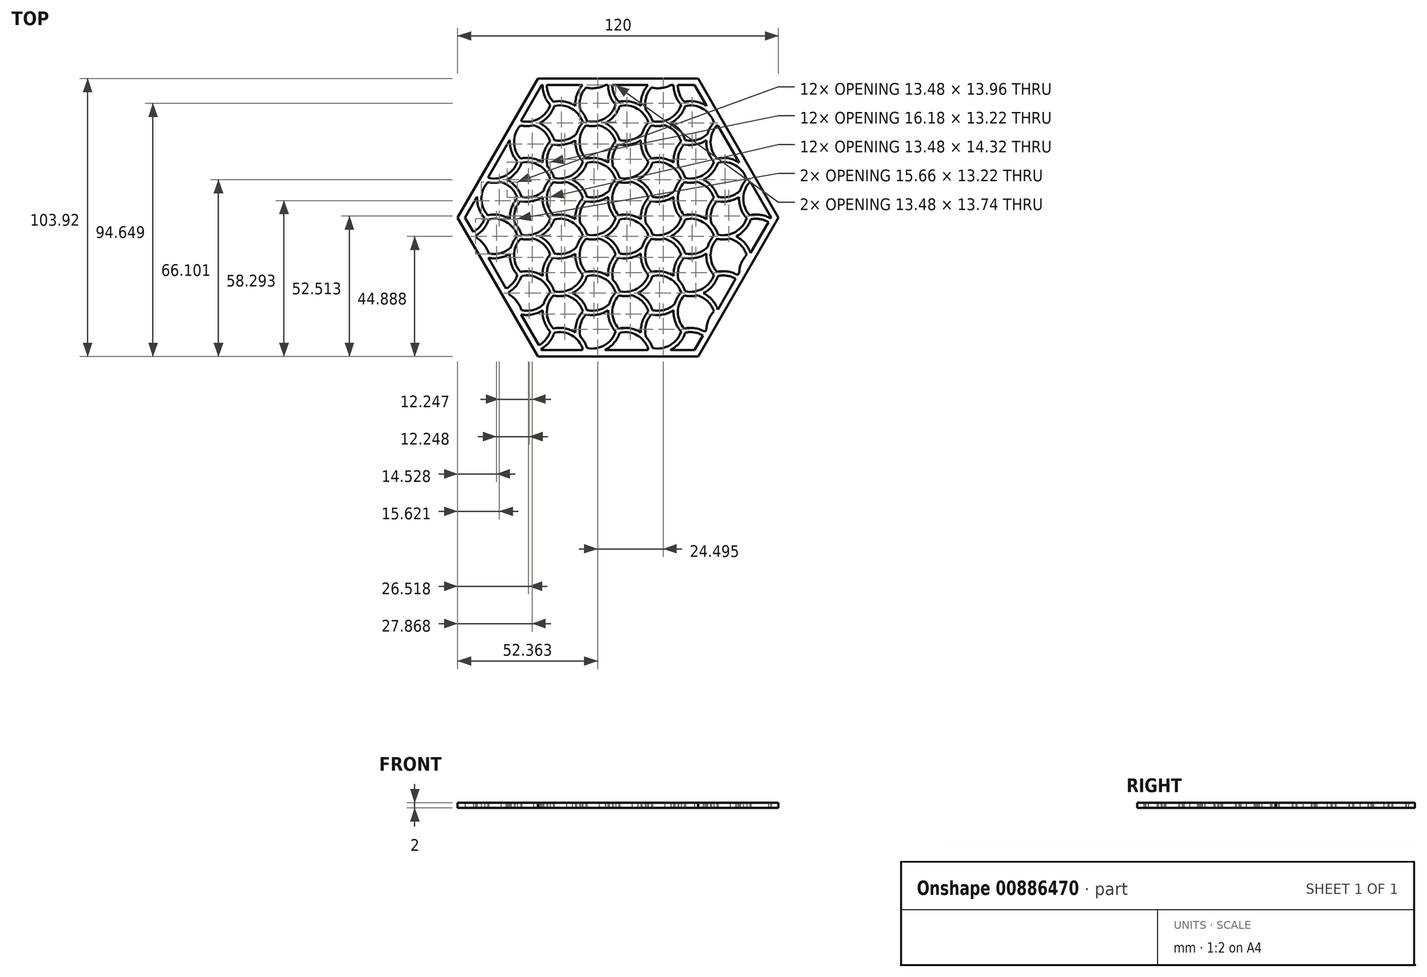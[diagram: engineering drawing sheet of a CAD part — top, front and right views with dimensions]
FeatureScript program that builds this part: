
annotation { "Feature Type Name" : "Feature", "Feature Type Description" : "" }
export const myFeature = defineFeature(function(context is Context, id is Id, definition is map)
    precondition{}
    {
        {
            var Q0;
            Q0=qCreatedBy(makeId("Top.planeOp"),FACE);
            var sketch = newSketch(context, id + "F0", { "sketchPlane" : qUnion([Q0])});
            skArc(sketch, "E0", {"start": v(0, 0) * mm, "mid": v(4.53, -0.15) * mm, "end": v(8.65, 1.7) * mm});
            skPoint(sketch, "E1.center", {"position": v(0, 0) * mm});
            skArc(sketch, "E2.1.0", {"start": v(0, 0) * mm, "mid": v(-2.13, 4) * mm, "end": v(-5.8, 6.64) * mm});
            skArc(sketch, "E2.2.0", {"start": v(0, 0) * mm, "mid": v(-2.4, -3.84) * mm, "end": v(-2.85, -8.35) * mm});
            skArc(sketch, "E3.1.0.0", {"start": v(12.25, 7.07) * mm, "mid": v(7.59, 13.14) * mm, "end": v(0, 14.14) * mm});
            skArc(sketch, "E3.1.0.2", {"start": v(12.25, 7.07) * mm, "mid": v(9.32, 0) * mm, "end": v(12.25, -7.07) * mm});
            skArc(sketch, "E4.1.0", {"start": v(-12.25, 7.07) * mm, "mid": v(-15.18, 0) * mm, "end": v(-12.25, -7.07) * mm});
            skArc(sketch, "E4.1.2", {"start": v(-12.25, 7.07) * mm, "mid": v(-4.66, 8.07) * mm, "end": v(0, 14.14) * mm});
            skArc(sketch, "E4.2.0", {"start": v(0, -14.14) * mm, "mid": v(7.59, -13.14) * mm, "end": v(12.25, -7.07) * mm});
            skArc(sketch, "E4.2.2", {"start": v(0, -14.14) * mm, "mid": v(-4.66, -8.07) * mm, "end": v(-12.25, -7.07) * mm});
            skPoint(sketch, "E4.center", {"position": v(-0.04, -0.07) * mm});
            skPoint(sketch, "E5.orphan", {"position": v(-12.25, 7.07) * mm});
            skPoint(sketch, "E6.orphan", {"position": v(0, -14.14) * mm});
            skLineSegment(sketch, "E7", {"start": v(0, 0) * mm, "end": v(9.66, 2.59) * mm, "construction": true});
            skLineSegment(sketch, "E8", {"start": v(0, 0) * mm, "end": v(-14.4, -3.86) * mm, "construction": true});
            skArc(sketch, "E9.0", {"start": v(-11.99, 6.18) * mm, "mid": v(-14.38, 0) * mm, "end": v(-11.99, -6.18) * mm});
            skArc(sketch, "E9.1", {"start": v(11.35, 7.29) * mm, "mid": v(7.19, 12.45) * mm, "end": v(0.64, 13.47) * mm});
            skArc(sketch, "E9.2", {"start": v(11.35, 7.29) * mm, "mid": v(8.52, 0) * mm, "end": v(11.35, -7.29) * mm});
            skArc(sketch, "E9.3", {"start": v(-11.99, 6.18) * mm, "mid": v(-4.26, 7.38) * mm, "end": v(0.64, 13.47) * mm});
            skArc(sketch, "E9.4", {"start": v(0.64, -13.47) * mm, "mid": v(7.19, -12.45) * mm, "end": v(11.35, -7.29) * mm});
            skArc(sketch, "E9.5", {"start": v(0.64, -13.47) * mm, "mid": v(-4.26, -7.38) * mm, "end": v(-11.99, -6.18) * mm});
            skArc(sketch, "E10.0", {"start": v(0.64, 0.67) * mm, "mid": v(-1.45, 4.42) * mm, "end": v(-4.83, 7.07) * mm});
            skArc(sketch, "E10.1", {"start": v(0.64, 0.67) * mm, "mid": v(5.08, 0.8) * mm, "end": v(8.95, 3.01) * mm});
            skArc(sketch, "E11.0", {"start": v(-0.9, 0.22) * mm, "mid": v(-3.24, 4) * mm, "end": v(-7.08, 6.24) * mm});
            skArc(sketch, "E11.1", {"start": v(-0.9, 0.22) * mm, "mid": v(-3.1, -3.46) * mm, "end": v(-3.7, -7.72) * mm});
            skArc(sketch, "E12.0", {"start": v(0.26, -0.89) * mm, "mid": v(4.55, -0.96) * mm, "end": v(8.54, 0.65) * mm});
            skArc(sketch, "E12.1", {"start": v(0.26, -0.89) * mm, "mid": v(-1.85, -4.8) * mm, "end": v(-1.87, -9.25) * mm});
            skArc(sketch, "E13.1.0.0", {"start": v(25.13, -13.47) * mm, "mid": v(20.24, -7.38) * mm, "end": v(12.5, -6.18) * mm});
            skArc(sketch, "E13.1.0.1", {"start": v(36.74, 7.07) * mm, "mid": v(32.08, 13.14) * mm, "end": v(24.5, 14.14) * mm});
            skArc(sketch, "E13.1.0.2", {"start": v(24.5, -14.14) * mm, "mid": v(19.84, -8.07) * mm, "end": v(12.25, -7.07) * mm});
            skArc(sketch, "E13.1.0.3", {"start": v(12.5, 6.18) * mm, "mid": v(10.12, 0) * mm, "end": v(12.5, -6.18) * mm});
            skArc(sketch, "E13.1.0.4", {"start": v(12.25, 7.07) * mm, "mid": v(19.84, 8.07) * mm, "end": v(24.5, 14.14) * mm});
            skArc(sketch, "E13.1.0.5", {"start": v(35.84, 7.29) * mm, "mid": v(31.68, 12.45) * mm, "end": v(25.13, 13.47) * mm});
            skArc(sketch, "E13.1.0.6", {"start": v(23.6, 0.22) * mm, "mid": v(21.26, 4) * mm, "end": v(17.41, 6.24) * mm});
            skArc(sketch, "E13.1.0.7", {"start": v(24.5, 0) * mm, "mid": v(22.1, -3.84) * mm, "end": v(21.65, -8.35) * mm});
            skPoint(sketch, "E13.1.0.8", {"position": v(12.25, 7.07) * mm});
            skArc(sketch, "E13.1.0.9", {"start": v(24.5, -14.14) * mm, "mid": v(32.08, -13.14) * mm, "end": v(36.74, -7.07) * mm});
            skLineSegment(sketch, "E13.1.0.10", {"start": v(24.5, 0) * mm, "end": v(34.15, 2.59) * mm, "construction": true});
            skArc(sketch, "E13.1.0.11", {"start": v(24.5, 0) * mm, "mid": v(22.36, 4) * mm, "end": v(18.69, 6.64) * mm});
            skArc(sketch, "E13.1.0.12", {"start": v(12.5, 6.18) * mm, "mid": v(20.24, 7.38) * mm, "end": v(25.13, 13.47) * mm});
            skArc(sketch, "E13.1.0.13", {"start": v(25.13, 0.67) * mm, "mid": v(29.58, 0.8) * mm, "end": v(33.44, 3.01) * mm});
            skArc(sketch, "E13.1.0.14", {"start": v(35.84, 7.29) * mm, "mid": v(33.01, 0) * mm, "end": v(35.84, -7.29) * mm});
            skArc(sketch, "E13.1.0.15", {"start": v(24.5, 0) * mm, "mid": v(29.02, -0.15) * mm, "end": v(33.15, 1.7) * mm});
            skArc(sketch, "E13.1.0.16", {"start": v(36.74, 7.07) * mm, "mid": v(33.81, 0) * mm, "end": v(36.74, -7.07) * mm});
            skArc(sketch, "E13.1.0.17", {"start": v(25.13, -13.47) * mm, "mid": v(31.68, -12.45) * mm, "end": v(35.84, -7.29) * mm});
            skArc(sketch, "E13.1.0.18", {"start": v(25.13, 0.67) * mm, "mid": v(23.05, 4.42) * mm, "end": v(19.67, 7.07) * mm});
            skArc(sketch, "E13.1.0.19", {"start": v(24.75, -0.89) * mm, "mid": v(29.05, -0.96) * mm, "end": v(33.03, 0.65) * mm});
            skArc(sketch, "E13.1.0.21", {"start": v(24.75, -0.89) * mm, "mid": v(22.65, -4.8) * mm, "end": v(22.63, -9.25) * mm});
            skArc(sketch, "E13.1.0.22", {"start": v(23.6, 0.22) * mm, "mid": v(21.39, -3.46) * mm, "end": v(20.79, -7.72) * mm});
            skLineSegment(sketch, "E13.1.0.23", {"start": v(24.5, 0) * mm, "end": v(10.1, -3.86) * mm, "construction": true});
            skPoint(sketch, "E13.1.0.24", {"position": v(24.5, 0) * mm});
            skPoint(sketch, "E13.1.0.25", {"position": v(24.5, -14.14) * mm});
            skPoint(sketch, "E13.1.0.26", {"position": v(24.46, -0.07) * mm});
            skPoint(sketch, "E13.1.0.27", {"position": v(24.5, 0) * mm});
            skPoint(sketch, "E13.1.0.28", {"position": v(24.5, 0) * mm});
            skPoint(sketch, "E13.1.0.29", {"position": v(24.5, 0) * mm});
            skArc(sketch, "E13.2.0.0", {"start": v(49.63, -13.47) * mm, "mid": v(44.73, -7.38) * mm, "end": v(37, -6.18) * mm});
            skArc(sketch, "E13.2.0.1", {"start": v(61.24, 7.07) * mm, "mid": v(56.58, 13.14) * mm, "end": v(48.99, 14.14) * mm});
            skArc(sketch, "E13.2.0.2", {"start": v(48.99, -14.14) * mm, "mid": v(44.33, -8.07) * mm, "end": v(36.74, -7.07) * mm});
            skArc(sketch, "E13.2.0.3", {"start": v(37, 6.18) * mm, "mid": v(34.61, 0) * mm, "end": v(37, -6.18) * mm});
            skArc(sketch, "E13.2.0.4", {"start": v(36.74, 7.07) * mm, "mid": v(44.33, 8.07) * mm, "end": v(48.99, 14.14) * mm});
            skArc(sketch, "E13.2.0.5", {"start": v(60.34, 7.29) * mm, "mid": v(56.18, 12.45) * mm, "end": v(49.63, 13.47) * mm});
            skArc(sketch, "E13.2.0.6", {"start": v(48.1, 0.22) * mm, "mid": v(45.75, 4) * mm, "end": v(41.9, 6.24) * mm});
            skArc(sketch, "E13.2.0.7", {"start": v(48.99, 0) * mm, "mid": v(46.6, -3.84) * mm, "end": v(46.14, -8.35) * mm});
            skPoint(sketch, "E13.2.0.8", {"position": v(36.74, 7.07) * mm});
            skArc(sketch, "E13.2.0.9", {"start": v(48.99, -14.14) * mm, "mid": v(56.58, -13.14) * mm, "end": v(61.24, -7.07) * mm});
            skLineSegment(sketch, "E13.2.0.10", {"start": v(48.99, 0) * mm, "end": v(58.65, 2.59) * mm, "construction": true});
            skArc(sketch, "E13.2.0.11", {"start": v(48.99, 0) * mm, "mid": v(46.86, 4) * mm, "end": v(43.18, 6.64) * mm});
            skArc(sketch, "E13.2.0.12", {"start": v(37, 6.18) * mm, "mid": v(44.73, 7.38) * mm, "end": v(49.63, 13.47) * mm});
            skArc(sketch, "E13.2.0.13", {"start": v(49.63, 0.67) * mm, "mid": v(54.07, 0.8) * mm, "end": v(57.94, 3.01) * mm});
            skArc(sketch, "E13.2.0.14", {"start": v(60.34, 7.29) * mm, "mid": v(57.5, 0) * mm, "end": v(60.34, -7.29) * mm});
            skArc(sketch, "E13.2.0.15", {"start": v(48.99, 0) * mm, "mid": v(53.52, -0.15) * mm, "end": v(57.64, 1.7) * mm});
            skArc(sketch, "E13.2.0.16", {"start": v(61.24, 7.07) * mm, "mid": v(58.3, 0) * mm, "end": v(61.24, -7.07) * mm});
            skArc(sketch, "E13.2.0.17", {"start": v(49.63, -13.47) * mm, "mid": v(56.18, -12.45) * mm, "end": v(60.34, -7.29) * mm});
            skArc(sketch, "E13.2.0.18", {"start": v(49.63, 0.67) * mm, "mid": v(47.54, 4.42) * mm, "end": v(44.16, 7.07) * mm});
            skArc(sketch, "E13.2.0.19", {"start": v(49.25, -0.89) * mm, "mid": v(53.54, -0.96) * mm, "end": v(57.53, 0.65) * mm});
            skArc(sketch, "E13.2.0.20", {"start": v(36.74, 7.07) * mm, "mid": v(33.81, 0) * mm, "end": v(36.74, -7.07) * mm});
            skArc(sketch, "E13.2.0.21", {"start": v(49.25, -0.89) * mm, "mid": v(47.14, -4.8) * mm, "end": v(47.12, -9.25) * mm});
            skArc(sketch, "E13.2.0.22", {"start": v(48.1, 0.22) * mm, "mid": v(45.88, -3.46) * mm, "end": v(45.28, -7.72) * mm});
            skLineSegment(sketch, "E13.2.0.23", {"start": v(48.99, 0) * mm, "end": v(34.59, -3.86) * mm, "construction": true});
            skPoint(sketch, "E13.2.0.24", {"position": v(48.99, 0) * mm});
            skPoint(sketch, "E13.2.0.25", {"position": v(48.99, -14.14) * mm});
            skPoint(sketch, "E13.2.0.26", {"position": v(48.95, -0.07) * mm});
            skPoint(sketch, "E13.2.0.27", {"position": v(48.99, 0) * mm});
            skPoint(sketch, "E13.2.0.28", {"position": v(48.99, 0) * mm});
            skPoint(sketch, "E13.2.0.29", {"position": v(48.99, 0) * mm});
            skLineSegment(sketch, "E13.direction1", {"start": v(-9.66, -16.73) * mm, "end": v(14.84, -16.73) * mm, "construction": true});
            skArc(sketch, "E14.0.3.0", {"start": v(74.12, -13.47) * mm, "mid": v(69.23, -7.38) * mm, "end": v(61.5, -6.18) * mm});
            skArc(sketch, "E14.4.3.0", {"start": v(85.73, 7.07) * mm, "mid": v(81.07, 13.14) * mm, "end": v(73.48, 14.14) * mm});
            skArc(sketch, "E14.8.3.0", {"start": v(73.48, -14.14) * mm, "mid": v(68.83, -8.07) * mm, "end": v(61.24, -7.07) * mm});
            skArc(sketch, "E14.12.3.0", {"start": v(61.5, 6.18) * mm, "mid": v(59.1, 0) * mm, "end": v(61.5, -6.18) * mm});
            skArc(sketch, "E14.16.3.0", {"start": v(61.24, 7.07) * mm, "mid": v(68.83, 8.07) * mm, "end": v(73.48, 14.14) * mm});
            skArc(sketch, "E14.20.3.0", {"start": v(84.83, 7.29) * mm, "mid": v(80.67, 12.45) * mm, "end": v(74.12, 13.47) * mm});
            skArc(sketch, "E14.24.3.0", {"start": v(72.59, 0.22) * mm, "mid": v(70.25, 4) * mm, "end": v(66.4, 6.24) * mm});
            skArc(sketch, "E14.28.3.0", {"start": v(73.48, 0) * mm, "mid": v(71.1, -3.84) * mm, "end": v(70.64, -8.35) * mm});
            skPoint(sketch, "E14.32.3.0", {"position": v(61.24, 7.07) * mm});
            skArc(sketch, "E14.33.3.0", {"start": v(73.48, -14.14) * mm, "mid": v(81.07, -13.14) * mm, "end": v(85.73, -7.07) * mm});
            skLineSegment(sketch, "E14.37.3.0", {"start": v(73.48, 0) * mm, "end": v(83.14, 2.59) * mm, "construction": true});
            skArc(sketch, "E14.40.3.0", {"start": v(73.48, 0) * mm, "mid": v(71.35, 4) * mm, "end": v(67.68, 6.64) * mm});
            skArc(sketch, "E14.44.3.0", {"start": v(61.5, 6.18) * mm, "mid": v(69.23, 7.38) * mm, "end": v(74.12, 13.47) * mm});
            skArc(sketch, "E14.48.3.0", {"start": v(74.12, 0.67) * mm, "mid": v(78.57, 0.8) * mm, "end": v(82.43, 3.01) * mm});
            skArc(sketch, "E14.52.3.0", {"start": v(84.83, 7.29) * mm, "mid": v(82, 0) * mm, "end": v(84.83, -7.29) * mm});
            skArc(sketch, "E14.56.3.0", {"start": v(73.48, 0) * mm, "mid": v(78.01, -0.15) * mm, "end": v(82.14, 1.7) * mm});
            skArc(sketch, "E14.60.3.0", {"start": v(85.73, 7.07) * mm, "mid": v(82.8, 0) * mm, "end": v(85.73, -7.07) * mm});
            skArc(sketch, "E14.64.3.0", {"start": v(74.12, -13.47) * mm, "mid": v(80.67, -12.45) * mm, "end": v(84.83, -7.29) * mm});
            skArc(sketch, "E14.68.3.0", {"start": v(74.12, 0.67) * mm, "mid": v(72.04, 4.42) * mm, "end": v(68.66, 7.07) * mm});
            skArc(sketch, "E14.72.3.0", {"start": v(73.74, -0.89) * mm, "mid": v(78.04, -0.96) * mm, "end": v(82.02, 0.65) * mm});
            skArc(sketch, "E14.80.3.0", {"start": v(73.74, -0.89) * mm, "mid": v(71.64, -4.8) * mm, "end": v(71.62, -9.25) * mm});
            skArc(sketch, "E14.84.3.0", {"start": v(72.59, 0.22) * mm, "mid": v(70.38, -3.46) * mm, "end": v(69.78, -7.72) * mm});
            skLineSegment(sketch, "E14.88.3.0", {"start": v(73.48, 0) * mm, "end": v(59.08, -3.86) * mm, "construction": true});
            skPoint(sketch, "E14.91.3.0", {"position": v(73.48, 0) * mm});
            skPoint(sketch, "E14.92.3.0", {"position": v(73.48, -14.14) * mm});
            skPoint(sketch, "E14.93.3.0", {"position": v(73.45, -0.07) * mm});
            skPoint(sketch, "E14.94.3.0", {"position": v(73.48, 0) * mm});
            skPoint(sketch, "E14.95.3.0", {"position": v(73.48, 0) * mm});
            skPoint(sketch, "E14.96.3.0", {"position": v(73.48, 0) * mm});
            skArc(sketch, "E14.0.4.0", {"start": v(98.62, -13.47) * mm, "mid": v(93.72, -7.38) * mm, "end": v(86, -6.18) * mm});
            skArc(sketch, "E14.4.4.0", {"start": v(110.23, 7.07) * mm, "mid": v(105.57, 13.14) * mm, "end": v(97.98, 14.14) * mm});
            skArc(sketch, "E14.8.4.0", {"start": v(97.98, -14.14) * mm, "mid": v(93.32, -8.07) * mm, "end": v(85.73, -7.07) * mm});
            skArc(sketch, "E14.12.4.0", {"start": v(86, 6.18) * mm, "mid": v(83.6, 0) * mm, "end": v(86, -6.18) * mm});
            skArc(sketch, "E14.16.4.0", {"start": v(85.73, 7.07) * mm, "mid": v(93.32, 8.07) * mm, "end": v(97.98, 14.14) * mm});
            skArc(sketch, "E14.20.4.0", {"start": v(109.33, 7.29) * mm, "mid": v(105.17, 12.45) * mm, "end": v(98.62, 13.47) * mm});
            skArc(sketch, "E14.24.4.0", {"start": v(97.08, 0.22) * mm, "mid": v(94.74, 4) * mm, "end": v(90.9, 6.24) * mm});
            skArc(sketch, "E14.28.4.0", {"start": v(97.98, 0) * mm, "mid": v(95.59, -3.84) * mm, "end": v(95.13, -8.35) * mm});
            skPoint(sketch, "E14.32.4.0", {"position": v(85.73, 7.07) * mm});
            skArc(sketch, "E14.33.4.0", {"start": v(97.98, -14.14) * mm, "mid": v(105.57, -13.14) * mm, "end": v(110.23, -7.07) * mm});
            skLineSegment(sketch, "E14.37.4.0", {"start": v(97.98, 0) * mm, "end": v(107.64, 2.59) * mm, "construction": true});
            skArc(sketch, "E14.40.4.0", {"start": v(97.98, 0) * mm, "mid": v(95.85, 4) * mm, "end": v(92.17, 6.64) * mm});
            skArc(sketch, "E14.44.4.0", {"start": v(86, 6.18) * mm, "mid": v(93.72, 7.38) * mm, "end": v(98.62, 13.47) * mm});
            skArc(sketch, "E14.48.4.0", {"start": v(98.62, 0.67) * mm, "mid": v(103.06, 0.8) * mm, "end": v(106.93, 3.01) * mm});
            skArc(sketch, "E14.52.4.0", {"start": v(109.33, 7.29) * mm, "mid": v(106.5, 0) * mm, "end": v(109.33, -7.29) * mm});
            skArc(sketch, "E14.56.4.0", {"start": v(97.98, 0) * mm, "mid": v(102.5, -0.15) * mm, "end": v(106.63, 1.7) * mm});
            skArc(sketch, "E14.60.4.0", {"start": v(110.23, 7.07) * mm, "mid": v(107.3, 0) * mm, "end": v(110.23, -7.07) * mm});
            skArc(sketch, "E14.64.4.0", {"start": v(98.62, -13.47) * mm, "mid": v(105.17, -12.45) * mm, "end": v(109.33, -7.29) * mm});
            skArc(sketch, "E14.68.4.0", {"start": v(98.62, 0.67) * mm, "mid": v(96.53, 4.42) * mm, "end": v(93.15, 7.07) * mm});
            skArc(sketch, "E14.72.4.0", {"start": v(98.24, -0.89) * mm, "mid": v(102.53, -0.96) * mm, "end": v(106.52, 0.65) * mm});
            skArc(sketch, "E14.76.4.0", {"start": v(85.73, 7.07) * mm, "mid": v(82.8, 0) * mm, "end": v(85.73, -7.07) * mm});
            skArc(sketch, "E14.80.4.0", {"start": v(98.24, -0.89) * mm, "mid": v(96.13, -4.8) * mm, "end": v(96.11, -9.25) * mm});
            skArc(sketch, "E14.84.4.0", {"start": v(97.08, 0.22) * mm, "mid": v(94.87, -3.46) * mm, "end": v(94.27, -7.72) * mm});
            skLineSegment(sketch, "E14.88.4.0", {"start": v(97.98, 0) * mm, "end": v(83.58, -3.86) * mm, "construction": true});
            skPoint(sketch, "E14.91.4.0", {"position": v(97.98, 0) * mm});
            skPoint(sketch, "E14.92.4.0", {"position": v(97.98, -14.14) * mm});
            skPoint(sketch, "E14.93.4.0", {"position": v(97.94, -0.07) * mm});
            skPoint(sketch, "E14.94.4.0", {"position": v(97.98, 0) * mm});
            skPoint(sketch, "E14.95.4.0", {"position": v(97.98, 0) * mm});
            skPoint(sketch, "E14.96.4.0", {"position": v(97.98, 0) * mm});
            skArc(sketch, "E14.0.5.0", {"start": v(123.11, -13.47) * mm, "mid": v(118.22, -7.38) * mm, "end": v(110.49, -6.18) * mm});
            skArc(sketch, "E14.4.5.0", {"start": v(134.72, 7.07) * mm, "mid": v(130.06, 13.14) * mm, "end": v(122.47, 14.14) * mm});
            skArc(sketch, "E14.8.5.0", {"start": v(122.47, -14.14) * mm, "mid": v(117.82, -8.07) * mm, "end": v(110.23, -7.07) * mm});
            skArc(sketch, "E14.12.5.0", {"start": v(110.49, 6.18) * mm, "mid": v(108.1, 0) * mm, "end": v(110.49, -6.18) * mm});
            skArc(sketch, "E14.16.5.0", {"start": v(110.23, 7.07) * mm, "mid": v(117.82, 8.07) * mm, "end": v(122.47, 14.14) * mm});
            skArc(sketch, "E14.20.5.0", {"start": v(133.82, 7.29) * mm, "mid": v(129.66, 12.45) * mm, "end": v(123.11, 13.47) * mm});
            skArc(sketch, "E14.24.5.0", {"start": v(121.58, 0.22) * mm, "mid": v(119.24, 4) * mm, "end": v(115.4, 6.24) * mm});
            skArc(sketch, "E14.28.5.0", {"start": v(122.47, 0) * mm, "mid": v(120.08, -3.84) * mm, "end": v(119.63, -8.35) * mm});
            skPoint(sketch, "E14.32.5.0", {"position": v(110.23, 7.07) * mm});
            skArc(sketch, "E14.33.5.0", {"start": v(122.47, -14.14) * mm, "mid": v(130.06, -13.14) * mm, "end": v(134.72, -7.07) * mm});
            skLineSegment(sketch, "E14.37.5.0", {"start": v(122.47, 0) * mm, "end": v(132.13, 2.59) * mm, "construction": true});
            skArc(sketch, "E14.40.5.0", {"start": v(122.47, 0) * mm, "mid": v(120.34, 4) * mm, "end": v(116.67, 6.64) * mm});
            skArc(sketch, "E14.44.5.0", {"start": v(110.49, 6.18) * mm, "mid": v(118.22, 7.38) * mm, "end": v(123.11, 13.47) * mm});
            skArc(sketch, "E14.48.5.0", {"start": v(123.11, 0.67) * mm, "mid": v(127.56, 0.8) * mm, "end": v(131.42, 3.01) * mm});
            skArc(sketch, "E14.52.5.0", {"start": v(133.82, 7.29) * mm, "mid": v(131, 0) * mm, "end": v(133.82, -7.29) * mm});
            skArc(sketch, "E14.56.5.0", {"start": v(122.47, 0) * mm, "mid": v(127, -0.15) * mm, "end": v(131.13, 1.7) * mm});
            skArc(sketch, "E14.60.5.0", {"start": v(134.72, 7.07) * mm, "mid": v(131.8, 0) * mm, "end": v(134.72, -7.07) * mm});
            skArc(sketch, "E14.64.5.0", {"start": v(123.11, -13.47) * mm, "mid": v(129.66, -12.45) * mm, "end": v(133.82, -7.29) * mm});
            skArc(sketch, "E14.68.5.0", {"start": v(123.11, 0.67) * mm, "mid": v(121.03, 4.42) * mm, "end": v(117.65, 7.07) * mm});
            skArc(sketch, "E14.72.5.0", {"start": v(122.73, -0.89) * mm, "mid": v(127.03, -0.96) * mm, "end": v(131.01, 0.65) * mm});
            skArc(sketch, "E14.76.5.0", {"start": v(110.23, 7.07) * mm, "mid": v(107.3, 0) * mm, "end": v(110.23, -7.07) * mm});
            skArc(sketch, "E14.80.5.0", {"start": v(122.73, -0.89) * mm, "mid": v(120.63, -4.8) * mm, "end": v(120.6, -9.25) * mm});
            skArc(sketch, "E14.84.5.0", {"start": v(121.58, 0.22) * mm, "mid": v(119.37, -3.46) * mm, "end": v(118.76, -7.72) * mm});
            skLineSegment(sketch, "E14.88.5.0", {"start": v(122.47, 0) * mm, "end": v(108.07, -3.86) * mm, "construction": true});
            skPoint(sketch, "E14.91.5.0", {"position": v(122.47, 0) * mm});
            skPoint(sketch, "E14.92.5.0", {"position": v(122.47, -14.14) * mm});
            skPoint(sketch, "E14.93.5.0", {"position": v(122.44, -0.07) * mm});
            skPoint(sketch, "E14.94.5.0", {"position": v(122.47, 0) * mm});
            skPoint(sketch, "E14.95.5.0", {"position": v(122.47, 0) * mm});
            skPoint(sketch, "E14.96.5.0", {"position": v(122.47, 0) * mm});
            skLineSegment(sketch, "E15.0.1.0", {"start": v(110.23, 21.21) * mm, "end": v(119.89, 23.8) * mm, "construction": true});
            skArc(sketch, "E15.0.1.1", {"start": v(-24.24, 27.4) * mm, "mid": v(-26.62, 21.21) * mm, "end": v(-24.24, 15.03) * mm});
            skArc(sketch, "E15.0.1.2", {"start": v(110.49, 20.33) * mm, "mid": v(108.38, 16.4) * mm, "end": v(108.36, 11.96) * mm});
            skArc(sketch, "E15.0.1.3", {"start": v(-12.25, 21.21) * mm, "mid": v(-14.64, 17.37) * mm, "end": v(-15.1, 12.86) * mm});
            skLineSegment(sketch, "E15.0.1.4", {"start": v(61.24, 21.21) * mm, "end": v(46.84, 17.35) * mm, "construction": true});
            skPoint(sketch, "E15.0.1.5", {"position": v(36.74, 21.21) * mm});
            skLineSegment(sketch, "E15.0.1.6", {"start": v(85.73, 21.21) * mm, "end": v(95.4, 23.8) * mm, "construction": true});
            skArc(sketch, "E15.0.1.7", {"start": v(12.89, 21.88) * mm, "mid": v(17.33, 22.02) * mm, "end": v(21.2, 24.22) * mm});
            skArc(sketch, "E15.0.1.8", {"start": v(12.89, 21.88) * mm, "mid": v(10.8, 25.64) * mm, "end": v(7.42, 28.28) * mm});
            skArc(sketch, "E15.0.1.9", {"start": v(23.6, 28.5) * mm, "mid": v(20.77, 21.21) * mm, "end": v(23.6, 13.92) * mm});
            skArc(sketch, "E15.0.1.10", {"start": v(-0.9, 28.5) * mm, "mid": v(-3.73, 21.21) * mm, "end": v(-0.9, 13.92) * mm});
            skArc(sketch, "E15.0.1.11", {"start": v(61.88, 21.88) * mm, "mid": v(66.32, 22.02) * mm, "end": v(70.18, 24.22) * mm});
            skArc(sketch, "E15.0.1.12", {"start": v(110.87, 7.74) * mm, "mid": v(105.97, 13.84) * mm, "end": v(98.24, 15.03) * mm});
            skArc(sketch, "E15.0.1.13", {"start": v(86, 20.33) * mm, "mid": v(83.89, 16.4) * mm, "end": v(83.87, 11.96) * mm});
            skArc(sketch, "E15.0.1.14", {"start": v(37, 20.33) * mm, "mid": v(34.9, 16.4) * mm, "end": v(34.88, 11.96) * mm});
            skArc(sketch, "E15.0.1.15", {"start": v(72.59, 28.5) * mm, "mid": v(69.76, 21.21) * mm, "end": v(72.59, 13.92) * mm});
            skArc(sketch, "E15.0.1.16", {"start": v(97.08, 28.5) * mm, "mid": v(92.92, 33.66) * mm, "end": v(86.37, 34.69) * mm});
            skArc(sketch, "E15.0.1.17", {"start": v(12.25, 21.21) * mm, "mid": v(9.85, 17.37) * mm, "end": v(9.4, 12.86) * mm});
            skArc(sketch, "E15.0.1.19", {"start": v(85.73, 21.21) * mm, "mid": v(83.6, 25.2) * mm, "end": v(79.92, 27.85) * mm});
            skArc(sketch, "E15.0.1.20", {"start": v(35.84, 21.43) * mm, "mid": v(33.63, 17.75) * mm, "end": v(33.03, 13.5) * mm});
            skArc(sketch, "E15.0.1.21", {"start": v(61.5, 20.33) * mm, "mid": v(59.4, 16.4) * mm, "end": v(59.37, 11.96) * mm});
            skArc(sketch, "E15.0.1.22", {"start": v(-11.6, 7.74) * mm, "mid": v(-5.06, 8.76) * mm, "end": v(-0.9, 13.92) * mm});
            skArc(sketch, "E15.0.1.23", {"start": v(110.23, 21.21) * mm, "mid": v(114.75, 21.06) * mm, "end": v(118.88, 22.92) * mm});
            skArc(sketch, "E15.0.1.24", {"start": v(36.74, 21.21) * mm, "mid": v(34.61, 25.2) * mm, "end": v(30.93, 27.85) * mm});
            skArc(sketch, "E15.0.1.25", {"start": v(24.5, 28.28) * mm, "mid": v(19.84, 34.36) * mm, "end": v(12.25, 35.36) * mm});
            skArc(sketch, "E15.0.1.26", {"start": v(86.37, 21.88) * mm, "mid": v(90.82, 22.02) * mm, "end": v(94.68, 24.22) * mm});
            skArc(sketch, "E15.0.1.27", {"start": v(12.89, 7.74) * mm, "mid": v(7.99, 13.84) * mm, "end": v(0.26, 15.03) * mm});
            skArc(sketch, "E15.0.1.28", {"start": v(60.34, 21.43) * mm, "mid": v(58.13, 17.75) * mm, "end": v(57.53, 13.5) * mm});
            skLineSegment(sketch, "E15.0.1.30", {"start": v(36.74, 21.21) * mm, "end": v(22.34, 17.35) * mm, "construction": true});
            skArc(sketch, "E15.0.1.31", {"start": v(72.59, 28.5) * mm, "mid": v(68.43, 33.66) * mm, "end": v(61.88, 34.69) * mm});
            skArc(sketch, "E15.0.1.32", {"start": v(11.35, 21.43) * mm, "mid": v(9.14, 17.75) * mm, "end": v(8.54, 13.5) * mm});
            skArc(sketch, "E15.0.1.33", {"start": v(12.5, 20.33) * mm, "mid": v(10.4, 16.4) * mm, "end": v(10.38, 11.96) * mm});
            skArc(sketch, "E15.0.1.34", {"start": v(97.08, 28.5) * mm, "mid": v(94.25, 21.21) * mm, "end": v(97.08, 13.92) * mm});
            skArc(sketch, "E15.0.1.35", {"start": v(97.98, 28.28) * mm, "mid": v(93.32, 34.36) * mm, "end": v(85.73, 35.36) * mm});
            skArc(sketch, "E15.0.1.36", {"start": v(-12.25, 7.07) * mm, "mid": v(-16.9, 13.14) * mm, "end": v(-24.5, 14.14) * mm});
            skArc(sketch, "E15.0.1.37", {"start": v(24.5, 28.28) * mm, "mid": v(32.08, 29.28) * mm, "end": v(36.74, 35.36) * mm});
            skArc(sketch, "E15.0.1.39", {"start": v(-24.5, 28.28) * mm, "mid": v(-16.9, 29.28) * mm, "end": v(-12.25, 35.36) * mm});
            skArc(sketch, "E15.0.1.40", {"start": v(23.6, 28.5) * mm, "mid": v(19.44, 33.66) * mm, "end": v(12.89, 34.69) * mm});
            skArc(sketch, "E15.0.1.41", {"start": v(110.23, 21.21) * mm, "mid": v(108.1, 25.2) * mm, "end": v(104.42, 27.85) * mm});
            skPoint(sketch, "E15.0.1.44", {"position": v(97.98, 28.28) * mm});
            skArc(sketch, "E15.0.1.46", {"start": v(12.89, 7.74) * mm, "mid": v(19.44, 8.76) * mm, "end": v(23.6, 13.92) * mm});
            skArc(sketch, "E15.0.1.47", {"start": v(-11.6, 7.74) * mm, "mid": v(-16.5, 13.84) * mm, "end": v(-24.24, 15.03) * mm});
            skArc(sketch, "E15.0.1.48", {"start": v(121.58, 28.5) * mm, "mid": v(118.75, 21.21) * mm, "end": v(121.58, 13.92) * mm});
            skArc(sketch, "E15.0.1.49", {"start": v(37.38, 7.74) * mm, "mid": v(32.48, 13.84) * mm, "end": v(24.75, 15.03) * mm});
            skArc(sketch, "E15.0.1.50", {"start": v(-0.9, 28.5) * mm, "mid": v(-5.06, 33.66) * mm, "end": v(-11.6, 34.69) * mm});
            skArc(sketch, "E15.0.1.51", {"start": v(86.37, 7.74) * mm, "mid": v(92.92, 8.76) * mm, "end": v(97.08, 13.92) * mm});
            skArc(sketch, "E15.0.1.52", {"start": v(84.83, 21.43) * mm, "mid": v(82.5, 25.21) * mm, "end": v(78.65, 27.46) * mm});
            skArc(sketch, "E15.0.1.55", {"start": v(-12.25, 21.21) * mm, "mid": v(-7.72, 21.06) * mm, "end": v(-3.6, 22.92) * mm});
            skArc(sketch, "E15.0.1.56", {"start": v(12.25, 21.21) * mm, "mid": v(10.12, 25.2) * mm, "end": v(6.44, 27.85) * mm});
            skArc(sketch, "E15.0.1.57", {"start": v(85.73, 21.21) * mm, "mid": v(83.34, 17.37) * mm, "end": v(82.89, 12.86) * mm});
            skArc(sketch, "E15.0.1.58", {"start": v(-24.5, 28.28) * mm, "mid": v(-27.42, 21.21) * mm, "end": v(-24.5, 14.14) * mm});
            skArc(sketch, "E15.0.1.59", {"start": v(-11.6, 21.88) * mm, "mid": v(-13.7, 25.64) * mm, "end": v(-17.08, 28.28) * mm});
            skPoint(sketch, "E15.0.1.61", {"position": v(-12.25, 21.21) * mm});
            skLineSegment(sketch, "E15.0.1.62", {"start": v(61.24, 21.21) * mm, "end": v(70.9, 23.8) * mm, "construction": true});
            skArc(sketch, "E15.0.1.63", {"start": v(48.1, 28.5) * mm, "mid": v(45.26, 21.21) * mm, "end": v(48.1, 13.92) * mm});
            skArc(sketch, "E15.0.1.64", {"start": v(-11.99, 20.33) * mm, "mid": v(-14.1, 16.4) * mm, "end": v(-14.11, 11.96) * mm});
            skArc(sketch, "E15.0.1.65", {"start": v(98.24, 27.4) * mm, "mid": v(95.85, 21.21) * mm, "end": v(98.24, 15.03) * mm});
            skArc(sketch, "E15.0.1.66", {"start": v(86, 20.33) * mm, "mid": v(90.29, 20.25) * mm, "end": v(94.27, 21.86) * mm});
            skArc(sketch, "E15.0.1.67", {"start": v(-11.6, 21.88) * mm, "mid": v(-7.16, 22.02) * mm, "end": v(-3.3, 24.22) * mm});
            skArc(sketch, "E15.0.1.68", {"start": v(110.87, 21.88) * mm, "mid": v(115.31, 22.02) * mm, "end": v(119.17, 24.22) * mm});
            skArc(sketch, "E15.0.1.70", {"start": v(37.38, 7.74) * mm, "mid": v(43.93, 8.76) * mm, "end": v(48.1, 13.92) * mm});
            skArc(sketch, "E15.0.1.71", {"start": v(73.74, 27.4) * mm, "mid": v(81.47, 28.6) * mm, "end": v(86.37, 34.69) * mm});
            skArc(sketch, "E15.0.1.72", {"start": v(122.47, 28.28) * mm, "mid": v(119.55, 21.21) * mm, "end": v(122.47, 14.14) * mm});
            skPoint(sketch, "E15.0.1.73", {"position": v(85.73, 21.21) * mm});
            skArc(sketch, "E15.0.1.74", {"start": v(73.74, 27.4) * mm, "mid": v(71.36, 21.21) * mm, "end": v(73.74, 15.03) * mm});
            skArc(sketch, "E15.0.1.75", {"start": v(61.88, 21.88) * mm, "mid": v(59.8, 25.64) * mm, "end": v(56.4, 28.28) * mm});
            skPoint(sketch, "E15.0.1.76", {"position": v(24.5, 28.28) * mm});
            skArc(sketch, "E15.0.1.77", {"start": v(48.1, 28.5) * mm, "mid": v(43.93, 33.66) * mm, "end": v(37.38, 34.69) * mm});
            skLineSegment(sketch, "E15.0.1.78", {"start": v(110.23, 21.21) * mm, "end": v(95.83, 17.35) * mm, "construction": true});
            skArc(sketch, "E15.0.1.79", {"start": v(86.37, 21.88) * mm, "mid": v(84.29, 25.64) * mm, "end": v(80.9, 28.28) * mm});
            skArc(sketch, "E15.0.1.80", {"start": v(110.87, 21.88) * mm, "mid": v(108.78, 25.64) * mm, "end": v(105.4, 28.28) * mm});
            skPoint(sketch, "E15.0.1.81", {"position": v(48.99, 28.28) * mm});
            skLineSegment(sketch, "E15.0.1.82", {"start": v(-12.25, 21.21) * mm, "end": v(-26.65, 17.35) * mm, "construction": true});
            skArc(sketch, "E15.0.1.83", {"start": v(110.49, 20.33) * mm, "mid": v(114.78, 20.25) * mm, "end": v(118.76, 21.86) * mm});
            skArc(sketch, "E15.0.1.84", {"start": v(84.83, 21.43) * mm, "mid": v(82.62, 17.75) * mm, "end": v(82.02, 13.5) * mm});
            skArc(sketch, "E15.0.1.85", {"start": v(24.75, 27.4) * mm, "mid": v(32.48, 28.6) * mm, "end": v(37.38, 34.69) * mm});
            skArc(sketch, "E15.0.1.86", {"start": v(37, 20.33) * mm, "mid": v(41.3, 20.25) * mm, "end": v(45.28, 21.86) * mm});
            skArc(sketch, "E15.0.1.87", {"start": v(86.37, 7.74) * mm, "mid": v(81.47, 13.84) * mm, "end": v(73.74, 15.03) * mm});
            skArc(sketch, "E15.0.1.88", {"start": v(12.5, 20.33) * mm, "mid": v(16.8, 20.25) * mm, "end": v(20.79, 21.86) * mm});
            skArc(sketch, "E15.0.1.89", {"start": v(73.48, 28.28) * mm, "mid": v(68.83, 34.36) * mm, "end": v(61.24, 35.36) * mm});
            skArc(sketch, "E15.0.1.91", {"start": v(60.34, 21.43) * mm, "mid": v(58, 25.21) * mm, "end": v(54.16, 27.46) * mm});
            skArc(sketch, "E15.0.1.92", {"start": v(-12.25, 21.21) * mm, "mid": v(-14.38, 25.2) * mm, "end": v(-18.06, 27.85) * mm});
            skArc(sketch, "E15.0.1.93", {"start": v(61.24, 21.21) * mm, "mid": v(58.84, 17.37) * mm, "end": v(58.4, 12.86) * mm});
            skArc(sketch, "E15.0.1.94", {"start": v(109.33, 21.43) * mm, "mid": v(107.12, 17.75) * mm, "end": v(106.52, 13.5) * mm});
            skArc(sketch, "E15.0.1.95", {"start": v(37.38, 21.88) * mm, "mid": v(41.83, 22.02) * mm, "end": v(45.69, 24.22) * mm});
            skArc(sketch, "E15.0.1.96", {"start": v(121.58, 28.5) * mm, "mid": v(117.42, 33.66) * mm, "end": v(110.87, 34.69) * mm});
            skArc(sketch, "E15.0.1.97", {"start": v(-13.15, 21.43) * mm, "mid": v(-15.36, 17.75) * mm, "end": v(-15.96, 13.5) * mm});
            skArc(sketch, "E15.0.1.98", {"start": v(110.87, 7.74) * mm, "mid": v(117.42, 8.76) * mm, "end": v(121.58, 13.92) * mm});
            skArc(sketch, "E15.0.1.99", {"start": v(37.38, 21.88) * mm, "mid": v(35.3, 25.64) * mm, "end": v(31.91, 28.28) * mm});
            skArc(sketch, "E15.0.1.100", {"start": v(0.26, 27.4) * mm, "mid": v(7.99, 28.6) * mm, "end": v(12.89, 34.69) * mm});
            skArc(sketch, "E15.0.1.101", {"start": v(122.47, 28.28) * mm, "mid": v(117.82, 34.36) * mm, "end": v(110.23, 35.36) * mm});
            skArc(sketch, "E15.0.1.102", {"start": v(0, 28.28) * mm, "mid": v(-4.66, 34.36) * mm, "end": v(-12.25, 35.36) * mm});
            skArc(sketch, "E15.0.1.103", {"start": v(36.74, 21.21) * mm, "mid": v(41.27, 21.06) * mm, "end": v(45.4, 22.92) * mm});
            skArc(sketch, "E15.0.1.105", {"start": v(-24.24, 27.4) * mm, "mid": v(-16.5, 28.6) * mm, "end": v(-11.6, 34.69) * mm});
            skArc(sketch, "E15.0.1.106", {"start": v(0, 28.28) * mm, "mid": v(7.59, 29.28) * mm, "end": v(12.25, 35.36) * mm});
            skArc(sketch, "E15.0.1.107", {"start": v(49.25, 27.4) * mm, "mid": v(46.86, 21.21) * mm, "end": v(49.25, 15.03) * mm});
            skArc(sketch, "E15.0.1.108", {"start": v(73.48, 28.28) * mm, "mid": v(81.07, 29.28) * mm, "end": v(85.73, 35.36) * mm});
            skArc(sketch, "E15.0.1.109", {"start": v(48.99, 28.28) * mm, "mid": v(56.58, 29.28) * mm, "end": v(61.24, 35.36) * mm});
            skPoint(sketch, "E15.0.1.110", {"position": v(0, 28.28) * mm});
            skArc(sketch, "E15.0.1.112", {"start": v(48.99, 28.28) * mm, "mid": v(44.33, 34.36) * mm, "end": v(36.74, 35.36) * mm});
            skLineSegment(sketch, "E15.0.1.113", {"start": v(85.73, 21.21) * mm, "end": v(71.33, 17.35) * mm, "construction": true});
            skArc(sketch, "E15.0.1.115", {"start": v(-11.99, 20.33) * mm, "mid": v(-7.7, 20.25) * mm, "end": v(-3.7, 21.86) * mm});
            skArc(sketch, "E15.0.1.118", {"start": v(49.25, 27.4) * mm, "mid": v(56.98, 28.6) * mm, "end": v(61.88, 34.69) * mm});
            skLineSegment(sketch, "E15.0.1.120", {"start": v(12.25, 21.21) * mm, "end": v(-2.15, 17.35) * mm, "construction": true});
            skArc(sketch, "E15.0.1.121", {"start": v(61.5, 20.33) * mm, "mid": v(65.8, 20.25) * mm, "end": v(69.78, 21.86) * mm});
            skArc(sketch, "E15.0.1.122", {"start": v(36.74, 21.21) * mm, "mid": v(34.35, 17.37) * mm, "end": v(33.9, 12.86) * mm});
            skArc(sketch, "E15.0.1.123", {"start": v(97.98, 28.28) * mm, "mid": v(105.57, 29.28) * mm, "end": v(110.23, 35.36) * mm});
            skPoint(sketch, "E15.0.1.124", {"position": v(73.48, 28.28) * mm});
            skArc(sketch, "E15.0.1.125", {"start": v(-13.15, 21.43) * mm, "mid": v(-15.49, 25.21) * mm, "end": v(-19.33, 27.46) * mm});
            skPoint(sketch, "E15.0.1.126", {"position": v(-24.5, 28.28) * mm});
            skLineSegment(sketch, "E15.0.1.127", {"start": v(-12.25, 21.21) * mm, "end": v(-2.59, 23.8) * mm, "construction": true});
            skArc(sketch, "E15.0.1.128", {"start": v(0, 28.28) * mm, "mid": v(-2.93, 21.21) * mm, "end": v(0, 14.14) * mm});
            skPoint(sketch, "E15.0.1.129", {"position": v(-12.28, 21.14) * mm});
            skArc(sketch, "E15.0.1.130", {"start": v(85.73, 21.21) * mm, "mid": v(90.26, 21.06) * mm, "end": v(94.39, 22.92) * mm});
            skArc(sketch, "E15.0.1.131", {"start": v(35.84, 21.43) * mm, "mid": v(33.5, 25.21) * mm, "end": v(29.66, 27.46) * mm});
            skArc(sketch, "E15.0.1.132", {"start": v(61.88, 7.74) * mm, "mid": v(68.43, 8.76) * mm, "end": v(72.59, 13.92) * mm});
            skLineSegment(sketch, "E15.0.1.133", {"start": v(-21.9, 4.48) * mm, "end": v(2.59, 4.48) * mm, "construction": true});
            skArc(sketch, "E15.0.1.134", {"start": v(73.48, 28.28) * mm, "mid": v(70.56, 21.21) * mm, "end": v(73.48, 14.14) * mm});
            skArc(sketch, "E15.0.1.135", {"start": v(109.33, 21.43) * mm, "mid": v(106.99, 25.21) * mm, "end": v(103.15, 27.46) * mm});
            skArc(sketch, "E15.0.1.136", {"start": v(61.24, 21.21) * mm, "mid": v(59.1, 25.2) * mm, "end": v(55.43, 27.85) * mm});
            skArc(sketch, "E15.0.1.137", {"start": v(24.5, 28.28) * mm, "mid": v(21.57, 21.21) * mm, "end": v(24.5, 14.14) * mm});
            skLineSegment(sketch, "E15.0.1.138", {"start": v(12.25, 21.21) * mm, "end": v(21.9, 23.8) * mm, "construction": true});
            skPoint(sketch, "E15.0.1.139", {"position": v(61.24, 21.21) * mm});
            skLineSegment(sketch, "E15.0.1.140", {"start": v(36.74, 21.21) * mm, "end": v(46.4, 23.8) * mm, "construction": true});
            skArc(sketch, "E15.0.1.141", {"start": v(48.99, 28.28) * mm, "mid": v(46.06, 21.21) * mm, "end": v(48.99, 14.14) * mm});
            skArc(sketch, "E15.0.1.142", {"start": v(110.23, 21.21) * mm, "mid": v(107.83, 17.37) * mm, "end": v(107.38, 12.86) * mm});
            skArc(sketch, "E15.0.1.143", {"start": v(0.26, 27.4) * mm, "mid": v(-2.13, 21.21) * mm, "end": v(0.26, 15.03) * mm});
            skArc(sketch, "E15.0.1.144", {"start": v(61.88, 7.74) * mm, "mid": v(56.98, 13.84) * mm, "end": v(49.25, 15.03) * mm});
            skArc(sketch, "E15.0.1.145", {"start": v(61.24, 21.21) * mm, "mid": v(65.76, 21.06) * mm, "end": v(69.9, 22.92) * mm});
            skArc(sketch, "E15.0.1.146", {"start": v(97.98, 28.28) * mm, "mid": v(95.05, 21.21) * mm, "end": v(97.98, 14.14) * mm});
            skArc(sketch, "E15.0.1.147", {"start": v(24.75, 27.4) * mm, "mid": v(22.37, 21.21) * mm, "end": v(24.75, 15.03) * mm});
            skPoint(sketch, "E15.0.1.148", {"position": v(110.23, 21.21) * mm});
            skPoint(sketch, "E15.0.1.149", {"position": v(12.25, 21.21) * mm});
            skArc(sketch, "E15.0.1.150", {"start": v(12.25, 21.21) * mm, "mid": v(16.77, 21.06) * mm, "end": v(20.9, 22.92) * mm});
            skArc(sketch, "E15.0.1.151", {"start": v(98.24, 27.4) * mm, "mid": v(105.97, 28.6) * mm, "end": v(110.87, 34.69) * mm});
            skArc(sketch, "E15.0.1.152", {"start": v(11.35, 21.43) * mm, "mid": v(9, 25.21) * mm, "end": v(5.17, 27.46) * mm});
            skArc(sketch, "E15.0.1.153", {"start": v(24.5, 28.28) * mm, "mid": v(21.57, 21.21) * mm, "end": v(24.5, 14.14) * mm});
            skPoint(sketch, "E15.0.1.154", {"position": v(61.24, 21.21) * mm});
            skArc(sketch, "E15.0.1.155", {"start": v(97.98, 28.28) * mm, "mid": v(95.05, 21.21) * mm, "end": v(97.98, 14.14) * mm});
            skPoint(sketch, "E15.0.1.156", {"position": v(110.23, 21.21) * mm});
            skArc(sketch, "E15.0.1.157", {"start": v(0, 28.28) * mm, "mid": v(-2.93, 21.21) * mm, "end": v(0, 14.14) * mm});
            skPoint(sketch, "E15.0.1.158", {"position": v(36.74, 21.21) * mm});
            skArc(sketch, "E15.0.1.159", {"start": v(48.99, 28.28) * mm, "mid": v(46.06, 21.21) * mm, "end": v(48.99, 14.14) * mm});
            skArc(sketch, "E15.0.1.160", {"start": v(73.48, 28.28) * mm, "mid": v(70.56, 21.21) * mm, "end": v(73.48, 14.14) * mm});
            skPoint(sketch, "E15.0.1.161", {"position": v(-12.25, 21.21) * mm});
            skPoint(sketch, "E15.0.1.162", {"position": v(12.25, 21.21) * mm});
            skPoint(sketch, "E15.0.1.163", {"position": v(85.73, 21.21) * mm});
            skPoint(sketch, "E15.0.1.164", {"position": v(110.23, 21.21) * mm});
            skPoint(sketch, "E15.0.1.165", {"position": v(85.73, 21.21) * mm});
            skPoint(sketch, "E15.0.1.166", {"position": v(12.25, 21.21) * mm});
            skPoint(sketch, "E15.0.1.167", {"position": v(61.24, 21.21) * mm});
            skPoint(sketch, "E15.0.1.168", {"position": v(-12.25, 21.21) * mm});
            skPoint(sketch, "E15.0.1.169", {"position": v(36.74, 21.21) * mm});
            skPoint(sketch, "E15.0.1.170", {"position": v(110.23, 21.21) * mm});
            skPoint(sketch, "E15.0.1.171", {"position": v(12.25, 21.21) * mm});
            skPoint(sketch, "E15.0.1.172", {"position": v(-12.25, 21.21) * mm});
            skPoint(sketch, "E15.0.1.173", {"position": v(85.73, 21.21) * mm});
            skPoint(sketch, "E15.0.1.174", {"position": v(36.74, 21.21) * mm});
            skPoint(sketch, "E15.0.1.175", {"position": v(61.2, 21.14) * mm});
            skPoint(sketch, "E15.0.1.176", {"position": v(36.7, 21.14) * mm});
            skPoint(sketch, "E15.0.1.177", {"position": v(110.2, 21.14) * mm});
            skPoint(sketch, "E15.0.1.178", {"position": v(61.24, 21.21) * mm});
            skPoint(sketch, "E15.0.1.179", {"position": v(85.7, 21.14) * mm});
            skPoint(sketch, "E15.0.1.180", {"position": v(12.21, 21.14) * mm});
            skLineSegment(sketch, "E15.0.2.0", {"start": v(97.98, 42.43) * mm, "end": v(107.64, 45.01) * mm, "construction": true});
            skArc(sketch, "E15.0.2.1", {"start": v(-36.48, 48.61) * mm, "mid": v(-38.87, 42.43) * mm, "end": v(-36.48, 36.24) * mm});
            skArc(sketch, "E15.0.2.2", {"start": v(98.24, 41.54) * mm, "mid": v(96.13, 37.62) * mm, "end": v(96.11, 33.17) * mm});
            skArc(sketch, "E15.0.2.3", {"start": v(-24.5, 42.43) * mm, "mid": v(-26.89, 38.58) * mm, "end": v(-27.34, 34.08) * mm});
            skLineSegment(sketch, "E15.0.2.4", {"start": v(48.99, 42.43) * mm, "end": v(34.59, 38.57) * mm, "construction": true});
            skPoint(sketch, "E15.0.2.5", {"position": v(24.5, 42.43) * mm});
            skLineSegment(sketch, "E15.0.2.6", {"start": v(73.48, 42.43) * mm, "end": v(83.14, 45.01) * mm, "construction": true});
            skArc(sketch, "E15.0.2.7", {"start": v(0.64, 43.1) * mm, "mid": v(5.08, 43.23) * mm, "end": v(8.95, 45.44) * mm});
            skArc(sketch, "E15.0.2.8", {"start": v(0.64, 43.1) * mm, "mid": v(-1.45, 46.85) * mm, "end": v(-4.83, 49.5) * mm});
            skArc(sketch, "E15.0.2.9", {"start": v(11.35, 49.72) * mm, "mid": v(8.52, 42.43) * mm, "end": v(11.35, 35.14) * mm});
            skArc(sketch, "E15.0.2.10", {"start": v(-13.15, 49.72) * mm, "mid": v(-15.98, 42.43) * mm, "end": v(-13.15, 35.14) * mm});
            skArc(sketch, "E15.0.2.11", {"start": v(49.63, 43.1) * mm, "mid": v(54.07, 43.23) * mm, "end": v(57.94, 45.44) * mm});
            skArc(sketch, "E15.0.2.12", {"start": v(98.62, 28.95) * mm, "mid": v(93.72, 35.05) * mm, "end": v(86, 36.24) * mm});
            skArc(sketch, "E15.0.2.13", {"start": v(73.74, 41.54) * mm, "mid": v(71.64, 37.62) * mm, "end": v(71.62, 33.17) * mm});
            skArc(sketch, "E15.0.2.14", {"start": v(24.75, 41.54) * mm, "mid": v(22.65, 37.62) * mm, "end": v(22.63, 33.17) * mm});
            skArc(sketch, "E15.0.2.15", {"start": v(60.34, 49.72) * mm, "mid": v(57.5, 42.43) * mm, "end": v(60.34, 35.14) * mm});
            skArc(sketch, "E15.0.2.16", {"start": v(84.83, 49.72) * mm, "mid": v(80.67, 54.88) * mm, "end": v(74.12, 55.9) * mm});
            skArc(sketch, "E15.0.2.17", {"start": v(0, 42.43) * mm, "mid": v(-2.4, 38.58) * mm, "end": v(-2.85, 34.08) * mm});
            skPoint(sketch, "E15.0.2.18", {"position": v(73.48, 28.28) * mm});
            skArc(sketch, "E15.0.2.19", {"start": v(73.48, 42.43) * mm, "mid": v(71.35, 46.42) * mm, "end": v(67.68, 49.07) * mm});
            skArc(sketch, "E15.0.2.20", {"start": v(23.6, 42.64) * mm, "mid": v(21.39, 38.96) * mm, "end": v(20.79, 34.7) * mm});
            skArc(sketch, "E15.0.2.21", {"start": v(49.25, 41.54) * mm, "mid": v(47.14, 37.62) * mm, "end": v(47.12, 33.17) * mm});
            skArc(sketch, "E15.0.2.22", {"start": v(-23.86, 28.95) * mm, "mid": v(-17.3, 29.98) * mm, "end": v(-13.15, 35.14) * mm});
            skArc(sketch, "E15.0.2.23", {"start": v(97.98, 42.43) * mm, "mid": v(102.5, 42.28) * mm, "end": v(106.63, 44.14) * mm});
            skArc(sketch, "E15.0.2.24", {"start": v(24.5, 42.43) * mm, "mid": v(22.36, 46.42) * mm, "end": v(18.69, 49.07) * mm});
            skArc(sketch, "E15.0.2.25", {"start": v(12.25, 49.5) * mm, "mid": v(7.59, 55.57) * mm, "end": v(0, 56.57) * mm});
            skArc(sketch, "E15.0.2.26", {"start": v(74.12, 43.1) * mm, "mid": v(78.57, 43.23) * mm, "end": v(82.43, 45.44) * mm});
            skArc(sketch, "E15.0.2.27", {"start": v(0.64, 28.95) * mm, "mid": v(-4.26, 35.05) * mm, "end": v(-11.99, 36.24) * mm});
            skArc(sketch, "E15.0.2.28", {"start": v(48.1, 42.64) * mm, "mid": v(45.88, 38.96) * mm, "end": v(45.28, 34.7) * mm});
            skPoint(sketch, "E15.0.2.29", {"position": v(24.5, 28.28) * mm});
            skLineSegment(sketch, "E15.0.2.30", {"start": v(24.5, 42.43) * mm, "end": v(10.1, 38.57) * mm, "construction": true});
            skArc(sketch, "E15.0.2.31", {"start": v(60.34, 49.72) * mm, "mid": v(56.18, 54.88) * mm, "end": v(49.63, 55.9) * mm});
            skArc(sketch, "E15.0.2.32", {"start": v(-0.9, 42.64) * mm, "mid": v(-3.1, 38.96) * mm, "end": v(-3.7, 34.7) * mm});
            skArc(sketch, "E15.0.2.33", {"start": v(0.26, 41.54) * mm, "mid": v(-1.85, 37.62) * mm, "end": v(-1.87, 33.17) * mm});
            skArc(sketch, "E15.0.2.34", {"start": v(84.83, 49.72) * mm, "mid": v(82, 42.43) * mm, "end": v(84.83, 35.14) * mm});
            skArc(sketch, "E15.0.2.35", {"start": v(85.73, 49.5) * mm, "mid": v(81.07, 55.57) * mm, "end": v(73.48, 56.57) * mm});
            skArc(sketch, "E15.0.2.36", {"start": v(-24.5, 28.28) * mm, "mid": v(-29.15, 34.36) * mm, "end": v(-36.74, 35.36) * mm});
            skArc(sketch, "E15.0.2.37", {"start": v(12.25, 49.5) * mm, "mid": v(19.84, 50.5) * mm, "end": v(24.5, 56.57) * mm});
            skArc(sketch, "E15.0.2.38", {"start": v(97.98, 28.28) * mm, "mid": v(105.57, 29.28) * mm, "end": v(110.23, 35.36) * mm});
            skArc(sketch, "E15.0.2.39", {"start": v(-36.74, 49.5) * mm, "mid": v(-29.15, 50.5) * mm, "end": v(-24.5, 56.57) * mm});
            skArc(sketch, "E15.0.2.40", {"start": v(11.35, 49.72) * mm, "mid": v(7.19, 54.88) * mm, "end": v(0.64, 55.9) * mm});
            skArc(sketch, "E15.0.2.41", {"start": v(97.98, 42.43) * mm, "mid": v(95.85, 46.42) * mm, "end": v(92.17, 49.07) * mm});
            skArc(sketch, "E15.0.2.42", {"start": v(73.48, 28.28) * mm, "mid": v(68.83, 34.36) * mm, "end": v(61.24, 35.36) * mm});
            skPoint(sketch, "E15.0.2.43", {"position": v(0, 28.28) * mm});
            skPoint(sketch, "E15.0.2.44", {"position": v(85.73, 49.5) * mm});
            skArc(sketch, "E15.0.2.45", {"start": v(48.99, 28.28) * mm, "mid": v(44.33, 34.36) * mm, "end": v(36.74, 35.36) * mm});
            skArc(sketch, "E15.0.2.46", {"start": v(0.64, 28.95) * mm, "mid": v(7.19, 29.98) * mm, "end": v(11.35, 35.14) * mm});
            skArc(sketch, "E15.0.2.47", {"start": v(-23.86, 28.95) * mm, "mid": v(-28.75, 35.05) * mm, "end": v(-36.48, 36.24) * mm});
            skArc(sketch, "E15.0.2.48", {"start": v(109.33, 49.72) * mm, "mid": v(106.5, 42.43) * mm, "end": v(109.33, 35.14) * mm});
            skArc(sketch, "E15.0.2.49", {"start": v(25.13, 28.95) * mm, "mid": v(20.24, 35.05) * mm, "end": v(12.5, 36.24) * mm});
            skArc(sketch, "E15.0.2.50", {"start": v(-13.15, 49.72) * mm, "mid": v(-17.3, 54.88) * mm, "end": v(-23.86, 55.9) * mm});
            skArc(sketch, "E15.0.2.51", {"start": v(74.12, 28.95) * mm, "mid": v(80.67, 29.98) * mm, "end": v(84.83, 35.14) * mm});
            skArc(sketch, "E15.0.2.52", {"start": v(72.59, 42.64) * mm, "mid": v(70.25, 46.43) * mm, "end": v(66.4, 48.67) * mm});
            skPoint(sketch, "E15.0.2.53", {"position": v(-24.5, 28.28) * mm});
            skArc(sketch, "E15.0.2.54", {"start": v(73.48, 28.28) * mm, "mid": v(81.07, 29.28) * mm, "end": v(85.73, 35.36) * mm});
            skArc(sketch, "E15.0.2.55", {"start": v(-24.5, 42.43) * mm, "mid": v(-19.97, 42.28) * mm, "end": v(-15.84, 44.14) * mm});
            skArc(sketch, "E15.0.2.56", {"start": v(0, 42.43) * mm, "mid": v(-2.13, 46.42) * mm, "end": v(-5.8, 49.07) * mm});
            skArc(sketch, "E15.0.2.57", {"start": v(73.48, 42.43) * mm, "mid": v(71.1, 38.58) * mm, "end": v(70.64, 34.08) * mm});
            skArc(sketch, "E15.0.2.58", {"start": v(-36.74, 49.5) * mm, "mid": v(-39.67, 42.43) * mm, "end": v(-36.74, 35.36) * mm});
            skArc(sketch, "E15.0.2.59", {"start": v(-23.86, 43.1) * mm, "mid": v(-25.94, 46.85) * mm, "end": v(-29.32, 49.5) * mm});
            skArc(sketch, "E15.0.2.60", {"start": v(24.5, 28.28) * mm, "mid": v(32.08, 29.28) * mm, "end": v(36.74, 35.36) * mm});
            skPoint(sketch, "E15.0.2.61", {"position": v(-24.5, 42.43) * mm});
            skLineSegment(sketch, "E15.0.2.62", {"start": v(48.99, 42.43) * mm, "end": v(58.65, 45.01) * mm, "construction": true});
            skArc(sketch, "E15.0.2.63", {"start": v(35.84, 49.72) * mm, "mid": v(33.01, 42.43) * mm, "end": v(35.84, 35.14) * mm});
            skArc(sketch, "E15.0.2.64", {"start": v(-24.24, 41.54) * mm, "mid": v(-26.34, 37.62) * mm, "end": v(-26.36, 33.17) * mm});
            skArc(sketch, "E15.0.2.65", {"start": v(86, 48.61) * mm, "mid": v(83.6, 42.43) * mm, "end": v(86, 36.24) * mm});
            skArc(sketch, "E15.0.2.66", {"start": v(73.74, 41.54) * mm, "mid": v(78.04, 41.47) * mm, "end": v(82.02, 43.07) * mm});
            skArc(sketch, "E15.0.2.67", {"start": v(-23.86, 43.1) * mm, "mid": v(-19.41, 43.23) * mm, "end": v(-15.55, 45.44) * mm});
            skArc(sketch, "E15.0.2.68", {"start": v(98.62, 43.1) * mm, "mid": v(103.06, 43.23) * mm, "end": v(106.93, 45.44) * mm});
            skPoint(sketch, "E15.0.2.69", {"position": v(48.99, 28.28) * mm});
            skArc(sketch, "E15.0.2.70", {"start": v(25.13, 28.95) * mm, "mid": v(31.68, 29.98) * mm, "end": v(35.84, 35.14) * mm});
            skArc(sketch, "E15.0.2.71", {"start": v(61.5, 48.61) * mm, "mid": v(69.23, 49.8) * mm, "end": v(74.12, 55.9) * mm});
            skArc(sketch, "E15.0.2.72", {"start": v(110.23, 49.5) * mm, "mid": v(107.3, 42.43) * mm, "end": v(110.23, 35.36) * mm});
            skPoint(sketch, "E15.0.2.73", {"position": v(73.48, 42.43) * mm});
            skArc(sketch, "E15.0.2.74", {"start": v(61.5, 48.61) * mm, "mid": v(59.1, 42.43) * mm, "end": v(61.5, 36.24) * mm});
            skArc(sketch, "E15.0.2.75", {"start": v(49.63, 43.1) * mm, "mid": v(47.54, 46.85) * mm, "end": v(44.16, 49.5) * mm});
            skPoint(sketch, "E15.0.2.76", {"position": v(12.25, 49.5) * mm});
            skArc(sketch, "E15.0.2.77", {"start": v(35.84, 49.72) * mm, "mid": v(31.68, 54.88) * mm, "end": v(25.13, 55.9) * mm});
            skLineSegment(sketch, "E15.0.2.78", {"start": v(97.98, 42.43) * mm, "end": v(83.58, 38.57) * mm, "construction": true});
            skArc(sketch, "E15.0.2.79", {"start": v(74.12, 43.1) * mm, "mid": v(72.04, 46.85) * mm, "end": v(68.66, 49.5) * mm});
            skArc(sketch, "E15.0.2.80", {"start": v(98.62, 43.1) * mm, "mid": v(96.53, 46.85) * mm, "end": v(93.15, 49.5) * mm});
            skPoint(sketch, "E15.0.2.81", {"position": v(36.74, 49.5) * mm});
            skLineSegment(sketch, "E15.0.2.82", {"start": v(-24.5, 42.43) * mm, "end": v(-38.9, 38.57) * mm, "construction": true});
            skArc(sketch, "E15.0.2.83", {"start": v(98.24, 41.54) * mm, "mid": v(102.53, 41.47) * mm, "end": v(106.52, 43.07) * mm});
            skArc(sketch, "E15.0.2.84", {"start": v(72.59, 42.64) * mm, "mid": v(70.38, 38.96) * mm, "end": v(69.78, 34.7) * mm});
            skArc(sketch, "E15.0.2.85", {"start": v(12.5, 48.61) * mm, "mid": v(20.24, 49.8) * mm, "end": v(25.13, 55.9) * mm});
            skArc(sketch, "E15.0.2.86", {"start": v(24.75, 41.54) * mm, "mid": v(29.05, 41.47) * mm, "end": v(33.03, 43.07) * mm});
            skArc(sketch, "E15.0.2.87", {"start": v(74.12, 28.95) * mm, "mid": v(69.23, 35.05) * mm, "end": v(61.5, 36.24) * mm});
            skArc(sketch, "E15.0.2.88", {"start": v(0.26, 41.54) * mm, "mid": v(4.55, 41.47) * mm, "end": v(8.54, 43.07) * mm});
            skArc(sketch, "E15.0.2.89", {"start": v(61.24, 49.5) * mm, "mid": v(56.58, 55.57) * mm, "end": v(48.99, 56.57) * mm});
            skArc(sketch, "E15.0.2.90", {"start": v(48.99, 28.28) * mm, "mid": v(56.58, 29.28) * mm, "end": v(61.24, 35.36) * mm});
            skArc(sketch, "E15.0.2.91", {"start": v(48.1, 42.64) * mm, "mid": v(45.75, 46.43) * mm, "end": v(41.9, 48.67) * mm});
            skArc(sketch, "E15.0.2.92", {"start": v(-24.5, 42.43) * mm, "mid": v(-26.63, 46.42) * mm, "end": v(-30.3, 49.07) * mm});
            skArc(sketch, "E15.0.2.93", {"start": v(48.99, 42.43) * mm, "mid": v(46.6, 38.58) * mm, "end": v(46.14, 34.08) * mm});
            skArc(sketch, "E15.0.2.94", {"start": v(97.08, 42.64) * mm, "mid": v(94.87, 38.96) * mm, "end": v(94.27, 34.7) * mm});
            skArc(sketch, "E15.0.2.95", {"start": v(25.13, 43.1) * mm, "mid": v(29.58, 43.23) * mm, "end": v(33.44, 45.44) * mm});
            skArc(sketch, "E15.0.2.96", {"start": v(109.33, 49.72) * mm, "mid": v(105.17, 54.88) * mm, "end": v(98.62, 55.9) * mm});
            skArc(sketch, "E15.0.2.97", {"start": v(-25.4, 42.64) * mm, "mid": v(-27.6, 38.96) * mm, "end": v(-28.2, 34.7) * mm});
            skArc(sketch, "E15.0.2.98", {"start": v(98.62, 28.95) * mm, "mid": v(105.17, 29.98) * mm, "end": v(109.33, 35.14) * mm});
            skArc(sketch, "E15.0.2.99", {"start": v(25.13, 43.1) * mm, "mid": v(23.05, 46.85) * mm, "end": v(19.67, 49.5) * mm});
            skArc(sketch, "E15.0.2.100", {"start": v(-11.99, 48.61) * mm, "mid": v(-4.26, 49.8) * mm, "end": v(0.64, 55.9) * mm});
            skArc(sketch, "E15.0.2.101", {"start": v(110.23, 49.5) * mm, "mid": v(105.57, 55.57) * mm, "end": v(97.98, 56.57) * mm});
            skArc(sketch, "E15.0.2.102", {"start": v(-12.25, 49.5) * mm, "mid": v(-16.9, 55.57) * mm, "end": v(-24.5, 56.57) * mm});
            skArc(sketch, "E15.0.2.103", {"start": v(24.5, 42.43) * mm, "mid": v(29.02, 42.28) * mm, "end": v(33.15, 44.14) * mm});
            skArc(sketch, "E15.0.2.104", {"start": v(0, 28.28) * mm, "mid": v(-4.66, 34.36) * mm, "end": v(-12.25, 35.36) * mm});
            skArc(sketch, "E15.0.2.105", {"start": v(-36.48, 48.61) * mm, "mid": v(-28.75, 49.8) * mm, "end": v(-23.86, 55.9) * mm});
            skArc(sketch, "E15.0.2.106", {"start": v(-12.25, 49.5) * mm, "mid": v(-4.66, 50.5) * mm, "end": v(0, 56.57) * mm});
            skArc(sketch, "E15.0.2.107", {"start": v(37, 48.61) * mm, "mid": v(34.61, 42.43) * mm, "end": v(37, 36.24) * mm});
            skArc(sketch, "E15.0.2.108", {"start": v(61.24, 49.5) * mm, "mid": v(68.83, 50.5) * mm, "end": v(73.48, 56.57) * mm});
            skArc(sketch, "E15.0.2.109", {"start": v(36.74, 49.5) * mm, "mid": v(44.33, 50.5) * mm, "end": v(48.99, 56.57) * mm});
            skPoint(sketch, "E15.0.2.110", {"position": v(-12.25, 49.5) * mm});
            skPoint(sketch, "E15.0.2.111", {"position": v(97.98, 28.28) * mm});
            skArc(sketch, "E15.0.2.112", {"start": v(36.74, 49.5) * mm, "mid": v(32.08, 55.57) * mm, "end": v(24.5, 56.57) * mm});
            skLineSegment(sketch, "E15.0.2.113", {"start": v(73.48, 42.43) * mm, "end": v(59.08, 38.57) * mm, "construction": true});
            skArc(sketch, "E15.0.2.114", {"start": v(0, 28.28) * mm, "mid": v(7.59, 29.28) * mm, "end": v(12.25, 35.36) * mm});
            skArc(sketch, "E15.0.2.115", {"start": v(-24.24, 41.54) * mm, "mid": v(-19.94, 41.47) * mm, "end": v(-15.96, 43.07) * mm});
            skArc(sketch, "E15.0.2.116", {"start": v(-24.5, 28.28) * mm, "mid": v(-16.9, 29.28) * mm, "end": v(-12.25, 35.36) * mm});
            skArc(sketch, "E15.0.2.117", {"start": v(24.5, 28.28) * mm, "mid": v(19.84, 34.36) * mm, "end": v(12.25, 35.36) * mm});
            skArc(sketch, "E15.0.2.118", {"start": v(37, 48.61) * mm, "mid": v(44.73, 49.8) * mm, "end": v(49.63, 55.9) * mm});
            skArc(sketch, "E15.0.2.119", {"start": v(97.98, 28.28) * mm, "mid": v(93.32, 34.36) * mm, "end": v(85.73, 35.36) * mm});
            skLineSegment(sketch, "E15.0.2.120", {"start": v(0, 42.43) * mm, "end": v(-14.4, 38.57) * mm, "construction": true});
            skArc(sketch, "E15.0.2.121", {"start": v(49.25, 41.54) * mm, "mid": v(53.54, 41.47) * mm, "end": v(57.53, 43.07) * mm});
            skArc(sketch, "E15.0.2.122", {"start": v(24.5, 42.43) * mm, "mid": v(22.1, 38.58) * mm, "end": v(21.65, 34.08) * mm});
            skArc(sketch, "E15.0.2.123", {"start": v(85.73, 49.5) * mm, "mid": v(93.32, 50.5) * mm, "end": v(97.98, 56.57) * mm});
            skPoint(sketch, "E15.0.2.124", {"position": v(61.24, 49.5) * mm});
            skArc(sketch, "E15.0.2.125", {"start": v(-25.4, 42.64) * mm, "mid": v(-27.73, 46.43) * mm, "end": v(-31.57, 48.67) * mm});
            skPoint(sketch, "E15.0.2.126", {"position": v(-36.74, 49.5) * mm});
            skLineSegment(sketch, "E15.0.2.127", {"start": v(-24.5, 42.43) * mm, "end": v(-14.84, 45.01) * mm, "construction": true});
            skArc(sketch, "E15.0.2.128", {"start": v(-12.25, 49.5) * mm, "mid": v(-15.18, 42.43) * mm, "end": v(-12.25, 35.36) * mm});
            skPoint(sketch, "E15.0.2.129", {"position": v(-24.53, 42.36) * mm});
            skArc(sketch, "E15.0.2.130", {"start": v(73.48, 42.43) * mm, "mid": v(78.01, 42.28) * mm, "end": v(82.14, 44.14) * mm});
            skArc(sketch, "E15.0.2.131", {"start": v(23.6, 42.64) * mm, "mid": v(21.26, 46.43) * mm, "end": v(17.41, 48.67) * mm});
            skArc(sketch, "E15.0.2.132", {"start": v(49.63, 28.95) * mm, "mid": v(56.18, 29.98) * mm, "end": v(60.34, 35.14) * mm});
            skLineSegment(sketch, "E15.0.2.133", {"start": v(-34.15, 25.7) * mm, "end": v(-9.66, 25.7) * mm, "construction": true});
            skArc(sketch, "E15.0.2.134", {"start": v(61.24, 49.5) * mm, "mid": v(58.3, 42.43) * mm, "end": v(61.24, 35.36) * mm});
            skArc(sketch, "E15.0.2.135", {"start": v(97.08, 42.64) * mm, "mid": v(94.74, 46.43) * mm, "end": v(90.9, 48.67) * mm});
            skArc(sketch, "E15.0.2.136", {"start": v(48.99, 42.43) * mm, "mid": v(46.86, 46.42) * mm, "end": v(43.18, 49.07) * mm});
            skArc(sketch, "E15.0.2.137", {"start": v(12.25, 49.5) * mm, "mid": v(9.32, 42.43) * mm, "end": v(12.25, 35.36) * mm});
            skLineSegment(sketch, "E15.0.2.138", {"start": v(0, 42.43) * mm, "end": v(9.66, 45.01) * mm, "construction": true});
            skPoint(sketch, "E15.0.2.139", {"position": v(48.99, 42.43) * mm});
            skLineSegment(sketch, "E15.0.2.140", {"start": v(24.5, 42.43) * mm, "end": v(34.15, 45.01) * mm, "construction": true});
            skArc(sketch, "E15.0.2.141", {"start": v(36.74, 49.5) * mm, "mid": v(33.81, 42.43) * mm, "end": v(36.74, 35.36) * mm});
            skArc(sketch, "E15.0.2.142", {"start": v(97.98, 42.43) * mm, "mid": v(95.59, 38.58) * mm, "end": v(95.13, 34.08) * mm});
            skArc(sketch, "E15.0.2.143", {"start": v(-11.99, 48.61) * mm, "mid": v(-14.38, 42.43) * mm, "end": v(-11.99, 36.24) * mm});
            skArc(sketch, "E15.0.2.144", {"start": v(49.63, 28.95) * mm, "mid": v(44.73, 35.05) * mm, "end": v(37, 36.24) * mm});
            skArc(sketch, "E15.0.2.145", {"start": v(48.99, 42.43) * mm, "mid": v(53.52, 42.28) * mm, "end": v(57.64, 44.14) * mm});
            skArc(sketch, "E15.0.2.146", {"start": v(85.73, 49.5) * mm, "mid": v(82.8, 42.43) * mm, "end": v(85.73, 35.36) * mm});
            skArc(sketch, "E15.0.2.147", {"start": v(12.5, 48.61) * mm, "mid": v(10.12, 42.43) * mm, "end": v(12.5, 36.24) * mm});
            skPoint(sketch, "E15.0.2.148", {"position": v(97.98, 42.43) * mm});
            skPoint(sketch, "E15.0.2.149", {"position": v(0, 42.43) * mm});
            skArc(sketch, "E15.0.2.150", {"start": v(0, 42.43) * mm, "mid": v(4.53, 42.28) * mm, "end": v(8.65, 44.14) * mm});
            skArc(sketch, "E15.0.2.151", {"start": v(86, 48.61) * mm, "mid": v(93.72, 49.8) * mm, "end": v(98.62, 55.9) * mm});
            skArc(sketch, "E15.0.2.152", {"start": v(-0.9, 42.64) * mm, "mid": v(-3.24, 46.43) * mm, "end": v(-7.08, 48.67) * mm});
            skArc(sketch, "E15.0.2.153", {"start": v(12.25, 49.5) * mm, "mid": v(9.32, 42.43) * mm, "end": v(12.25, 35.36) * mm});
            skPoint(sketch, "E15.0.2.154", {"position": v(48.99, 42.43) * mm});
            skArc(sketch, "E15.0.2.155", {"start": v(85.73, 49.5) * mm, "mid": v(82.8, 42.43) * mm, "end": v(85.73, 35.36) * mm});
            skPoint(sketch, "E15.0.2.156", {"position": v(97.98, 42.43) * mm});
            skArc(sketch, "E15.0.2.157", {"start": v(-12.25, 49.5) * mm, "mid": v(-15.18, 42.43) * mm, "end": v(-12.25, 35.36) * mm});
            skPoint(sketch, "E15.0.2.158", {"position": v(24.5, 42.43) * mm});
            skArc(sketch, "E15.0.2.159", {"start": v(36.74, 49.5) * mm, "mid": v(33.81, 42.43) * mm, "end": v(36.74, 35.36) * mm});
            skArc(sketch, "E15.0.2.160", {"start": v(61.24, 49.5) * mm, "mid": v(58.3, 42.43) * mm, "end": v(61.24, 35.36) * mm});
            skPoint(sketch, "E15.0.2.161", {"position": v(-24.5, 42.43) * mm});
            skPoint(sketch, "E15.0.2.162", {"position": v(0, 42.43) * mm});
            skPoint(sketch, "E15.0.2.163", {"position": v(73.48, 42.43) * mm});
            skPoint(sketch, "E15.0.2.164", {"position": v(97.98, 42.43) * mm});
            skPoint(sketch, "E15.0.2.165", {"position": v(73.48, 42.43) * mm});
            skPoint(sketch, "E15.0.2.166", {"position": v(0, 42.43) * mm});
            skPoint(sketch, "E15.0.2.167", {"position": v(48.99, 42.43) * mm});
            skPoint(sketch, "E15.0.2.168", {"position": v(-24.5, 42.43) * mm});
            skPoint(sketch, "E15.0.2.169", {"position": v(24.5, 42.43) * mm});
            skPoint(sketch, "E15.0.2.170", {"position": v(97.98, 42.43) * mm});
            skPoint(sketch, "E15.0.2.171", {"position": v(0, 42.43) * mm});
            skPoint(sketch, "E15.0.2.172", {"position": v(-24.5, 42.43) * mm});
            skPoint(sketch, "E15.0.2.173", {"position": v(73.48, 42.43) * mm});
            skPoint(sketch, "E15.0.2.174", {"position": v(24.5, 42.43) * mm});
            skPoint(sketch, "E15.0.2.175", {"position": v(48.95, 42.36) * mm});
            skPoint(sketch, "E15.0.2.176", {"position": v(24.46, 42.36) * mm});
            skPoint(sketch, "E15.0.2.177", {"position": v(97.94, 42.36) * mm});
            skPoint(sketch, "E15.0.2.178", {"position": v(48.99, 42.43) * mm});
            skPoint(sketch, "E15.0.2.179", {"position": v(73.45, 42.36) * mm});
            skPoint(sketch, "E15.0.2.180", {"position": v(-0.04, 42.36) * mm});
            skLineSegment(sketch, "E15.0.3.0", {"start": v(85.73, 63.64) * mm, "end": v(95.4, 66.23) * mm, "construction": true});
            skArc(sketch, "E15.0.3.1", {"start": v(-48.73, 69.82) * mm, "mid": v(-51.12, 63.64) * mm, "end": v(-48.73, 57.46) * mm});
            skArc(sketch, "E15.0.3.2", {"start": v(86, 62.75) * mm, "mid": v(83.89, 58.83) * mm, "end": v(83.87, 54.39) * mm});
            skArc(sketch, "E15.0.3.3", {"start": v(-36.74, 63.64) * mm, "mid": v(-39.14, 59.8) * mm, "end": v(-39.59, 55.29) * mm});
            skLineSegment(sketch, "E15.0.3.4", {"start": v(36.74, 63.64) * mm, "end": v(22.34, 59.78) * mm, "construction": true});
            skPoint(sketch, "E15.0.3.5", {"position": v(12.25, 63.64) * mm});
            skLineSegment(sketch, "E15.0.3.6", {"start": v(61.24, 63.64) * mm, "end": v(70.9, 66.23) * mm, "construction": true});
            skArc(sketch, "E15.0.3.7", {"start": v(-11.6, 64.3) * mm, "mid": v(-7.16, 64.44) * mm, "end": v(-3.3, 66.65) * mm});
            skArc(sketch, "E15.0.3.8", {"start": v(-11.6, 64.3) * mm, "mid": v(-13.7, 68.06) * mm, "end": v(-17.08, 70.71) * mm});
            skArc(sketch, "E15.0.3.9", {"start": v(-0.9, 70.93) * mm, "mid": v(-3.73, 63.64) * mm, "end": v(-0.9, 56.35) * mm});
            skArc(sketch, "E15.0.3.10", {"start": v(-25.4, 70.93) * mm, "mid": v(-28.22, 63.64) * mm, "end": v(-25.4, 56.35) * mm});
            skArc(sketch, "E15.0.3.11", {"start": v(37.38, 64.3) * mm, "mid": v(41.83, 64.44) * mm, "end": v(45.69, 66.65) * mm});
            skArc(sketch, "E15.0.3.12", {"start": v(86.37, 50.17) * mm, "mid": v(81.47, 56.26) * mm, "end": v(73.74, 57.46) * mm});
            skArc(sketch, "E15.0.3.13", {"start": v(61.5, 62.75) * mm, "mid": v(59.4, 58.83) * mm, "end": v(59.37, 54.39) * mm});
            skArc(sketch, "E15.0.3.14", {"start": v(12.5, 62.75) * mm, "mid": v(10.4, 58.83) * mm, "end": v(10.38, 54.39) * mm});
            skArc(sketch, "E15.0.3.15", {"start": v(48.1, 70.93) * mm, "mid": v(45.26, 63.64) * mm, "end": v(48.1, 56.35) * mm});
            skArc(sketch, "E15.0.3.16", {"start": v(72.59, 70.93) * mm, "mid": v(68.43, 76.09) * mm, "end": v(61.88, 77.11) * mm});
            skArc(sketch, "E15.0.3.17", {"start": v(-12.25, 63.64) * mm, "mid": v(-14.64, 59.8) * mm, "end": v(-15.1, 55.29) * mm});
            skPoint(sketch, "E15.0.3.18", {"position": v(61.24, 49.5) * mm});
            skArc(sketch, "E15.0.3.19", {"start": v(61.24, 63.64) * mm, "mid": v(59.1, 67.63) * mm, "end": v(55.43, 70.28) * mm});
            skArc(sketch, "E15.0.3.20", {"start": v(11.35, 63.86) * mm, "mid": v(9.14, 60.18) * mm, "end": v(8.54, 55.92) * mm});
            skArc(sketch, "E15.0.3.21", {"start": v(37, 62.75) * mm, "mid": v(34.9, 58.83) * mm, "end": v(34.88, 54.39) * mm});
            skArc(sketch, "E15.0.3.22", {"start": v(-36.1, 50.17) * mm, "mid": v(-29.55, 51.19) * mm, "end": v(-25.4, 56.35) * mm});
            skArc(sketch, "E15.0.3.23", {"start": v(85.73, 63.64) * mm, "mid": v(90.26, 63.49) * mm, "end": v(94.39, 65.35) * mm});
            skArc(sketch, "E15.0.3.24", {"start": v(12.25, 63.64) * mm, "mid": v(10.12, 67.63) * mm, "end": v(6.44, 70.28) * mm});
            skArc(sketch, "E15.0.3.25", {"start": v(0, 70.71) * mm, "mid": v(-4.66, 76.78) * mm, "end": v(-12.25, 77.78) * mm});
            skArc(sketch, "E15.0.3.26", {"start": v(61.88, 64.3) * mm, "mid": v(66.32, 64.44) * mm, "end": v(70.18, 66.65) * mm});
            skArc(sketch, "E15.0.3.27", {"start": v(-11.6, 50.17) * mm, "mid": v(-16.5, 56.26) * mm, "end": v(-24.24, 57.46) * mm});
            skArc(sketch, "E15.0.3.28", {"start": v(35.84, 63.86) * mm, "mid": v(33.63, 60.18) * mm, "end": v(33.03, 55.92) * mm});
            skPoint(sketch, "E15.0.3.29", {"position": v(12.25, 49.5) * mm});
            skLineSegment(sketch, "E15.0.3.30", {"start": v(12.25, 63.64) * mm, "end": v(-2.15, 59.78) * mm, "construction": true});
            skArc(sketch, "E15.0.3.31", {"start": v(48.1, 70.93) * mm, "mid": v(43.93, 76.09) * mm, "end": v(37.38, 77.11) * mm});
            skArc(sketch, "E15.0.3.32", {"start": v(-13.15, 63.86) * mm, "mid": v(-15.36, 60.18) * mm, "end": v(-15.96, 55.92) * mm});
            skArc(sketch, "E15.0.3.33", {"start": v(-11.99, 62.75) * mm, "mid": v(-14.1, 58.83) * mm, "end": v(-14.11, 54.39) * mm});
            skArc(sketch, "E15.0.3.34", {"start": v(72.59, 70.93) * mm, "mid": v(69.76, 63.64) * mm, "end": v(72.59, 56.35) * mm});
            skArc(sketch, "E15.0.3.35", {"start": v(73.48, 70.71) * mm, "mid": v(68.83, 76.78) * mm, "end": v(61.24, 77.78) * mm});
            skArc(sketch, "E15.0.3.36", {"start": v(-36.74, 49.5) * mm, "mid": v(-41.4, 55.57) * mm, "end": v(-48.99, 56.57) * mm});
            skArc(sketch, "E15.0.3.37", {"start": v(0, 70.71) * mm, "mid": v(7.59, 71.7) * mm, "end": v(12.25, 77.78) * mm});
            skArc(sketch, "E15.0.3.38", {"start": v(85.73, 49.5) * mm, "mid": v(93.32, 50.5) * mm, "end": v(97.98, 56.57) * mm});
            skArc(sketch, "E15.0.3.39", {"start": v(-48.99, 70.71) * mm, "mid": v(-41.4, 71.7) * mm, "end": v(-36.74, 77.78) * mm});
            skArc(sketch, "E15.0.3.40", {"start": v(-0.9, 70.93) * mm, "mid": v(-5.06, 76.09) * mm, "end": v(-11.6, 77.11) * mm});
            skArc(sketch, "E15.0.3.41", {"start": v(85.73, 63.64) * mm, "mid": v(83.6, 67.63) * mm, "end": v(79.92, 70.28) * mm});
            skArc(sketch, "E15.0.3.42", {"start": v(61.24, 49.5) * mm, "mid": v(56.58, 55.57) * mm, "end": v(48.99, 56.57) * mm});
            skPoint(sketch, "E15.0.3.43", {"position": v(-12.25, 49.5) * mm});
            skPoint(sketch, "E15.0.3.44", {"position": v(73.48, 70.71) * mm});
            skArc(sketch, "E15.0.3.45", {"start": v(36.74, 49.5) * mm, "mid": v(32.08, 55.57) * mm, "end": v(24.5, 56.57) * mm});
            skArc(sketch, "E15.0.3.46", {"start": v(-11.6, 50.17) * mm, "mid": v(-5.06, 51.19) * mm, "end": v(-0.9, 56.35) * mm});
            skArc(sketch, "E15.0.3.47", {"start": v(-36.1, 50.17) * mm, "mid": v(-41, 56.26) * mm, "end": v(-48.73, 57.46) * mm});
            skArc(sketch, "E15.0.3.48", {"start": v(97.08, 70.93) * mm, "mid": v(94.25, 63.64) * mm, "end": v(97.08, 56.35) * mm});
            skArc(sketch, "E15.0.3.49", {"start": v(12.89, 50.17) * mm, "mid": v(7.99, 56.26) * mm, "end": v(0.26, 57.46) * mm});
            skArc(sketch, "E15.0.3.50", {"start": v(-25.4, 70.93) * mm, "mid": v(-29.55, 76.09) * mm, "end": v(-36.1, 77.11) * mm});
            skArc(sketch, "E15.0.3.51", {"start": v(61.88, 50.17) * mm, "mid": v(68.43, 51.19) * mm, "end": v(72.59, 56.35) * mm});
            skArc(sketch, "E15.0.3.52", {"start": v(60.34, 63.86) * mm, "mid": v(58, 67.64) * mm, "end": v(54.16, 69.88) * mm});
            skPoint(sketch, "E15.0.3.53", {"position": v(-36.74, 49.5) * mm});
            skArc(sketch, "E15.0.3.54", {"start": v(61.24, 49.5) * mm, "mid": v(68.83, 50.5) * mm, "end": v(73.48, 56.57) * mm});
            skArc(sketch, "E15.0.3.55", {"start": v(-36.74, 63.64) * mm, "mid": v(-32.22, 63.49) * mm, "end": v(-28.09, 65.35) * mm});
            skArc(sketch, "E15.0.3.56", {"start": v(-12.25, 63.64) * mm, "mid": v(-14.38, 67.63) * mm, "end": v(-18.06, 70.28) * mm});
            skArc(sketch, "E15.0.3.57", {"start": v(61.24, 63.64) * mm, "mid": v(58.84, 59.8) * mm, "end": v(58.4, 55.29) * mm});
            skArc(sketch, "E15.0.3.58", {"start": v(-48.99, 70.71) * mm, "mid": v(-51.92, 63.64) * mm, "end": v(-48.99, 56.57) * mm});
            skArc(sketch, "E15.0.3.59", {"start": v(-36.1, 64.3) * mm, "mid": v(-38.19, 68.06) * mm, "end": v(-41.57, 70.71) * mm});
            skArc(sketch, "E15.0.3.60", {"start": v(12.25, 49.5) * mm, "mid": v(19.84, 50.5) * mm, "end": v(24.5, 56.57) * mm});
            skPoint(sketch, "E15.0.3.61", {"position": v(-36.74, 63.64) * mm});
            skLineSegment(sketch, "E15.0.3.62", {"start": v(36.74, 63.64) * mm, "end": v(46.4, 66.23) * mm, "construction": true});
            skArc(sketch, "E15.0.3.63", {"start": v(23.6, 70.93) * mm, "mid": v(20.77, 63.64) * mm, "end": v(23.6, 56.35) * mm});
            skArc(sketch, "E15.0.3.64", {"start": v(-36.48, 62.75) * mm, "mid": v(-38.59, 58.83) * mm, "end": v(-38.6, 54.39) * mm});
            skArc(sketch, "E15.0.3.65", {"start": v(73.74, 69.82) * mm, "mid": v(71.36, 63.64) * mm, "end": v(73.74, 57.46) * mm});
            skArc(sketch, "E15.0.3.66", {"start": v(61.5, 62.75) * mm, "mid": v(65.8, 62.68) * mm, "end": v(69.78, 64.29) * mm});
            skArc(sketch, "E15.0.3.67", {"start": v(-36.1, 64.3) * mm, "mid": v(-31.66, 64.44) * mm, "end": v(-27.8, 66.65) * mm});
            skArc(sketch, "E15.0.3.68", {"start": v(86.37, 64.3) * mm, "mid": v(90.82, 64.44) * mm, "end": v(94.68, 66.65) * mm});
            skPoint(sketch, "E15.0.3.69", {"position": v(36.74, 49.5) * mm});
            skArc(sketch, "E15.0.3.70", {"start": v(12.89, 50.17) * mm, "mid": v(19.44, 51.19) * mm, "end": v(23.6, 56.35) * mm});
            skArc(sketch, "E15.0.3.71", {"start": v(49.25, 69.82) * mm, "mid": v(56.98, 71.02) * mm, "end": v(61.88, 77.11) * mm});
            skArc(sketch, "E15.0.3.72", {"start": v(97.98, 70.71) * mm, "mid": v(95.05, 63.64) * mm, "end": v(97.98, 56.57) * mm});
            skPoint(sketch, "E15.0.3.73", {"position": v(61.24, 63.64) * mm});
            skArc(sketch, "E15.0.3.74", {"start": v(49.25, 69.82) * mm, "mid": v(46.86, 63.64) * mm, "end": v(49.25, 57.46) * mm});
            skArc(sketch, "E15.0.3.75", {"start": v(37.38, 64.3) * mm, "mid": v(35.3, 68.06) * mm, "end": v(31.91, 70.71) * mm});
            skPoint(sketch, "E15.0.3.76", {"position": v(0, 70.71) * mm});
            skArc(sketch, "E15.0.3.77", {"start": v(23.6, 70.93) * mm, "mid": v(19.44, 76.09) * mm, "end": v(12.89, 77.11) * mm});
            skLineSegment(sketch, "E15.0.3.78", {"start": v(85.73, 63.64) * mm, "end": v(71.33, 59.78) * mm, "construction": true});
            skArc(sketch, "E15.0.3.79", {"start": v(61.88, 64.3) * mm, "mid": v(59.8, 68.06) * mm, "end": v(56.4, 70.71) * mm});
            skArc(sketch, "E15.0.3.80", {"start": v(86.37, 64.3) * mm, "mid": v(84.29, 68.06) * mm, "end": v(80.9, 70.71) * mm});
            skPoint(sketch, "E15.0.3.81", {"position": v(24.5, 70.71) * mm});
            skLineSegment(sketch, "E15.0.3.82", {"start": v(-36.74, 63.64) * mm, "end": v(-51.14, 59.78) * mm, "construction": true});
            skArc(sketch, "E15.0.3.83", {"start": v(86, 62.75) * mm, "mid": v(90.29, 62.68) * mm, "end": v(94.27, 64.29) * mm});
            skArc(sketch, "E15.0.3.84", {"start": v(60.34, 63.86) * mm, "mid": v(58.13, 60.18) * mm, "end": v(57.53, 55.92) * mm});
            skArc(sketch, "E15.0.3.85", {"start": v(0.26, 69.82) * mm, "mid": v(7.99, 71.02) * mm, "end": v(12.89, 77.11) * mm});
            skArc(sketch, "E15.0.3.86", {"start": v(12.5, 62.75) * mm, "mid": v(16.8, 62.68) * mm, "end": v(20.79, 64.29) * mm});
            skArc(sketch, "E15.0.3.87", {"start": v(61.88, 50.17) * mm, "mid": v(56.98, 56.26) * mm, "end": v(49.25, 57.46) * mm});
            skArc(sketch, "E15.0.3.88", {"start": v(-11.99, 62.75) * mm, "mid": v(-7.7, 62.68) * mm, "end": v(-3.7, 64.29) * mm});
            skArc(sketch, "E15.0.3.89", {"start": v(48.99, 70.71) * mm, "mid": v(44.33, 76.78) * mm, "end": v(36.74, 77.78) * mm});
            skArc(sketch, "E15.0.3.90", {"start": v(36.74, 49.5) * mm, "mid": v(44.33, 50.5) * mm, "end": v(48.99, 56.57) * mm});
            skArc(sketch, "E15.0.3.91", {"start": v(35.84, 63.86) * mm, "mid": v(33.5, 67.64) * mm, "end": v(29.66, 69.88) * mm});
            skArc(sketch, "E15.0.3.92", {"start": v(-36.74, 63.64) * mm, "mid": v(-38.87, 67.63) * mm, "end": v(-42.55, 70.28) * mm});
            skArc(sketch, "E15.0.3.93", {"start": v(36.74, 63.64) * mm, "mid": v(34.35, 59.8) * mm, "end": v(33.9, 55.29) * mm});
            skArc(sketch, "E15.0.3.94", {"start": v(84.83, 63.86) * mm, "mid": v(82.62, 60.18) * mm, "end": v(82.02, 55.92) * mm});
            skArc(sketch, "E15.0.3.95", {"start": v(12.89, 64.3) * mm, "mid": v(17.33, 64.44) * mm, "end": v(21.2, 66.65) * mm});
            skArc(sketch, "E15.0.3.96", {"start": v(97.08, 70.93) * mm, "mid": v(92.92, 76.09) * mm, "end": v(86.37, 77.11) * mm});
            skArc(sketch, "E15.0.3.97", {"start": v(-37.64, 63.86) * mm, "mid": v(-39.85, 60.18) * mm, "end": v(-40.45, 55.92) * mm});
            skArc(sketch, "E15.0.3.98", {"start": v(86.37, 50.17) * mm, "mid": v(92.92, 51.19) * mm, "end": v(97.08, 56.35) * mm});
            skArc(sketch, "E15.0.3.99", {"start": v(12.89, 64.3) * mm, "mid": v(10.8, 68.06) * mm, "end": v(7.42, 70.71) * mm});
            skArc(sketch, "E15.0.3.100", {"start": v(-24.24, 69.82) * mm, "mid": v(-16.5, 71.02) * mm, "end": v(-11.6, 77.11) * mm});
            skArc(sketch, "E15.0.3.101", {"start": v(97.98, 70.71) * mm, "mid": v(93.32, 76.78) * mm, "end": v(85.73, 77.78) * mm});
            skArc(sketch, "E15.0.3.102", {"start": v(-24.5, 70.71) * mm, "mid": v(-29.15, 76.78) * mm, "end": v(-36.74, 77.78) * mm});
            skArc(sketch, "E15.0.3.103", {"start": v(12.25, 63.64) * mm, "mid": v(16.77, 63.49) * mm, "end": v(20.9, 65.35) * mm});
            skArc(sketch, "E15.0.3.104", {"start": v(-12.25, 49.5) * mm, "mid": v(-16.9, 55.57) * mm, "end": v(-24.5, 56.57) * mm});
            skArc(sketch, "E15.0.3.105", {"start": v(-48.73, 69.82) * mm, "mid": v(-41, 71.02) * mm, "end": v(-36.1, 77.11) * mm});
            skArc(sketch, "E15.0.3.106", {"start": v(-24.5, 70.71) * mm, "mid": v(-16.9, 71.7) * mm, "end": v(-12.25, 77.78) * mm});
            skArc(sketch, "E15.0.3.107", {"start": v(24.75, 69.82) * mm, "mid": v(22.37, 63.64) * mm, "end": v(24.75, 57.46) * mm});
            skArc(sketch, "E15.0.3.108", {"start": v(48.99, 70.71) * mm, "mid": v(56.58, 71.7) * mm, "end": v(61.24, 77.78) * mm});
            skArc(sketch, "E15.0.3.109", {"start": v(24.5, 70.71) * mm, "mid": v(32.08, 71.7) * mm, "end": v(36.74, 77.78) * mm});
            skPoint(sketch, "E15.0.3.110", {"position": v(-24.5, 70.71) * mm});
            skPoint(sketch, "E15.0.3.111", {"position": v(85.73, 49.5) * mm});
            skArc(sketch, "E15.0.3.112", {"start": v(24.5, 70.71) * mm, "mid": v(19.84, 76.78) * mm, "end": v(12.25, 77.78) * mm});
            skLineSegment(sketch, "E15.0.3.113", {"start": v(61.24, 63.64) * mm, "end": v(46.84, 59.78) * mm, "construction": true});
            skArc(sketch, "E15.0.3.114", {"start": v(-12.25, 49.5) * mm, "mid": v(-4.66, 50.5) * mm, "end": v(0, 56.57) * mm});
            skArc(sketch, "E15.0.3.115", {"start": v(-36.48, 62.75) * mm, "mid": v(-32.19, 62.68) * mm, "end": v(-28.2, 64.29) * mm});
            skArc(sketch, "E15.0.3.116", {"start": v(-36.74, 49.5) * mm, "mid": v(-29.15, 50.5) * mm, "end": v(-24.5, 56.57) * mm});
            skArc(sketch, "E15.0.3.117", {"start": v(12.25, 49.5) * mm, "mid": v(7.59, 55.57) * mm, "end": v(0, 56.57) * mm});
            skArc(sketch, "E15.0.3.118", {"start": v(24.75, 69.82) * mm, "mid": v(32.48, 71.02) * mm, "end": v(37.38, 77.11) * mm});
            skArc(sketch, "E15.0.3.119", {"start": v(85.73, 49.5) * mm, "mid": v(81.07, 55.57) * mm, "end": v(73.48, 56.57) * mm});
            skLineSegment(sketch, "E15.0.3.120", {"start": v(-12.25, 63.64) * mm, "end": v(-26.65, 59.78) * mm, "construction": true});
            skArc(sketch, "E15.0.3.121", {"start": v(37, 62.75) * mm, "mid": v(41.3, 62.68) * mm, "end": v(45.28, 64.29) * mm});
            skArc(sketch, "E15.0.3.122", {"start": v(12.25, 63.64) * mm, "mid": v(9.85, 59.8) * mm, "end": v(9.4, 55.29) * mm});
            skArc(sketch, "E15.0.3.123", {"start": v(73.48, 70.71) * mm, "mid": v(81.07, 71.7) * mm, "end": v(85.73, 77.78) * mm});
            skPoint(sketch, "E15.0.3.124", {"position": v(48.99, 70.71) * mm});
            skArc(sketch, "E15.0.3.125", {"start": v(-37.64, 63.86) * mm, "mid": v(-39.98, 67.64) * mm, "end": v(-43.82, 69.88) * mm});
            skPoint(sketch, "E15.0.3.126", {"position": v(-48.99, 70.71) * mm});
            skLineSegment(sketch, "E15.0.3.127", {"start": v(-36.74, 63.64) * mm, "end": v(-27.08, 66.23) * mm, "construction": true});
            skArc(sketch, "E15.0.3.128", {"start": v(-24.5, 70.71) * mm, "mid": v(-27.42, 63.64) * mm, "end": v(-24.5, 56.57) * mm});
            skPoint(sketch, "E15.0.3.129", {"position": v(-36.78, 63.57) * mm});
            skArc(sketch, "E15.0.3.130", {"start": v(61.24, 63.64) * mm, "mid": v(65.76, 63.49) * mm, "end": v(69.9, 65.35) * mm});
            skArc(sketch, "E15.0.3.131", {"start": v(11.35, 63.86) * mm, "mid": v(9, 67.64) * mm, "end": v(5.17, 69.88) * mm});
            skArc(sketch, "E15.0.3.132", {"start": v(37.38, 50.17) * mm, "mid": v(43.93, 51.19) * mm, "end": v(48.1, 56.35) * mm});
            skLineSegment(sketch, "E15.0.3.133", {"start": v(-46.4, 46.9) * mm, "end": v(-21.9, 46.9) * mm, "construction": true});
            skArc(sketch, "E15.0.3.134", {"start": v(48.99, 70.71) * mm, "mid": v(46.06, 63.64) * mm, "end": v(48.99, 56.57) * mm});
            skArc(sketch, "E15.0.3.135", {"start": v(84.83, 63.86) * mm, "mid": v(82.5, 67.64) * mm, "end": v(78.65, 69.88) * mm});
            skArc(sketch, "E15.0.3.136", {"start": v(36.74, 63.64) * mm, "mid": v(34.61, 67.63) * mm, "end": v(30.93, 70.28) * mm});
            skArc(sketch, "E15.0.3.137", {"start": v(0, 70.71) * mm, "mid": v(-2.93, 63.64) * mm, "end": v(0, 56.57) * mm});
            skLineSegment(sketch, "E15.0.3.138", {"start": v(-12.25, 63.64) * mm, "end": v(-2.59, 66.23) * mm, "construction": true});
            skPoint(sketch, "E15.0.3.139", {"position": v(36.74, 63.64) * mm});
            skLineSegment(sketch, "E15.0.3.140", {"start": v(12.25, 63.64) * mm, "end": v(21.9, 66.23) * mm, "construction": true});
            skArc(sketch, "E15.0.3.141", {"start": v(24.5, 70.71) * mm, "mid": v(21.57, 63.64) * mm, "end": v(24.5, 56.57) * mm});
            skArc(sketch, "E15.0.3.142", {"start": v(85.73, 63.64) * mm, "mid": v(83.34, 59.8) * mm, "end": v(82.89, 55.29) * mm});
            skArc(sketch, "E15.0.3.143", {"start": v(-24.24, 69.82) * mm, "mid": v(-26.62, 63.64) * mm, "end": v(-24.24, 57.46) * mm});
            skArc(sketch, "E15.0.3.144", {"start": v(37.38, 50.17) * mm, "mid": v(32.48, 56.26) * mm, "end": v(24.75, 57.46) * mm});
            skArc(sketch, "E15.0.3.145", {"start": v(36.74, 63.64) * mm, "mid": v(41.27, 63.49) * mm, "end": v(45.4, 65.35) * mm});
            skArc(sketch, "E15.0.3.146", {"start": v(73.48, 70.71) * mm, "mid": v(70.56, 63.64) * mm, "end": v(73.48, 56.57) * mm});
            skArc(sketch, "E15.0.3.147", {"start": v(0.26, 69.82) * mm, "mid": v(-2.13, 63.64) * mm, "end": v(0.26, 57.46) * mm});
            skPoint(sketch, "E15.0.3.148", {"position": v(85.73, 63.64) * mm});
            skPoint(sketch, "E15.0.3.149", {"position": v(-12.25, 63.64) * mm});
            skArc(sketch, "E15.0.3.150", {"start": v(-12.25, 63.64) * mm, "mid": v(-7.72, 63.49) * mm, "end": v(-3.6, 65.35) * mm});
            skArc(sketch, "E15.0.3.151", {"start": v(73.74, 69.82) * mm, "mid": v(81.47, 71.02) * mm, "end": v(86.37, 77.11) * mm});
            skArc(sketch, "E15.0.3.152", {"start": v(-13.15, 63.86) * mm, "mid": v(-15.49, 67.64) * mm, "end": v(-19.33, 69.88) * mm});
            skArc(sketch, "E15.0.3.153", {"start": v(0, 70.71) * mm, "mid": v(-2.93, 63.64) * mm, "end": v(0, 56.57) * mm});
            skPoint(sketch, "E15.0.3.154", {"position": v(36.74, 63.64) * mm});
            skArc(sketch, "E15.0.3.155", {"start": v(73.48, 70.71) * mm, "mid": v(70.56, 63.64) * mm, "end": v(73.48, 56.57) * mm});
            skPoint(sketch, "E15.0.3.156", {"position": v(85.73, 63.64) * mm});
            skArc(sketch, "E15.0.3.157", {"start": v(-24.5, 70.71) * mm, "mid": v(-27.42, 63.64) * mm, "end": v(-24.5, 56.57) * mm});
            skPoint(sketch, "E15.0.3.158", {"position": v(12.25, 63.64) * mm});
            skArc(sketch, "E15.0.3.159", {"start": v(24.5, 70.71) * mm, "mid": v(21.57, 63.64) * mm, "end": v(24.5, 56.57) * mm});
            skArc(sketch, "E15.0.3.160", {"start": v(48.99, 70.71) * mm, "mid": v(46.06, 63.64) * mm, "end": v(48.99, 56.57) * mm});
            skPoint(sketch, "E15.0.3.161", {"position": v(-36.74, 63.64) * mm});
            skPoint(sketch, "E15.0.3.162", {"position": v(-12.25, 63.64) * mm});
            skPoint(sketch, "E15.0.3.163", {"position": v(61.24, 63.64) * mm});
            skPoint(sketch, "E15.0.3.164", {"position": v(85.73, 63.64) * mm});
            skPoint(sketch, "E15.0.3.165", {"position": v(61.24, 63.64) * mm});
            skPoint(sketch, "E15.0.3.166", {"position": v(-12.25, 63.64) * mm});
            skPoint(sketch, "E15.0.3.167", {"position": v(36.74, 63.64) * mm});
            skPoint(sketch, "E15.0.3.168", {"position": v(-36.74, 63.64) * mm});
            skPoint(sketch, "E15.0.3.169", {"position": v(12.25, 63.64) * mm});
            skPoint(sketch, "E15.0.3.170", {"position": v(85.73, 63.64) * mm});
            skPoint(sketch, "E15.0.3.171", {"position": v(-12.25, 63.64) * mm});
            skPoint(sketch, "E15.0.3.172", {"position": v(-36.74, 63.64) * mm});
            skPoint(sketch, "E15.0.3.173", {"position": v(61.24, 63.64) * mm});
            skPoint(sketch, "E15.0.3.174", {"position": v(12.25, 63.64) * mm});
            skPoint(sketch, "E15.0.3.175", {"position": v(36.7, 63.57) * mm});
            skPoint(sketch, "E15.0.3.176", {"position": v(12.21, 63.57) * mm});
            skPoint(sketch, "E15.0.3.177", {"position": v(85.7, 63.57) * mm});
            skPoint(sketch, "E15.0.3.178", {"position": v(36.74, 63.64) * mm});
            skPoint(sketch, "E15.0.3.179", {"position": v(61.2, 63.57) * mm});
            skPoint(sketch, "E15.0.3.180", {"position": v(-12.28, 63.57) * mm});
            skLineSegment(sketch, "E15.0.4.0", {"start": v(73.48, 84.85) * mm, "end": v(83.14, 87.44) * mm, "construction": true});
            skArc(sketch, "E15.0.4.1", {"start": v(-60.98, 91.04) * mm, "mid": v(-63.37, 84.85) * mm, "end": v(-60.98, 78.67) * mm});
            skArc(sketch, "E15.0.4.2", {"start": v(73.74, 83.97) * mm, "mid": v(71.64, 80.05) * mm, "end": v(71.62, 75.6) * mm});
            skArc(sketch, "E15.0.4.3", {"start": v(-48.99, 84.85) * mm, "mid": v(-51.38, 81) * mm, "end": v(-51.84, 76.5) * mm});
            skLineSegment(sketch, "E15.0.4.4", {"start": v(24.5, 84.85) * mm, "end": v(10.1, 81) * mm, "construction": true});
            skPoint(sketch, "E15.0.4.5", {"position": v(0, 84.85) * mm});
            skLineSegment(sketch, "E15.0.4.6", {"start": v(48.99, 84.85) * mm, "end": v(58.65, 87.44) * mm, "construction": true});
            skArc(sketch, "E15.0.4.7", {"start": v(-23.86, 85.52) * mm, "mid": v(-19.41, 85.66) * mm, "end": v(-15.55, 87.86) * mm});
            skArc(sketch, "E15.0.4.8", {"start": v(-23.86, 85.52) * mm, "mid": v(-25.94, 89.28) * mm, "end": v(-29.32, 91.92) * mm});
            skArc(sketch, "E15.0.4.9", {"start": v(-13.15, 92.14) * mm, "mid": v(-15.98, 84.85) * mm, "end": v(-13.15, 77.56) * mm});
            skArc(sketch, "E15.0.4.10", {"start": v(-37.64, 92.14) * mm, "mid": v(-40.47, 84.85) * mm, "end": v(-37.64, 77.56) * mm});
            skArc(sketch, "E15.0.4.11", {"start": v(25.13, 85.52) * mm, "mid": v(29.58, 85.66) * mm, "end": v(33.44, 87.86) * mm});
            skArc(sketch, "E15.0.4.12", {"start": v(74.12, 71.38) * mm, "mid": v(69.23, 77.48) * mm, "end": v(61.5, 78.67) * mm});
            skArc(sketch, "E15.0.4.13", {"start": v(49.25, 83.97) * mm, "mid": v(47.14, 80.05) * mm, "end": v(47.12, 75.6) * mm});
            skArc(sketch, "E15.0.4.14", {"start": v(0.26, 83.97) * mm, "mid": v(-1.85, 80.05) * mm, "end": v(-1.87, 75.6) * mm});
            skArc(sketch, "E15.0.4.15", {"start": v(35.84, 92.14) * mm, "mid": v(33.01, 84.85) * mm, "end": v(35.84, 77.56) * mm});
            skArc(sketch, "E15.0.4.16", {"start": v(60.34, 92.14) * mm, "mid": v(56.18, 97.3) * mm, "end": v(49.63, 98.33) * mm});
            skArc(sketch, "E15.0.4.17", {"start": v(-24.5, 84.85) * mm, "mid": v(-26.89, 81) * mm, "end": v(-27.34, 76.5) * mm});
            skPoint(sketch, "E15.0.4.18", {"position": v(48.99, 70.71) * mm});
            skArc(sketch, "E15.0.4.19", {"start": v(48.99, 84.85) * mm, "mid": v(46.86, 88.85) * mm, "end": v(43.18, 91.5) * mm});
            skArc(sketch, "E15.0.4.20", {"start": v(-0.9, 85.07) * mm, "mid": v(-3.1, 81.39) * mm, "end": v(-3.7, 77.14) * mm});
            skArc(sketch, "E15.0.4.21", {"start": v(24.75, 83.97) * mm, "mid": v(22.65, 80.05) * mm, "end": v(22.63, 75.6) * mm});
            skArc(sketch, "E15.0.4.22", {"start": v(-48.35, 71.38) * mm, "mid": v(-41.8, 72.4) * mm, "end": v(-37.64, 77.56) * mm});
            skArc(sketch, "E15.0.4.23", {"start": v(73.48, 84.85) * mm, "mid": v(78.01, 84.7) * mm, "end": v(82.14, 86.56) * mm});
            skArc(sketch, "E15.0.4.24", {"start": v(0, 84.85) * mm, "mid": v(-2.13, 88.85) * mm, "end": v(-5.8, 91.5) * mm});
            skArc(sketch, "E15.0.4.25", {"start": v(-12.25, 91.92) * mm, "mid": v(-16.9, 98) * mm, "end": v(-24.5, 99) * mm});
            skArc(sketch, "E15.0.4.26", {"start": v(49.63, 85.52) * mm, "mid": v(54.07, 85.66) * mm, "end": v(57.94, 87.86) * mm});
            skArc(sketch, "E15.0.4.27", {"start": v(-23.86, 71.38) * mm, "mid": v(-28.75, 77.48) * mm, "end": v(-36.48, 78.67) * mm});
            skArc(sketch, "E15.0.4.28", {"start": v(23.6, 85.07) * mm, "mid": v(21.39, 81.39) * mm, "end": v(20.79, 77.14) * mm});
            skPoint(sketch, "E15.0.4.29", {"position": v(0, 70.71) * mm});
            skLineSegment(sketch, "E15.0.4.30", {"start": v(0, 84.85) * mm, "end": v(-14.4, 81) * mm, "construction": true});
            skArc(sketch, "E15.0.4.31", {"start": v(35.84, 92.14) * mm, "mid": v(31.68, 97.3) * mm, "end": v(25.13, 98.33) * mm});
            skArc(sketch, "E15.0.4.32", {"start": v(-25.4, 85.07) * mm, "mid": v(-27.6, 81.39) * mm, "end": v(-28.2, 77.14) * mm});
            skArc(sketch, "E15.0.4.33", {"start": v(-24.24, 83.97) * mm, "mid": v(-26.34, 80.05) * mm, "end": v(-26.36, 75.6) * mm});
            skArc(sketch, "E15.0.4.34", {"start": v(60.34, 92.14) * mm, "mid": v(57.5, 84.85) * mm, "end": v(60.34, 77.56) * mm});
            skArc(sketch, "E15.0.4.35", {"start": v(61.24, 91.92) * mm, "mid": v(56.58, 98) * mm, "end": v(48.99, 99) * mm});
            skArc(sketch, "E15.0.4.36", {"start": v(-48.99, 70.71) * mm, "mid": v(-53.65, 76.78) * mm, "end": v(-61.24, 77.78) * mm});
            skArc(sketch, "E15.0.4.37", {"start": v(-12.25, 91.92) * mm, "mid": v(-4.66, 92.92) * mm, "end": v(0, 99) * mm});
            skArc(sketch, "E15.0.4.38", {"start": v(73.48, 70.71) * mm, "mid": v(81.07, 71.7) * mm, "end": v(85.73, 77.78) * mm});
            skArc(sketch, "E15.0.4.39", {"start": v(-61.24, 91.92) * mm, "mid": v(-53.65, 92.92) * mm, "end": v(-48.99, 99) * mm});
            skArc(sketch, "E15.0.4.40", {"start": v(-13.15, 92.14) * mm, "mid": v(-17.3, 97.3) * mm, "end": v(-23.86, 98.33) * mm});
            skArc(sketch, "E15.0.4.41", {"start": v(73.48, 84.85) * mm, "mid": v(71.35, 88.85) * mm, "end": v(67.68, 91.5) * mm});
            skArc(sketch, "E15.0.4.42", {"start": v(48.99, 70.71) * mm, "mid": v(44.33, 76.78) * mm, "end": v(36.74, 77.78) * mm});
            skPoint(sketch, "E15.0.4.43", {"position": v(-24.5, 70.71) * mm});
            skPoint(sketch, "E15.0.4.44", {"position": v(61.24, 91.92) * mm});
            skArc(sketch, "E15.0.4.45", {"start": v(24.5, 70.71) * mm, "mid": v(19.84, 76.78) * mm, "end": v(12.25, 77.78) * mm});
            skArc(sketch, "E15.0.4.46", {"start": v(-23.86, 71.38) * mm, "mid": v(-17.3, 72.4) * mm, "end": v(-13.15, 77.56) * mm});
            skArc(sketch, "E15.0.4.47", {"start": v(-48.35, 71.38) * mm, "mid": v(-53.25, 77.48) * mm, "end": v(-60.98, 78.67) * mm});
            skArc(sketch, "E15.0.4.48", {"start": v(84.83, 92.14) * mm, "mid": v(82, 84.85) * mm, "end": v(84.83, 77.56) * mm});
            skArc(sketch, "E15.0.4.49", {"start": v(0.64, 71.38) * mm, "mid": v(-4.26, 77.48) * mm, "end": v(-11.99, 78.67) * mm});
            skArc(sketch, "E15.0.4.50", {"start": v(-37.64, 92.14) * mm, "mid": v(-41.8, 97.3) * mm, "end": v(-48.35, 98.33) * mm});
            skArc(sketch, "E15.0.4.51", {"start": v(49.63, 71.38) * mm, "mid": v(56.18, 72.4) * mm, "end": v(60.34, 77.56) * mm});
            skArc(sketch, "E15.0.4.52", {"start": v(48.1, 85.07) * mm, "mid": v(45.75, 88.85) * mm, "end": v(41.9, 91.1) * mm});
            skPoint(sketch, "E15.0.4.53", {"position": v(-48.99, 70.71) * mm});
            skArc(sketch, "E15.0.4.54", {"start": v(48.99, 70.71) * mm, "mid": v(56.58, 71.7) * mm, "end": v(61.24, 77.78) * mm});
            skArc(sketch, "E15.0.4.55", {"start": v(-48.99, 84.85) * mm, "mid": v(-44.46, 84.7) * mm, "end": v(-40.34, 86.56) * mm});
            skArc(sketch, "E15.0.4.56", {"start": v(-24.5, 84.85) * mm, "mid": v(-26.63, 88.85) * mm, "end": v(-30.3, 91.5) * mm});
            skArc(sketch, "E15.0.4.57", {"start": v(48.99, 84.85) * mm, "mid": v(46.6, 81) * mm, "end": v(46.14, 76.5) * mm});
            skArc(sketch, "E15.0.4.58", {"start": v(-61.24, 91.92) * mm, "mid": v(-64.17, 84.85) * mm, "end": v(-61.24, 77.78) * mm});
            skArc(sketch, "E15.0.4.59", {"start": v(-48.35, 85.52) * mm, "mid": v(-50.44, 89.28) * mm, "end": v(-53.82, 91.92) * mm});
            skArc(sketch, "E15.0.4.60", {"start": v(0, 70.71) * mm, "mid": v(7.59, 71.7) * mm, "end": v(12.25, 77.78) * mm});
            skPoint(sketch, "E15.0.4.61", {"position": v(-48.99, 84.85) * mm});
            skLineSegment(sketch, "E15.0.4.62", {"start": v(24.5, 84.85) * mm, "end": v(34.15, 87.44) * mm, "construction": true});
            skArc(sketch, "E15.0.4.63", {"start": v(11.35, 92.14) * mm, "mid": v(8.52, 84.85) * mm, "end": v(11.35, 77.56) * mm});
            skArc(sketch, "E15.0.4.64", {"start": v(-48.73, 83.97) * mm, "mid": v(-50.84, 80.05) * mm, "end": v(-50.86, 75.6) * mm});
            skArc(sketch, "E15.0.4.65", {"start": v(61.5, 91.04) * mm, "mid": v(59.1, 84.85) * mm, "end": v(61.5, 78.67) * mm});
            skArc(sketch, "E15.0.4.66", {"start": v(49.25, 83.97) * mm, "mid": v(53.54, 83.9) * mm, "end": v(57.53, 85.5) * mm});
            skArc(sketch, "E15.0.4.67", {"start": v(-48.35, 85.52) * mm, "mid": v(-43.9, 85.66) * mm, "end": v(-40.04, 87.86) * mm});
            skArc(sketch, "E15.0.4.68", {"start": v(74.12, 85.52) * mm, "mid": v(78.57, 85.66) * mm, "end": v(82.43, 87.86) * mm});
            skPoint(sketch, "E15.0.4.69", {"position": v(24.5, 70.71) * mm});
            skArc(sketch, "E15.0.4.70", {"start": v(0.64, 71.38) * mm, "mid": v(7.19, 72.4) * mm, "end": v(11.35, 77.56) * mm});
            skArc(sketch, "E15.0.4.71", {"start": v(37, 91.04) * mm, "mid": v(44.73, 92.23) * mm, "end": v(49.63, 98.33) * mm});
            skArc(sketch, "E15.0.4.72", {"start": v(85.73, 91.92) * mm, "mid": v(82.8, 84.85) * mm, "end": v(85.73, 77.78) * mm});
            skPoint(sketch, "E15.0.4.73", {"position": v(48.99, 84.85) * mm});
            skArc(sketch, "E15.0.4.74", {"start": v(37, 91.04) * mm, "mid": v(34.61, 84.85) * mm, "end": v(37, 78.67) * mm});
            skArc(sketch, "E15.0.4.75", {"start": v(25.13, 85.52) * mm, "mid": v(23.05, 89.28) * mm, "end": v(19.67, 91.92) * mm});
            skPoint(sketch, "E15.0.4.76", {"position": v(-12.25, 91.92) * mm});
            skArc(sketch, "E15.0.4.77", {"start": v(11.35, 92.14) * mm, "mid": v(7.19, 97.3) * mm, "end": v(0.64, 98.33) * mm});
            skLineSegment(sketch, "E15.0.4.78", {"start": v(73.48, 84.85) * mm, "end": v(59.08, 81) * mm, "construction": true});
            skArc(sketch, "E15.0.4.79", {"start": v(49.63, 85.52) * mm, "mid": v(47.54, 89.28) * mm, "end": v(44.16, 91.92) * mm});
            skArc(sketch, "E15.0.4.80", {"start": v(74.12, 85.52) * mm, "mid": v(72.04, 89.28) * mm, "end": v(68.66, 91.92) * mm});
            skPoint(sketch, "E15.0.4.81", {"position": v(12.25, 91.92) * mm});
            skLineSegment(sketch, "E15.0.4.82", {"start": v(-48.99, 84.85) * mm, "end": v(-63.4, 81) * mm, "construction": true});
            skArc(sketch, "E15.0.4.83", {"start": v(73.74, 83.97) * mm, "mid": v(78.04, 83.9) * mm, "end": v(82.02, 85.5) * mm});
            skArc(sketch, "E15.0.4.84", {"start": v(48.1, 85.07) * mm, "mid": v(45.88, 81.39) * mm, "end": v(45.28, 77.14) * mm});
            skArc(sketch, "E15.0.4.85", {"start": v(-11.99, 91.04) * mm, "mid": v(-4.26, 92.23) * mm, "end": v(0.64, 98.33) * mm});
            skArc(sketch, "E15.0.4.86", {"start": v(0.26, 83.97) * mm, "mid": v(4.55, 83.9) * mm, "end": v(8.54, 85.5) * mm});
            skArc(sketch, "E15.0.4.87", {"start": v(49.63, 71.38) * mm, "mid": v(44.73, 77.48) * mm, "end": v(37, 78.67) * mm});
            skArc(sketch, "E15.0.4.88", {"start": v(-24.24, 83.97) * mm, "mid": v(-19.94, 83.9) * mm, "end": v(-15.96, 85.5) * mm});
            skArc(sketch, "E15.0.4.89", {"start": v(36.74, 91.92) * mm, "mid": v(32.08, 98) * mm, "end": v(24.5, 99) * mm});
            skArc(sketch, "E15.0.4.90", {"start": v(24.5, 70.71) * mm, "mid": v(32.08, 71.7) * mm, "end": v(36.74, 77.78) * mm});
            skArc(sketch, "E15.0.4.91", {"start": v(23.6, 85.07) * mm, "mid": v(21.26, 88.85) * mm, "end": v(17.41, 91.1) * mm});
            skArc(sketch, "E15.0.4.92", {"start": v(-48.99, 84.85) * mm, "mid": v(-51.12, 88.85) * mm, "end": v(-54.8, 91.5) * mm});
            skArc(sketch, "E15.0.4.93", {"start": v(24.5, 84.85) * mm, "mid": v(22.1, 81) * mm, "end": v(21.65, 76.5) * mm});
            skArc(sketch, "E15.0.4.94", {"start": v(72.59, 85.07) * mm, "mid": v(70.38, 81.39) * mm, "end": v(69.78, 77.14) * mm});
            skArc(sketch, "E15.0.4.95", {"start": v(0.64, 85.52) * mm, "mid": v(5.08, 85.66) * mm, "end": v(8.95, 87.86) * mm});
            skArc(sketch, "E15.0.4.96", {"start": v(84.83, 92.14) * mm, "mid": v(80.67, 97.3) * mm, "end": v(74.12, 98.33) * mm});
            skArc(sketch, "E15.0.4.97", {"start": v(-49.89, 85.07) * mm, "mid": v(-52.1, 81.39) * mm, "end": v(-52.7, 77.14) * mm});
            skArc(sketch, "E15.0.4.98", {"start": v(74.12, 71.38) * mm, "mid": v(80.67, 72.4) * mm, "end": v(84.83, 77.56) * mm});
            skArc(sketch, "E15.0.4.99", {"start": v(0.64, 85.52) * mm, "mid": v(-1.45, 89.28) * mm, "end": v(-4.83, 91.92) * mm});
            skArc(sketch, "E15.0.4.100", {"start": v(-36.48, 91.04) * mm, "mid": v(-28.75, 92.23) * mm, "end": v(-23.86, 98.33) * mm});
            skArc(sketch, "E15.0.4.101", {"start": v(85.73, 91.92) * mm, "mid": v(81.07, 98) * mm, "end": v(73.48, 99) * mm});
            skArc(sketch, "E15.0.4.102", {"start": v(-36.74, 91.92) * mm, "mid": v(-41.4, 98) * mm, "end": v(-48.99, 99) * mm});
            skArc(sketch, "E15.0.4.103", {"start": v(0, 84.85) * mm, "mid": v(4.53, 84.7) * mm, "end": v(8.65, 86.56) * mm});
            skArc(sketch, "E15.0.4.104", {"start": v(-24.5, 70.71) * mm, "mid": v(-29.15, 76.78) * mm, "end": v(-36.74, 77.78) * mm});
            skArc(sketch, "E15.0.4.105", {"start": v(-60.98, 91.04) * mm, "mid": v(-53.25, 92.23) * mm, "end": v(-48.35, 98.33) * mm});
            skArc(sketch, "E15.0.4.106", {"start": v(-36.74, 91.92) * mm, "mid": v(-29.15, 92.92) * mm, "end": v(-24.5, 99) * mm});
            skArc(sketch, "E15.0.4.107", {"start": v(12.5, 91.04) * mm, "mid": v(10.12, 84.85) * mm, "end": v(12.5, 78.67) * mm});
            skArc(sketch, "E15.0.4.108", {"start": v(36.74, 91.92) * mm, "mid": v(44.33, 92.92) * mm, "end": v(48.99, 99) * mm});
            skArc(sketch, "E15.0.4.109", {"start": v(12.25, 91.92) * mm, "mid": v(19.84, 92.92) * mm, "end": v(24.5, 99) * mm});
            skPoint(sketch, "E15.0.4.110", {"position": v(-36.74, 91.92) * mm});
            skPoint(sketch, "E15.0.4.111", {"position": v(73.48, 70.71) * mm});
            skArc(sketch, "E15.0.4.112", {"start": v(12.25, 91.92) * mm, "mid": v(7.59, 98) * mm, "end": v(0, 99) * mm});
            skLineSegment(sketch, "E15.0.4.113", {"start": v(48.99, 84.85) * mm, "end": v(34.59, 81) * mm, "construction": true});
            skArc(sketch, "E15.0.4.114", {"start": v(-24.5, 70.71) * mm, "mid": v(-16.9, 71.7) * mm, "end": v(-12.25, 77.78) * mm});
            skArc(sketch, "E15.0.4.115", {"start": v(-48.73, 83.97) * mm, "mid": v(-44.44, 83.9) * mm, "end": v(-40.45, 85.5) * mm});
            skArc(sketch, "E15.0.4.116", {"start": v(-48.99, 70.71) * mm, "mid": v(-41.4, 71.7) * mm, "end": v(-36.74, 77.78) * mm});
            skArc(sketch, "E15.0.4.117", {"start": v(0, 70.71) * mm, "mid": v(-4.66, 76.78) * mm, "end": v(-12.25, 77.78) * mm});
            skArc(sketch, "E15.0.4.118", {"start": v(12.5, 91.04) * mm, "mid": v(20.24, 92.23) * mm, "end": v(25.13, 98.33) * mm});
            skArc(sketch, "E15.0.4.119", {"start": v(73.48, 70.71) * mm, "mid": v(68.83, 76.78) * mm, "end": v(61.24, 77.78) * mm});
            skLineSegment(sketch, "E15.0.4.120", {"start": v(-24.5, 84.85) * mm, "end": v(-38.9, 81) * mm, "construction": true});
            skArc(sketch, "E15.0.4.121", {"start": v(24.75, 83.97) * mm, "mid": v(29.05, 83.9) * mm, "end": v(33.03, 85.5) * mm});
            skArc(sketch, "E15.0.4.122", {"start": v(0, 84.85) * mm, "mid": v(-2.4, 81) * mm, "end": v(-2.85, 76.5) * mm});
            skArc(sketch, "E15.0.4.123", {"start": v(61.24, 91.92) * mm, "mid": v(68.83, 92.92) * mm, "end": v(73.48, 99) * mm});
            skPoint(sketch, "E15.0.4.124", {"position": v(36.74, 91.92) * mm});
            skArc(sketch, "E15.0.4.125", {"start": v(-49.89, 85.07) * mm, "mid": v(-52.23, 88.85) * mm, "end": v(-56.07, 91.1) * mm});
            skPoint(sketch, "E15.0.4.126", {"position": v(-61.24, 91.92) * mm});
            skLineSegment(sketch, "E15.0.4.127", {"start": v(-48.99, 84.85) * mm, "end": v(-39.33, 87.44) * mm, "construction": true});
            skArc(sketch, "E15.0.4.128", {"start": v(-36.74, 91.92) * mm, "mid": v(-39.67, 84.85) * mm, "end": v(-36.74, 77.78) * mm});
            skPoint(sketch, "E15.0.4.129", {"position": v(-49.03, 84.78) * mm});
            skArc(sketch, "E15.0.4.130", {"start": v(48.99, 84.85) * mm, "mid": v(53.52, 84.7) * mm, "end": v(57.64, 86.56) * mm});
            skArc(sketch, "E15.0.4.131", {"start": v(-0.9, 85.07) * mm, "mid": v(-3.24, 88.85) * mm, "end": v(-7.08, 91.1) * mm});
            skArc(sketch, "E15.0.4.132", {"start": v(25.13, 71.38) * mm, "mid": v(31.68, 72.4) * mm, "end": v(35.84, 77.56) * mm});
            skLineSegment(sketch, "E15.0.4.133", {"start": v(-58.65, 68.12) * mm, "end": v(-34.15, 68.12) * mm, "construction": true});
            skArc(sketch, "E15.0.4.134", {"start": v(36.74, 91.92) * mm, "mid": v(33.81, 84.85) * mm, "end": v(36.74, 77.78) * mm});
            skArc(sketch, "E15.0.4.135", {"start": v(72.59, 85.07) * mm, "mid": v(70.25, 88.85) * mm, "end": v(66.4, 91.1) * mm});
            skArc(sketch, "E15.0.4.136", {"start": v(24.5, 84.85) * mm, "mid": v(22.36, 88.85) * mm, "end": v(18.69, 91.5) * mm});
            skArc(sketch, "E15.0.4.137", {"start": v(-12.25, 91.92) * mm, "mid": v(-15.18, 84.85) * mm, "end": v(-12.25, 77.78) * mm});
            skLineSegment(sketch, "E15.0.4.138", {"start": v(-24.5, 84.85) * mm, "end": v(-14.84, 87.44) * mm, "construction": true});
            skPoint(sketch, "E15.0.4.139", {"position": v(24.5, 84.85) * mm});
            skLineSegment(sketch, "E15.0.4.140", {"start": v(0, 84.85) * mm, "end": v(9.66, 87.44) * mm, "construction": true});
            skArc(sketch, "E15.0.4.141", {"start": v(12.25, 91.92) * mm, "mid": v(9.32, 84.85) * mm, "end": v(12.25, 77.78) * mm});
            skArc(sketch, "E15.0.4.142", {"start": v(73.48, 84.85) * mm, "mid": v(71.1, 81) * mm, "end": v(70.64, 76.5) * mm});
            skArc(sketch, "E15.0.4.143", {"start": v(-36.48, 91.04) * mm, "mid": v(-38.87, 84.85) * mm, "end": v(-36.48, 78.67) * mm});
            skArc(sketch, "E15.0.4.144", {"start": v(25.13, 71.38) * mm, "mid": v(20.24, 77.48) * mm, "end": v(12.5, 78.67) * mm});
            skArc(sketch, "E15.0.4.145", {"start": v(24.5, 84.85) * mm, "mid": v(29.02, 84.7) * mm, "end": v(33.15, 86.56) * mm});
            skArc(sketch, "E15.0.4.146", {"start": v(61.24, 91.92) * mm, "mid": v(58.3, 84.85) * mm, "end": v(61.24, 77.78) * mm});
            skArc(sketch, "E15.0.4.147", {"start": v(-11.99, 91.04) * mm, "mid": v(-14.38, 84.85) * mm, "end": v(-11.99, 78.67) * mm});
            skPoint(sketch, "E15.0.4.148", {"position": v(73.48, 84.85) * mm});
            skPoint(sketch, "E15.0.4.149", {"position": v(-24.5, 84.85) * mm});
            skArc(sketch, "E15.0.4.150", {"start": v(-24.5, 84.85) * mm, "mid": v(-19.97, 84.7) * mm, "end": v(-15.84, 86.56) * mm});
            skArc(sketch, "E15.0.4.151", {"start": v(61.5, 91.04) * mm, "mid": v(69.23, 92.23) * mm, "end": v(74.12, 98.33) * mm});
            skArc(sketch, "E15.0.4.152", {"start": v(-25.4, 85.07) * mm, "mid": v(-27.73, 88.85) * mm, "end": v(-31.57, 91.1) * mm});
            skArc(sketch, "E15.0.4.153", {"start": v(-12.25, 91.92) * mm, "mid": v(-15.18, 84.85) * mm, "end": v(-12.25, 77.78) * mm});
            skPoint(sketch, "E15.0.4.154", {"position": v(24.5, 84.85) * mm});
            skArc(sketch, "E15.0.4.155", {"start": v(61.24, 91.92) * mm, "mid": v(58.3, 84.85) * mm, "end": v(61.24, 77.78) * mm});
            skPoint(sketch, "E15.0.4.156", {"position": v(73.48, 84.85) * mm});
            skArc(sketch, "E15.0.4.157", {"start": v(-36.74, 91.92) * mm, "mid": v(-39.67, 84.85) * mm, "end": v(-36.74, 77.78) * mm});
            skPoint(sketch, "E15.0.4.158", {"position": v(0, 84.85) * mm});
            skArc(sketch, "E15.0.4.159", {"start": v(12.25, 91.92) * mm, "mid": v(9.32, 84.85) * mm, "end": v(12.25, 77.78) * mm});
            skArc(sketch, "E15.0.4.160", {"start": v(36.74, 91.92) * mm, "mid": v(33.81, 84.85) * mm, "end": v(36.74, 77.78) * mm});
            skPoint(sketch, "E15.0.4.161", {"position": v(-48.99, 84.85) * mm});
            skPoint(sketch, "E15.0.4.162", {"position": v(-24.5, 84.85) * mm});
            skPoint(sketch, "E15.0.4.163", {"position": v(48.99, 84.85) * mm});
            skPoint(sketch, "E15.0.4.164", {"position": v(73.48, 84.85) * mm});
            skPoint(sketch, "E15.0.4.165", {"position": v(48.99, 84.85) * mm});
            skPoint(sketch, "E15.0.4.166", {"position": v(-24.5, 84.85) * mm});
            skPoint(sketch, "E15.0.4.167", {"position": v(24.5, 84.85) * mm});
            skPoint(sketch, "E15.0.4.168", {"position": v(-48.99, 84.85) * mm});
            skPoint(sketch, "E15.0.4.169", {"position": v(0, 84.85) * mm});
            skPoint(sketch, "E15.0.4.170", {"position": v(73.48, 84.85) * mm});
            skPoint(sketch, "E15.0.4.171", {"position": v(-24.5, 84.85) * mm});
            skPoint(sketch, "E15.0.4.172", {"position": v(-48.99, 84.85) * mm});
            skPoint(sketch, "E15.0.4.173", {"position": v(48.99, 84.85) * mm});
            skPoint(sketch, "E15.0.4.174", {"position": v(0, 84.85) * mm});
            skPoint(sketch, "E15.0.4.175", {"position": v(24.46, 84.78) * mm});
            skPoint(sketch, "E15.0.4.176", {"position": v(-0.04, 84.78) * mm});
            skPoint(sketch, "E15.0.4.177", {"position": v(73.45, 84.78) * mm});
            skPoint(sketch, "E15.0.4.178", {"position": v(24.5, 84.85) * mm});
            skPoint(sketch, "E15.0.4.179", {"position": v(48.95, 84.78) * mm});
            skPoint(sketch, "E15.0.4.180", {"position": v(-24.53, 84.78) * mm});
            skLineSegment(sketch, "E15.0.5.0", {"start": v(61.24, 106.07) * mm, "end": v(70.9, 108.65) * mm, "construction": true});
            skArc(sketch, "E15.0.5.1", {"start": v(-73.22, 112.25) * mm, "mid": v(-75.61, 106.07) * mm, "end": v(-73.22, 99.88) * mm});
            skArc(sketch, "E15.0.5.2", {"start": v(61.5, 105.18) * mm, "mid": v(59.4, 101.26) * mm, "end": v(59.37, 96.81) * mm});
            skArc(sketch, "E15.0.5.3", {"start": v(-61.24, 106.07) * mm, "mid": v(-63.63, 102.22) * mm, "end": v(-64.08, 97.72) * mm});
            skLineSegment(sketch, "E15.0.5.4", {"start": v(12.25, 106.07) * mm, "end": v(-2.15, 102.2) * mm, "construction": true});
            skPoint(sketch, "E15.0.5.5", {"position": v(-12.25, 106.07) * mm});
            skLineSegment(sketch, "E15.0.5.6", {"start": v(36.74, 106.07) * mm, "end": v(46.4, 108.65) * mm, "construction": true});
            skArc(sketch, "E15.0.5.7", {"start": v(-36.1, 106.73) * mm, "mid": v(-31.66, 106.87) * mm, "end": v(-27.8, 109.08) * mm});
            skArc(sketch, "E15.0.5.8", {"start": v(-36.1, 106.73) * mm, "mid": v(-38.19, 110.5) * mm, "end": v(-41.57, 113.14) * mm});
            skArc(sketch, "E15.0.5.9", {"start": v(-25.4, 113.36) * mm, "mid": v(-28.22, 106.07) * mm, "end": v(-25.4, 98.78) * mm});
            skArc(sketch, "E15.0.5.10", {"start": v(-49.89, 113.36) * mm, "mid": v(-52.72, 106.07) * mm, "end": v(-49.89, 98.78) * mm});
            skArc(sketch, "E15.0.5.11", {"start": v(12.89, 106.73) * mm, "mid": v(17.33, 106.87) * mm, "end": v(21.2, 109.08) * mm});
            skArc(sketch, "E15.0.5.12", {"start": v(61.88, 92.6) * mm, "mid": v(56.98, 98.69) * mm, "end": v(49.25, 99.88) * mm});
            skArc(sketch, "E15.0.5.13", {"start": v(37, 105.18) * mm, "mid": v(34.9, 101.26) * mm, "end": v(34.88, 96.81) * mm});
            skArc(sketch, "E15.0.5.14", {"start": v(-11.99, 105.18) * mm, "mid": v(-14.1, 101.26) * mm, "end": v(-14.11, 96.81) * mm});
            skArc(sketch, "E15.0.5.15", {"start": v(23.6, 113.36) * mm, "mid": v(20.77, 106.07) * mm, "end": v(23.6, 98.78) * mm});
            skArc(sketch, "E15.0.5.16", {"start": v(48.1, 113.36) * mm, "mid": v(43.93, 118.52) * mm, "end": v(37.38, 119.54) * mm});
            skArc(sketch, "E15.0.5.17", {"start": v(-36.74, 106.07) * mm, "mid": v(-39.14, 102.22) * mm, "end": v(-39.59, 97.72) * mm});
            skPoint(sketch, "E15.0.5.18", {"position": v(36.74, 91.92) * mm});
            skArc(sketch, "E15.0.5.19", {"start": v(36.74, 106.07) * mm, "mid": v(34.61, 110.06) * mm, "end": v(30.93, 112.7) * mm});
            skArc(sketch, "E15.0.5.20", {"start": v(-13.15, 106.28) * mm, "mid": v(-15.36, 102.6) * mm, "end": v(-15.96, 98.35) * mm});
            skArc(sketch, "E15.0.5.21", {"start": v(12.5, 105.18) * mm, "mid": v(10.4, 101.26) * mm, "end": v(10.38, 96.81) * mm});
            skArc(sketch, "E15.0.5.22", {"start": v(-60.6, 92.6) * mm, "mid": v(-54.05, 93.62) * mm, "end": v(-49.89, 98.78) * mm});
            skArc(sketch, "E15.0.5.23", {"start": v(61.24, 106.07) * mm, "mid": v(65.76, 105.91) * mm, "end": v(69.9, 107.78) * mm});
            skArc(sketch, "E15.0.5.24", {"start": v(-12.25, 106.07) * mm, "mid": v(-14.38, 110.06) * mm, "end": v(-18.06, 112.7) * mm});
            skArc(sketch, "E15.0.5.25", {"start": v(-24.5, 113.14) * mm, "mid": v(-29.15, 119.2) * mm, "end": v(-36.74, 120.2) * mm});
            skArc(sketch, "E15.0.5.26", {"start": v(37.38, 106.73) * mm, "mid": v(41.83, 106.87) * mm, "end": v(45.69, 109.08) * mm});
            skArc(sketch, "E15.0.5.27", {"start": v(-36.1, 92.6) * mm, "mid": v(-41, 98.69) * mm, "end": v(-48.73, 99.88) * mm});
            skArc(sketch, "E15.0.5.28", {"start": v(11.35, 106.28) * mm, "mid": v(9.14, 102.6) * mm, "end": v(8.54, 98.35) * mm});
            skPoint(sketch, "E15.0.5.29", {"position": v(-12.25, 91.92) * mm});
            skLineSegment(sketch, "E15.0.5.30", {"start": v(-12.25, 106.07) * mm, "end": v(-26.65, 102.2) * mm, "construction": true});
            skArc(sketch, "E15.0.5.31", {"start": v(23.6, 113.36) * mm, "mid": v(19.44, 118.52) * mm, "end": v(12.89, 119.54) * mm});
            skArc(sketch, "E15.0.5.32", {"start": v(-37.64, 106.28) * mm, "mid": v(-39.85, 102.6) * mm, "end": v(-40.45, 98.35) * mm});
            skArc(sketch, "E15.0.5.33", {"start": v(-36.48, 105.18) * mm, "mid": v(-38.59, 101.26) * mm, "end": v(-38.6, 96.81) * mm});
            skArc(sketch, "E15.0.5.34", {"start": v(48.1, 113.36) * mm, "mid": v(45.26, 106.07) * mm, "end": v(48.1, 98.78) * mm});
            skArc(sketch, "E15.0.5.35", {"start": v(48.99, 113.14) * mm, "mid": v(44.33, 119.2) * mm, "end": v(36.74, 120.2) * mm});
            skArc(sketch, "E15.0.5.36", {"start": v(-61.24, 91.92) * mm, "mid": v(-65.9, 98) * mm, "end": v(-73.48, 99) * mm});
            skArc(sketch, "E15.0.5.37", {"start": v(-24.5, 113.14) * mm, "mid": v(-16.9, 114.14) * mm, "end": v(-12.25, 120.2) * mm});
            skArc(sketch, "E15.0.5.38", {"start": v(61.24, 91.92) * mm, "mid": v(68.83, 92.92) * mm, "end": v(73.48, 99) * mm});
            skArc(sketch, "E15.0.5.39", {"start": v(-73.48, 113.14) * mm, "mid": v(-65.9, 114.14) * mm, "end": v(-61.24, 120.2) * mm});
            skArc(sketch, "E15.0.5.40", {"start": v(-25.4, 113.36) * mm, "mid": v(-29.55, 118.52) * mm, "end": v(-36.1, 119.54) * mm});
            skArc(sketch, "E15.0.5.41", {"start": v(61.24, 106.07) * mm, "mid": v(59.1, 110.06) * mm, "end": v(55.43, 112.7) * mm});
            skArc(sketch, "E15.0.5.42", {"start": v(36.74, 91.92) * mm, "mid": v(32.08, 98) * mm, "end": v(24.5, 99) * mm});
            skPoint(sketch, "E15.0.5.43", {"position": v(-36.74, 91.92) * mm});
            skPoint(sketch, "E15.0.5.44", {"position": v(48.99, 113.14) * mm});
            skArc(sketch, "E15.0.5.45", {"start": v(12.25, 91.92) * mm, "mid": v(7.59, 98) * mm, "end": v(0, 99) * mm});
            skArc(sketch, "E15.0.5.46", {"start": v(-36.1, 92.6) * mm, "mid": v(-29.55, 93.62) * mm, "end": v(-25.4, 98.78) * mm});
            skArc(sketch, "E15.0.5.47", {"start": v(-60.6, 92.6) * mm, "mid": v(-65.5, 98.69) * mm, "end": v(-73.22, 99.88) * mm});
            skArc(sketch, "E15.0.5.48", {"start": v(72.59, 113.36) * mm, "mid": v(69.76, 106.07) * mm, "end": v(72.59, 98.78) * mm});
            skArc(sketch, "E15.0.5.49", {"start": v(-11.6, 92.6) * mm, "mid": v(-16.5, 98.69) * mm, "end": v(-24.24, 99.88) * mm});
            skArc(sketch, "E15.0.5.50", {"start": v(-49.89, 113.36) * mm, "mid": v(-54.05, 118.52) * mm, "end": v(-60.6, 119.54) * mm});
            skArc(sketch, "E15.0.5.51", {"start": v(37.38, 92.6) * mm, "mid": v(43.93, 93.62) * mm, "end": v(48.1, 98.78) * mm});
            skArc(sketch, "E15.0.5.52", {"start": v(35.84, 106.28) * mm, "mid": v(33.5, 110.07) * mm, "end": v(29.66, 112.3) * mm});
            skPoint(sketch, "E15.0.5.53", {"position": v(-61.24, 91.92) * mm});
            skArc(sketch, "E15.0.5.54", {"start": v(36.74, 91.92) * mm, "mid": v(44.33, 92.92) * mm, "end": v(48.99, 99) * mm});
            skArc(sketch, "E15.0.5.55", {"start": v(-61.24, 106.07) * mm, "mid": v(-56.71, 105.91) * mm, "end": v(-52.58, 107.78) * mm});
            skArc(sketch, "E15.0.5.56", {"start": v(-36.74, 106.07) * mm, "mid": v(-38.87, 110.06) * mm, "end": v(-42.55, 112.7) * mm});
            skArc(sketch, "E15.0.5.57", {"start": v(36.74, 106.07) * mm, "mid": v(34.35, 102.22) * mm, "end": v(33.9, 97.72) * mm});
            skArc(sketch, "E15.0.5.58", {"start": v(-73.48, 113.14) * mm, "mid": v(-76.41, 106.07) * mm, "end": v(-73.48, 99) * mm});
            skArc(sketch, "E15.0.5.59", {"start": v(-60.6, 106.73) * mm, "mid": v(-62.68, 110.5) * mm, "end": v(-66.07, 113.14) * mm});
            skArc(sketch, "E15.0.5.60", {"start": v(-12.25, 91.92) * mm, "mid": v(-4.66, 92.92) * mm, "end": v(0, 99) * mm});
            skPoint(sketch, "E15.0.5.61", {"position": v(-61.24, 106.07) * mm});
            skLineSegment(sketch, "E15.0.5.62", {"start": v(12.25, 106.07) * mm, "end": v(21.9, 108.65) * mm, "construction": true});
            skArc(sketch, "E15.0.5.63", {"start": v(-0.9, 113.36) * mm, "mid": v(-3.73, 106.07) * mm, "end": v(-0.9, 98.78) * mm});
            skArc(sketch, "E15.0.5.64", {"start": v(-60.98, 105.18) * mm, "mid": v(-63.08, 101.26) * mm, "end": v(-63.1, 96.81) * mm});
            skArc(sketch, "E15.0.5.65", {"start": v(49.25, 112.25) * mm, "mid": v(46.86, 106.07) * mm, "end": v(49.25, 99.88) * mm});
            skArc(sketch, "E15.0.5.66", {"start": v(37, 105.18) * mm, "mid": v(41.3, 105.1) * mm, "end": v(45.28, 106.71) * mm});
            skArc(sketch, "E15.0.5.67", {"start": v(-60.6, 106.73) * mm, "mid": v(-56.15, 106.87) * mm, "end": v(-52.3, 109.08) * mm});
            skArc(sketch, "E15.0.5.68", {"start": v(61.88, 106.73) * mm, "mid": v(66.32, 106.87) * mm, "end": v(70.18, 109.08) * mm});
            skPoint(sketch, "E15.0.5.69", {"position": v(12.25, 91.92) * mm});
            skArc(sketch, "E15.0.5.70", {"start": v(-11.6, 92.6) * mm, "mid": v(-5.06, 93.62) * mm, "end": v(-0.9, 98.78) * mm});
            skArc(sketch, "E15.0.5.71", {"start": v(24.75, 112.25) * mm, "mid": v(32.48, 113.44) * mm, "end": v(37.38, 119.54) * mm});
            skArc(sketch, "E15.0.5.72", {"start": v(73.48, 113.14) * mm, "mid": v(70.56, 106.07) * mm, "end": v(73.48, 99) * mm});
            skPoint(sketch, "E15.0.5.73", {"position": v(36.74, 106.07) * mm});
            skArc(sketch, "E15.0.5.74", {"start": v(24.75, 112.25) * mm, "mid": v(22.37, 106.07) * mm, "end": v(24.75, 99.88) * mm});
            skArc(sketch, "E15.0.5.75", {"start": v(12.89, 106.73) * mm, "mid": v(10.8, 110.5) * mm, "end": v(7.42, 113.14) * mm});
            skPoint(sketch, "E15.0.5.76", {"position": v(-24.5, 113.14) * mm});
            skArc(sketch, "E15.0.5.77", {"start": v(-0.9, 113.36) * mm, "mid": v(-5.06, 118.52) * mm, "end": v(-11.6, 119.54) * mm});
            skLineSegment(sketch, "E15.0.5.78", {"start": v(61.24, 106.07) * mm, "end": v(46.84, 102.2) * mm, "construction": true});
            skArc(sketch, "E15.0.5.79", {"start": v(37.38, 106.73) * mm, "mid": v(35.3, 110.5) * mm, "end": v(31.91, 113.14) * mm});
            skArc(sketch, "E15.0.5.80", {"start": v(61.88, 106.73) * mm, "mid": v(59.8, 110.5) * mm, "end": v(56.4, 113.14) * mm});
            skPoint(sketch, "E15.0.5.81", {"position": v(0, 113.14) * mm});
            skLineSegment(sketch, "E15.0.5.82", {"start": v(-61.24, 106.07) * mm, "end": v(-75.64, 102.2) * mm, "construction": true});
            skArc(sketch, "E15.0.5.83", {"start": v(61.5, 105.18) * mm, "mid": v(65.8, 105.1) * mm, "end": v(69.78, 106.71) * mm});
            skArc(sketch, "E15.0.5.84", {"start": v(35.84, 106.28) * mm, "mid": v(33.63, 102.6) * mm, "end": v(33.03, 98.35) * mm});
            skArc(sketch, "E15.0.5.85", {"start": v(-24.24, 112.25) * mm, "mid": v(-16.5, 113.44) * mm, "end": v(-11.6, 119.54) * mm});
            skArc(sketch, "E15.0.5.86", {"start": v(-11.99, 105.18) * mm, "mid": v(-7.7, 105.1) * mm, "end": v(-3.7, 106.71) * mm});
            skArc(sketch, "E15.0.5.87", {"start": v(37.38, 92.6) * mm, "mid": v(32.48, 98.69) * mm, "end": v(24.75, 99.88) * mm});
            skArc(sketch, "E15.0.5.88", {"start": v(-36.48, 105.18) * mm, "mid": v(-32.19, 105.1) * mm, "end": v(-28.2, 106.71) * mm});
            skArc(sketch, "E15.0.5.89", {"start": v(24.5, 113.14) * mm, "mid": v(19.84, 119.2) * mm, "end": v(12.25, 120.2) * mm});
            skArc(sketch, "E15.0.5.90", {"start": v(12.25, 91.92) * mm, "mid": v(19.84, 92.92) * mm, "end": v(24.5, 99) * mm});
            skArc(sketch, "E15.0.5.91", {"start": v(11.35, 106.28) * mm, "mid": v(9, 110.07) * mm, "end": v(5.17, 112.3) * mm});
            skArc(sketch, "E15.0.5.92", {"start": v(-61.24, 106.07) * mm, "mid": v(-63.37, 110.06) * mm, "end": v(-67.05, 112.7) * mm});
            skArc(sketch, "E15.0.5.93", {"start": v(12.25, 106.07) * mm, "mid": v(9.85, 102.22) * mm, "end": v(9.4, 97.72) * mm});
            skArc(sketch, "E15.0.5.94", {"start": v(60.34, 106.28) * mm, "mid": v(58.13, 102.6) * mm, "end": v(57.53, 98.35) * mm});
            skArc(sketch, "E15.0.5.95", {"start": v(-11.6, 106.73) * mm, "mid": v(-7.16, 106.87) * mm, "end": v(-3.3, 109.08) * mm});
            skArc(sketch, "E15.0.5.96", {"start": v(72.59, 113.36) * mm, "mid": v(68.43, 118.52) * mm, "end": v(61.88, 119.54) * mm});
            skArc(sketch, "E15.0.5.97", {"start": v(-62.14, 106.28) * mm, "mid": v(-64.35, 102.6) * mm, "end": v(-64.95, 98.35) * mm});
            skArc(sketch, "E15.0.5.98", {"start": v(61.88, 92.6) * mm, "mid": v(68.43, 93.62) * mm, "end": v(72.59, 98.78) * mm});
            skArc(sketch, "E15.0.5.99", {"start": v(-11.6, 106.73) * mm, "mid": v(-13.7, 110.5) * mm, "end": v(-17.08, 113.14) * mm});
            skArc(sketch, "E15.0.5.100", {"start": v(-48.73, 112.25) * mm, "mid": v(-41, 113.44) * mm, "end": v(-36.1, 119.54) * mm});
            skArc(sketch, "E15.0.5.101", {"start": v(73.48, 113.14) * mm, "mid": v(68.83, 119.2) * mm, "end": v(61.24, 120.2) * mm});
            skArc(sketch, "E15.0.5.102", {"start": v(-48.99, 113.14) * mm, "mid": v(-53.65, 119.2) * mm, "end": v(-61.24, 120.2) * mm});
            skArc(sketch, "E15.0.5.103", {"start": v(-12.25, 106.07) * mm, "mid": v(-7.72, 105.91) * mm, "end": v(-3.6, 107.78) * mm});
            skArc(sketch, "E15.0.5.104", {"start": v(-36.74, 91.92) * mm, "mid": v(-41.4, 98) * mm, "end": v(-48.99, 99) * mm});
            skArc(sketch, "E15.0.5.105", {"start": v(-73.22, 112.25) * mm, "mid": v(-65.5, 113.44) * mm, "end": v(-60.6, 119.54) * mm});
            skArc(sketch, "E15.0.5.106", {"start": v(-48.99, 113.14) * mm, "mid": v(-41.4, 114.14) * mm, "end": v(-36.74, 120.2) * mm});
            skArc(sketch, "E15.0.5.107", {"start": v(0.26, 112.25) * mm, "mid": v(-2.13, 106.07) * mm, "end": v(0.26, 99.88) * mm});
            skArc(sketch, "E15.0.5.108", {"start": v(24.5, 113.14) * mm, "mid": v(32.08, 114.14) * mm, "end": v(36.74, 120.2) * mm});
            skArc(sketch, "E15.0.5.109", {"start": v(0, 113.14) * mm, "mid": v(7.59, 114.14) * mm, "end": v(12.25, 120.2) * mm});
            skPoint(sketch, "E15.0.5.110", {"position": v(-48.99, 113.14) * mm});
            skPoint(sketch, "E15.0.5.111", {"position": v(61.24, 91.92) * mm});
            skArc(sketch, "E15.0.5.112", {"start": v(0, 113.14) * mm, "mid": v(-4.66, 119.2) * mm, "end": v(-12.25, 120.2) * mm});
            skLineSegment(sketch, "E15.0.5.113", {"start": v(36.74, 106.07) * mm, "end": v(22.34, 102.2) * mm, "construction": true});
            skArc(sketch, "E15.0.5.114", {"start": v(-36.74, 91.92) * mm, "mid": v(-29.15, 92.92) * mm, "end": v(-24.5, 99) * mm});
            skArc(sketch, "E15.0.5.115", {"start": v(-60.98, 105.18) * mm, "mid": v(-56.68, 105.1) * mm, "end": v(-52.7, 106.71) * mm});
            skArc(sketch, "E15.0.5.116", {"start": v(-61.24, 91.92) * mm, "mid": v(-53.65, 92.92) * mm, "end": v(-48.99, 99) * mm});
            skArc(sketch, "E15.0.5.117", {"start": v(-12.25, 91.92) * mm, "mid": v(-16.9, 98) * mm, "end": v(-24.5, 99) * mm});
            skArc(sketch, "E15.0.5.118", {"start": v(0.26, 112.25) * mm, "mid": v(7.99, 113.44) * mm, "end": v(12.89, 119.54) * mm});
            skArc(sketch, "E15.0.5.119", {"start": v(61.24, 91.92) * mm, "mid": v(56.58, 98) * mm, "end": v(48.99, 99) * mm});
            skLineSegment(sketch, "E15.0.5.120", {"start": v(-36.74, 106.07) * mm, "end": v(-51.14, 102.2) * mm, "construction": true});
            skArc(sketch, "E15.0.5.121", {"start": v(12.5, 105.18) * mm, "mid": v(16.8, 105.1) * mm, "end": v(20.79, 106.71) * mm});
            skArc(sketch, "E15.0.5.122", {"start": v(-12.25, 106.07) * mm, "mid": v(-14.64, 102.22) * mm, "end": v(-15.1, 97.72) * mm});
            skArc(sketch, "E15.0.5.123", {"start": v(48.99, 113.14) * mm, "mid": v(56.58, 114.14) * mm, "end": v(61.24, 120.2) * mm});
            skPoint(sketch, "E15.0.5.124", {"position": v(24.5, 113.14) * mm});
            skArc(sketch, "E15.0.5.125", {"start": v(-62.14, 106.28) * mm, "mid": v(-64.48, 110.07) * mm, "end": v(-68.32, 112.3) * mm});
            skPoint(sketch, "E15.0.5.126", {"position": v(-73.48, 113.14) * mm});
            skLineSegment(sketch, "E15.0.5.127", {"start": v(-61.24, 106.07) * mm, "end": v(-51.58, 108.65) * mm, "construction": true});
            skArc(sketch, "E15.0.5.128", {"start": v(-48.99, 113.14) * mm, "mid": v(-51.92, 106.07) * mm, "end": v(-48.99, 99) * mm});
            skPoint(sketch, "E15.0.5.129", {"position": v(-61.27, 106) * mm});
            skArc(sketch, "E15.0.5.130", {"start": v(36.74, 106.07) * mm, "mid": v(41.27, 105.91) * mm, "end": v(45.4, 107.78) * mm});
            skArc(sketch, "E15.0.5.131", {"start": v(-13.15, 106.28) * mm, "mid": v(-15.49, 110.07) * mm, "end": v(-19.33, 112.3) * mm});
            skArc(sketch, "E15.0.5.132", {"start": v(12.89, 92.6) * mm, "mid": v(19.44, 93.62) * mm, "end": v(23.6, 98.78) * mm});
            skLineSegment(sketch, "E15.0.5.133", {"start": v(-70.9, 89.34) * mm, "end": v(-46.4, 89.34) * mm, "construction": true});
            skArc(sketch, "E15.0.5.134", {"start": v(24.5, 113.14) * mm, "mid": v(21.57, 106.07) * mm, "end": v(24.5, 99) * mm});
            skArc(sketch, "E15.0.5.135", {"start": v(60.34, 106.28) * mm, "mid": v(58, 110.07) * mm, "end": v(54.16, 112.3) * mm});
            skArc(sketch, "E15.0.5.136", {"start": v(12.25, 106.07) * mm, "mid": v(10.12, 110.06) * mm, "end": v(6.44, 112.7) * mm});
            skArc(sketch, "E15.0.5.137", {"start": v(-24.5, 113.14) * mm, "mid": v(-27.42, 106.07) * mm, "end": v(-24.5, 99) * mm});
            skLineSegment(sketch, "E15.0.5.138", {"start": v(-36.74, 106.07) * mm, "end": v(-27.08, 108.65) * mm, "construction": true});
            skPoint(sketch, "E15.0.5.139", {"position": v(12.25, 106.07) * mm});
            skLineSegment(sketch, "E15.0.5.140", {"start": v(-12.25, 106.07) * mm, "end": v(-2.59, 108.65) * mm, "construction": true});
            skArc(sketch, "E15.0.5.141", {"start": v(0, 113.14) * mm, "mid": v(-2.93, 106.07) * mm, "end": v(0, 99) * mm});
            skArc(sketch, "E15.0.5.142", {"start": v(61.24, 106.07) * mm, "mid": v(58.84, 102.22) * mm, "end": v(58.4, 97.72) * mm});
            skArc(sketch, "E15.0.5.143", {"start": v(-48.73, 112.25) * mm, "mid": v(-51.12, 106.07) * mm, "end": v(-48.73, 99.88) * mm});
            skArc(sketch, "E15.0.5.144", {"start": v(12.89, 92.6) * mm, "mid": v(7.99, 98.69) * mm, "end": v(0.26, 99.88) * mm});
            skArc(sketch, "E15.0.5.145", {"start": v(12.25, 106.07) * mm, "mid": v(16.77, 105.91) * mm, "end": v(20.9, 107.78) * mm});
            skArc(sketch, "E15.0.5.146", {"start": v(48.99, 113.14) * mm, "mid": v(46.06, 106.07) * mm, "end": v(48.99, 99) * mm});
            skArc(sketch, "E15.0.5.147", {"start": v(-24.24, 112.25) * mm, "mid": v(-26.62, 106.07) * mm, "end": v(-24.24, 99.88) * mm});
            skPoint(sketch, "E15.0.5.148", {"position": v(61.24, 106.07) * mm});
            skPoint(sketch, "E15.0.5.149", {"position": v(-36.74, 106.07) * mm});
            skArc(sketch, "E15.0.5.150", {"start": v(-36.74, 106.07) * mm, "mid": v(-32.22, 105.91) * mm, "end": v(-28.09, 107.78) * mm});
            skArc(sketch, "E15.0.5.151", {"start": v(49.25, 112.25) * mm, "mid": v(56.98, 113.44) * mm, "end": v(61.88, 119.54) * mm});
            skArc(sketch, "E15.0.5.152", {"start": v(-37.64, 106.28) * mm, "mid": v(-39.98, 110.07) * mm, "end": v(-43.82, 112.3) * mm});
            skArc(sketch, "E15.0.5.153", {"start": v(-24.5, 113.14) * mm, "mid": v(-27.42, 106.07) * mm, "end": v(-24.5, 99) * mm});
            skPoint(sketch, "E15.0.5.154", {"position": v(12.25, 106.07) * mm});
            skArc(sketch, "E15.0.5.155", {"start": v(48.99, 113.14) * mm, "mid": v(46.06, 106.07) * mm, "end": v(48.99, 99) * mm});
            skPoint(sketch, "E15.0.5.156", {"position": v(61.24, 106.07) * mm});
            skArc(sketch, "E15.0.5.157", {"start": v(-48.99, 113.14) * mm, "mid": v(-51.92, 106.07) * mm, "end": v(-48.99, 99) * mm});
            skPoint(sketch, "E15.0.5.158", {"position": v(-12.25, 106.07) * mm});
            skArc(sketch, "E15.0.5.159", {"start": v(0, 113.14) * mm, "mid": v(-2.93, 106.07) * mm, "end": v(0, 99) * mm});
            skArc(sketch, "E15.0.5.160", {"start": v(24.5, 113.14) * mm, "mid": v(21.57, 106.07) * mm, "end": v(24.5, 99) * mm});
            skPoint(sketch, "E15.0.5.161", {"position": v(-61.24, 106.07) * mm});
            skPoint(sketch, "E15.0.5.162", {"position": v(-36.74, 106.07) * mm});
            skPoint(sketch, "E15.0.5.163", {"position": v(36.74, 106.07) * mm});
            skPoint(sketch, "E15.0.5.164", {"position": v(61.24, 106.07) * mm});
            skPoint(sketch, "E15.0.5.165", {"position": v(36.74, 106.07) * mm});
            skPoint(sketch, "E15.0.5.166", {"position": v(-36.74, 106.07) * mm});
            skPoint(sketch, "E15.0.5.167", {"position": v(12.25, 106.07) * mm});
            skPoint(sketch, "E15.0.5.168", {"position": v(-61.24, 106.07) * mm});
            skPoint(sketch, "E15.0.5.169", {"position": v(-12.25, 106.07) * mm});
            skPoint(sketch, "E15.0.5.170", {"position": v(61.24, 106.07) * mm});
            skPoint(sketch, "E15.0.5.171", {"position": v(-36.74, 106.07) * mm});
            skPoint(sketch, "E15.0.5.172", {"position": v(-61.24, 106.07) * mm});
            skPoint(sketch, "E15.0.5.173", {"position": v(36.74, 106.07) * mm});
            skPoint(sketch, "E15.0.5.174", {"position": v(-12.25, 106.07) * mm});
            skPoint(sketch, "E15.0.5.175", {"position": v(12.21, 106) * mm});
            skPoint(sketch, "E15.0.5.176", {"position": v(-12.28, 106) * mm});
            skPoint(sketch, "E15.0.5.177", {"position": v(61.2, 106) * mm});
            skPoint(sketch, "E15.0.5.178", {"position": v(12.25, 106.07) * mm});
            skPoint(sketch, "E15.0.5.179", {"position": v(36.7, 106) * mm});
            skPoint(sketch, "E15.0.5.180", {"position": v(-36.78, 106) * mm});
            skLineSegment(sketch, "E15.direction1", {"start": v(-9.66, -16.73) * mm, "end": v(15.34, -16.73) * mm, "construction": true});
            skLineSegment(sketch, "E15.direction2", {"start": v(-9.66, -16.73) * mm, "end": v(-21.9, 4.48) * mm, "construction": true});
            skPoint(sketch, "E16.1.0.0", {"position": v(-61.24, 49.5) * mm});
            skArc(sketch, "E16.1.0.1", {"start": v(-85.1, 64.3) * mm, "mid": v(-80.65, 64.44) * mm, "end": v(-76.79, 66.65) * mm});
            skArc(sketch, "E16.1.0.2", {"start": v(-97.98, 84.85) * mm, "mid": v(-93.45, 84.7) * mm, "end": v(-89.32, 86.56) * mm});
            skArc(sketch, "E16.1.0.3", {"start": v(-97.72, 41.54) * mm, "mid": v(-93.43, 41.47) * mm, "end": v(-89.44, 43.07) * mm});
            skArc(sketch, "E16.1.0.4", {"start": v(-49.89, 70.93) * mm, "mid": v(-54.05, 76.09) * mm, "end": v(-60.6, 77.11) * mm});
            skArc(sketch, "E16.1.0.5", {"start": v(-109.59, 50.17) * mm, "mid": v(-103.04, 51.19) * mm, "end": v(-98.88, 56.35) * mm});
            skArc(sketch, "E16.1.0.6", {"start": v(-60.6, 64.3) * mm, "mid": v(-62.68, 68.06) * mm, "end": v(-66.07, 70.71) * mm});
            skArc(sketch, "E16.1.0.7", {"start": v(-85.1, 50.17) * mm, "mid": v(-90, 56.26) * mm, "end": v(-97.72, 57.46) * mm});
            skArc(sketch, "E16.1.0.8", {"start": v(-24.5, -14.14) * mm, "mid": v(-16.9, -13.14) * mm, "end": v(-12.25, -7.07) * mm});
            skArc(sketch, "E16.1.0.9", {"start": v(-195.32, 71.38) * mm, "mid": v(-188.77, 72.4) * mm, "end": v(-184.6, 77.56) * mm});
            skArc(sketch, "E16.1.0.10", {"start": v(-121.84, 71.38) * mm, "mid": v(-126.73, 77.48) * mm, "end": v(-134.46, 78.67) * mm});
            skArc(sketch, "E16.1.0.11", {"start": v(-85.1, 106.73) * mm, "mid": v(-87.18, 110.5) * mm, "end": v(-90.56, 113.14) * mm});
            skArc(sketch, "E16.1.0.12", {"start": v(-122.47, -14.14) * mm, "mid": v(-127.13, -8.07) * mm, "end": v(-134.72, -7.07) * mm});
            skArc(sketch, "E16.1.0.13", {"start": v(-98.88, 42.64) * mm, "mid": v(-101.22, 46.43) * mm, "end": v(-105.06, 48.67) * mm});
            skArc(sketch, "E16.1.0.14", {"start": v(-97.72, 41.54) * mm, "mid": v(-99.83, 37.62) * mm, "end": v(-99.85, 33.17) * mm});
            skArc(sketch, "E16.1.0.15", {"start": v(-146.7, 27.4) * mm, "mid": v(-138.98, 28.6) * mm, "end": v(-134.08, 34.69) * mm});
            skArc(sketch, "E16.1.0.16", {"start": v(-146.97, 28.28) * mm, "mid": v(-151.63, 34.36) * mm, "end": v(-159.22, 35.36) * mm});
            skArc(sketch, "E16.1.0.17", {"start": v(-134.46, 91.04) * mm, "mid": v(-126.73, 92.23) * mm, "end": v(-121.84, 98.33) * mm});
            skPoint(sketch, "E16.1.0.18", {"position": v(-85.73, 106.07) * mm});
            skPoint(sketch, "E16.1.0.19", {"position": v(-85.73, 7.07) * mm});
            skArc(sketch, "E16.1.0.20", {"start": v(-183.07, 50.17) * mm, "mid": v(-176.52, 51.19) * mm, "end": v(-172.36, 56.35) * mm});
            skArc(sketch, "E16.1.0.21", {"start": v(-60.98, 20.33) * mm, "mid": v(-63.08, 16.4) * mm, "end": v(-63.1, 11.96) * mm});
            skPoint(sketch, "E16.1.0.22", {"position": v(-122.47, 113.14) * mm});
            skArc(sketch, "E16.1.0.23", {"start": v(-183.07, 64.3) * mm, "mid": v(-178.63, 64.44) * mm, "end": v(-174.77, 66.65) * mm});
            skArc(sketch, "E16.1.0.24", {"start": v(-158.96, 48.61) * mm, "mid": v(-151.23, 49.8) * mm, "end": v(-146.33, 55.9) * mm});
            skArc(sketch, "E16.1.0.25", {"start": v(-97.34, -13.47) * mm, "mid": v(-90.8, -12.45) * mm, "end": v(-86.63, -7.29) * mm});
            skArc(sketch, "E16.1.0.26", {"start": v(-208.2, 106.07) * mm, "mid": v(-210.6, 102.22) * mm, "end": v(-211.05, 97.72) * mm});
            skArc(sketch, "E16.1.0.27", {"start": v(-109.59, 7.74) * mm, "mid": v(-103.04, 8.76) * mm, "end": v(-98.88, 13.92) * mm});
            skArc(sketch, "E16.1.0.28", {"start": v(-172.36, 70.93) * mm, "mid": v(-176.52, 76.09) * mm, "end": v(-183.07, 77.11) * mm});
            skArc(sketch, "E16.1.0.29", {"start": v(-208.2, 91.92) * mm, "mid": v(-211.14, 84.85) * mm, "end": v(-208.2, 77.78) * mm});
            skArc(sketch, "E16.1.0.30", {"start": v(-85.1, 21.88) * mm, "mid": v(-80.65, 22.02) * mm, "end": v(-76.79, 24.22) * mm});
            skArc(sketch, "E16.1.0.31", {"start": v(-171.46, 113.14) * mm, "mid": v(-176.12, 119.2) * mm, "end": v(-183.71, 120.2) * mm});
            skArc(sketch, "E16.1.0.32", {"start": v(-61.24, 49.5) * mm, "mid": v(-53.65, 50.5) * mm, "end": v(-48.99, 56.57) * mm});
            skArc(sketch, "E16.1.0.33", {"start": v(-36.1, 7.74) * mm, "mid": v(-41, 13.84) * mm, "end": v(-48.73, 15.03) * mm});
            skArc(sketch, "E16.1.0.34", {"start": v(-49.89, 28.5) * mm, "mid": v(-54.05, 33.66) * mm, "end": v(-60.6, 34.69) * mm});
            skArc(sketch, "E16.1.0.35", {"start": v(-146.7, 112.25) * mm, "mid": v(-138.98, 113.44) * mm, "end": v(-134.08, 119.54) * mm});
            skArc(sketch, "E16.1.0.36", {"start": v(-207.95, 91.04) * mm, "mid": v(-210.34, 84.85) * mm, "end": v(-207.95, 78.67) * mm});
            skArc(sketch, "E16.1.0.38", {"start": v(-134.08, 21.88) * mm, "mid": v(-129.64, 22.02) * mm, "end": v(-125.78, 24.22) * mm});
            skArc(sketch, "E16.1.0.39", {"start": v(-73.48, 0) * mm, "mid": v(-75.62, 4) * mm, "end": v(-79.3, 6.64) * mm});
            skPoint(sketch, "E16.1.0.40", {"position": v(-85.73, 91.92) * mm});
            skArc(sketch, "E16.1.0.41", {"start": v(-122.21, 112.25) * mm, "mid": v(-114.49, 113.44) * mm, "end": v(-109.59, 119.54) * mm});
            skArc(sketch, "E16.1.0.42", {"start": v(-36.1, 21.88) * mm, "mid": v(-38.19, 25.64) * mm, "end": v(-41.57, 28.28) * mm});
            skArc(sketch, "E16.1.0.43", {"start": v(-170.83, 71.38) * mm, "mid": v(-175.72, 77.48) * mm, "end": v(-183.45, 78.67) * mm});
            skArc(sketch, "E16.1.0.44", {"start": v(-110.23, 63.64) * mm, "mid": v(-112.36, 67.63) * mm, "end": v(-116.03, 70.28) * mm});
            skArc(sketch, "E16.1.0.45", {"start": v(-160.11, 49.72) * mm, "mid": v(-164.28, 54.88) * mm, "end": v(-170.83, 55.9) * mm});
            skPoint(sketch, "E16.1.0.46", {"position": v(-85.73, 49.5) * mm});
            skPoint(sketch, "E16.1.0.47", {"position": v(-97.98, 42.43) * mm});
            skArc(sketch, "E16.1.0.48", {"start": v(-122.21, -0.89) * mm, "mid": v(-117.92, -0.96) * mm, "end": v(-113.94, 0.65) * mm});
            skArc(sketch, "E16.1.0.49", {"start": v(-24.24, -0.89) * mm, "mid": v(-19.94, -0.96) * mm, "end": v(-15.96, 0.65) * mm});
            skArc(sketch, "E16.1.0.50", {"start": v(-36.48, 20.33) * mm, "mid": v(-32.19, 20.25) * mm, "end": v(-28.2, 21.86) * mm});
            skPoint(sketch, "E16.1.0.51", {"position": v(-85.73, 21.21) * mm});
            skPoint(sketch, "E16.1.0.52", {"position": v(-208.2, 91.92) * mm});
            skArc(sketch, "E16.1.0.53", {"start": v(-98.88, 0.22) * mm, "mid": v(-101.09, -3.46) * mm, "end": v(-101.69, -7.72) * mm});
            skPoint(sketch, "E16.1.0.54", {"position": v(-171.46, 84.85) * mm});
            skArc(sketch, "E16.1.0.55", {"start": v(-159.22, 63.64) * mm, "mid": v(-154.7, 63.49) * mm, "end": v(-150.56, 65.35) * mm});
            skPoint(sketch, "E16.1.0.56", {"position": v(-159.22, 21.21) * mm});
            skArc(sketch, "E16.1.0.57", {"start": v(-72.85, -13.47) * mm, "mid": v(-66.3, -12.45) * mm, "end": v(-62.14, -7.29) * mm});
            skLineSegment(sketch, "E16.1.0.58", {"start": v(-156.63, -16.73) * mm, "end": v(-168.88, 4.48) * mm, "construction": true});
            skLineSegment(sketch, "E16.1.0.59", {"start": v(-73.48, 84.85) * mm, "end": v(-63.83, 87.44) * mm, "construction": true});
            skArc(sketch, "E16.1.0.60", {"start": v(-134.46, 20.33) * mm, "mid": v(-130.17, 20.25) * mm, "end": v(-126.18, 21.86) * mm});
            skLineSegment(sketch, "E16.1.0.61", {"start": v(-61.24, 21.21) * mm, "end": v(-51.58, 23.8) * mm, "construction": true});
            skArc(sketch, "E16.1.0.62", {"start": v(-73.48, 70.71) * mm, "mid": v(-65.9, 71.7) * mm, "end": v(-61.24, 77.78) * mm});
            skLineSegment(sketch, "E16.1.0.63", {"start": v(-134.72, 21.21) * mm, "end": v(-125.06, 23.8) * mm, "construction": true});
            skArc(sketch, "E16.1.0.64", {"start": v(-172.36, 42.64) * mm, "mid": v(-174.57, 38.96) * mm, "end": v(-175.17, 34.7) * mm});
            skPoint(sketch, "E16.1.0.65", {"position": v(-183.71, 106.07) * mm});
            skPoint(sketch, "E16.1.0.66", {"position": v(-195.96, 113.14) * mm});
            skLineSegment(sketch, "E16.1.0.67", {"start": v(-85.73, 21.21) * mm, "end": v(-76.07, 23.8) * mm, "construction": true});
            skArc(sketch, "E16.1.0.68", {"start": v(-183.45, 62.75) * mm, "mid": v(-179.16, 62.68) * mm, "end": v(-175.17, 64.29) * mm});
            skArc(sketch, "E16.1.0.69", {"start": v(-85.47, 62.75) * mm, "mid": v(-81.18, 62.68) * mm, "end": v(-77.2, 64.29) * mm});
            skArc(sketch, "E16.1.0.71", {"start": v(-135.62, 21.43) * mm, "mid": v(-137.83, 17.75) * mm, "end": v(-138.43, 13.5) * mm});
            skArc(sketch, "E16.1.0.72", {"start": v(-158.58, 106.73) * mm, "mid": v(-154.13, 106.87) * mm, "end": v(-150.27, 109.08) * mm});
            skArc(sketch, "E16.1.0.73", {"start": v(-97.34, 28.95) * mm, "mid": v(-90.8, 29.98) * mm, "end": v(-86.63, 35.14) * mm});
            skArc(sketch, "E16.1.0.74", {"start": v(-123.37, 42.64) * mm, "mid": v(-125.71, 46.43) * mm, "end": v(-129.55, 48.67) * mm});
            skArc(sketch, "E16.1.0.75", {"start": v(-86.63, 92.14) * mm, "mid": v(-90.8, 97.3) * mm, "end": v(-97.34, 98.33) * mm});
            skArc(sketch, "E16.1.0.76", {"start": v(-48.73, -0.89) * mm, "mid": v(-50.84, -4.8) * mm, "end": v(-50.86, -9.25) * mm});
            skArc(sketch, "E16.1.0.77", {"start": v(-97.98, 113.14) * mm, "mid": v(-102.64, 119.2) * mm, "end": v(-110.23, 120.2) * mm});
            skArc(sketch, "E16.1.0.78", {"start": v(-72.85, 28.95) * mm, "mid": v(-77.74, 35.05) * mm, "end": v(-85.47, 36.24) * mm});
            skArc(sketch, "E16.1.0.79", {"start": v(-48.99, 28.28) * mm, "mid": v(-53.65, 34.36) * mm, "end": v(-61.24, 35.36) * mm});
            skPoint(sketch, "E16.1.0.80", {"position": v(-146.97, 0) * mm});
            skArc(sketch, "E16.1.0.81", {"start": v(-196.86, 85.07) * mm, "mid": v(-199.07, 81.39) * mm, "end": v(-199.67, 77.14) * mm});
            skPoint(sketch, "E16.1.0.82", {"position": v(-159.22, 49.5) * mm});
            skArc(sketch, "E16.1.0.83", {"start": v(-61.24, 63.64) * mm, "mid": v(-63.37, 67.63) * mm, "end": v(-67.05, 70.28) * mm});
            skArc(sketch, "E16.1.0.84", {"start": v(-36.1, 21.88) * mm, "mid": v(-31.66, 22.02) * mm, "end": v(-27.8, 24.22) * mm});
            skArc(sketch, "E16.1.0.85", {"start": v(-134.08, 50.17) * mm, "mid": v(-127.53, 51.19) * mm, "end": v(-123.37, 56.35) * mm});
            skArc(sketch, "E16.1.0.86", {"start": v(-48.99, 28.28) * mm, "mid": v(-41.4, 29.28) * mm, "end": v(-36.74, 35.36) * mm});
            skArc(sketch, "E16.1.0.87", {"start": v(-97.34, 43.1) * mm, "mid": v(-99.43, 46.85) * mm, "end": v(-102.8, 49.5) * mm});
            skArc(sketch, "E16.1.0.88", {"start": v(-60.6, 7.74) * mm, "mid": v(-65.5, 13.84) * mm, "end": v(-73.22, 15.03) * mm});
            skArc(sketch, "E16.1.0.89", {"start": v(-97.98, 0) * mm, "mid": v(-100.11, 4) * mm, "end": v(-103.79, 6.64) * mm});
            skArc(sketch, "E16.1.0.90", {"start": v(-110.23, 49.5) * mm, "mid": v(-114.89, 55.57) * mm, "end": v(-122.47, 56.57) * mm});
            skArc(sketch, "E16.1.0.91", {"start": v(-85.47, 6.18) * mm, "mid": v(-77.74, 7.38) * mm, "end": v(-72.85, 13.47) * mm});
            skArc(sketch, "E16.1.0.92", {"start": v(-48.35, 43.1) * mm, "mid": v(-43.9, 43.23) * mm, "end": v(-40.04, 45.44) * mm});
            skArc(sketch, "E16.1.0.93", {"start": v(-73.48, 113.14) * mm, "mid": v(-78.14, 119.2) * mm, "end": v(-85.73, 120.2) * mm});
            skPoint(sketch, "E16.1.0.94", {"position": v(-97.98, -14.14) * mm});
            skArc(sketch, "E16.1.0.95", {"start": v(-37.64, 49.72) * mm, "mid": v(-40.47, 42.43) * mm, "end": v(-37.64, 35.14) * mm});
            skPoint(sketch, "E16.1.0.96", {"position": v(-48.99, 28.28) * mm});
            skArc(sketch, "E16.1.0.97", {"start": v(-111.12, 63.86) * mm, "mid": v(-113.47, 67.64) * mm, "end": v(-117.3, 69.88) * mm});
            skArc(sketch, "E16.1.0.98", {"start": v(-195.96, 84.85) * mm, "mid": v(-198.35, 81) * mm, "end": v(-198.8, 76.5) * mm});
            skArc(sketch, "E16.1.0.99", {"start": v(-85.47, 105.18) * mm, "mid": v(-81.18, 105.1) * mm, "end": v(-77.2, 106.71) * mm});
            skArc(sketch, "E16.1.0.100", {"start": v(-146.97, 0) * mm, "mid": v(-149.36, -3.84) * mm, "end": v(-149.82, -8.35) * mm});
            skArc(sketch, "E16.1.0.101", {"start": v(-74.38, 85.07) * mm, "mid": v(-76.6, 81.39) * mm, "end": v(-77.2, 77.14) * mm});
            skArc(sketch, "E16.1.0.102", {"start": v(-85.1, 21.88) * mm, "mid": v(-87.18, 25.64) * mm, "end": v(-90.56, 28.28) * mm});
            skPoint(sketch, "E16.1.0.103", {"position": v(-73.48, 42.43) * mm});
            skPoint(sketch, "E16.1.0.104", {"position": v(-134.72, 91.92) * mm});
            skArc(sketch, "E16.1.0.105", {"start": v(-122.47, 28.28) * mm, "mid": v(-114.89, 29.28) * mm, "end": v(-110.23, 35.36) * mm});
            skArc(sketch, "E16.1.0.106", {"start": v(-171.2, 69.82) * mm, "mid": v(-163.48, 71.02) * mm, "end": v(-158.58, 77.11) * mm});
            skArc(sketch, "E16.1.0.107", {"start": v(-109.59, 106.73) * mm, "mid": v(-105.14, 106.87) * mm, "end": v(-101.28, 109.08) * mm});
            skArc(sketch, "E16.1.0.108", {"start": v(-109.59, 64.3) * mm, "mid": v(-105.14, 64.44) * mm, "end": v(-101.28, 66.65) * mm});
            skArc(sketch, "E16.1.0.109", {"start": v(-146.33, 28.95) * mm, "mid": v(-139.78, 29.98) * mm, "end": v(-135.62, 35.14) * mm});
            skArc(sketch, "E16.1.0.110", {"start": v(-97.34, 71.38) * mm, "mid": v(-90.8, 72.4) * mm, "end": v(-86.63, 77.56) * mm});
            skPoint(sketch, "E16.1.0.111", {"position": v(-36.74, 21.21) * mm});
            skArc(sketch, "E16.1.0.112", {"start": v(-134.08, 106.73) * mm, "mid": v(-136.17, 110.5) * mm, "end": v(-139.55, 113.14) * mm});
            skPoint(sketch, "E16.1.0.113", {"position": v(-134.72, 63.64) * mm});
            skArc(sketch, "E16.1.0.114", {"start": v(-195.7, 83.97) * mm, "mid": v(-191.4, 83.9) * mm, "end": v(-187.42, 85.5) * mm});
            skArc(sketch, "E16.1.0.115", {"start": v(-48.99, -14.14) * mm, "mid": v(-41.4, -13.14) * mm, "end": v(-36.74, -7.07) * mm});
            skArc(sketch, "E16.1.0.116", {"start": v(-171.2, 41.54) * mm, "mid": v(-173.3, 37.62) * mm, "end": v(-173.33, 33.17) * mm});
            skArc(sketch, "E16.1.0.117", {"start": v(-25.4, 28.5) * mm, "mid": v(-28.22, 21.21) * mm, "end": v(-25.4, 13.92) * mm});
            skArc(sketch, "E16.1.0.118", {"start": v(-170.83, 85.52) * mm, "mid": v(-166.38, 85.66) * mm, "end": v(-162.52, 87.86) * mm});
            skArc(sketch, "E16.1.0.119", {"start": v(-48.99, -14.14) * mm, "mid": v(-53.65, -8.07) * mm, "end": v(-61.24, -7.07) * mm});
            skArc(sketch, "E16.1.0.120", {"start": v(-183.45, 48.61) * mm, "mid": v(-175.72, 49.8) * mm, "end": v(-170.83, 55.9) * mm});
            skArc(sketch, "E16.1.0.121", {"start": v(-24.5, 0) * mm, "mid": v(-26.63, 4) * mm, "end": v(-30.3, 6.64) * mm});
            skArc(sketch, "E16.1.0.122", {"start": v(-146.7, 69.82) * mm, "mid": v(-138.98, 71.02) * mm, "end": v(-134.08, 77.11) * mm});
            skArc(sketch, "E16.1.0.124", {"start": v(-97.72, -0.89) * mm, "mid": v(-93.43, -0.96) * mm, "end": v(-89.44, 0.65) * mm});
            skArc(sketch, "E16.1.0.125", {"start": v(-24.5, -14.14) * mm, "mid": v(-29.15, -8.07) * mm, "end": v(-36.74, -7.07) * mm});
            skArc(sketch, "E16.1.0.126", {"start": v(-97.98, 28.28) * mm, "mid": v(-90.4, 29.28) * mm, "end": v(-85.73, 35.36) * mm});
            skArc(sketch, "E16.1.0.127", {"start": v(-135.62, 106.28) * mm, "mid": v(-137.83, 102.6) * mm, "end": v(-138.43, 98.35) * mm});
            skPoint(sketch, "E16.1.0.128", {"position": v(-110.23, 21.21) * mm});
            skArc(sketch, "E16.1.0.129", {"start": v(-122.47, 84.85) * mm, "mid": v(-124.87, 81) * mm, "end": v(-125.32, 76.5) * mm});
            skArc(sketch, "E16.1.0.130", {"start": v(-24.5, 0) * mm, "mid": v(-19.97, -0.15) * mm, "end": v(-15.84, 1.7) * mm});
            skArc(sketch, "E16.1.0.131", {"start": v(-98.88, 113.36) * mm, "mid": v(-103.04, 118.52) * mm, "end": v(-109.59, 119.54) * mm});
            skArc(sketch, "E16.1.0.132", {"start": v(-183.71, 91.92) * mm, "mid": v(-188.37, 98) * mm, "end": v(-195.96, 99) * mm});
            skArc(sketch, "E16.1.0.133", {"start": v(-220.45, 113.14) * mm, "mid": v(-223.38, 106.07) * mm, "end": v(-220.45, 99) * mm});
            skArc(sketch, "E16.1.0.134", {"start": v(-195.96, 70.71) * mm, "mid": v(-198.89, 63.64) * mm, "end": v(-195.96, 56.57) * mm});
            skArc(sketch, "E16.1.0.135", {"start": v(-146.7, 83.97) * mm, "mid": v(-142.42, 83.9) * mm, "end": v(-138.43, 85.5) * mm});
            skArc(sketch, "E16.1.0.136", {"start": v(-97.72, 83.97) * mm, "mid": v(-99.83, 80.05) * mm, "end": v(-99.85, 75.6) * mm});
            skLineSegment(sketch, "E16.1.0.137", {"start": v(-48.99, 0) * mm, "end": v(-39.33, 2.59) * mm, "construction": true});
            skArc(sketch, "E16.1.0.138", {"start": v(-183.71, 106.07) * mm, "mid": v(-186.1, 102.22) * mm, "end": v(-186.56, 97.72) * mm});
            skArc(sketch, "E16.1.0.139", {"start": v(-61.24, 49.5) * mm, "mid": v(-65.9, 55.57) * mm, "end": v(-73.48, 56.57) * mm});
            skArc(sketch, "E16.1.0.140", {"start": v(-111.12, 49.72) * mm, "mid": v(-115.29, 54.88) * mm, "end": v(-121.84, 55.9) * mm});
            skArc(sketch, "E16.1.0.141", {"start": v(-72.85, 28.95) * mm, "mid": v(-66.3, 29.98) * mm, "end": v(-62.14, 35.14) * mm});
            skArc(sketch, "E16.1.0.142", {"start": v(-23.86, 0.67) * mm, "mid": v(-25.94, 4.42) * mm, "end": v(-29.32, 7.07) * mm});
            skArc(sketch, "E16.1.0.143", {"start": v(-97.34, -13.47) * mm, "mid": v(-102.24, -7.38) * mm, "end": v(-109.97, -6.18) * mm});
            skArc(sketch, "E16.1.0.144", {"start": v(-72.85, 85.52) * mm, "mid": v(-74.93, 89.28) * mm, "end": v(-78.31, 91.92) * mm});
            skArc(sketch, "E16.1.0.145", {"start": v(-170.83, 28.95) * mm, "mid": v(-164.28, 29.98) * mm, "end": v(-160.11, 35.14) * mm});
            skArc(sketch, "E16.1.0.146", {"start": v(-146.97, 113.14) * mm, "mid": v(-151.63, 119.2) * mm, "end": v(-159.22, 120.2) * mm});
            skArc(sketch, "E16.1.0.147", {"start": v(-146.97, -14.14) * mm, "mid": v(-151.63, -8.07) * mm, "end": v(-159.22, -7.07) * mm});
            skArc(sketch, "E16.1.0.148", {"start": v(-72.85, 43.1) * mm, "mid": v(-74.93, 46.85) * mm, "end": v(-78.31, 49.5) * mm});
            skArc(sketch, "E16.1.0.149", {"start": v(-36.48, 6.18) * mm, "mid": v(-28.75, 7.38) * mm, "end": v(-23.86, 13.47) * mm});
            skArc(sketch, "E16.1.0.150", {"start": v(-208.2, 91.92) * mm, "mid": v(-200.62, 92.92) * mm, "end": v(-195.96, 99) * mm});
            skPoint(sketch, "E16.1.0.151", {"position": v(-48.99, -14.14) * mm});
            skArc(sketch, "E16.1.0.152", {"start": v(-146.7, -0.89) * mm, "mid": v(-148.81, -4.8) * mm, "end": v(-148.84, -9.25) * mm});
            skArc(sketch, "E16.1.0.153", {"start": v(-134.46, 48.61) * mm, "mid": v(-126.73, 49.8) * mm, "end": v(-121.84, 55.9) * mm});
            skPoint(sketch, "E16.1.0.154", {"position": v(-73.48, 28.28) * mm});
            skArc(sketch, "E16.1.0.155", {"start": v(-110.23, 91.92) * mm, "mid": v(-102.64, 92.92) * mm, "end": v(-97.98, 99) * mm});
            skArc(sketch, "E16.1.0.156", {"start": v(-158.58, 50.17) * mm, "mid": v(-152.03, 51.19) * mm, "end": v(-147.87, 56.35) * mm});
            skArc(sketch, "E16.1.0.157", {"start": v(-109.97, 105.18) * mm, "mid": v(-105.67, 105.1) * mm, "end": v(-101.69, 106.71) * mm});
            skArc(sketch, "E16.1.0.158", {"start": v(-60.6, 50.17) * mm, "mid": v(-54.05, 51.19) * mm, "end": v(-49.89, 56.35) * mm});
            skArc(sketch, "E16.1.0.159", {"start": v(-73.48, 0) * mm, "mid": v(-75.88, -3.84) * mm, "end": v(-76.33, -8.35) * mm});
            skArc(sketch, "E16.1.0.160", {"start": v(-49.89, 70.93) * mm, "mid": v(-52.72, 63.64) * mm, "end": v(-49.89, 56.35) * mm});
            skArc(sketch, "E16.1.0.161", {"start": v(-85.73, 21.21) * mm, "mid": v(-81.2, 21.06) * mm, "end": v(-77.08, 22.92) * mm});
            skPoint(sketch, "E16.1.0.162", {"position": v(-73.48, -14.14) * mm});
            skArc(sketch, "E16.1.0.163", {"start": v(-97.98, 42.43) * mm, "mid": v(-93.45, 42.28) * mm, "end": v(-89.32, 44.14) * mm});
            skPoint(sketch, "E16.1.0.164", {"position": v(-61.24, 7.07) * mm});
            skArc(sketch, "E16.1.0.165", {"start": v(-147.87, 0.22) * mm, "mid": v(-150.08, -3.46) * mm, "end": v(-150.68, -7.72) * mm});
            skArc(sketch, "E16.1.0.166", {"start": v(-134.08, 92.6) * mm, "mid": v(-127.53, 93.62) * mm, "end": v(-123.37, 98.78) * mm});
            skArc(sketch, "E16.1.0.167", {"start": v(-158.96, 91.04) * mm, "mid": v(-151.23, 92.23) * mm, "end": v(-146.33, 98.33) * mm});
            skArc(sketch, "E16.1.0.168", {"start": v(-158.58, 64.3) * mm, "mid": v(-160.66, 68.06) * mm, "end": v(-164.05, 70.71) * mm});
            skPoint(sketch, "E16.1.0.169", {"position": v(-220.45, 113.14) * mm});
            skArc(sketch, "E16.1.0.170", {"start": v(-184.6, 92.14) * mm, "mid": v(-188.77, 97.3) * mm, "end": v(-195.32, 98.33) * mm});
            skArc(sketch, "E16.1.0.171", {"start": v(-74.38, 28.5) * mm, "mid": v(-78.54, 33.66) * mm, "end": v(-85.1, 34.69) * mm});
            skArc(sketch, "E16.1.0.172", {"start": v(-146.33, -13.47) * mm, "mid": v(-139.78, -12.45) * mm, "end": v(-135.62, -7.29) * mm});
            skArc(sketch, "E16.1.0.173", {"start": v(-110.23, 91.92) * mm, "mid": v(-114.89, 98) * mm, "end": v(-122.47, 99) * mm});
            skArc(sketch, "E16.1.0.174", {"start": v(-195.96, 84.85) * mm, "mid": v(-191.43, 84.7) * mm, "end": v(-187.3, 86.56) * mm});
            skArc(sketch, "E16.1.0.175", {"start": v(-60.6, 7.74) * mm, "mid": v(-54.05, 8.76) * mm, "end": v(-49.89, 13.92) * mm});
            skArc(sketch, "E16.1.0.176", {"start": v(-123.37, 28.5) * mm, "mid": v(-127.53, 33.66) * mm, "end": v(-134.08, 34.69) * mm});
            skPoint(sketch, "E16.1.0.177", {"position": v(-61.24, 63.64) * mm});
            skArc(sketch, "E16.1.0.178", {"start": v(-97.98, 0) * mm, "mid": v(-93.45, -0.15) * mm, "end": v(-89.32, 1.7) * mm});
            skArc(sketch, "E16.1.0.179", {"start": v(-23.86, -13.47) * mm, "mid": v(-28.75, -7.38) * mm, "end": v(-36.48, -6.18) * mm});
            skArc(sketch, "E16.1.0.180", {"start": v(-109.97, 48.61) * mm, "mid": v(-102.24, 49.8) * mm, "end": v(-97.34, 55.9) * mm});
            skArc(sketch, "E16.1.0.181", {"start": v(-209.1, 106.28) * mm, "mid": v(-211.32, 102.6) * mm, "end": v(-211.92, 98.35) * mm});
            skArc(sketch, "E16.1.0.183", {"start": v(-134.08, 64.3) * mm, "mid": v(-136.17, 68.06) * mm, "end": v(-139.55, 70.71) * mm});
            skPoint(sketch, "E16.1.0.184", {"position": v(-48.99, 42.43) * mm});
            skArc(sketch, "E16.1.0.185", {"start": v(-109.59, 92.6) * mm, "mid": v(-114.49, 98.69) * mm, "end": v(-122.21, 99.88) * mm});
            skArc(sketch, "E16.1.0.186", {"start": v(-195.32, 85.52) * mm, "mid": v(-190.88, 85.66) * mm, "end": v(-187.01, 87.86) * mm});
            skArc(sketch, "E16.1.0.187", {"start": v(-86.63, 7.29) * mm, "mid": v(-90.8, 12.45) * mm, "end": v(-97.34, 13.47) * mm});
            skArc(sketch, "E16.1.0.188", {"start": v(-170.83, 28.95) * mm, "mid": v(-175.72, 35.05) * mm, "end": v(-183.45, 36.24) * mm});
            skPoint(sketch, "E16.1.0.189", {"position": v(-73.48, 84.85) * mm});
            skArc(sketch, "E16.1.0.190", {"start": v(-85.73, 106.07) * mm, "mid": v(-81.2, 105.91) * mm, "end": v(-77.08, 107.78) * mm});
            skArc(sketch, "E16.1.0.191", {"start": v(-183.07, 64.3) * mm, "mid": v(-185.16, 68.06) * mm, "end": v(-188.54, 70.71) * mm});
            skArc(sketch, "E16.1.0.192", {"start": v(-97.34, 85.52) * mm, "mid": v(-99.43, 89.28) * mm, "end": v(-102.8, 91.92) * mm});
            skArc(sketch, "E16.1.0.193", {"start": v(-207.95, 105.18) * mm, "mid": v(-203.65, 105.1) * mm, "end": v(-199.67, 106.71) * mm});
            skArc(sketch, "E16.1.0.194", {"start": v(-109.97, 62.75) * mm, "mid": v(-105.67, 62.68) * mm, "end": v(-101.69, 64.29) * mm});
            skArc(sketch, "E16.1.0.195", {"start": v(-85.1, 106.73) * mm, "mid": v(-80.65, 106.87) * mm, "end": v(-76.79, 109.08) * mm});
            skArc(sketch, "E16.1.0.196", {"start": v(-60.98, 20.33) * mm, "mid": v(-56.68, 20.25) * mm, "end": v(-52.7, 21.86) * mm});
            skArc(sketch, "E16.1.0.197", {"start": v(-183.71, 49.5) * mm, "mid": v(-186.64, 42.43) * mm, "end": v(-183.71, 35.36) * mm});
            skArc(sketch, "E16.1.0.198", {"start": v(-122.47, 42.43) * mm, "mid": v(-117.95, 42.28) * mm, "end": v(-113.82, 44.14) * mm});
            skPoint(sketch, "E16.1.0.199", {"position": v(-73.48, 70.71) * mm});
            skArc(sketch, "E16.1.0.200", {"start": v(-134.72, 49.5) * mm, "mid": v(-139.38, 55.57) * mm, "end": v(-146.97, 56.57) * mm});
            skPoint(sketch, "E16.1.0.201", {"position": v(-159.22, 106.07) * mm});
            skArc(sketch, "E16.1.0.202", {"start": v(-134.46, 62.75) * mm, "mid": v(-130.17, 62.68) * mm, "end": v(-126.18, 64.29) * mm});
            skArc(sketch, "E16.1.0.203", {"start": v(-146.97, 113.14) * mm, "mid": v(-139.38, 114.14) * mm, "end": v(-134.72, 120.2) * mm});
            skArc(sketch, "E16.1.0.204", {"start": v(-97.34, 28.95) * mm, "mid": v(-102.24, 35.05) * mm, "end": v(-109.97, 36.24) * mm});
            skArc(sketch, "E16.1.0.205", {"start": v(-171.46, 42.43) * mm, "mid": v(-166.94, 42.28) * mm, "end": v(-162.8, 44.14) * mm});
            skPoint(sketch, "E16.1.0.206", {"position": v(-195.96, 84.85) * mm});
            skPoint(sketch, "E16.1.0.207", {"position": v(-183.71, 63.64) * mm});
            skArc(sketch, "E16.1.0.208", {"start": v(-121.84, 28.95) * mm, "mid": v(-115.29, 29.98) * mm, "end": v(-111.12, 35.14) * mm});
            skPoint(sketch, "E16.1.0.209", {"position": v(-146.97, 70.71) * mm});
            skArc(sketch, "E16.1.0.210", {"start": v(-158.96, 62.75) * mm, "mid": v(-154.66, 62.68) * mm, "end": v(-150.68, 64.29) * mm});
            skArc(sketch, "E16.1.0.211", {"start": v(-109.97, 6.18) * mm, "mid": v(-102.24, 7.38) * mm, "end": v(-97.34, 13.47) * mm});
            skArc(sketch, "E16.1.0.212", {"start": v(-97.98, -14.14) * mm, "mid": v(-102.64, -8.07) * mm, "end": v(-110.23, -7.07) * mm});
            skArc(sketch, "E16.1.0.213", {"start": v(-85.47, 20.33) * mm, "mid": v(-87.58, 16.4) * mm, "end": v(-87.6, 11.96) * mm});
            skArc(sketch, "E16.1.0.214", {"start": v(-170.83, 71.38) * mm, "mid": v(-164.28, 72.4) * mm, "end": v(-160.11, 77.56) * mm});
            skArc(sketch, "E16.1.0.215", {"start": v(-171.2, 41.54) * mm, "mid": v(-166.91, 41.47) * mm, "end": v(-162.93, 43.07) * mm});
            skArc(sketch, "E16.1.0.216", {"start": v(-183.07, 106.73) * mm, "mid": v(-185.16, 110.5) * mm, "end": v(-188.54, 113.14) * mm});
            skArc(sketch, "E16.1.0.217", {"start": v(-13.15, 7.29) * mm, "mid": v(-17.3, 12.45) * mm, "end": v(-23.86, 13.47) * mm});
            skPoint(sketch, "E16.1.0.218", {"position": v(-97.98, 70.71) * mm});
            skArc(sketch, "E16.1.0.219", {"start": v(-61.24, 7.07) * mm, "mid": v(-65.9, 13.14) * mm, "end": v(-73.48, 14.14) * mm});
            skArc(sketch, "E16.1.0.220", {"start": v(-195.32, 71.38) * mm, "mid": v(-200.22, 77.48) * mm, "end": v(-207.95, 78.67) * mm});
            skLineSegment(sketch, "E16.1.0.221", {"start": v(-195.96, 84.85) * mm, "end": v(-186.3, 87.44) * mm, "construction": true});
            skArc(sketch, "E16.1.0.222", {"start": v(-48.73, 27.4) * mm, "mid": v(-41, 28.6) * mm, "end": v(-36.1, 34.69) * mm});
            skArc(sketch, "E16.1.0.223", {"start": v(-134.72, 21.21) * mm, "mid": v(-137.12, 17.37) * mm, "end": v(-137.57, 12.86) * mm});
            skArc(sketch, "E16.1.0.224", {"start": v(-195.96, 70.71) * mm, "mid": v(-200.62, 76.78) * mm, "end": v(-208.2, 77.78) * mm});
            skArc(sketch, "E16.1.0.225", {"start": v(-160.11, 92.14) * mm, "mid": v(-164.28, 97.3) * mm, "end": v(-170.83, 98.33) * mm});
            skArc(sketch, "E16.1.0.226", {"start": v(-85.47, 105.18) * mm, "mid": v(-87.58, 101.26) * mm, "end": v(-87.6, 96.81) * mm});
            skArc(sketch, "E16.1.0.227", {"start": v(-62.14, 21.43) * mm, "mid": v(-64.35, 17.75) * mm, "end": v(-64.95, 13.5) * mm});
            skArc(sketch, "E16.1.0.228", {"start": v(-122.21, 41.54) * mm, "mid": v(-117.92, 41.47) * mm, "end": v(-113.94, 43.07) * mm});
            skArc(sketch, "E16.1.0.229", {"start": v(-97.98, 28.28) * mm, "mid": v(-102.64, 34.36) * mm, "end": v(-110.23, 35.36) * mm});
            skArc(sketch, "E16.1.0.230", {"start": v(-158.96, 20.33) * mm, "mid": v(-161.06, 16.4) * mm, "end": v(-161.08, 11.96) * mm});
            skArc(sketch, "E16.1.0.231", {"start": v(-97.72, -0.89) * mm, "mid": v(-99.83, -4.8) * mm, "end": v(-99.85, -9.25) * mm});
            skArc(sketch, "E16.1.0.232", {"start": v(-147.87, 70.93) * mm, "mid": v(-152.03, 76.09) * mm, "end": v(-158.58, 77.11) * mm});
            skPoint(sketch, "E16.1.0.233", {"position": v(-146.97, -14.14) * mm});
            skArc(sketch, "E16.1.0.234", {"start": v(-121.84, 43.1) * mm, "mid": v(-123.92, 46.85) * mm, "end": v(-127.3, 49.5) * mm});
            skArc(sketch, "E16.1.0.235", {"start": v(-207.57, 106.73) * mm, "mid": v(-203.12, 106.87) * mm, "end": v(-199.26, 109.08) * mm});
            skArc(sketch, "E16.1.0.236", {"start": v(-85.73, 49.5) * mm, "mid": v(-78.14, 50.5) * mm, "end": v(-73.48, 56.57) * mm});
            skArc(sketch, "E16.1.0.237", {"start": v(-85.73, 7.07) * mm, "mid": v(-90.4, 13.14) * mm, "end": v(-97.98, 14.14) * mm});
            skArc(sketch, "E16.1.0.238", {"start": v(-146.33, 43.1) * mm, "mid": v(-141.89, 43.23) * mm, "end": v(-138.02, 45.44) * mm});
            skArc(sketch, "E16.1.0.239", {"start": v(-146.97, 42.43) * mm, "mid": v(-142.44, 42.28) * mm, "end": v(-138.31, 44.14) * mm});
            skArc(sketch, "E16.1.0.240", {"start": v(-147.87, 28.5) * mm, "mid": v(-152.03, 33.66) * mm, "end": v(-158.58, 34.69) * mm});
            skArc(sketch, "E16.1.0.241", {"start": v(-97.72, 27.4) * mm, "mid": v(-90, 28.6) * mm, "end": v(-85.1, 34.69) * mm});
            skArc(sketch, "E16.1.0.242", {"start": v(-183.71, 63.64) * mm, "mid": v(-185.84, 67.63) * mm, "end": v(-189.52, 70.28) * mm});
            skArc(sketch, "E16.1.0.243", {"start": v(-73.48, 70.71) * mm, "mid": v(-78.14, 76.78) * mm, "end": v(-85.73, 77.78) * mm});
            skPoint(sketch, "E16.1.0.244", {"position": v(-159.22, 63.64) * mm});
            skArc(sketch, "E16.1.0.245", {"start": v(-123.37, 85.07) * mm, "mid": v(-125.58, 81.39) * mm, "end": v(-126.18, 77.14) * mm});
            skPoint(sketch, "E16.1.0.246", {"position": v(-122.47, 84.85) * mm});
            skPoint(sketch, "E16.1.0.247", {"position": v(-97.98, 28.28) * mm});
            skPoint(sketch, "E16.1.0.248", {"position": v(-110.23, 106.07) * mm});
            skArc(sketch, "E16.1.0.249", {"start": v(-74.38, 42.64) * mm, "mid": v(-76.6, 38.96) * mm, "end": v(-77.2, 34.7) * mm});
            skPoint(sketch, "E16.1.0.250", {"position": v(-183.71, 49.5) * mm});
            skLineSegment(sketch, "E16.1.0.251", {"start": v(-61.24, 63.64) * mm, "end": v(-51.58, 66.23) * mm, "construction": true});
            skArc(sketch, "E16.1.0.252", {"start": v(-171.2, 27.4) * mm, "mid": v(-173.6, 21.21) * mm, "end": v(-171.2, 15.03) * mm});
            skArc(sketch, "E16.1.0.253", {"start": v(-37.64, 49.72) * mm, "mid": v(-41.8, 54.88) * mm, "end": v(-48.35, 55.9) * mm});
            skArc(sketch, "E16.1.0.254", {"start": v(-62.14, 49.72) * mm, "mid": v(-66.3, 54.88) * mm, "end": v(-72.85, 55.9) * mm});
            skArc(sketch, "E16.1.0.255", {"start": v(-184.6, 106.28) * mm, "mid": v(-186.82, 102.6) * mm, "end": v(-187.42, 98.35) * mm});
            skArc(sketch, "E16.1.0.257", {"start": v(-171.2, 83.97) * mm, "mid": v(-173.3, 80.05) * mm, "end": v(-173.33, 75.6) * mm});
            skArc(sketch, "E16.1.0.258", {"start": v(-171.2, 112.25) * mm, "mid": v(-163.48, 113.44) * mm, "end": v(-158.58, 119.54) * mm});
            skArc(sketch, "E16.1.0.259", {"start": v(-207.57, 92.6) * mm, "mid": v(-212.47, 98.69) * mm, "end": v(-220.2, 99.88) * mm});
            skArc(sketch, "E16.1.0.260", {"start": v(-72.85, 43.1) * mm, "mid": v(-68.4, 43.23) * mm, "end": v(-64.54, 45.44) * mm});
            skArc(sketch, "E16.1.0.261", {"start": v(-147.87, 42.64) * mm, "mid": v(-150.2, 46.43) * mm, "end": v(-154.05, 48.67) * mm});
            skArc(sketch, "E16.1.0.262", {"start": v(-183.07, 92.6) * mm, "mid": v(-176.52, 93.62) * mm, "end": v(-172.36, 98.78) * mm});
            skArc(sketch, "E16.1.0.263", {"start": v(-85.1, 64.3) * mm, "mid": v(-87.18, 68.06) * mm, "end": v(-90.56, 70.71) * mm});
            skArc(sketch, "E16.1.0.264", {"start": v(-146.97, 42.43) * mm, "mid": v(-149.36, 38.58) * mm, "end": v(-149.82, 34.08) * mm});
            skArc(sketch, "E16.1.0.265", {"start": v(-159.22, 106.07) * mm, "mid": v(-161.61, 102.22) * mm, "end": v(-162.06, 97.72) * mm});
            skArc(sketch, "E16.1.0.266", {"start": v(-183.07, 92.6) * mm, "mid": v(-187.97, 98.69) * mm, "end": v(-195.7, 99.88) * mm});
            skArc(sketch, "E16.1.0.267", {"start": v(-146.33, 85.52) * mm, "mid": v(-141.89, 85.66) * mm, "end": v(-138.02, 87.86) * mm});
            skArc(sketch, "E16.1.0.268", {"start": v(-97.34, 71.38) * mm, "mid": v(-102.24, 77.48) * mm, "end": v(-109.97, 78.67) * mm});
            skArc(sketch, "E16.1.0.269", {"start": v(-61.24, 63.64) * mm, "mid": v(-56.71, 63.49) * mm, "end": v(-52.58, 65.35) * mm});
            skArc(sketch, "E16.1.0.270", {"start": v(-208.2, 91.92) * mm, "mid": v(-212.87, 98) * mm, "end": v(-220.45, 99) * mm});
            skArc(sketch, "E16.1.0.271", {"start": v(-196.86, 113.36) * mm, "mid": v(-201.02, 118.52) * mm, "end": v(-207.57, 119.54) * mm});
            skArc(sketch, "E16.1.0.272", {"start": v(-183.71, 106.07) * mm, "mid": v(-179.19, 105.91) * mm, "end": v(-175.06, 107.78) * mm});
            skArc(sketch, "E16.1.0.273", {"start": v(-122.47, -14.14) * mm, "mid": v(-114.89, -13.14) * mm, "end": v(-110.23, -7.07) * mm});
            skArc(sketch, "E16.1.0.274", {"start": v(-134.46, 105.18) * mm, "mid": v(-136.57, 101.26) * mm, "end": v(-136.59, 96.81) * mm});
            skArc(sketch, "E16.1.0.275", {"start": v(-110.23, 21.21) * mm, "mid": v(-112.62, 17.37) * mm, "end": v(-113.07, 12.86) * mm});
            skArc(sketch, "E16.1.0.276", {"start": v(-183.07, 106.73) * mm, "mid": v(-178.63, 106.87) * mm, "end": v(-174.77, 109.08) * mm});
            skArc(sketch, "E16.1.0.277", {"start": v(-85.73, 91.92) * mm, "mid": v(-90.4, 98) * mm, "end": v(-97.98, 99) * mm});
            skArc(sketch, "E16.1.0.278", {"start": v(-220.2, 112.25) * mm, "mid": v(-212.47, 113.44) * mm, "end": v(-207.57, 119.54) * mm});
            skArc(sketch, "E16.1.0.279", {"start": v(-60.6, 64.3) * mm, "mid": v(-56.15, 64.44) * mm, "end": v(-52.3, 66.65) * mm});
            skPoint(sketch, "E16.1.0.280", {"position": v(-85.73, 63.64) * mm});
            skArc(sketch, "E16.1.0.281", {"start": v(-135.62, 49.72) * mm, "mid": v(-139.78, 54.88) * mm, "end": v(-146.33, 55.9) * mm});
            skArc(sketch, "E16.1.0.282", {"start": v(-121.84, 43.1) * mm, "mid": v(-117.4, 43.23) * mm, "end": v(-113.53, 45.44) * mm});
            skPoint(sketch, "E16.1.0.283", {"position": v(-146.97, 84.85) * mm});
            skArc(sketch, "E16.1.0.284", {"start": v(-109.59, 50.17) * mm, "mid": v(-114.49, 56.26) * mm, "end": v(-122.21, 57.46) * mm});
            skArc(sketch, "E16.1.0.285", {"start": v(-172.36, 85.07) * mm, "mid": v(-174.57, 81.39) * mm, "end": v(-175.17, 77.14) * mm});
            skPoint(sketch, "E16.1.0.286", {"position": v(-24.5, -14.14) * mm});
            skArc(sketch, "E16.1.0.287", {"start": v(-48.35, -13.47) * mm, "mid": v(-41.8, -12.45) * mm, "end": v(-37.64, -7.29) * mm});
            skArc(sketch, "E16.1.0.288", {"start": v(-48.35, 0.67) * mm, "mid": v(-50.44, 4.42) * mm, "end": v(-53.82, 7.07) * mm});
            skArc(sketch, "E16.1.0.289", {"start": v(-171.46, 84.85) * mm, "mid": v(-166.94, 84.7) * mm, "end": v(-162.8, 86.56) * mm});
            skArc(sketch, "E16.1.0.290", {"start": v(-146.33, -13.47) * mm, "mid": v(-151.23, -7.38) * mm, "end": v(-158.96, -6.18) * mm});
            skArc(sketch, "E16.1.0.291", {"start": v(-36.1, 7.74) * mm, "mid": v(-29.55, 8.76) * mm, "end": v(-25.4, 13.92) * mm});
            skPoint(sketch, "E16.1.0.292", {"position": v(-195.96, 70.71) * mm});
            skPoint(sketch, "E16.1.0.293", {"position": v(-146.97, 113.14) * mm});
            skArc(sketch, "E16.1.0.294", {"start": v(-73.48, 28.28) * mm, "mid": v(-65.9, 29.28) * mm, "end": v(-61.24, 35.36) * mm});
            skArc(sketch, "E16.1.0.295", {"start": v(-171.46, 28.28) * mm, "mid": v(-163.88, 29.28) * mm, "end": v(-159.22, 35.36) * mm});
            skArc(sketch, "E16.1.0.296", {"start": v(-171.46, 84.85) * mm, "mid": v(-173.86, 81) * mm, "end": v(-174.31, 76.5) * mm});
            skArc(sketch, "E16.1.0.297", {"start": v(-208.2, 106.07) * mm, "mid": v(-203.68, 105.91) * mm, "end": v(-199.55, 107.78) * mm});
            skArc(sketch, "E16.1.0.298", {"start": v(-159.22, 49.5) * mm, "mid": v(-163.88, 55.57) * mm, "end": v(-171.46, 56.57) * mm});
            skPoint(sketch, "E16.1.0.299", {"position": v(-171.46, 70.71) * mm});
            skArc(sketch, "E16.1.0.300", {"start": v(-85.73, 49.5) * mm, "mid": v(-90.4, 55.57) * mm, "end": v(-97.98, 56.57) * mm});
            skArc(sketch, "E16.1.0.301", {"start": v(-121.84, 0.67) * mm, "mid": v(-117.4, 0.8) * mm, "end": v(-113.53, 3.01) * mm});
            skArc(sketch, "E16.1.0.302", {"start": v(-85.73, 63.64) * mm, "mid": v(-87.86, 67.63) * mm, "end": v(-91.54, 70.28) * mm});
            skArc(sketch, "E16.1.0.303", {"start": v(-122.47, 28.28) * mm, "mid": v(-127.13, 34.36) * mm, "end": v(-134.72, 35.36) * mm});
            skArc(sketch, "E16.1.0.304", {"start": v(-207.57, 92.6) * mm, "mid": v(-201.02, 93.62) * mm, "end": v(-196.86, 98.78) * mm});
            skArc(sketch, "E16.1.0.305", {"start": v(-23.86, -13.47) * mm, "mid": v(-17.3, -12.45) * mm, "end": v(-13.15, -7.29) * mm});
            skArc(sketch, "E16.1.0.306", {"start": v(-170.83, 85.52) * mm, "mid": v(-172.9, 89.28) * mm, "end": v(-176.3, 91.92) * mm});
            skArc(sketch, "E16.1.0.307", {"start": v(-61.24, 21.21) * mm, "mid": v(-63.63, 17.37) * mm, "end": v(-64.08, 12.86) * mm});
            skArc(sketch, "E16.1.0.308", {"start": v(-111.12, 106.28) * mm, "mid": v(-113.34, 102.6) * mm, "end": v(-113.94, 98.35) * mm});
            skArc(sketch, "E16.1.0.309", {"start": v(-48.35, 28.95) * mm, "mid": v(-53.25, 35.05) * mm, "end": v(-60.98, 36.24) * mm});
            skArc(sketch, "E16.1.0.310", {"start": v(-72.85, 71.38) * mm, "mid": v(-66.3, 72.4) * mm, "end": v(-62.14, 77.56) * mm});
            skLineSegment(sketch, "E16.1.0.311", {"start": v(-122.47, 84.85) * mm, "end": v(-112.82, 87.44) * mm, "construction": true});
            skArc(sketch, "E16.1.0.312", {"start": v(-159.22, 106.07) * mm, "mid": v(-154.7, 105.91) * mm, "end": v(-150.56, 107.78) * mm});
            skArc(sketch, "E16.1.0.313", {"start": v(-85.47, 91.04) * mm, "mid": v(-77.74, 92.23) * mm, "end": v(-72.85, 98.33) * mm});
            skPoint(sketch, "E16.1.0.314", {"position": v(-110.23, 49.5) * mm});
            skArc(sketch, "E16.1.0.315", {"start": v(-74.38, 113.36) * mm, "mid": v(-77.21, 106.07) * mm, "end": v(-74.38, 98.78) * mm});
            skArc(sketch, "E16.1.0.316", {"start": v(-97.98, -14.14) * mm, "mid": v(-90.4, -13.14) * mm, "end": v(-85.73, -7.07) * mm});
            skArc(sketch, "E16.1.0.317", {"start": v(-171.46, 28.28) * mm, "mid": v(-174.4, 21.21) * mm, "end": v(-171.46, 14.14) * mm});
            skLineSegment(sketch, "E16.1.0.319", {"start": v(-217.87, 89.34) * mm, "end": v(-193.37, 89.34) * mm, "construction": true});
            skArc(sketch, "E16.1.0.320", {"start": v(-97.72, 112.25) * mm, "mid": v(-90, 113.44) * mm, "end": v(-85.1, 119.54) * mm});
            skArc(sketch, "E16.1.0.321", {"start": v(-195.7, 83.97) * mm, "mid": v(-197.8, 80.05) * mm, "end": v(-197.83, 75.6) * mm});
            skArc(sketch, "E16.1.0.322", {"start": v(-73.48, -14.14) * mm, "mid": v(-65.9, -13.14) * mm, "end": v(-61.24, -7.07) * mm});
            skArc(sketch, "E16.1.0.323", {"start": v(-73.22, 69.82) * mm, "mid": v(-65.5, 71.02) * mm, "end": v(-60.6, 77.11) * mm});
            skLineSegment(sketch, "E16.1.0.324", {"start": v(-110.23, 21.21) * mm, "end": v(-100.57, 23.8) * mm, "construction": true});
            skArc(sketch, "E16.1.0.325", {"start": v(-111.12, 92.14) * mm, "mid": v(-115.29, 97.3) * mm, "end": v(-121.84, 98.33) * mm});
            skArc(sketch, "E16.1.0.326", {"start": v(-97.98, 70.71) * mm, "mid": v(-102.64, 76.78) * mm, "end": v(-110.23, 77.78) * mm});
            skArc(sketch, "E16.1.0.327", {"start": v(-158.58, 21.88) * mm, "mid": v(-160.66, 25.64) * mm, "end": v(-164.05, 28.28) * mm});
            skPoint(sketch, "E16.1.0.328", {"position": v(-134.72, 21.21) * mm});
            skArc(sketch, "E16.1.0.329", {"start": v(-97.98, 70.71) * mm, "mid": v(-90.4, 71.7) * mm, "end": v(-85.73, 77.78) * mm});
            skArc(sketch, "E16.1.0.330", {"start": v(-122.47, 113.14) * mm, "mid": v(-114.89, 114.14) * mm, "end": v(-110.23, 120.2) * mm});
            skArc(sketch, "E16.1.0.331", {"start": v(-73.48, 28.28) * mm, "mid": v(-78.14, 34.36) * mm, "end": v(-85.73, 35.36) * mm});
            skArc(sketch, "E16.1.0.332", {"start": v(-134.72, 63.64) * mm, "mid": v(-130.2, 63.49) * mm, "end": v(-126.07, 65.35) * mm});
            skArc(sketch, "E16.1.0.333", {"start": v(-207.95, 91.04) * mm, "mid": v(-200.22, 92.23) * mm, "end": v(-195.32, 98.33) * mm});
            skPoint(sketch, "E16.1.0.334", {"position": v(-97.98, 84.85) * mm});
            skArc(sketch, "E16.1.0.335", {"start": v(-158.58, 64.3) * mm, "mid": v(-154.13, 64.44) * mm, "end": v(-150.27, 66.65) * mm});
            skArc(sketch, "E16.1.0.336", {"start": v(-122.21, 41.54) * mm, "mid": v(-124.32, 37.62) * mm, "end": v(-124.34, 33.17) * mm});
            skPoint(sketch, "E16.1.0.337", {"position": v(-134.72, 7.07) * mm});
            skArc(sketch, "E16.1.0.338", {"start": v(-195.7, 69.82) * mm, "mid": v(-198.09, 63.64) * mm, "end": v(-195.7, 57.46) * mm});
            skArc(sketch, "E16.1.0.339", {"start": v(-134.08, 50.17) * mm, "mid": v(-138.98, 56.26) * mm, "end": v(-146.7, 57.46) * mm});
            skPoint(sketch, "E16.1.0.340", {"position": v(-171.46, 113.14) * mm});
            skArc(sketch, "E16.1.0.341", {"start": v(-160.11, 106.28) * mm, "mid": v(-162.33, 102.6) * mm, "end": v(-162.93, 98.35) * mm});
            skArc(sketch, "E16.1.0.342", {"start": v(-146.33, 43.1) * mm, "mid": v(-148.41, 46.85) * mm, "end": v(-151.8, 49.5) * mm});
            skArc(sketch, "E16.1.0.343", {"start": v(-134.08, 7.74) * mm, "mid": v(-127.53, 8.76) * mm, "end": v(-123.37, 13.92) * mm});
            skArc(sketch, "E16.1.0.344", {"start": v(-159.22, 91.92) * mm, "mid": v(-151.63, 92.92) * mm, "end": v(-146.97, 99) * mm});
            skLineSegment(sketch, "E16.1.0.345", {"start": v(-97.98, 84.85) * mm, "end": v(-88.32, 87.44) * mm, "construction": true});
            skArc(sketch, "E16.1.0.346", {"start": v(-109.59, 92.6) * mm, "mid": v(-103.04, 93.62) * mm, "end": v(-98.88, 98.78) * mm});
            skArc(sketch, "E16.1.0.347", {"start": v(-74.38, 0.22) * mm, "mid": v(-76.6, -3.46) * mm, "end": v(-77.2, -7.72) * mm});
            skArc(sketch, "E16.1.0.348", {"start": v(-109.59, 7.74) * mm, "mid": v(-114.49, 13.84) * mm, "end": v(-122.21, 15.03) * mm});
            skArc(sketch, "E16.1.0.349", {"start": v(-97.72, 69.82) * mm, "mid": v(-90, 71.02) * mm, "end": v(-85.1, 77.11) * mm});
            skArc(sketch, "E16.1.0.350", {"start": v(-49.89, 0.22) * mm, "mid": v(-52.1, -3.46) * mm, "end": v(-52.7, -7.72) * mm});
            skArc(sketch, "E16.1.0.351", {"start": v(-85.1, 7.74) * mm, "mid": v(-78.54, 8.76) * mm, "end": v(-74.38, 13.92) * mm});
            skArc(sketch, "E16.1.0.352", {"start": v(-109.59, 21.88) * mm, "mid": v(-105.14, 22.02) * mm, "end": v(-101.28, 24.22) * mm});
            skArc(sketch, "E16.1.0.353", {"start": v(-60.6, 21.88) * mm, "mid": v(-56.15, 22.02) * mm, "end": v(-52.3, 24.22) * mm});
            skLineSegment(sketch, "E16.1.0.354", {"start": v(-205.62, 68.12) * mm, "end": v(-181.12, 68.12) * mm, "construction": true});
            skArc(sketch, "E16.1.0.355", {"start": v(-97.34, 0.67) * mm, "mid": v(-99.43, 4.42) * mm, "end": v(-102.8, 7.07) * mm});
            skArc(sketch, "E16.1.0.356", {"start": v(-195.32, 85.52) * mm, "mid": v(-197.4, 89.28) * mm, "end": v(-200.79, 91.92) * mm});
            skArc(sketch, "E16.1.0.358", {"start": v(-110.23, 49.5) * mm, "mid": v(-102.64, 50.5) * mm, "end": v(-97.98, 56.57) * mm});
            skArc(sketch, "E16.1.0.359", {"start": v(-24.5, 0) * mm, "mid": v(-26.89, -3.84) * mm, "end": v(-27.34, -8.35) * mm});
            skArc(sketch, "E16.1.0.360", {"start": v(-109.97, 20.33) * mm, "mid": v(-105.67, 20.25) * mm, "end": v(-101.69, 21.86) * mm});
            skArc(sketch, "E16.1.0.361", {"start": v(-110.23, 21.21) * mm, "mid": v(-105.7, 21.06) * mm, "end": v(-101.57, 22.92) * mm});
            skArc(sketch, "E16.1.0.362", {"start": v(-74.38, 70.93) * mm, "mid": v(-78.54, 76.09) * mm, "end": v(-85.1, 77.11) * mm});
            skArc(sketch, "E16.1.0.363", {"start": v(-85.1, 50.17) * mm, "mid": v(-78.54, 51.19) * mm, "end": v(-74.38, 56.35) * mm});
            skArc(sketch, "E16.1.0.364", {"start": v(-72.85, 85.52) * mm, "mid": v(-68.4, 85.66) * mm, "end": v(-64.54, 87.86) * mm});
            skPoint(sketch, "E16.1.0.365", {"position": v(-146.97, 42.43) * mm});
            skArc(sketch, "E16.1.0.366", {"start": v(-62.14, 7.29) * mm, "mid": v(-66.3, 12.45) * mm, "end": v(-72.85, 13.47) * mm});
            skArc(sketch, "E16.1.0.367", {"start": v(-48.73, 41.54) * mm, "mid": v(-44.44, 41.47) * mm, "end": v(-40.45, 43.07) * mm});
            skArc(sketch, "E16.1.0.368", {"start": v(-110.23, 7.07) * mm, "mid": v(-114.89, 13.14) * mm, "end": v(-122.47, 14.14) * mm});
            skArc(sketch, "E16.1.0.369", {"start": v(-183.45, 105.18) * mm, "mid": v(-179.16, 105.1) * mm, "end": v(-175.17, 106.71) * mm});
            skPoint(sketch, "E16.1.0.370", {"position": v(-208.2, 106.07) * mm});
            skArc(sketch, "E16.1.0.371", {"start": v(-72.85, 71.38) * mm, "mid": v(-77.74, 77.48) * mm, "end": v(-85.47, 78.67) * mm});
            skArc(sketch, "E16.1.0.372", {"start": v(-195.7, 112.25) * mm, "mid": v(-187.97, 113.44) * mm, "end": v(-183.07, 119.54) * mm});
            skArc(sketch, "E16.1.0.373", {"start": v(-85.73, 91.92) * mm, "mid": v(-78.14, 92.92) * mm, "end": v(-73.48, 99) * mm});
            skPoint(sketch, "E16.1.0.374", {"position": v(-36.74, 7.07) * mm});
            skArc(sketch, "E16.1.0.375", {"start": v(-72.85, 0.67) * mm, "mid": v(-68.4, 0.8) * mm, "end": v(-64.54, 3.01) * mm});
            skArc(sketch, "E16.1.0.376", {"start": v(-85.1, 7.74) * mm, "mid": v(-90, 13.84) * mm, "end": v(-97.72, 15.03) * mm});
            skArc(sketch, "E16.1.0.377", {"start": v(-158.58, 50.17) * mm, "mid": v(-163.48, 56.26) * mm, "end": v(-171.2, 57.46) * mm});
            skArc(sketch, "E16.1.0.378", {"start": v(-48.35, 28.95) * mm, "mid": v(-41.8, 29.98) * mm, "end": v(-37.64, 35.14) * mm});
            skArc(sketch, "E16.1.0.379", {"start": v(-171.2, 83.97) * mm, "mid": v(-166.91, 83.9) * mm, "end": v(-162.93, 85.5) * mm});
            skArc(sketch, "E16.1.0.380", {"start": v(-146.97, 70.71) * mm, "mid": v(-151.63, 76.78) * mm, "end": v(-159.22, 77.78) * mm});
            skLineSegment(sketch, "E16.1.0.381", {"start": v(-171.46, 84.85) * mm, "end": v(-161.8, 87.44) * mm, "construction": true});
            skPoint(sketch, "E16.1.0.382", {"position": v(-134.72, 49.5) * mm});
            skArc(sketch, "E16.1.0.383", {"start": v(-48.73, -0.89) * mm, "mid": v(-44.44, -0.96) * mm, "end": v(-40.45, 0.65) * mm});
            skArc(sketch, "E16.1.0.384", {"start": v(-134.72, 106.07) * mm, "mid": v(-130.2, 105.91) * mm, "end": v(-126.07, 107.78) * mm});
            skArc(sketch, "E16.1.0.385", {"start": v(-48.35, -13.47) * mm, "mid": v(-53.25, -7.38) * mm, "end": v(-60.98, -6.18) * mm});
            skArc(sketch, "E16.1.0.386", {"start": v(-73.22, 83.97) * mm, "mid": v(-75.33, 80.05) * mm, "end": v(-75.35, 75.6) * mm});
            skArc(sketch, "E16.1.0.388", {"start": v(-98.88, 85.07) * mm, "mid": v(-101.09, 81.39) * mm, "end": v(-101.69, 77.14) * mm});
            skArc(sketch, "E16.1.0.389", {"start": v(-134.72, 91.92) * mm, "mid": v(-139.38, 98) * mm, "end": v(-146.97, 99) * mm});
            skArc(sketch, "E16.1.0.390", {"start": v(-135.62, 92.14) * mm, "mid": v(-139.78, 97.3) * mm, "end": v(-146.33, 98.33) * mm});
            skArc(sketch, "E16.1.0.391", {"start": v(-171.46, 28.28) * mm, "mid": v(-176.12, 34.36) * mm, "end": v(-183.71, 35.36) * mm});
            skArc(sketch, "E16.1.0.392", {"start": v(-62.14, 63.86) * mm, "mid": v(-64.48, 67.64) * mm, "end": v(-68.32, 69.88) * mm});
            skArc(sketch, "E16.1.0.393", {"start": v(-171.2, 27.4) * mm, "mid": v(-163.48, 28.6) * mm, "end": v(-158.58, 34.69) * mm});
            skArc(sketch, "E16.1.0.394", {"start": v(-86.63, 63.86) * mm, "mid": v(-88.97, 67.64) * mm, "end": v(-92.81, 69.88) * mm});
            skArc(sketch, "E16.1.0.395", {"start": v(-134.72, 91.92) * mm, "mid": v(-127.13, 92.92) * mm, "end": v(-122.47, 99) * mm});
            skArc(sketch, "E16.1.0.396", {"start": v(-147.87, 113.36) * mm, "mid": v(-152.03, 118.52) * mm, "end": v(-158.58, 119.54) * mm});
            skArc(sketch, "E16.1.0.397", {"start": v(-48.99, 0) * mm, "mid": v(-44.46, -0.15) * mm, "end": v(-40.34, 1.7) * mm});
            skArc(sketch, "E16.1.0.398", {"start": v(-85.73, 106.07) * mm, "mid": v(-88.13, 102.22) * mm, "end": v(-88.58, 97.72) * mm});
            skArc(sketch, "E16.1.0.399", {"start": v(-86.63, 106.28) * mm, "mid": v(-88.84, 102.6) * mm, "end": v(-89.44, 98.35) * mm});
            skArc(sketch, "E16.1.0.400", {"start": v(-172.36, 113.36) * mm, "mid": v(-176.52, 118.52) * mm, "end": v(-183.07, 119.54) * mm});
            skArc(sketch, "E16.1.0.401", {"start": v(-122.47, 42.43) * mm, "mid": v(-124.87, 38.58) * mm, "end": v(-125.32, 34.08) * mm});
            skArc(sketch, "E16.1.0.402", {"start": v(-109.59, 64.3) * mm, "mid": v(-111.67, 68.06) * mm, "end": v(-115.06, 70.71) * mm});
            skArc(sketch, "E16.1.0.403", {"start": v(-134.08, 106.73) * mm, "mid": v(-129.64, 106.87) * mm, "end": v(-125.78, 109.08) * mm});
            skArc(sketch, "E16.1.0.404", {"start": v(-86.63, 49.72) * mm, "mid": v(-90.8, 54.88) * mm, "end": v(-97.34, 55.9) * mm});
            skArc(sketch, "E16.1.0.405", {"start": v(-123.37, 70.93) * mm, "mid": v(-127.53, 76.09) * mm, "end": v(-134.08, 77.11) * mm});
            skArc(sketch, "E16.1.0.406", {"start": v(-134.08, 92.6) * mm, "mid": v(-138.98, 98.69) * mm, "end": v(-146.7, 99.88) * mm});
            skPoint(sketch, "E16.1.0.407", {"position": v(-122.47, 28.28) * mm});
            skLineSegment(sketch, "E16.1.0.408", {"start": v(-193.37, 46.9) * mm, "end": v(-168.88, 46.9) * mm, "construction": true});
            skArc(sketch, "E16.1.0.409", {"start": v(-25.4, 28.5) * mm, "mid": v(-29.55, 33.66) * mm, "end": v(-36.1, 34.69) * mm});
            skArc(sketch, "E16.1.0.410", {"start": v(-146.33, 71.38) * mm, "mid": v(-139.78, 72.4) * mm, "end": v(-135.62, 77.56) * mm});
            skArc(sketch, "E16.1.0.411", {"start": v(-85.47, 20.33) * mm, "mid": v(-81.18, 20.25) * mm, "end": v(-77.2, 21.86) * mm});
            skArc(sketch, "E16.1.0.412", {"start": v(-61.24, 21.21) * mm, "mid": v(-56.71, 21.06) * mm, "end": v(-52.58, 22.92) * mm});
            skArc(sketch, "E16.1.0.413", {"start": v(-73.22, 41.54) * mm, "mid": v(-68.93, 41.47) * mm, "end": v(-64.95, 43.07) * mm});
            skArc(sketch, "E16.1.0.414", {"start": v(-146.7, 41.54) * mm, "mid": v(-148.81, 37.62) * mm, "end": v(-148.84, 33.17) * mm});
            skArc(sketch, "E16.1.0.415", {"start": v(-73.48, -14.14) * mm, "mid": v(-78.14, -8.07) * mm, "end": v(-85.73, -7.07) * mm});
            skPoint(sketch, "E16.1.0.416", {"position": v(-134.72, 106.07) * mm});
            skArc(sketch, "E16.1.0.417", {"start": v(-109.97, 20.33) * mm, "mid": v(-112.07, 16.4) * mm, "end": v(-112.1, 11.96) * mm});
            skLineSegment(sketch, "E16.1.0.418", {"start": v(-146.97, 84.85) * mm, "end": v(-137.31, 87.44) * mm, "construction": true});
            skArc(sketch, "E16.1.0.419", {"start": v(-195.96, 113.14) * mm, "mid": v(-200.62, 119.2) * mm, "end": v(-208.2, 120.2) * mm});
            skArc(sketch, "E16.1.0.420", {"start": v(-121.84, -13.47) * mm, "mid": v(-115.29, -12.45) * mm, "end": v(-111.12, -7.29) * mm});
            skArc(sketch, "E16.1.0.421", {"start": v(-60.6, 50.17) * mm, "mid": v(-65.5, 56.26) * mm, "end": v(-73.22, 57.46) * mm});
            skArc(sketch, "E16.1.0.422", {"start": v(-122.47, 0) * mm, "mid": v(-117.95, -0.15) * mm, "end": v(-113.82, 1.7) * mm});
            skArc(sketch, "E16.1.0.423", {"start": v(-207.95, 105.18) * mm, "mid": v(-210.05, 101.26) * mm, "end": v(-210.07, 96.81) * mm});
            skArc(sketch, "E16.1.0.424", {"start": v(-183.45, 48.61) * mm, "mid": v(-185.84, 42.43) * mm, "end": v(-183.45, 36.24) * mm});
            skArc(sketch, "E16.1.0.425", {"start": v(-170.83, 43.1) * mm, "mid": v(-166.38, 43.23) * mm, "end": v(-162.52, 45.44) * mm});
            skArc(sketch, "E16.1.0.426", {"start": v(-134.46, 105.18) * mm, "mid": v(-130.17, 105.1) * mm, "end": v(-126.18, 106.71) * mm});
            skArc(sketch, "E16.1.0.427", {"start": v(-97.98, 84.85) * mm, "mid": v(-100.37, 81) * mm, "end": v(-100.83, 76.5) * mm});
            skArc(sketch, "E16.1.0.428", {"start": v(-36.74, 21.21) * mm, "mid": v(-39.14, 17.37) * mm, "end": v(-39.59, 12.86) * mm});
            skArc(sketch, "E16.1.0.429", {"start": v(-37.64, 7.29) * mm, "mid": v(-41.8, 12.45) * mm, "end": v(-48.35, 13.47) * mm});
            skArc(sketch, "E16.1.0.430", {"start": v(-159.22, 7.07) * mm, "mid": v(-163.88, 13.14) * mm, "end": v(-171.46, 14.14) * mm});
            skArc(sketch, "E16.1.0.431", {"start": v(-98.88, 42.64) * mm, "mid": v(-101.09, 38.96) * mm, "end": v(-101.69, 34.7) * mm});
            skArc(sketch, "E16.1.0.432", {"start": v(-110.23, 106.07) * mm, "mid": v(-105.7, 105.91) * mm, "end": v(-101.57, 107.78) * mm});
            skArc(sketch, "E16.1.0.433", {"start": v(-220.45, 113.14) * mm, "mid": v(-212.87, 114.14) * mm, "end": v(-208.2, 120.2) * mm});
            skArc(sketch, "E16.1.0.434", {"start": v(-160.11, 63.86) * mm, "mid": v(-162.46, 67.64) * mm, "end": v(-166.3, 69.88) * mm});
            skArc(sketch, "E16.1.0.435", {"start": v(-195.7, 69.82) * mm, "mid": v(-187.97, 71.02) * mm, "end": v(-183.07, 77.11) * mm});
            skArc(sketch, "E16.1.0.436", {"start": v(-123.37, 42.64) * mm, "mid": v(-125.58, 38.96) * mm, "end": v(-126.18, 34.7) * mm});
            skArc(sketch, "E16.1.0.437", {"start": v(-62.14, 92.14) * mm, "mid": v(-66.3, 97.3) * mm, "end": v(-72.85, 98.33) * mm});
            skArc(sketch, "E16.1.0.438", {"start": v(-171.46, 70.71) * mm, "mid": v(-176.12, 76.78) * mm, "end": v(-183.71, 77.78) * mm});
            skArc(sketch, "E16.1.0.439", {"start": v(-97.98, 113.14) * mm, "mid": v(-90.4, 114.14) * mm, "end": v(-85.73, 120.2) * mm});
            skLineSegment(sketch, "E16.1.0.440", {"start": v(-48.99, 42.43) * mm, "end": v(-39.33, 45.01) * mm, "construction": true});
            skArc(sketch, "E16.1.0.441", {"start": v(-73.22, -0.89) * mm, "mid": v(-68.93, -0.96) * mm, "end": v(-64.95, 0.65) * mm});
            skArc(sketch, "E16.1.0.442", {"start": v(-85.73, 63.64) * mm, "mid": v(-81.2, 63.49) * mm, "end": v(-77.08, 65.35) * mm});
            skArc(sketch, "E16.1.0.444", {"start": v(-24.24, -0.89) * mm, "mid": v(-26.34, -4.8) * mm, "end": v(-26.36, -9.25) * mm});
            skArc(sketch, "E16.1.0.445", {"start": v(-97.34, 0.67) * mm, "mid": v(-92.9, 0.8) * mm, "end": v(-89.03, 3.01) * mm});
            skArc(sketch, "E16.1.0.446", {"start": v(-183.71, 49.5) * mm, "mid": v(-188.37, 55.57) * mm, "end": v(-195.96, 56.57) * mm});
            skArc(sketch, "E16.1.0.447", {"start": v(-146.7, 41.54) * mm, "mid": v(-142.42, 41.47) * mm, "end": v(-138.43, 43.07) * mm});
            skArc(sketch, "E16.1.0.448", {"start": v(-60.6, 21.88) * mm, "mid": v(-62.68, 25.64) * mm, "end": v(-66.07, 28.28) * mm});
            skArc(sketch, "E16.1.0.449", {"start": v(-86.63, 21.43) * mm, "mid": v(-88.84, 17.75) * mm, "end": v(-89.44, 13.5) * mm});
            skArc(sketch, "E16.1.0.450", {"start": v(-23.86, 0.67) * mm, "mid": v(-19.41, 0.8) * mm, "end": v(-15.55, 3.01) * mm});
            skArc(sketch, "E16.1.0.451", {"start": v(-146.33, 28.95) * mm, "mid": v(-151.23, 35.05) * mm, "end": v(-158.96, 36.24) * mm});
            skArc(sketch, "E16.1.0.452", {"start": v(-121.84, 85.52) * mm, "mid": v(-123.92, 89.28) * mm, "end": v(-127.3, 91.92) * mm});
            skArc(sketch, "E16.1.0.453", {"start": v(-13.15, 7.29) * mm, "mid": v(-15.98, 0) * mm, "end": v(-13.15, -7.29) * mm});
            skArc(sketch, "E16.1.0.454", {"start": v(-49.89, 42.64) * mm, "mid": v(-52.1, 38.96) * mm, "end": v(-52.7, 34.7) * mm});
            skArc(sketch, "E16.1.0.455", {"start": v(-134.08, 64.3) * mm, "mid": v(-129.64, 64.44) * mm, "end": v(-125.78, 66.65) * mm});
            skArc(sketch, "E16.1.0.456", {"start": v(-171.46, 113.14) * mm, "mid": v(-163.88, 114.14) * mm, "end": v(-159.22, 120.2) * mm});
            skArc(sketch, "E16.1.0.457", {"start": v(-158.96, 105.18) * mm, "mid": v(-154.66, 105.1) * mm, "end": v(-150.68, 106.71) * mm});
            skArc(sketch, "E16.1.0.458", {"start": v(-123.37, 113.36) * mm, "mid": v(-127.53, 118.52) * mm, "end": v(-134.08, 119.54) * mm});
            skArc(sketch, "E16.1.0.459", {"start": v(-122.47, 70.71) * mm, "mid": v(-114.89, 71.7) * mm, "end": v(-110.23, 77.78) * mm});
            skArc(sketch, "E16.1.0.460", {"start": v(-85.1, 92.6) * mm, "mid": v(-78.54, 93.62) * mm, "end": v(-74.38, 98.78) * mm});
            skArc(sketch, "E16.1.0.461", {"start": v(-122.47, 113.14) * mm, "mid": v(-127.13, 119.2) * mm, "end": v(-134.72, 120.2) * mm});
            skArc(sketch, "E16.1.0.462", {"start": v(-183.71, 63.64) * mm, "mid": v(-179.19, 63.49) * mm, "end": v(-175.06, 65.35) * mm});
            skArc(sketch, "E16.1.0.463", {"start": v(-195.96, 113.14) * mm, "mid": v(-188.37, 114.14) * mm, "end": v(-183.71, 120.2) * mm});
            skArc(sketch, "E16.1.0.464", {"start": v(-146.7, 83.97) * mm, "mid": v(-148.81, 80.05) * mm, "end": v(-148.84, 75.6) * mm});
            skArc(sketch, "E16.1.0.465", {"start": v(-147.87, 85.07) * mm, "mid": v(-150.08, 81.39) * mm, "end": v(-150.68, 77.14) * mm});
            skPoint(sketch, "E16.1.0.466", {"position": v(-122.47, -14.14) * mm});
            skPoint(sketch, "E16.1.0.467", {"position": v(-146.97, 28.28) * mm});
            skArc(sketch, "E16.1.0.468", {"start": v(-146.33, 85.52) * mm, "mid": v(-148.41, 89.28) * mm, "end": v(-151.8, 91.92) * mm});
            skArc(sketch, "E16.1.0.469", {"start": v(-146.97, 70.71) * mm, "mid": v(-139.38, 71.7) * mm, "end": v(-134.72, 77.78) * mm});
            skArc(sketch, "E16.1.0.470", {"start": v(-48.73, 41.54) * mm, "mid": v(-50.84, 37.62) * mm, "end": v(-50.86, 33.17) * mm});
            skLineSegment(sketch, "E16.1.0.471", {"start": v(-159.22, 21.21) * mm, "end": v(-149.56, 23.8) * mm, "construction": true});
            skArc(sketch, "E16.1.0.472", {"start": v(-122.47, 84.85) * mm, "mid": v(-117.95, 84.7) * mm, "end": v(-113.82, 86.56) * mm});
            skArc(sketch, "E16.1.0.473", {"start": v(-98.88, 70.93) * mm, "mid": v(-103.04, 76.09) * mm, "end": v(-109.59, 77.11) * mm});
            skArc(sketch, "E16.1.0.474", {"start": v(-48.35, 0.67) * mm, "mid": v(-43.9, 0.8) * mm, "end": v(-40.04, 3.01) * mm});
            skArc(sketch, "E16.1.0.475", {"start": v(-147.87, 42.64) * mm, "mid": v(-150.08, 38.96) * mm, "end": v(-150.68, 34.7) * mm});
            skArc(sketch, "E16.1.0.476", {"start": v(-159.22, 91.92) * mm, "mid": v(-163.88, 98) * mm, "end": v(-171.46, 99) * mm});
            skArc(sketch, "E16.1.0.477", {"start": v(-134.72, 106.07) * mm, "mid": v(-137.12, 102.22) * mm, "end": v(-137.57, 97.72) * mm});
            skArc(sketch, "E16.1.0.478", {"start": v(-37.64, 21.43) * mm, "mid": v(-39.85, 17.75) * mm, "end": v(-40.45, 13.5) * mm});
            skPoint(sketch, "E16.1.0.479", {"position": v(-110.23, 7.07) * mm});
            skArc(sketch, "E16.1.0.480", {"start": v(-146.33, 71.38) * mm, "mid": v(-151.23, 77.48) * mm, "end": v(-158.96, 78.67) * mm});
            skPoint(sketch, "E16.1.0.481", {"position": v(-61.24, 21.21) * mm});
            skArc(sketch, "E16.1.0.482", {"start": v(-111.12, 7.29) * mm, "mid": v(-115.29, 12.45) * mm, "end": v(-121.84, 13.47) * mm});
            skArc(sketch, "E16.1.0.483", {"start": v(-146.97, 28.28) * mm, "mid": v(-139.38, 29.28) * mm, "end": v(-134.72, 35.36) * mm});
            skPoint(sketch, "E16.1.0.484", {"position": v(-122.47, 42.43) * mm});
            skArc(sketch, "E16.1.0.485", {"start": v(-159.22, 21.21) * mm, "mid": v(-161.61, 17.37) * mm, "end": v(-162.06, 12.86) * mm});
            skPoint(sketch, "E16.1.0.486", {"position": v(-122.47, 0) * mm});
            skArc(sketch, "E16.1.0.487", {"start": v(-36.48, 20.33) * mm, "mid": v(-38.59, 16.4) * mm, "end": v(-38.6, 11.96) * mm});
            skArc(sketch, "E16.1.0.488", {"start": v(-48.99, 0) * mm, "mid": v(-51.12, 4) * mm, "end": v(-54.8, 6.64) * mm});
            skPoint(sketch, "E16.1.0.489", {"position": v(-73.48, 0) * mm});
            skArc(sketch, "E16.1.0.490", {"start": v(-183.71, 91.92) * mm, "mid": v(-176.12, 92.92) * mm, "end": v(-171.46, 99) * mm});
            skArc(sketch, "E16.1.0.491", {"start": v(-74.38, 113.36) * mm, "mid": v(-78.54, 118.52) * mm, "end": v(-85.1, 119.54) * mm});
            skArc(sketch, "E16.1.0.492", {"start": v(-160.11, 21.43) * mm, "mid": v(-162.33, 17.75) * mm, "end": v(-162.93, 13.5) * mm});
            skPoint(sketch, "E16.1.0.494", {"position": v(-122.47, 70.71) * mm});
            skArc(sketch, "E16.1.0.495", {"start": v(-134.46, 6.18) * mm, "mid": v(-126.73, 7.38) * mm, "end": v(-121.84, 13.47) * mm});
            skLineSegment(sketch, "E16.1.0.496", {"start": v(-36.74, 21.21) * mm, "end": v(-27.08, 23.8) * mm, "construction": true});
            skArc(sketch, "E16.1.0.497", {"start": v(-73.48, 42.43) * mm, "mid": v(-68.96, 42.28) * mm, "end": v(-64.83, 44.14) * mm});
            skPoint(sketch, "E16.1.0.498", {"position": v(-110.23, 63.64) * mm});
            skPoint(sketch, "E16.1.0.499", {"position": v(-48.99, 0) * mm});
            skArc(sketch, "E16.1.0.500", {"start": v(-25.4, 0.22) * mm, "mid": v(-27.6, -3.46) * mm, "end": v(-28.2, -7.72) * mm});
            skArc(sketch, "E16.1.0.501", {"start": v(-110.23, 63.64) * mm, "mid": v(-105.7, 63.49) * mm, "end": v(-101.57, 65.35) * mm});
            skArc(sketch, "E16.1.0.502", {"start": v(-36.74, 7.07) * mm, "mid": v(-41.4, 13.14) * mm, "end": v(-48.99, 14.14) * mm});
            skPoint(sketch, "E16.1.0.503", {"position": v(-159.22, 7.07) * mm});
            skLineSegment(sketch, "E16.1.0.504", {"start": v(-156.63, -16.73) * mm, "end": v(-131.63, -16.73) * mm, "construction": true});
            skArc(sketch, "E16.1.0.505", {"start": v(-111.12, 21.43) * mm, "mid": v(-113.34, 17.75) * mm, "end": v(-113.94, 13.5) * mm});
            skArc(sketch, "E16.1.0.506", {"start": v(-158.96, 105.18) * mm, "mid": v(-161.06, 101.26) * mm, "end": v(-161.08, 96.81) * mm});
            skArc(sketch, "E16.1.0.507", {"start": v(-62.14, 92.14) * mm, "mid": v(-64.97, 84.85) * mm, "end": v(-62.14, 77.56) * mm});
            skArc(sketch, "E16.1.0.508", {"start": v(-73.22, -0.89) * mm, "mid": v(-75.33, -4.8) * mm, "end": v(-75.35, -9.25) * mm});
            skArc(sketch, "E16.1.0.509", {"start": v(-109.97, 105.18) * mm, "mid": v(-112.07, 101.26) * mm, "end": v(-112.1, 96.81) * mm});
            skArc(sketch, "E16.1.0.510", {"start": v(-158.58, 7.74) * mm, "mid": v(-163.48, 13.84) * mm, "end": v(-171.2, 15.03) * mm});
            skArc(sketch, "E16.1.0.511", {"start": v(-122.47, 70.71) * mm, "mid": v(-127.13, 76.78) * mm, "end": v(-134.72, 77.78) * mm});
            skArc(sketch, "E16.1.0.512", {"start": v(-109.97, 91.04) * mm, "mid": v(-102.24, 92.23) * mm, "end": v(-97.34, 98.33) * mm});
            skArc(sketch, "E16.1.0.513", {"start": v(-98.88, 28.5) * mm, "mid": v(-103.04, 33.66) * mm, "end": v(-109.59, 34.69) * mm});
            skArc(sketch, "E16.1.0.514", {"start": v(-109.59, 106.73) * mm, "mid": v(-111.67, 110.5) * mm, "end": v(-115.06, 113.14) * mm});
            skArc(sketch, "E16.1.0.515", {"start": v(-122.21, 69.82) * mm, "mid": v(-114.49, 71.02) * mm, "end": v(-109.59, 77.11) * mm});
            skArc(sketch, "E16.1.0.516", {"start": v(-122.21, 27.4) * mm, "mid": v(-114.49, 28.6) * mm, "end": v(-109.59, 34.69) * mm});
            skArc(sketch, "E16.1.0.517", {"start": v(-109.59, 21.88) * mm, "mid": v(-111.67, 25.64) * mm, "end": v(-115.06, 28.28) * mm});
            skArc(sketch, "E16.1.0.518", {"start": v(-158.58, 106.73) * mm, "mid": v(-160.66, 110.5) * mm, "end": v(-164.05, 113.14) * mm});
            skArc(sketch, "E16.1.0.519", {"start": v(-121.84, 28.95) * mm, "mid": v(-126.73, 35.05) * mm, "end": v(-134.46, 36.24) * mm});
            skArc(sketch, "E16.1.0.520", {"start": v(-146.97, 84.85) * mm, "mid": v(-149.36, 81) * mm, "end": v(-149.82, 76.5) * mm});
            skArc(sketch, "E16.1.0.521", {"start": v(-134.46, 20.33) * mm, "mid": v(-136.57, 16.4) * mm, "end": v(-136.59, 11.96) * mm});
            skArc(sketch, "E16.1.0.522", {"start": v(-73.22, 41.54) * mm, "mid": v(-75.33, 37.62) * mm, "end": v(-75.35, 33.17) * mm});
            skArc(sketch, "E16.1.0.523", {"start": v(-207.57, 106.73) * mm, "mid": v(-209.65, 110.5) * mm, "end": v(-213.03, 113.14) * mm});
            skPoint(sketch, "E16.1.0.524", {"position": v(-171.46, 42.43) * mm});
            skArc(sketch, "E16.1.0.525", {"start": v(-183.45, 105.18) * mm, "mid": v(-185.56, 101.26) * mm, "end": v(-185.58, 96.81) * mm});
            skArc(sketch, "E16.1.0.526", {"start": v(-146.97, -14.14) * mm, "mid": v(-139.38, -13.14) * mm, "end": v(-134.72, -7.07) * mm});
            skArc(sketch, "E16.1.0.527", {"start": v(-183.71, 49.5) * mm, "mid": v(-176.12, 50.5) * mm, "end": v(-171.46, 56.57) * mm});
            skArc(sketch, "E16.1.0.528", {"start": v(-159.22, 49.5) * mm, "mid": v(-151.63, 50.5) * mm, "end": v(-146.97, 56.57) * mm});
            skArc(sketch, "E16.1.0.529", {"start": v(-134.72, 21.21) * mm, "mid": v(-130.2, 21.06) * mm, "end": v(-126.07, 22.92) * mm});
            skArc(sketch, "E16.1.0.530", {"start": v(-73.48, 0) * mm, "mid": v(-68.96, -0.15) * mm, "end": v(-64.83, 1.7) * mm});
            skArc(sketch, "E16.1.0.531", {"start": v(-135.62, 63.86) * mm, "mid": v(-137.96, 67.64) * mm, "end": v(-141.8, 69.88) * mm});
            skArc(sketch, "E16.1.0.532", {"start": v(-183.45, 91.04) * mm, "mid": v(-175.72, 92.23) * mm, "end": v(-170.83, 98.33) * mm});
            skArc(sketch, "E16.1.0.533", {"start": v(-134.08, 21.88) * mm, "mid": v(-136.17, 25.64) * mm, "end": v(-139.55, 28.28) * mm});
            skArc(sketch, "E16.1.0.534", {"start": v(-73.48, 84.85) * mm, "mid": v(-68.96, 84.7) * mm, "end": v(-64.83, 86.56) * mm});
            skArc(sketch, "E16.1.0.535", {"start": v(-121.84, 71.38) * mm, "mid": v(-115.29, 72.4) * mm, "end": v(-111.12, 77.56) * mm});
            skPoint(sketch, "E16.1.0.536", {"position": v(-110.23, 91.92) * mm});
            skArc(sketch, "E16.1.0.537", {"start": v(-158.58, 92.6) * mm, "mid": v(-152.03, 93.62) * mm, "end": v(-147.87, 98.78) * mm});
            skArc(sketch, "E16.1.0.538", {"start": v(-122.21, 83.97) * mm, "mid": v(-124.32, 80.05) * mm, "end": v(-124.34, 75.6) * mm});
            skPoint(sketch, "E16.1.0.539", {"position": v(-97.98, 113.14) * mm});
            skArc(sketch, "E16.1.0.540", {"start": v(-72.85, -13.47) * mm, "mid": v(-77.74, -7.38) * mm, "end": v(-85.47, -6.18) * mm});
            skArc(sketch, "E16.1.0.541", {"start": v(-110.23, 106.07) * mm, "mid": v(-112.62, 102.22) * mm, "end": v(-113.07, 97.72) * mm});
            skPoint(sketch, "E16.1.0.542", {"position": v(-159.22, 91.92) * mm});
            skPoint(sketch, "E16.1.0.543", {"position": v(-171.46, 28.28) * mm});
            skArc(sketch, "E16.1.0.544", {"start": v(-60.98, 62.75) * mm, "mid": v(-56.68, 62.68) * mm, "end": v(-52.7, 64.29) * mm});
            skPoint(sketch, "E16.1.0.545", {"position": v(-183.71, 91.92) * mm});
            skArc(sketch, "E16.1.0.546", {"start": v(-48.99, 42.43) * mm, "mid": v(-44.46, 42.28) * mm, "end": v(-40.34, 44.14) * mm});
            skArc(sketch, "E16.1.0.547", {"start": v(-97.34, 43.1) * mm, "mid": v(-92.9, 43.23) * mm, "end": v(-89.03, 45.44) * mm});
            skArc(sketch, "E16.1.0.548", {"start": v(-158.58, 92.6) * mm, "mid": v(-163.48, 98.69) * mm, "end": v(-171.2, 99.88) * mm});
            skArc(sketch, "E16.1.0.549", {"start": v(-220.2, 112.25) * mm, "mid": v(-222.58, 106.07) * mm, "end": v(-220.2, 99.88) * mm});
            skPoint(sketch, "E16.1.0.550", {"position": v(-97.98, 0) * mm});
            skPoint(sketch, "E16.1.0.551", {"position": v(-24.5, 0) * mm});
            skArc(sketch, "E16.1.0.552", {"start": v(-36.74, 21.21) * mm, "mid": v(-32.22, 21.06) * mm, "end": v(-28.09, 22.92) * mm});
            skArc(sketch, "E16.1.0.553", {"start": v(-72.85, 0.67) * mm, "mid": v(-74.93, 4.42) * mm, "end": v(-78.31, 7.07) * mm});
            skArc(sketch, "E16.1.0.554", {"start": v(-85.47, 48.61) * mm, "mid": v(-77.74, 49.8) * mm, "end": v(-72.85, 55.9) * mm});
            skArc(sketch, "E16.1.0.556", {"start": v(-134.72, 49.5) * mm, "mid": v(-127.13, 50.5) * mm, "end": v(-122.47, 56.57) * mm});
            skArc(sketch, "E16.1.0.557", {"start": v(-48.35, 43.1) * mm, "mid": v(-50.44, 46.85) * mm, "end": v(-53.82, 49.5) * mm});
            skArc(sketch, "E16.1.0.558", {"start": v(-73.22, 27.4) * mm, "mid": v(-65.5, 28.6) * mm, "end": v(-60.6, 34.69) * mm});
            skArc(sketch, "E16.1.0.559", {"start": v(-48.99, 42.43) * mm, "mid": v(-51.38, 38.58) * mm, "end": v(-51.84, 34.08) * mm});
            skArc(sketch, "E16.1.0.560", {"start": v(-60.98, 6.18) * mm, "mid": v(-53.25, 7.38) * mm, "end": v(-48.35, 13.47) * mm});
            skArc(sketch, "E16.1.0.561", {"start": v(-183.07, 50.17) * mm, "mid": v(-187.97, 56.26) * mm, "end": v(-195.7, 57.46) * mm});
            skLineSegment(sketch, "E16.1.0.562", {"start": v(-181.12, 25.7) * mm, "end": v(-156.63, 25.7) * mm, "construction": true});
            skArc(sketch, "E16.1.0.563", {"start": v(-85.1, 92.6) * mm, "mid": v(-90, 98.69) * mm, "end": v(-97.72, 99.88) * mm});
            skArc(sketch, "E16.1.0.564", {"start": v(-85.73, 21.21) * mm, "mid": v(-88.13, 17.37) * mm, "end": v(-88.58, 12.86) * mm});
            skArc(sketch, "E16.1.0.565", {"start": v(-60.98, 48.61) * mm, "mid": v(-53.25, 49.8) * mm, "end": v(-48.35, 55.9) * mm});
            skArc(sketch, "E16.1.0.566", {"start": v(-159.22, 91.92) * mm, "mid": v(-162.15, 84.85) * mm, "end": v(-159.22, 77.78) * mm});
            skPoint(sketch, "E16.1.0.567", {"position": v(-195.96, 84.85) * mm});
            skArc(sketch, "E16.1.0.568", {"start": v(-146.97, 84.85) * mm, "mid": v(-149.1, 88.85) * mm, "end": v(-152.78, 91.5) * mm});
            skArc(sketch, "E16.1.0.569", {"start": v(-85.73, 91.92) * mm, "mid": v(-78.14, 92.92) * mm, "end": v(-73.48, 99) * mm});
            skArc(sketch, "E16.1.0.570", {"start": v(-122.21, -0.89) * mm, "mid": v(-124.32, -4.8) * mm, "end": v(-124.34, -9.25) * mm});
            skArc(sketch, "E16.1.0.571", {"start": v(-111.12, 63.86) * mm, "mid": v(-113.34, 60.18) * mm, "end": v(-113.94, 55.92) * mm});
            skArc(sketch, "E16.1.0.572", {"start": v(-146.7, 69.82) * mm, "mid": v(-149.1, 63.64) * mm, "end": v(-146.7, 57.46) * mm});
            skPoint(sketch, "E16.1.0.573", {"position": v(-85.73, 106.07) * mm});
            skPoint(sketch, "E16.1.0.574", {"position": v(-134.72, 91.92) * mm});
            skArc(sketch, "E16.1.0.575", {"start": v(-183.71, 49.5) * mm, "mid": v(-176.12, 50.5) * mm, "end": v(-171.46, 56.57) * mm});
            skArc(sketch, "E16.1.0.576", {"start": v(-160.11, 92.14) * mm, "mid": v(-162.95, 84.85) * mm, "end": v(-160.11, 77.56) * mm});
            skArc(sketch, "E16.1.0.577", {"start": v(-134.72, 21.21) * mm, "mid": v(-136.85, 25.2) * mm, "end": v(-140.53, 27.85) * mm});
            skArc(sketch, "E16.1.0.578", {"start": v(-97.98, 70.71) * mm, "mid": v(-90.4, 71.7) * mm, "end": v(-85.73, 77.78) * mm});
            skPoint(sketch, "E16.1.0.579", {"position": v(-183.71, 106.07) * mm});
            skArc(sketch, "E16.1.0.580", {"start": v(-134.46, 91.04) * mm, "mid": v(-136.85, 84.85) * mm, "end": v(-134.46, 78.67) * mm});
            skArc(sketch, "E16.1.0.581", {"start": v(-184.6, 63.86) * mm, "mid": v(-186.95, 67.64) * mm, "end": v(-190.8, 69.88) * mm});
            skPoint(sketch, "E16.1.0.582", {"position": v(-183.71, 91.92) * mm});
            skArc(sketch, "E16.1.0.583", {"start": v(-147.87, 70.93) * mm, "mid": v(-150.7, 63.64) * mm, "end": v(-147.87, 56.35) * mm});
            skArc(sketch, "E16.1.0.584", {"start": v(-97.98, 28.28) * mm, "mid": v(-100.9, 21.21) * mm, "end": v(-97.98, 14.14) * mm});
            skLineSegment(sketch, "E16.1.0.585", {"start": v(-183.71, 63.64) * mm, "end": v(-198.11, 59.78) * mm, "construction": true});
            skArc(sketch, "E16.1.0.586", {"start": v(-62.14, 49.72) * mm, "mid": v(-64.97, 42.43) * mm, "end": v(-62.14, 35.14) * mm});
            skArc(sketch, "E16.1.0.587", {"start": v(-172.36, 70.93) * mm, "mid": v(-175.2, 63.64) * mm, "end": v(-172.36, 56.35) * mm});
            skPoint(sketch, "E16.1.0.588", {"position": v(-85.73, 21.21) * mm});
            skArc(sketch, "E16.1.0.589", {"start": v(-74.38, 0.22) * mm, "mid": v(-76.72, 4) * mm, "end": v(-80.56, 6.24) * mm});
            skArc(sketch, "E16.1.0.590", {"start": v(-134.72, 91.92) * mm, "mid": v(-127.13, 92.92) * mm, "end": v(-122.47, 99) * mm});
            skPoint(sketch, "E16.1.0.591", {"position": v(-171.46, 28.28) * mm});
            skArc(sketch, "E16.1.0.592", {"start": v(-85.73, 7.07) * mm, "mid": v(-90.4, 13.14) * mm, "end": v(-97.98, 14.14) * mm});
            skArc(sketch, "E16.1.0.593", {"start": v(-158.96, 6.18) * mm, "mid": v(-151.23, 7.38) * mm, "end": v(-146.33, 13.47) * mm});
            skLineSegment(sketch, "E16.1.0.594", {"start": v(-122.47, 42.43) * mm, "end": v(-136.88, 38.57) * mm, "construction": true});
            skArc(sketch, "E16.1.0.595", {"start": v(-109.97, 48.61) * mm, "mid": v(-112.36, 42.43) * mm, "end": v(-109.97, 36.24) * mm});
            skArc(sketch, "E16.1.0.596", {"start": v(-121.84, -13.47) * mm, "mid": v(-126.73, -7.38) * mm, "end": v(-134.46, -6.18) * mm});
            skArc(sketch, "E16.1.0.597", {"start": v(-85.73, 49.5) * mm, "mid": v(-90.4, 55.57) * mm, "end": v(-97.98, 56.57) * mm});
            skArc(sketch, "E16.1.0.598", {"start": v(-122.47, 70.71) * mm, "mid": v(-127.13, 76.78) * mm, "end": v(-134.72, 77.78) * mm});
            skArc(sketch, "E16.1.0.599", {"start": v(-159.22, 106.07) * mm, "mid": v(-161.35, 110.06) * mm, "end": v(-165.02, 112.7) * mm});
            skPoint(sketch, "E16.1.0.600", {"position": v(-183.71, 49.5) * mm});
            skArc(sketch, "E16.1.0.601", {"start": v(-110.23, 7.07) * mm, "mid": v(-113.16, 0) * mm, "end": v(-110.23, -7.07) * mm});
            skPoint(sketch, "E16.1.0.602", {"position": v(-208.24, 106) * mm});
            skArc(sketch, "E16.1.0.603", {"start": v(-134.72, 63.64) * mm, "mid": v(-136.85, 67.63) * mm, "end": v(-140.53, 70.28) * mm});
            skArc(sketch, "E16.1.0.604", {"start": v(-61.24, 49.5) * mm, "mid": v(-64.17, 42.43) * mm, "end": v(-61.24, 35.36) * mm});
            skArc(sketch, "E16.1.0.605", {"start": v(-73.22, 83.97) * mm, "mid": v(-68.93, 83.9) * mm, "end": v(-64.95, 85.5) * mm});
            skLineSegment(sketch, "E16.1.0.606", {"start": v(-146.97, 42.43) * mm, "end": v(-137.31, 45.01) * mm, "construction": true});
            skArc(sketch, "E16.1.0.607", {"start": v(-159.22, 63.64) * mm, "mid": v(-161.35, 67.63) * mm, "end": v(-165.02, 70.28) * mm});
            skArc(sketch, "E16.1.0.608", {"start": v(-111.12, 7.29) * mm, "mid": v(-113.96, 0) * mm, "end": v(-111.12, -7.29) * mm});
            skArc(sketch, "E16.1.0.609", {"start": v(-146.97, 84.85) * mm, "mid": v(-142.44, 84.7) * mm, "end": v(-138.31, 86.56) * mm});
            skPoint(sketch, "E16.1.0.610", {"position": v(-73.48, 28.28) * mm});
            skPoint(sketch, "E16.1.0.611", {"position": v(-97.98, 28.28) * mm});
            skArc(sketch, "E16.1.0.612", {"start": v(-110.23, 49.5) * mm, "mid": v(-102.64, 50.5) * mm, "end": v(-97.98, 56.57) * mm});
            skArc(sketch, "E16.1.0.613", {"start": v(-171.46, 70.71) * mm, "mid": v(-174.4, 63.64) * mm, "end": v(-171.46, 56.57) * mm});
            skPoint(sketch, "E16.1.0.614", {"position": v(-122.47, 70.71) * mm});
            skArc(sketch, "E16.1.0.615", {"start": v(-73.48, 84.85) * mm, "mid": v(-75.62, 88.85) * mm, "end": v(-79.3, 91.5) * mm});
            skArc(sketch, "E16.1.0.616", {"start": v(-195.96, 84.85) * mm, "mid": v(-198.1, 88.85) * mm, "end": v(-201.77, 91.5) * mm});
            skArc(sketch, "E16.1.0.617", {"start": v(-146.97, 0) * mm, "mid": v(-149.1, 4) * mm, "end": v(-152.78, 6.64) * mm});
            skArc(sketch, "E16.1.0.618", {"start": v(-171.46, 70.71) * mm, "mid": v(-163.88, 71.7) * mm, "end": v(-159.22, 77.78) * mm});
            skArc(sketch, "E16.1.0.619", {"start": v(-146.97, 70.71) * mm, "mid": v(-139.38, 71.7) * mm, "end": v(-134.72, 77.78) * mm});
            skPoint(sketch, "E16.1.0.620", {"position": v(-110.23, 106.07) * mm});
            skArc(sketch, "E16.1.0.621", {"start": v(-208.2, 91.92) * mm, "mid": v(-200.62, 92.92) * mm, "end": v(-195.96, 99) * mm});
            skArc(sketch, "E16.1.0.622", {"start": v(-122.47, 70.71) * mm, "mid": v(-125.4, 63.64) * mm, "end": v(-122.47, 56.57) * mm});
            skArc(sketch, "E16.1.0.623", {"start": v(-171.46, 113.14) * mm, "mid": v(-174.4, 106.07) * mm, "end": v(-171.46, 99) * mm});
            skArc(sketch, "E16.1.0.624", {"start": v(-158.96, 48.61) * mm, "mid": v(-161.35, 42.43) * mm, "end": v(-158.96, 36.24) * mm});
            skLineSegment(sketch, "E16.1.0.625", {"start": v(-110.23, 106.07) * mm, "end": v(-100.57, 108.65) * mm, "construction": true});
            skPoint(sketch, "E16.1.0.626", {"position": v(-85.73, 91.92) * mm});
            skArc(sketch, "E16.1.0.627", {"start": v(-73.48, 70.71) * mm, "mid": v(-78.14, 76.78) * mm, "end": v(-85.73, 77.78) * mm});
            skArc(sketch, "E16.1.0.628", {"start": v(-49.89, 42.64) * mm, "mid": v(-52.23, 46.43) * mm, "end": v(-56.07, 48.67) * mm});
            skArc(sketch, "E16.1.0.629", {"start": v(-135.62, 92.14) * mm, "mid": v(-138.45, 84.85) * mm, "end": v(-135.62, 77.56) * mm});
            skPoint(sketch, "E16.1.0.630", {"position": v(-171.46, 70.71) * mm});
            skArc(sketch, "E16.1.0.631", {"start": v(-49.89, 28.5) * mm, "mid": v(-52.72, 21.21) * mm, "end": v(-49.89, 13.92) * mm});
            skArc(sketch, "E16.1.0.632", {"start": v(-172.36, 85.07) * mm, "mid": v(-174.7, 88.85) * mm, "end": v(-178.54, 91.1) * mm});
            skArc(sketch, "E16.1.0.633", {"start": v(-109.97, 91.04) * mm, "mid": v(-112.36, 84.85) * mm, "end": v(-109.97, 78.67) * mm});
            skPoint(sketch, "E16.1.0.634", {"position": v(-159.22, 63.64) * mm});
            skPoint(sketch, "E16.1.0.635", {"position": v(-183.75, 63.57) * mm});
            skArc(sketch, "E16.1.0.636", {"start": v(-134.72, 49.5) * mm, "mid": v(-139.38, 55.57) * mm, "end": v(-146.97, 56.57) * mm});
            skArc(sketch, "E16.1.0.637", {"start": v(-160.11, 106.28) * mm, "mid": v(-162.46, 110.07) * mm, "end": v(-166.3, 112.3) * mm});
            skArc(sketch, "E16.1.0.638", {"start": v(-48.99, 42.43) * mm, "mid": v(-51.12, 46.42) * mm, "end": v(-54.8, 49.07) * mm});
            skArc(sketch, "E16.1.0.639", {"start": v(-160.11, 49.72) * mm, "mid": v(-162.95, 42.43) * mm, "end": v(-160.11, 35.14) * mm});
            skArc(sketch, "E16.1.0.640", {"start": v(-196.86, 113.36) * mm, "mid": v(-199.69, 106.07) * mm, "end": v(-196.86, 98.78) * mm});
            skPoint(sketch, "E16.1.0.641", {"position": v(-159.22, 91.92) * mm});
            skPoint(sketch, "E16.1.0.642", {"position": v(-159.22, 106.07) * mm});
            skArc(sketch, "E16.1.0.643", {"start": v(-147.87, 85.07) * mm, "mid": v(-150.2, 88.85) * mm, "end": v(-154.05, 91.1) * mm});
            skArc(sketch, "E16.1.0.644", {"start": v(-110.23, 7.07) * mm, "mid": v(-114.89, 13.14) * mm, "end": v(-122.47, 14.14) * mm});
            skPoint(sketch, "E16.1.0.645", {"position": v(-110.23, 63.64) * mm});
            skArc(sketch, "E16.1.0.646", {"start": v(-73.22, 27.4) * mm, "mid": v(-75.61, 21.21) * mm, "end": v(-73.22, 15.03) * mm});
            skArc(sketch, "E16.1.0.647", {"start": v(-184.6, 63.86) * mm, "mid": v(-186.82, 60.18) * mm, "end": v(-187.42, 55.92) * mm});
            skArc(sketch, "E16.1.0.648", {"start": v(-48.99, 28.28) * mm, "mid": v(-41.4, 29.28) * mm, "end": v(-36.74, 35.36) * mm});
            skArc(sketch, "E16.1.0.649", {"start": v(-208.2, 106.07) * mm, "mid": v(-210.34, 110.06) * mm, "end": v(-214.01, 112.7) * mm});
            skArc(sketch, "E16.1.0.650", {"start": v(-97.98, 113.14) * mm, "mid": v(-100.9, 106.07) * mm, "end": v(-97.98, 99) * mm});
            skArc(sketch, "E16.1.0.651", {"start": v(-110.23, 49.5) * mm, "mid": v(-114.89, 55.57) * mm, "end": v(-122.47, 56.57) * mm});
            skArc(sketch, "E16.1.0.652", {"start": v(-61.24, 7.07) * mm, "mid": v(-53.65, 8.07) * mm, "end": v(-48.99, 14.14) * mm});
            skPoint(sketch, "E16.1.0.653", {"position": v(-146.97, 28.28) * mm});
            skArc(sketch, "E16.1.0.654", {"start": v(-73.22, 69.82) * mm, "mid": v(-75.61, 63.64) * mm, "end": v(-73.22, 57.46) * mm});
            skArc(sketch, "E16.1.0.655", {"start": v(-62.14, 63.86) * mm, "mid": v(-64.35, 60.18) * mm, "end": v(-64.95, 55.92) * mm});
            skLineSegment(sketch, "E16.1.0.656", {"start": v(-159.22, 63.64) * mm, "end": v(-149.56, 66.23) * mm, "construction": true});
            skArc(sketch, "E16.1.0.657", {"start": v(-111.12, 92.14) * mm, "mid": v(-113.96, 84.85) * mm, "end": v(-111.12, 77.56) * mm});
            skArc(sketch, "E16.1.0.658", {"start": v(-74.38, 42.64) * mm, "mid": v(-76.72, 46.43) * mm, "end": v(-80.56, 48.67) * mm});
            skArc(sketch, "E16.1.0.659", {"start": v(-183.71, 106.07) * mm, "mid": v(-185.84, 110.06) * mm, "end": v(-189.52, 112.7) * mm});
            skPoint(sketch, "E16.1.0.660", {"position": v(-147, 42.36) * mm});
            skArc(sketch, "E16.1.0.661", {"start": v(-61.24, 49.5) * mm, "mid": v(-65.9, 55.57) * mm, "end": v(-73.48, 56.57) * mm});
            skPoint(sketch, "E16.1.0.662", {"position": v(-159.25, 21.14) * mm});
            skPoint(sketch, "E16.1.0.663", {"position": v(-24.5, 0) * mm});
            skArc(sketch, "E16.1.0.664", {"start": v(-122.47, 42.43) * mm, "mid": v(-124.6, 46.42) * mm, "end": v(-128.28, 49.07) * mm});
            skLineSegment(sketch, "E16.1.0.665", {"start": v(-110.23, 63.64) * mm, "end": v(-124.63, 59.78) * mm, "construction": true});
            skArc(sketch, "E16.1.0.666", {"start": v(-135.62, 49.72) * mm, "mid": v(-138.45, 42.43) * mm, "end": v(-135.62, 35.14) * mm});
            skArc(sketch, "E16.1.0.667", {"start": v(-48.99, 28.28) * mm, "mid": v(-53.65, 34.36) * mm, "end": v(-61.24, 35.36) * mm});
            skArc(sketch, "E16.1.0.668", {"start": v(-159.22, 49.5) * mm, "mid": v(-163.88, 55.57) * mm, "end": v(-171.46, 56.57) * mm});
            skArc(sketch, "E16.1.0.669", {"start": v(-183.45, 62.75) * mm, "mid": v(-185.56, 58.83) * mm, "end": v(-185.58, 54.39) * mm});
            skArc(sketch, "E16.1.0.670", {"start": v(-85.73, 21.21) * mm, "mid": v(-87.86, 25.2) * mm, "end": v(-91.54, 27.85) * mm});
            skPoint(sketch, "E16.1.0.671", {"position": v(-122.47, 42.43) * mm});
            skArc(sketch, "E16.1.0.672", {"start": v(-134.46, 62.75) * mm, "mid": v(-136.57, 58.83) * mm, "end": v(-136.59, 54.39) * mm});
            skArc(sketch, "E16.1.0.673", {"start": v(-146.97, 0) * mm, "mid": v(-142.44, -0.15) * mm, "end": v(-138.31, 1.7) * mm});
            skPoint(sketch, "E16.1.0.674", {"position": v(-134.72, 49.5) * mm});
            skArc(sketch, "E16.1.0.675", {"start": v(-97.98, 0) * mm, "mid": v(-100.37, -3.84) * mm, "end": v(-100.83, -8.35) * mm});
            skArc(sketch, "E16.1.0.676", {"start": v(-86.63, 63.86) * mm, "mid": v(-88.84, 60.18) * mm, "end": v(-89.44, 55.92) * mm});
            skArc(sketch, "E16.1.0.677", {"start": v(-97.98, 70.71) * mm, "mid": v(-100.9, 63.64) * mm, "end": v(-97.98, 56.57) * mm});
            skArc(sketch, "E16.1.0.678", {"start": v(-97.72, 27.4) * mm, "mid": v(-100.1, 21.21) * mm, "end": v(-97.72, 15.03) * mm});
            skLineSegment(sketch, "E16.1.0.679", {"start": v(-208.2, 106.07) * mm, "end": v(-198.55, 108.65) * mm, "construction": true});
            skArc(sketch, "E16.1.0.680", {"start": v(-97.98, 70.71) * mm, "mid": v(-102.64, 76.78) * mm, "end": v(-110.23, 77.78) * mm});
            skLineSegment(sketch, "E16.1.0.681", {"start": v(-85.73, 63.64) * mm, "end": v(-100.13, 59.78) * mm, "construction": true});
            skArc(sketch, "E16.1.0.682", {"start": v(-98.88, 28.5) * mm, "mid": v(-101.7, 21.21) * mm, "end": v(-98.88, 13.92) * mm});
            skArc(sketch, "E16.1.0.683", {"start": v(-122.21, 83.97) * mm, "mid": v(-117.92, 83.9) * mm, "end": v(-113.94, 85.5) * mm});
            skArc(sketch, "E16.1.0.684", {"start": v(-111.12, 21.43) * mm, "mid": v(-113.47, 25.21) * mm, "end": v(-117.3, 27.46) * mm});
            skArc(sketch, "E16.1.0.685", {"start": v(-209.1, 106.28) * mm, "mid": v(-211.45, 110.07) * mm, "end": v(-215.29, 112.3) * mm});
            skArc(sketch, "E16.1.0.686", {"start": v(-172.36, 113.36) * mm, "mid": v(-175.2, 106.07) * mm, "end": v(-172.36, 98.78) * mm});
            skArc(sketch, "E16.1.0.687", {"start": v(-158.58, 21.88) * mm, "mid": v(-154.13, 22.02) * mm, "end": v(-150.27, 24.22) * mm});
            skArc(sketch, "E16.1.0.688", {"start": v(-97.72, 69.82) * mm, "mid": v(-100.1, 63.64) * mm, "end": v(-97.72, 57.46) * mm});
            skPoint(sketch, "E16.1.0.689", {"position": v(-208.2, 91.92) * mm});
            skArc(sketch, "E16.1.0.690", {"start": v(-123.37, 0.22) * mm, "mid": v(-125.58, -3.46) * mm, "end": v(-126.18, -7.72) * mm});
            skPoint(sketch, "E16.1.0.691", {"position": v(-134.76, 21.14) * mm});
            skArc(sketch, "E16.1.0.692", {"start": v(-158.96, 91.04) * mm, "mid": v(-161.35, 84.85) * mm, "end": v(-158.96, 78.67) * mm});
            skArc(sketch, "E16.1.0.693", {"start": v(-36.48, 6.18) * mm, "mid": v(-38.87, 0) * mm, "end": v(-36.48, -6.18) * mm});
            skArc(sketch, "E16.1.0.694", {"start": v(-122.47, 70.71) * mm, "mid": v(-114.89, 71.7) * mm, "end": v(-110.23, 77.78) * mm});
            skPoint(sketch, "E16.1.0.695", {"position": v(-146.97, 84.85) * mm});
            skArc(sketch, "E16.1.0.696", {"start": v(-110.23, 21.21) * mm, "mid": v(-112.36, 25.2) * mm, "end": v(-116.03, 27.85) * mm});
            skArc(sketch, "E16.1.0.697", {"start": v(-61.24, 7.07) * mm, "mid": v(-65.9, 13.14) * mm, "end": v(-73.48, 14.14) * mm});
            skLineSegment(sketch, "E16.1.0.698", {"start": v(-146.97, 84.85) * mm, "end": v(-161.37, 81) * mm, "construction": true});
            skArc(sketch, "E16.1.0.699", {"start": v(-86.63, 92.14) * mm, "mid": v(-89.46, 84.85) * mm, "end": v(-86.63, 77.56) * mm});
            skArc(sketch, "E16.1.0.700", {"start": v(-98.88, 113.36) * mm, "mid": v(-101.7, 106.07) * mm, "end": v(-98.88, 98.78) * mm});
            skArc(sketch, "E16.1.0.701", {"start": v(-159.22, 49.5) * mm, "mid": v(-151.63, 50.5) * mm, "end": v(-146.97, 56.57) * mm});
            skLineSegment(sketch, "E16.1.0.702", {"start": v(-24.5, 0) * mm, "end": v(-14.84, 2.59) * mm, "construction": true});
            skPoint(sketch, "E16.1.0.703", {"position": v(-61.27, 21.14) * mm});
            skLineSegment(sketch, "E16.1.0.704", {"start": v(-122.47, 42.43) * mm, "end": v(-112.82, 45.01) * mm, "construction": true});
            skArc(sketch, "E16.1.0.705", {"start": v(-159.22, 91.92) * mm, "mid": v(-151.63, 92.92) * mm, "end": v(-146.97, 99) * mm});
            skArc(sketch, "E16.1.0.706", {"start": v(-122.47, 113.14) * mm, "mid": v(-125.4, 106.07) * mm, "end": v(-122.47, 99) * mm});
            skPoint(sketch, "E16.1.0.707", {"position": v(-48.99, 42.43) * mm});
            skLineSegment(sketch, "E16.1.0.708", {"start": v(-24.5, 0) * mm, "end": v(-38.9, -3.86) * mm, "construction": true});
            skArc(sketch, "E16.1.0.709", {"start": v(-171.46, 42.43) * mm, "mid": v(-173.6, 46.42) * mm, "end": v(-177.27, 49.07) * mm});
            skArc(sketch, "E16.1.0.710", {"start": v(-171.46, 84.85) * mm, "mid": v(-173.6, 88.85) * mm, "end": v(-177.27, 91.5) * mm});
            skArc(sketch, "E16.1.0.711", {"start": v(-122.21, 112.25) * mm, "mid": v(-124.6, 106.07) * mm, "end": v(-122.21, 99.88) * mm});
            skArc(sketch, "E16.1.0.712", {"start": v(-97.98, 84.85) * mm, "mid": v(-100.11, 88.85) * mm, "end": v(-103.79, 91.5) * mm});
            skArc(sketch, "E16.1.0.713", {"start": v(-134.72, 49.5) * mm, "mid": v(-127.13, 50.5) * mm, "end": v(-122.47, 56.57) * mm});
            skArc(sketch, "E16.1.0.714", {"start": v(-60.98, 62.75) * mm, "mid": v(-63.08, 58.83) * mm, "end": v(-63.1, 54.39) * mm});
            skArc(sketch, "E16.1.0.715", {"start": v(-146.7, -0.89) * mm, "mid": v(-142.42, -0.96) * mm, "end": v(-138.43, 0.65) * mm});
            skArc(sketch, "E16.1.0.716", {"start": v(-171.2, 112.25) * mm, "mid": v(-173.6, 106.07) * mm, "end": v(-171.2, 99.88) * mm});
            skLineSegment(sketch, "E16.1.0.717", {"start": v(-73.48, 0) * mm, "end": v(-87.89, -3.86) * mm, "construction": true});
            skArc(sketch, "E16.1.0.718", {"start": v(-85.73, 106.07) * mm, "mid": v(-87.86, 110.06) * mm, "end": v(-91.54, 112.7) * mm});
            skLineSegment(sketch, "E16.1.0.719", {"start": v(-110.23, 63.64) * mm, "end": v(-100.57, 66.23) * mm, "construction": true});
            skPoint(sketch, "E16.1.0.720", {"position": v(-122.47, 28.28) * mm});
            skArc(sketch, "E16.1.0.721", {"start": v(-85.73, 63.64) * mm, "mid": v(-88.13, 59.8) * mm, "end": v(-88.58, 55.29) * mm});
            skArc(sketch, "E16.1.0.722", {"start": v(-62.14, 7.29) * mm, "mid": v(-64.97, 0) * mm, "end": v(-62.14, -7.29) * mm});
            skArc(sketch, "E16.1.0.723", {"start": v(-147.87, 113.36) * mm, "mid": v(-150.7, 106.07) * mm, "end": v(-147.87, 98.78) * mm});
            skArc(sketch, "E16.1.0.724", {"start": v(-109.97, 62.75) * mm, "mid": v(-112.07, 58.83) * mm, "end": v(-112.1, 54.39) * mm});
            skArc(sketch, "E16.1.0.725", {"start": v(-160.11, 21.43) * mm, "mid": v(-162.46, 25.21) * mm, "end": v(-166.3, 27.46) * mm});
            skLineSegment(sketch, "E16.1.0.726", {"start": v(-146.97, 42.43) * mm, "end": v(-161.37, 38.57) * mm, "construction": true});
            skArc(sketch, "E16.1.0.727", {"start": v(-36.74, 7.07) * mm, "mid": v(-39.67, 0) * mm, "end": v(-36.74, -7.07) * mm});
            skLineSegment(sketch, "E16.1.0.728", {"start": v(-122.47, 84.85) * mm, "end": v(-136.88, 81) * mm, "construction": true});
            skPoint(sketch, "E16.1.0.729", {"position": v(-110.26, 21.14) * mm});
            skLineSegment(sketch, "E16.1.0.730", {"start": v(-159.22, 63.64) * mm, "end": v(-173.62, 59.78) * mm, "construction": true});
            skArc(sketch, "E16.1.0.731", {"start": v(-160.11, 63.86) * mm, "mid": v(-162.33, 60.18) * mm, "end": v(-162.93, 55.92) * mm});
            skArc(sketch, "E16.1.0.732", {"start": v(-135.62, 106.28) * mm, "mid": v(-137.96, 110.07) * mm, "end": v(-141.8, 112.3) * mm});
            skArc(sketch, "E16.1.0.733", {"start": v(-97.98, 42.43) * mm, "mid": v(-100.11, 46.42) * mm, "end": v(-103.79, 49.07) * mm});
            skArc(sketch, "E16.1.0.734", {"start": v(-48.99, 28.28) * mm, "mid": v(-51.92, 21.21) * mm, "end": v(-48.99, 14.14) * mm});
            skArc(sketch, "E16.1.0.735", {"start": v(-158.96, 20.33) * mm, "mid": v(-154.66, 20.25) * mm, "end": v(-150.68, 21.86) * mm});
            skArc(sketch, "E16.1.0.736", {"start": v(-122.21, 69.82) * mm, "mid": v(-124.6, 63.64) * mm, "end": v(-122.21, 57.46) * mm});
            skPoint(sketch, "E16.1.0.737", {"position": v(-48.99, 0) * mm});
            skArc(sketch, "E16.1.0.738", {"start": v(-85.73, 49.5) * mm, "mid": v(-78.14, 50.5) * mm, "end": v(-73.48, 56.57) * mm});
            skLineSegment(sketch, "E16.1.0.739", {"start": v(-159.22, 106.07) * mm, "end": v(-149.56, 108.65) * mm, "construction": true});
            skArc(sketch, "E16.1.0.740", {"start": v(-97.72, 83.97) * mm, "mid": v(-93.43, 83.9) * mm, "end": v(-89.44, 85.5) * mm});
            skArc(sketch, "E16.1.0.741", {"start": v(-98.88, 85.07) * mm, "mid": v(-101.22, 88.85) * mm, "end": v(-105.06, 91.1) * mm});
            skArc(sketch, "E16.1.0.742", {"start": v(-110.23, 7.07) * mm, "mid": v(-102.64, 8.07) * mm, "end": v(-97.98, 14.14) * mm});
            skArc(sketch, "E16.1.0.743", {"start": v(-97.98, 28.28) * mm, "mid": v(-90.4, 29.28) * mm, "end": v(-85.73, 35.36) * mm});
            skPoint(sketch, "E16.1.0.744", {"position": v(-85.73, 7.07) * mm});
            skArc(sketch, "E16.1.0.745", {"start": v(-195.96, 70.71) * mm, "mid": v(-188.37, 71.7) * mm, "end": v(-183.71, 77.78) * mm});
            skLineSegment(sketch, "E16.1.0.746", {"start": v(-97.98, 84.85) * mm, "end": v(-112.38, 81) * mm, "construction": true});
            skArc(sketch, "E16.1.0.747", {"start": v(-158.96, 62.75) * mm, "mid": v(-161.06, 58.83) * mm, "end": v(-161.08, 54.39) * mm});
            skPoint(sketch, "E16.1.0.748", {"position": v(-73.52, 42.36) * mm});
            skArc(sketch, "E16.1.0.749", {"start": v(-121.84, 85.52) * mm, "mid": v(-117.4, 85.66) * mm, "end": v(-113.53, 87.86) * mm});
            skArc(sketch, "E16.1.0.750", {"start": v(-134.72, 49.5) * mm, "mid": v(-137.65, 42.43) * mm, "end": v(-134.72, 35.36) * mm});
            skArc(sketch, "E16.1.0.751", {"start": v(-97.72, 112.25) * mm, "mid": v(-100.1, 106.07) * mm, "end": v(-97.72, 99.88) * mm});
            skArc(sketch, "E16.1.0.752", {"start": v(-110.23, 106.07) * mm, "mid": v(-112.36, 110.06) * mm, "end": v(-116.03, 112.7) * mm});
            skArc(sketch, "E16.1.0.753", {"start": v(-134.72, 7.07) * mm, "mid": v(-127.13, 8.07) * mm, "end": v(-122.47, 14.14) * mm});
            skLineSegment(sketch, "E16.1.0.754", {"start": v(-73.48, 84.85) * mm, "end": v(-87.89, 81) * mm, "construction": true});
            skPoint(sketch, "E16.1.0.755", {"position": v(-98.02, 84.78) * mm});
            skArc(sketch, "E16.1.0.756", {"start": v(-158.58, 7.74) * mm, "mid": v(-152.03, 8.76) * mm, "end": v(-147.87, 13.92) * mm});
            skArc(sketch, "E16.1.0.757", {"start": v(-158.96, 6.18) * mm, "mid": v(-161.35, 0) * mm, "end": v(-158.96, -6.18) * mm});
            skPoint(sketch, "E16.1.0.758", {"position": v(-159.22, 49.5) * mm});
            skPoint(sketch, "E16.1.0.759", {"position": v(-134.72, 106.07) * mm});
            skArc(sketch, "E16.1.0.760", {"start": v(-49.89, 0.22) * mm, "mid": v(-52.23, 4) * mm, "end": v(-56.07, 6.24) * mm});
            skPoint(sketch, "E16.1.0.761", {"position": v(-97.98, 70.71) * mm});
            skArc(sketch, "E16.1.0.762", {"start": v(-134.72, 63.64) * mm, "mid": v(-137.12, 59.8) * mm, "end": v(-137.57, 55.29) * mm});
            skArc(sketch, "E16.1.0.763", {"start": v(-159.22, 7.07) * mm, "mid": v(-162.15, 0) * mm, "end": v(-159.22, -7.07) * mm});
            skLineSegment(sketch, "E16.1.0.764", {"start": v(-171.46, 84.85) * mm, "end": v(-185.87, 81) * mm, "construction": true});
            skArc(sketch, "E16.1.0.765", {"start": v(-159.22, 21.21) * mm, "mid": v(-154.7, 21.06) * mm, "end": v(-150.56, 22.92) * mm});
            skLineSegment(sketch, "E16.1.0.766", {"start": v(-134.72, 63.64) * mm, "end": v(-125.06, 66.23) * mm, "construction": true});
            skArc(sketch, "E16.1.0.767", {"start": v(-146.97, 70.71) * mm, "mid": v(-149.9, 63.64) * mm, "end": v(-146.97, 56.57) * mm});
            skArc(sketch, "E16.1.0.768", {"start": v(-61.24, 21.21) * mm, "mid": v(-63.37, 25.2) * mm, "end": v(-67.05, 27.85) * mm});
            skArc(sketch, "E16.1.0.769", {"start": v(-135.62, 7.29) * mm, "mid": v(-138.45, 0) * mm, "end": v(-135.62, -7.29) * mm});
            skArc(sketch, "E16.1.0.770", {"start": v(-183.71, 91.92) * mm, "mid": v(-176.12, 92.92) * mm, "end": v(-171.46, 99) * mm});
            skArc(sketch, "E16.1.0.771", {"start": v(-146.33, 0.67) * mm, "mid": v(-148.41, 4.42) * mm, "end": v(-151.8, 7.07) * mm});
            skPoint(sketch, "E16.1.0.772", {"position": v(-171.46, 42.43) * mm});
            skArc(sketch, "E16.1.0.773", {"start": v(-37.64, 21.43) * mm, "mid": v(-39.98, 25.21) * mm, "end": v(-43.82, 27.46) * mm});
            skPoint(sketch, "E16.1.0.774", {"position": v(-146.97, 70.71) * mm});
            skArc(sketch, "E16.1.0.775", {"start": v(-110.23, 91.92) * mm, "mid": v(-113.16, 84.85) * mm, "end": v(-110.23, 77.78) * mm});
            skArc(sketch, "E16.1.0.776", {"start": v(-61.24, 7.07) * mm, "mid": v(-64.17, 0) * mm, "end": v(-61.24, -7.07) * mm});
            skArc(sketch, "E16.1.0.777", {"start": v(-146.97, 113.14) * mm, "mid": v(-149.9, 106.07) * mm, "end": v(-146.97, 99) * mm});
            skLineSegment(sketch, "E16.1.0.778", {"start": v(-73.48, 42.43) * mm, "end": v(-87.89, 38.57) * mm, "construction": true});
            skArc(sketch, "E16.1.0.779", {"start": v(-122.47, 28.28) * mm, "mid": v(-127.13, 34.36) * mm, "end": v(-134.72, 35.36) * mm});
            skPoint(sketch, "E16.1.0.780", {"position": v(-97.98, 0) * mm});
            skArc(sketch, "E16.1.0.781", {"start": v(-122.47, 28.28) * mm, "mid": v(-114.89, 29.28) * mm, "end": v(-110.23, 35.36) * mm});
            skArc(sketch, "E16.1.0.782", {"start": v(-25.4, 0.22) * mm, "mid": v(-27.73, 4) * mm, "end": v(-31.57, 6.24) * mm});
            skArc(sketch, "E16.1.0.783", {"start": v(-61.24, 63.64) * mm, "mid": v(-63.63, 59.8) * mm, "end": v(-64.08, 55.29) * mm});
            skArc(sketch, "E16.1.0.784", {"start": v(-85.47, 6.18) * mm, "mid": v(-87.86, 0) * mm, "end": v(-85.47, -6.18) * mm});
            skArc(sketch, "E16.1.0.785", {"start": v(-121.84, 0.67) * mm, "mid": v(-123.92, 4.42) * mm, "end": v(-127.3, 7.07) * mm});
            skPoint(sketch, "E16.1.0.786", {"position": v(-122.47, 84.85) * mm});
            skArc(sketch, "E16.1.0.787", {"start": v(-123.37, 70.93) * mm, "mid": v(-126.2, 63.64) * mm, "end": v(-123.37, 56.35) * mm});
            skArc(sketch, "E16.1.0.788", {"start": v(-73.48, 28.28) * mm, "mid": v(-65.9, 29.28) * mm, "end": v(-61.24, 35.36) * mm});
            skArc(sketch, "E16.1.0.789", {"start": v(-36.74, 7.07) * mm, "mid": v(-41.4, 13.14) * mm, "end": v(-48.99, 14.14) * mm});
            skArc(sketch, "E16.1.0.790", {"start": v(-159.22, 49.5) * mm, "mid": v(-162.15, 42.43) * mm, "end": v(-159.22, 35.36) * mm});
            skLineSegment(sketch, "E16.1.0.791", {"start": v(-171.46, 42.43) * mm, "end": v(-161.8, 45.01) * mm, "construction": true});
            skArc(sketch, "E16.1.0.792", {"start": v(-159.22, 21.21) * mm, "mid": v(-161.35, 25.2) * mm, "end": v(-165.02, 27.85) * mm});
            skArc(sketch, "E16.1.0.793", {"start": v(-134.08, 7.74) * mm, "mid": v(-138.98, 13.84) * mm, "end": v(-146.7, 15.03) * mm});
            skArc(sketch, "E16.1.0.794", {"start": v(-122.47, 0) * mm, "mid": v(-124.6, 4) * mm, "end": v(-128.28, 6.64) * mm});
            skArc(sketch, "E16.1.0.795", {"start": v(-183.45, 91.04) * mm, "mid": v(-185.84, 84.85) * mm, "end": v(-183.45, 78.67) * mm});
            skArc(sketch, "E16.1.0.796", {"start": v(-123.37, 0.22) * mm, "mid": v(-125.71, 4) * mm, "end": v(-129.55, 6.24) * mm});
            skArc(sketch, "E16.1.0.797", {"start": v(-110.23, 49.5) * mm, "mid": v(-113.16, 42.43) * mm, "end": v(-110.23, 35.36) * mm});
            skArc(sketch, "E16.1.0.798", {"start": v(-134.72, 91.92) * mm, "mid": v(-139.38, 98) * mm, "end": v(-146.97, 99) * mm});
            skArc(sketch, "E16.1.0.799", {"start": v(-134.72, 91.92) * mm, "mid": v(-137.65, 84.85) * mm, "end": v(-134.72, 77.78) * mm});
            skPoint(sketch, "E16.1.0.800", {"position": v(-85.73, 63.64) * mm});
            skArc(sketch, "E16.1.0.801", {"start": v(-73.48, 84.85) * mm, "mid": v(-75.88, 81) * mm, "end": v(-76.33, 76.5) * mm});
            skArc(sketch, "E16.1.0.802", {"start": v(-85.73, 7.07) * mm, "mid": v(-78.14, 8.07) * mm, "end": v(-73.48, 14.14) * mm});
            skLineSegment(sketch, "E16.1.0.803", {"start": v(-85.73, 106.07) * mm, "end": v(-76.07, 108.65) * mm, "construction": true});
            skLineSegment(sketch, "E16.1.0.804", {"start": v(-195.96, 84.85) * mm, "end": v(-210.36, 81) * mm, "construction": true});
            skLineSegment(sketch, "E16.1.0.805", {"start": v(-134.72, 106.07) * mm, "end": v(-125.06, 108.65) * mm, "construction": true});
            skArc(sketch, "E16.1.0.806", {"start": v(-85.73, 7.07) * mm, "mid": v(-88.66, 0) * mm, "end": v(-85.73, -7.07) * mm});
            skArc(sketch, "E16.1.0.807", {"start": v(-146.97, 42.43) * mm, "mid": v(-149.1, 46.42) * mm, "end": v(-152.78, 49.07) * mm});
            skLineSegment(sketch, "E16.1.0.808", {"start": v(-168.88, 4.48) * mm, "end": v(-144.38, 4.48) * mm, "construction": true});
            skArc(sketch, "E16.1.0.809", {"start": v(-109.97, 6.18) * mm, "mid": v(-112.36, 0) * mm, "end": v(-109.97, -6.18) * mm});
            skArc(sketch, "E16.1.0.810", {"start": v(-134.72, 7.07) * mm, "mid": v(-139.38, 13.14) * mm, "end": v(-146.97, 14.14) * mm});
            skLineSegment(sketch, "E16.1.0.811", {"start": v(-48.99, 0) * mm, "end": v(-63.4, -3.86) * mm, "construction": true});
            skArc(sketch, "E16.1.0.812", {"start": v(-146.7, 27.4) * mm, "mid": v(-149.1, 21.21) * mm, "end": v(-146.7, 15.03) * mm});
            skArc(sketch, "E16.1.0.813", {"start": v(-73.48, 42.43) * mm, "mid": v(-75.88, 38.58) * mm, "end": v(-76.33, 34.08) * mm});
            skArc(sketch, "E16.1.0.814", {"start": v(-171.2, 69.82) * mm, "mid": v(-173.6, 63.64) * mm, "end": v(-171.2, 57.46) * mm});
            skArc(sketch, "E16.1.0.815", {"start": v(-135.62, 63.86) * mm, "mid": v(-137.83, 60.18) * mm, "end": v(-138.43, 55.92) * mm});
            skArc(sketch, "E16.1.0.816", {"start": v(-73.48, 28.28) * mm, "mid": v(-76.41, 21.21) * mm, "end": v(-73.48, 14.14) * mm});
            skArc(sketch, "E16.1.0.817", {"start": v(-135.62, 7.29) * mm, "mid": v(-139.78, 12.45) * mm, "end": v(-146.33, 13.47) * mm});
            skPoint(sketch, "E16.1.0.818", {"position": v(-73.48, 0) * mm});
            skArc(sketch, "E16.1.0.819", {"start": v(-134.46, 48.61) * mm, "mid": v(-136.85, 42.43) * mm, "end": v(-134.46, 36.24) * mm});
            skLineSegment(sketch, "E16.1.0.820", {"start": v(-97.98, 0) * mm, "end": v(-112.38, -3.86) * mm, "construction": true});
            skArc(sketch, "E16.1.0.821", {"start": v(-85.47, 48.61) * mm, "mid": v(-87.86, 42.43) * mm, "end": v(-85.47, 36.24) * mm});
            skPoint(sketch, "E16.1.0.822", {"position": v(-147, -0.07) * mm});
            skArc(sketch, "E16.1.0.823", {"start": v(-110.23, 91.92) * mm, "mid": v(-114.89, 98) * mm, "end": v(-122.47, 99) * mm});
            skArc(sketch, "E16.1.0.824", {"start": v(-36.74, 7.07) * mm, "mid": v(-29.15, 8.07) * mm, "end": v(-24.5, 14.14) * mm});
            skPoint(sketch, "E16.1.0.825", {"position": v(-134.72, 63.64) * mm});
            skArc(sketch, "E16.1.0.826", {"start": v(-134.72, 106.07) * mm, "mid": v(-136.85, 110.06) * mm, "end": v(-140.53, 112.7) * mm});
            skArc(sketch, "E16.1.0.827", {"start": v(-60.98, 48.61) * mm, "mid": v(-63.37, 42.43) * mm, "end": v(-60.98, 36.24) * mm});
            skPoint(sketch, "E16.1.0.828", {"position": v(-48.99, 28.28) * mm});
            skPoint(sketch, "E16.1.0.829", {"position": v(-110.23, 91.92) * mm});
            skArc(sketch, "E16.1.0.830", {"start": v(-170.83, 43.1) * mm, "mid": v(-172.9, 46.85) * mm, "end": v(-176.3, 49.5) * mm});
            skArc(sketch, "E16.1.0.831", {"start": v(-85.47, 91.04) * mm, "mid": v(-87.86, 84.85) * mm, "end": v(-85.47, 78.67) * mm});
            skArc(sketch, "E16.1.0.832", {"start": v(-122.21, 27.4) * mm, "mid": v(-124.6, 21.21) * mm, "end": v(-122.21, 15.03) * mm});
            skArc(sketch, "E16.1.0.833", {"start": v(-159.22, 91.92) * mm, "mid": v(-163.88, 98) * mm, "end": v(-171.46, 99) * mm});
            skLineSegment(sketch, "E16.1.0.834", {"start": v(-73.48, 42.43) * mm, "end": v(-63.83, 45.01) * mm, "construction": true});
            skPoint(sketch, "E16.1.0.835", {"position": v(-61.24, 7.07) * mm});
            skArc(sketch, "E16.1.0.836", {"start": v(-146.33, 0.67) * mm, "mid": v(-141.89, 0.8) * mm, "end": v(-138.02, 3.01) * mm});
            skArc(sketch, "E16.1.0.837", {"start": v(-74.38, 85.07) * mm, "mid": v(-76.72, 88.85) * mm, "end": v(-80.56, 91.1) * mm});
            skArc(sketch, "E16.1.0.838", {"start": v(-122.47, 84.85) * mm, "mid": v(-124.6, 88.85) * mm, "end": v(-128.28, 91.5) * mm});
            skArc(sketch, "E16.1.0.839", {"start": v(-122.47, 0) * mm, "mid": v(-124.87, -3.84) * mm, "end": v(-125.32, -8.35) * mm});
            skArc(sketch, "E16.1.0.840", {"start": v(-122.47, 28.28) * mm, "mid": v(-125.4, 21.21) * mm, "end": v(-122.47, 14.14) * mm});
            skPoint(sketch, "E16.1.0.841", {"position": v(-36.74, 21.21) * mm});
            skLineSegment(sketch, "E16.1.0.842", {"start": v(-85.73, 63.64) * mm, "end": v(-76.07, 66.23) * mm, "construction": true});
            skLineSegment(sketch, "E16.1.0.843", {"start": v(-97.98, 0) * mm, "end": v(-88.32, 2.59) * mm, "construction": true});
            skPoint(sketch, "E16.1.0.844", {"position": v(-110.23, 7.07) * mm});
            skArc(sketch, "E16.1.0.845", {"start": v(-48.73, 27.4) * mm, "mid": v(-51.12, 21.21) * mm, "end": v(-48.73, 15.03) * mm});
            skArc(sketch, "E16.1.0.846", {"start": v(-123.37, 113.36) * mm, "mid": v(-126.2, 106.07) * mm, "end": v(-123.37, 98.78) * mm});
            skLineSegment(sketch, "E16.1.0.847", {"start": v(-183.71, 106.07) * mm, "end": v(-174.05, 108.65) * mm, "construction": true});
            skArc(sketch, "E16.1.0.848", {"start": v(-183.71, 91.92) * mm, "mid": v(-188.37, 98) * mm, "end": v(-195.96, 99) * mm});
            skArc(sketch, "E16.1.0.849", {"start": v(-74.38, 70.93) * mm, "mid": v(-77.21, 63.64) * mm, "end": v(-74.38, 56.35) * mm});
            skArc(sketch, "E16.1.0.850", {"start": v(-159.22, 63.64) * mm, "mid": v(-161.61, 59.8) * mm, "end": v(-162.06, 55.29) * mm});
            skArc(sketch, "E16.1.0.851", {"start": v(-73.48, 70.71) * mm, "mid": v(-65.9, 71.7) * mm, "end": v(-61.24, 77.78) * mm});
            skLineSegment(sketch, "E16.1.0.852", {"start": v(-183.71, 63.64) * mm, "end": v(-174.05, 66.23) * mm, "construction": true});
            skArc(sketch, "E16.1.0.853", {"start": v(-146.7, 112.25) * mm, "mid": v(-149.1, 106.07) * mm, "end": v(-146.7, 99.88) * mm});
            skArc(sketch, "E16.1.0.854", {"start": v(-184.6, 106.28) * mm, "mid": v(-186.95, 110.07) * mm, "end": v(-190.8, 112.3) * mm});
            skLineSegment(sketch, "E16.1.0.855", {"start": v(-97.98, 42.43) * mm, "end": v(-112.38, 38.57) * mm, "construction": true});
            skArc(sketch, "E16.1.0.856", {"start": v(-85.73, 49.5) * mm, "mid": v(-88.66, 42.43) * mm, "end": v(-85.73, 35.36) * mm});
            skArc(sketch, "E16.1.0.857", {"start": v(-147.87, 28.5) * mm, "mid": v(-150.7, 21.21) * mm, "end": v(-147.87, 13.92) * mm});
            skArc(sketch, "E16.1.0.858", {"start": v(-98.88, 0.22) * mm, "mid": v(-101.22, 4) * mm, "end": v(-105.06, 6.24) * mm});
            skArc(sketch, "E16.1.0.859", {"start": v(-86.63, 7.29) * mm, "mid": v(-89.46, 0) * mm, "end": v(-86.63, -7.29) * mm});
            skArc(sketch, "E16.1.0.860", {"start": v(-48.99, 0) * mm, "mid": v(-51.38, -3.84) * mm, "end": v(-51.84, -8.35) * mm});
            skArc(sketch, "E16.1.0.861", {"start": v(-146.97, 28.28) * mm, "mid": v(-151.63, 34.36) * mm, "end": v(-159.22, 35.36) * mm});
            skPoint(sketch, "E16.1.0.862", {"position": v(-36.74, 7.07) * mm});
            skPoint(sketch, "E16.1.0.863", {"position": v(-195.96, 70.71) * mm});
            skLineSegment(sketch, "E16.1.0.864", {"start": v(-171.46, 42.43) * mm, "end": v(-185.87, 38.57) * mm, "construction": true});
            skPoint(sketch, "E16.1.0.865", {"position": v(-73.48, 84.85) * mm});
            skPoint(sketch, "E16.1.0.866", {"position": v(-73.48, 70.71) * mm});
            skPoint(sketch, "E16.1.0.867", {"position": v(-61.24, 63.64) * mm});
            skArc(sketch, "E16.1.0.868", {"start": v(-184.6, 92.14) * mm, "mid": v(-187.44, 84.85) * mm, "end": v(-184.6, 77.56) * mm});
            skArc(sketch, "E16.1.0.869", {"start": v(-172.36, 42.64) * mm, "mid": v(-174.7, 46.43) * mm, "end": v(-178.54, 48.67) * mm});
            skArc(sketch, "E16.1.0.870", {"start": v(-36.74, 21.21) * mm, "mid": v(-38.87, 25.2) * mm, "end": v(-42.55, 27.85) * mm});
            skPoint(sketch, "E16.1.0.871", {"position": v(-110.23, 49.5) * mm});
            skArc(sketch, "E16.1.0.872", {"start": v(-61.24, 49.5) * mm, "mid": v(-53.65, 50.5) * mm, "end": v(-48.99, 56.57) * mm});
            skArc(sketch, "E16.1.0.873", {"start": v(-195.7, 112.25) * mm, "mid": v(-198.09, 106.07) * mm, "end": v(-195.7, 99.88) * mm});
            skArc(sketch, "E16.1.0.874", {"start": v(-146.97, 28.28) * mm, "mid": v(-139.38, 29.28) * mm, "end": v(-134.72, 35.36) * mm});
            skArc(sketch, "E16.1.0.875", {"start": v(-183.71, 91.92) * mm, "mid": v(-186.64, 84.85) * mm, "end": v(-183.71, 77.78) * mm});
            skLineSegment(sketch, "E16.1.0.876", {"start": v(-73.48, 0) * mm, "end": v(-63.83, 2.59) * mm, "construction": true});
            skArc(sketch, "E16.1.0.877", {"start": v(-97.98, 42.43) * mm, "mid": v(-100.37, 38.58) * mm, "end": v(-100.83, 34.08) * mm});
            skArc(sketch, "E16.1.0.878", {"start": v(-85.73, 91.92) * mm, "mid": v(-90.4, 98) * mm, "end": v(-97.98, 99) * mm});
            skPoint(sketch, "E16.1.0.879", {"position": v(-61.24, 49.5) * mm});
            skLineSegment(sketch, "E16.1.0.880", {"start": v(-48.99, 42.43) * mm, "end": v(-63.4, 38.57) * mm, "construction": true});
            skArc(sketch, "E16.1.0.881", {"start": v(-111.12, 49.72) * mm, "mid": v(-113.96, 42.43) * mm, "end": v(-111.12, 35.14) * mm});
            skArc(sketch, "E16.1.0.882", {"start": v(-85.73, 91.92) * mm, "mid": v(-88.66, 84.85) * mm, "end": v(-85.73, 77.78) * mm});
            skArc(sketch, "E16.1.0.883", {"start": v(-195.96, 113.14) * mm, "mid": v(-198.89, 106.07) * mm, "end": v(-195.96, 99) * mm});
            skArc(sketch, "E16.1.0.884", {"start": v(-73.48, 42.43) * mm, "mid": v(-75.62, 46.42) * mm, "end": v(-79.3, 49.07) * mm});
            skArc(sketch, "E16.1.0.885", {"start": v(-171.46, 42.43) * mm, "mid": v(-173.86, 38.58) * mm, "end": v(-174.31, 34.08) * mm});
            skArc(sketch, "E16.1.0.886", {"start": v(-146.97, 70.71) * mm, "mid": v(-151.63, 76.78) * mm, "end": v(-159.22, 77.78) * mm});
            skPoint(sketch, "E16.1.0.887", {"position": v(-171.46, 84.85) * mm});
            skArc(sketch, "E16.1.0.888", {"start": v(-110.23, 91.92) * mm, "mid": v(-102.64, 92.92) * mm, "end": v(-97.98, 99) * mm});
            skArc(sketch, "E16.1.0.889", {"start": v(-123.37, 28.5) * mm, "mid": v(-126.2, 21.21) * mm, "end": v(-123.37, 13.92) * mm});
            skLineSegment(sketch, "E16.1.0.890", {"start": v(-134.72, 63.64) * mm, "end": v(-149.12, 59.78) * mm, "construction": true});
            skLineSegment(sketch, "E16.1.0.891", {"start": v(-122.47, 0) * mm, "end": v(-112.82, 2.59) * mm, "construction": true});
            skPoint(sketch, "E16.1.0.892", {"position": v(-85.73, 49.5) * mm});
            skArc(sketch, "E16.1.0.893", {"start": v(-171.46, 28.28) * mm, "mid": v(-163.88, 29.28) * mm, "end": v(-159.22, 35.36) * mm});
            skArc(sketch, "E16.1.0.894", {"start": v(-110.23, 63.64) * mm, "mid": v(-112.62, 59.8) * mm, "end": v(-113.07, 55.29) * mm});
            skArc(sketch, "E16.1.0.895", {"start": v(-98.88, 70.93) * mm, "mid": v(-101.7, 63.64) * mm, "end": v(-98.88, 56.35) * mm});
            skLineSegment(sketch, "E16.1.0.896", {"start": v(-156.63, -16.73) * mm, "end": v(-132.13, -16.73) * mm, "construction": true});
            skArc(sketch, "E16.1.0.897", {"start": v(-73.48, 28.28) * mm, "mid": v(-78.14, 34.36) * mm, "end": v(-85.73, 35.36) * mm});
            skPoint(sketch, "E16.1.0.898", {"position": v(-122.47, 0) * mm});
            skArc(sketch, "E16.1.0.899", {"start": v(-171.46, 70.71) * mm, "mid": v(-176.12, 76.78) * mm, "end": v(-183.71, 77.78) * mm});
            skPoint(sketch, "E16.1.0.900", {"position": v(-98.02, 42.36) * mm});
            skArc(sketch, "E16.1.0.901", {"start": v(-74.38, 28.5) * mm, "mid": v(-77.21, 21.21) * mm, "end": v(-74.38, 13.92) * mm});
            skArc(sketch, "E16.1.0.902", {"start": v(-97.34, 85.52) * mm, "mid": v(-92.9, 85.66) * mm, "end": v(-89.03, 87.86) * mm});
            skArc(sketch, "E16.1.0.903", {"start": v(-85.47, 62.75) * mm, "mid": v(-87.58, 58.83) * mm, "end": v(-87.6, 54.39) * mm});
            skLineSegment(sketch, "E16.1.0.904", {"start": v(-97.98, 42.43) * mm, "end": v(-88.32, 45.01) * mm, "construction": true});
            skPoint(sketch, "E16.1.0.905", {"position": v(-159.22, 7.07) * mm});
            skArc(sketch, "E16.1.0.906", {"start": v(-60.98, 6.18) * mm, "mid": v(-63.37, 0) * mm, "end": v(-60.98, -6.18) * mm});
            skArc(sketch, "E16.1.0.907", {"start": v(-146.97, 28.28) * mm, "mid": v(-149.9, 21.21) * mm, "end": v(-146.97, 14.14) * mm});
            skPoint(sketch, "E16.1.0.908", {"position": v(-134.72, 7.07) * mm});
            skArc(sketch, "E16.1.0.909", {"start": v(-97.98, 28.28) * mm, "mid": v(-102.64, 34.36) * mm, "end": v(-110.23, 35.36) * mm});
            skArc(sketch, "E16.1.0.910", {"start": v(-37.64, 7.29) * mm, "mid": v(-40.47, 0) * mm, "end": v(-37.64, -7.29) * mm});
            skArc(sketch, "E16.1.0.911", {"start": v(-86.63, 49.72) * mm, "mid": v(-89.46, 42.43) * mm, "end": v(-86.63, 35.14) * mm});
            skArc(sketch, "E16.1.0.912", {"start": v(-73.48, 70.71) * mm, "mid": v(-76.41, 63.64) * mm, "end": v(-73.48, 56.57) * mm});
            skLineSegment(sketch, "E16.1.0.913", {"start": v(-146.97, 0) * mm, "end": v(-161.37, -3.86) * mm, "construction": true});
            skPoint(sketch, "E16.1.0.914", {"position": v(-85.73, 21.21) * mm});
            skPoint(sketch, "E16.1.0.915", {"position": v(-134.72, 21.21) * mm});
            skPoint(sketch, "E16.1.0.916", {"position": v(-208.2, 106.07) * mm});
            skPoint(sketch, "E16.1.0.917", {"position": v(-134.76, 106) * mm});
            skArc(sketch, "E16.1.0.918", {"start": v(-122.47, 70.71) * mm, "mid": v(-125.4, 63.64) * mm, "end": v(-122.47, 56.57) * mm});
            skArc(sketch, "E16.1.0.919", {"start": v(-134.72, 7.07) * mm, "mid": v(-127.13, 8.07) * mm, "end": v(-122.47, 14.14) * mm});
            skLineSegment(sketch, "E16.1.0.920", {"start": v(-110.23, 21.21) * mm, "end": v(-124.63, 17.35) * mm, "construction": true});
            skArc(sketch, "E16.1.0.921", {"start": v(-85.73, 91.92) * mm, "mid": v(-88.66, 84.85) * mm, "end": v(-85.73, 77.78) * mm});
            skPoint(sketch, "E16.1.0.922", {"position": v(-73.48, 0) * mm});
            skPoint(sketch, "E16.1.0.923", {"position": v(-110.23, 106.07) * mm});
            skArc(sketch, "E16.1.0.924", {"start": v(-110.23, 91.92) * mm, "mid": v(-113.16, 84.85) * mm, "end": v(-110.23, 77.78) * mm});
            skArc(sketch, "E16.1.0.925", {"start": v(-134.72, 7.07) * mm, "mid": v(-139.38, 13.14) * mm, "end": v(-146.97, 14.14) * mm});
            skPoint(sketch, "E16.1.0.926", {"position": v(-134.76, 63.57) * mm});
            skPoint(sketch, "E16.1.0.927", {"position": v(-61.24, 21.21) * mm});
            skArc(sketch, "E16.1.0.928", {"start": v(-147.87, 0.22) * mm, "mid": v(-150.2, 4) * mm, "end": v(-154.05, 6.24) * mm});
            skArc(sketch, "E16.1.0.929", {"start": v(-196.86, 85.07) * mm, "mid": v(-199.2, 88.85) * mm, "end": v(-203.04, 91.1) * mm});
            skPoint(sketch, "E16.1.0.930", {"position": v(-97.98, 42.43) * mm});
            skPoint(sketch, "E16.1.0.931", {"position": v(-73.48, 84.85) * mm});
            skLineSegment(sketch, "E16.1.0.932", {"start": v(-85.73, 106.07) * mm, "end": v(-100.13, 102.2) * mm, "construction": true});
            skArc(sketch, "E16.1.0.933", {"start": v(-122.47, 28.28) * mm, "mid": v(-125.4, 21.21) * mm, "end": v(-122.47, 14.14) * mm});
            skArc(sketch, "E16.1.0.934", {"start": v(-134.72, 7.07) * mm, "mid": v(-137.65, 0) * mm, "end": v(-134.72, -7.07) * mm});
            skArc(sketch, "E16.1.0.935", {"start": v(-183.71, 63.64) * mm, "mid": v(-186.1, 59.8) * mm, "end": v(-186.56, 55.29) * mm});
            skPoint(sketch, "E16.1.0.936", {"position": v(-48.99, 0) * mm});
            skArc(sketch, "E16.1.0.937", {"start": v(-73.48, 28.28) * mm, "mid": v(-76.41, 21.21) * mm, "end": v(-73.48, 14.14) * mm});
            skArc(sketch, "E16.1.0.938", {"start": v(-85.73, 7.07) * mm, "mid": v(-78.14, 8.07) * mm, "end": v(-73.48, 14.14) * mm});
            skArc(sketch, "E16.1.0.939", {"start": v(-183.71, 91.92) * mm, "mid": v(-186.64, 84.85) * mm, "end": v(-183.71, 77.78) * mm});
            skLineSegment(sketch, "E16.1.0.940", {"start": v(-159.22, 21.21) * mm, "end": v(-173.62, 17.35) * mm, "construction": true});
            skArc(sketch, "E16.1.0.941", {"start": v(-48.99, 28.28) * mm, "mid": v(-51.92, 21.21) * mm, "end": v(-48.99, 14.14) * mm});
            skArc(sketch, "E16.1.0.942", {"start": v(-171.46, 113.14) * mm, "mid": v(-174.4, 106.07) * mm, "end": v(-171.46, 99) * mm});
            skPoint(sketch, "E16.1.0.943", {"position": v(-73.48, 42.43) * mm});
            skArc(sketch, "E16.1.0.944", {"start": v(-97.98, 113.14) * mm, "mid": v(-100.9, 106.07) * mm, "end": v(-97.98, 99) * mm});
            skPoint(sketch, "E16.1.0.945", {"position": v(-146.97, 42.43) * mm});
            skPoint(sketch, "E16.1.0.946", {"position": v(-159.22, 21.21) * mm});
            skArc(sketch, "E16.1.0.947", {"start": v(-159.22, 49.5) * mm, "mid": v(-162.15, 42.43) * mm, "end": v(-159.22, 35.36) * mm});
            skArc(sketch, "E16.1.0.948", {"start": v(-36.74, 7.07) * mm, "mid": v(-29.15, 8.07) * mm, "end": v(-24.5, 14.14) * mm});
            skPoint(sketch, "E16.1.0.949", {"position": v(-24.5, 0) * mm});
            skLineSegment(sketch, "E16.1.0.950", {"start": v(-208.2, 106.07) * mm, "end": v(-222.6, 102.2) * mm, "construction": true});
            skArc(sketch, "E16.1.0.951", {"start": v(-62.14, 21.43) * mm, "mid": v(-64.48, 25.21) * mm, "end": v(-68.32, 27.46) * mm});
            skPoint(sketch, "E16.1.0.952", {"position": v(-146.97, 0) * mm});
            skArc(sketch, "E16.1.0.953", {"start": v(-123.37, 85.07) * mm, "mid": v(-125.71, 88.85) * mm, "end": v(-129.55, 91.1) * mm});
            skArc(sketch, "E16.1.0.954", {"start": v(-146.97, 70.71) * mm, "mid": v(-149.9, 63.64) * mm, "end": v(-146.97, 56.57) * mm});
            skArc(sketch, "E16.1.0.955", {"start": v(-134.72, 91.92) * mm, "mid": v(-137.65, 84.85) * mm, "end": v(-134.72, 77.78) * mm});
            skLineSegment(sketch, "E16.1.0.956", {"start": v(-146.97, 0) * mm, "end": v(-137.31, 2.59) * mm, "construction": true});
            skArc(sketch, "E16.1.0.957", {"start": v(-86.63, 21.43) * mm, "mid": v(-88.97, 25.21) * mm, "end": v(-92.81, 27.46) * mm});
            skPoint(sketch, "E16.1.0.958", {"position": v(-110.23, 21.21) * mm});
            skLineSegment(sketch, "E16.1.0.959", {"start": v(-61.24, 63.64) * mm, "end": v(-75.64, 59.78) * mm, "construction": true});
            skArc(sketch, "E16.1.0.960", {"start": v(-122.47, 113.14) * mm, "mid": v(-125.4, 106.07) * mm, "end": v(-122.47, 99) * mm});
            skArc(sketch, "E16.1.0.961", {"start": v(-111.12, 106.28) * mm, "mid": v(-113.47, 110.07) * mm, "end": v(-117.3, 112.3) * mm});
            skArc(sketch, "E16.1.0.962", {"start": v(-86.63, 106.28) * mm, "mid": v(-88.97, 110.07) * mm, "end": v(-92.81, 112.3) * mm});
            skArc(sketch, "E16.1.0.963", {"start": v(-135.62, 21.43) * mm, "mid": v(-137.96, 25.21) * mm, "end": v(-141.8, 27.46) * mm});
            skPoint(sketch, "E16.1.0.964", {"position": v(-122.51, 84.78) * mm});
            skArc(sketch, "E16.1.0.965", {"start": v(-110.23, 7.07) * mm, "mid": v(-102.64, 8.07) * mm, "end": v(-97.98, 14.14) * mm});
            skArc(sketch, "E16.1.0.966", {"start": v(-61.24, 7.07) * mm, "mid": v(-64.17, 0) * mm, "end": v(-61.24, -7.07) * mm});
            skPoint(sketch, "E16.1.0.967", {"position": v(-85.77, 106) * mm});
            skPoint(sketch, "E16.1.0.968", {"position": v(-85.73, 63.64) * mm});
            skArc(sketch, "E16.1.0.969", {"start": v(-61.24, 49.5) * mm, "mid": v(-64.17, 42.43) * mm, "end": v(-61.24, 35.36) * mm});
            skPoint(sketch, "E16.1.0.970", {"position": v(-97.98, 84.85) * mm});
            skArc(sketch, "E16.1.0.971", {"start": v(-110.23, 49.5) * mm, "mid": v(-113.16, 42.43) * mm, "end": v(-110.23, 35.36) * mm});
            skPoint(sketch, "E16.1.0.972", {"position": v(-146.97, 84.85) * mm});
            skArc(sketch, "E16.1.0.973", {"start": v(-171.46, 70.71) * mm, "mid": v(-174.4, 63.64) * mm, "end": v(-171.46, 56.57) * mm});
            skPoint(sketch, "E16.1.0.974", {"position": v(-159.22, 106.07) * mm});
            skArc(sketch, "E16.1.0.975", {"start": v(-159.22, 91.92) * mm, "mid": v(-162.15, 84.85) * mm, "end": v(-159.22, 77.78) * mm});
            skLineSegment(sketch, "E16.1.0.976", {"start": v(-122.47, 0) * mm, "end": v(-136.88, -3.86) * mm, "construction": true});
            skArc(sketch, "E16.1.0.977", {"start": v(-134.72, 49.5) * mm, "mid": v(-137.65, 42.43) * mm, "end": v(-134.72, 35.36) * mm});
            skArc(sketch, "E16.1.0.978", {"start": v(-97.98, 28.28) * mm, "mid": v(-100.9, 21.21) * mm, "end": v(-97.98, 14.14) * mm});
            skArc(sketch, "E16.1.0.979", {"start": v(-195.96, 113.14) * mm, "mid": v(-198.89, 106.07) * mm, "end": v(-195.96, 99) * mm});
            skPoint(sketch, "E16.1.0.980", {"position": v(-61.24, 63.64) * mm});
            skPoint(sketch, "E16.1.0.981", {"position": v(-196, 84.78) * mm});
            skArc(sketch, "E16.1.0.982", {"start": v(-97.98, 70.71) * mm, "mid": v(-100.9, 63.64) * mm, "end": v(-97.98, 56.57) * mm});
            skArc(sketch, "E16.1.0.983", {"start": v(-85.73, 49.5) * mm, "mid": v(-88.66, 42.43) * mm, "end": v(-85.73, 35.36) * mm});
            skPoint(sketch, "E16.1.0.984", {"position": v(-171.5, 84.78) * mm});
            skPoint(sketch, "E16.1.0.985", {"position": v(-183.71, 106.07) * mm});
            skArc(sketch, "E16.1.0.986", {"start": v(-110.23, 7.07) * mm, "mid": v(-113.16, 0) * mm, "end": v(-110.23, -7.07) * mm});
            skPoint(sketch, "E16.1.0.987", {"position": v(-183.71, 63.64) * mm});
            skArc(sketch, "E16.1.0.988", {"start": v(-36.74, 7.07) * mm, "mid": v(-39.67, 0) * mm, "end": v(-36.74, -7.07) * mm});
            skArc(sketch, "E16.1.0.989", {"start": v(-73.48, 70.71) * mm, "mid": v(-76.41, 63.64) * mm, "end": v(-73.48, 56.57) * mm});
            skPoint(sketch, "E16.1.0.990", {"position": v(-48.99, 42.43) * mm});
            skArc(sketch, "E16.1.0.991", {"start": v(-85.73, 7.07) * mm, "mid": v(-88.66, 0) * mm, "end": v(-85.73, -7.07) * mm});
            skPoint(sketch, "E16.1.0.992", {"position": v(-122.47, 42.43) * mm});
            skPoint(sketch, "E16.1.0.993", {"position": v(-97.98, 0) * mm});
            skPoint(sketch, "E16.1.0.994", {"position": v(-159.22, 63.64) * mm});
            skLineSegment(sketch, "E16.1.0.995", {"start": v(-183.71, 106.07) * mm, "end": v(-198.11, 102.2) * mm, "construction": true});
            skArc(sketch, "E16.1.0.996", {"start": v(-171.46, 70.71) * mm, "mid": v(-163.88, 71.7) * mm, "end": v(-159.22, 77.78) * mm});
            skPoint(sketch, "E16.1.0.997", {"position": v(-122.47, 0) * mm});
            skArc(sketch, "E16.1.0.998", {"start": v(-195.96, 70.71) * mm, "mid": v(-188.37, 71.7) * mm, "end": v(-183.71, 77.78) * mm});
            skArc(sketch, "E16.1.0.999", {"start": v(-159.22, 7.07) * mm, "mid": v(-151.63, 8.07) * mm, "end": v(-146.97, 14.14) * mm});
            skPoint(sketch, "E16.1.0.1000", {"position": v(-171.5, 42.36) * mm});
            skPoint(sketch, "E16.1.0.1001", {"position": v(-110.26, 63.57) * mm});
            skArc(sketch, "E16.1.0.1002", {"start": v(-146.97, 28.28) * mm, "mid": v(-149.9, 21.21) * mm, "end": v(-146.97, 14.14) * mm});
            skPoint(sketch, "E16.1.0.1003", {"position": v(-36.74, 21.21) * mm});
            skArc(sketch, "E16.1.0.1004", {"start": v(-61.24, 7.07) * mm, "mid": v(-53.65, 8.07) * mm, "end": v(-48.99, 14.14) * mm});
            skArc(sketch, "E16.1.0.1005", {"start": v(-134.46, 6.18) * mm, "mid": v(-136.85, 0) * mm, "end": v(-134.46, -6.18) * mm});
            skArc(sketch, "E16.1.0.1006", {"start": v(-146.97, 113.14) * mm, "mid": v(-149.9, 106.07) * mm, "end": v(-146.97, 99) * mm});
            skPoint(sketch, "E16.1.0.1007", {"position": v(-61.24, 63.64) * mm});
            skPoint(sketch, "E16.1.0.1008", {"position": v(-122.47, 42.43) * mm});
            skLineSegment(sketch, "E16.1.0.1009", {"start": v(-36.74, 21.21) * mm, "end": v(-51.14, 17.35) * mm, "construction": true});
            skPoint(sketch, "E16.1.0.1010", {"position": v(-24.5, 0) * mm});
            skPoint(sketch, "E16.1.0.1011", {"position": v(-110.23, 21.21) * mm});
            skLineSegment(sketch, "E16.1.0.1012", {"start": v(-134.72, 21.21) * mm, "end": v(-149.12, 17.35) * mm, "construction": true});
            skPoint(sketch, "E16.1.0.1013", {"position": v(-171.46, 42.43) * mm});
            skLineSegment(sketch, "E16.1.0.1014", {"start": v(-159.22, 106.07) * mm, "end": v(-173.62, 102.2) * mm, "construction": true});
            skPoint(sketch, "E16.1.0.1015", {"position": v(-85.73, 106.07) * mm});
            skPoint(sketch, "E16.1.0.1016", {"position": v(-73.52, 84.78) * mm});
            skPoint(sketch, "E16.1.0.1017", {"position": v(-73.48, 42.43) * mm});
            skLineSegment(sketch, "E16.1.0.1018", {"start": v(-110.23, 106.07) * mm, "end": v(-124.63, 102.2) * mm, "construction": true});
            skPoint(sketch, "E16.1.0.1019", {"position": v(-85.77, 63.57) * mm});
            skLineSegment(sketch, "E16.1.0.1020", {"start": v(-61.24, 21.21) * mm, "end": v(-75.64, 17.35) * mm, "construction": true});
            skPoint(sketch, "E16.1.0.1021", {"position": v(-183.71, 63.64) * mm});
            skPoint(sketch, "E16.1.0.1022", {"position": v(-110.23, 106.07) * mm});
            skPoint(sketch, "E16.1.0.1023", {"position": v(-134.72, 21.21) * mm});
            skPoint(sketch, "E16.1.0.1024", {"position": v(-97.98, 84.85) * mm});
            skPoint(sketch, "E16.1.0.1025", {"position": v(-208.2, 106.07) * mm});
            skPoint(sketch, "E16.1.0.1026", {"position": v(-85.73, 21.21) * mm});
            skPoint(sketch, "E16.1.0.1027", {"position": v(-195.96, 84.85) * mm});
            skPoint(sketch, "E16.1.0.1028", {"position": v(-61.24, 21.21) * mm});
            skPoint(sketch, "E16.1.0.1029", {"position": v(-147, 84.78) * mm});
            skPoint(sketch, "E16.1.0.1030", {"position": v(-159.25, 63.57) * mm});
            skPoint(sketch, "E16.1.0.1031", {"position": v(-122.47, 84.85) * mm});
            skPoint(sketch, "E16.1.0.1032", {"position": v(-110.23, 63.64) * mm});
            skPoint(sketch, "E16.1.0.1033", {"position": v(-97.98, 42.43) * mm});
            skArc(sketch, "E16.1.0.1034", {"start": v(-159.22, 7.07) * mm, "mid": v(-151.63, 8.07) * mm, "end": v(-146.97, 14.14) * mm});
            skPoint(sketch, "E16.1.0.1035", {"position": v(-36.74, 21.21) * mm});
            skPoint(sketch, "E16.1.0.1036", {"position": v(-159.22, 106.07) * mm});
            skPoint(sketch, "E16.1.0.1037", {"position": v(-159.22, 21.21) * mm});
            skLineSegment(sketch, "E16.1.0.1038", {"start": v(-134.72, 106.07) * mm, "end": v(-149.12, 102.2) * mm, "construction": true});
            skPoint(sketch, "E16.1.0.1039", {"position": v(-73.52, -0.07) * mm});
            skLineSegment(sketch, "E16.1.0.1040", {"start": v(-85.73, 21.21) * mm, "end": v(-100.13, 17.35) * mm, "construction": true});
            skPoint(sketch, "E16.1.0.1041", {"position": v(-122.47, 0) * mm});
            skPoint(sketch, "E16.1.0.1042", {"position": v(-48.99, 0) * mm});
            skPoint(sketch, "E16.1.0.1043", {"position": v(-146.97, 42.43) * mm});
            skPoint(sketch, "E16.1.0.1044", {"position": v(-171.46, 84.85) * mm});
            skPoint(sketch, "E16.1.0.1045", {"position": v(-134.72, 63.64) * mm});
            skPoint(sketch, "E16.1.0.1046", {"position": v(-183.71, 106.07) * mm});
            skPoint(sketch, "E16.1.0.1047", {"position": v(-134.72, 106.07) * mm});
            skPoint(sketch, "E16.1.0.1048", {"position": v(-97.98, 0) * mm});
            skPoint(sketch, "E16.1.0.1049", {"position": v(-48.99, 42.43) * mm});
            skPoint(sketch, "E16.1.0.1050", {"position": v(-146.97, 0) * mm});
            skArc(sketch, "E16.1.0.1051", {"start": v(-134.72, 7.07) * mm, "mid": v(-137.65, 0) * mm, "end": v(-134.72, -7.07) * mm});
            skPoint(sketch, "E16.1.0.1052", {"position": v(-85.73, 63.64) * mm});
            skPoint(sketch, "E16.1.0.1053", {"position": v(-97.98, 84.85) * mm});
            skPoint(sketch, "E16.1.0.1054", {"position": v(-110.26, 106) * mm});
            skPoint(sketch, "E16.1.0.1055", {"position": v(-146.97, 0) * mm});
            skPoint(sketch, "E16.1.0.1056", {"position": v(-171.46, 42.43) * mm});
            skPoint(sketch, "E16.1.0.1057", {"position": v(-195.96, 84.85) * mm});
            skPoint(sketch, "E16.1.0.1058", {"position": v(-110.23, 21.21) * mm});
            skPoint(sketch, "E16.1.0.1059", {"position": v(-134.72, 106.07) * mm});
            skPoint(sketch, "E16.1.0.1060", {"position": v(-183.71, 63.64) * mm});
            skPoint(sketch, "E16.1.0.1061", {"position": v(-159.22, 21.21) * mm});
            skPoint(sketch, "E16.1.0.1062", {"position": v(-146.97, 42.43) * mm});
            skPoint(sketch, "E16.1.0.1063", {"position": v(-98.02, -0.07) * mm});
            skPoint(sketch, "E16.1.0.1064", {"position": v(-134.72, 21.21) * mm});
            skPoint(sketch, "E16.1.0.1065", {"position": v(-208.2, 106.07) * mm});
            skPoint(sketch, "E16.1.0.1066", {"position": v(-97.98, 42.43) * mm});
            skPoint(sketch, "E16.1.0.1067", {"position": v(-183.75, 106) * mm});
            skPoint(sketch, "E16.1.0.1068", {"position": v(-171.46, 84.85) * mm});
            skPoint(sketch, "E16.1.0.1069", {"position": v(-73.48, 84.85) * mm});
            skPoint(sketch, "E16.1.0.1070", {"position": v(-122.51, 42.36) * mm});
            skPoint(sketch, "E16.1.0.1071", {"position": v(-159.25, 106) * mm});
            skPoint(sketch, "E16.1.0.1072", {"position": v(-24.53, -0.07) * mm});
            skPoint(sketch, "E16.1.0.1073", {"position": v(-110.23, 63.64) * mm});
            skPoint(sketch, "E16.1.0.1074", {"position": v(-146.97, 84.85) * mm});
            skPoint(sketch, "E16.1.0.1075", {"position": v(-49.03, -0.07) * mm});
            skPoint(sketch, "E16.1.0.1076", {"position": v(-134.72, 63.64) * mm});
            skPoint(sketch, "E16.1.0.1077", {"position": v(-36.78, 21.14) * mm});
            skPoint(sketch, "E16.1.0.1078", {"position": v(-73.48, 42.43) * mm});
            skPoint(sketch, "E16.1.0.1079", {"position": v(-49.03, 42.36) * mm});
            skPoint(sketch, "E16.1.0.1080", {"position": v(-73.48, 0) * mm});
            skPoint(sketch, "E16.1.0.1081", {"position": v(-61.24, 21.21) * mm});
            skPoint(sketch, "E16.1.0.1082", {"position": v(-85.77, 21.14) * mm});
            skPoint(sketch, "E16.1.0.1083", {"position": v(-159.22, 63.64) * mm});
            skPoint(sketch, "E16.1.0.1084", {"position": v(-122.47, 84.85) * mm});
            skPoint(sketch, "E16.1.0.1085", {"position": v(-122.51, -0.07) * mm});
            skPoint(sketch, "E16.1.0.1086", {"position": v(-85.73, 106.07) * mm});
            skPoint(sketch, "E16.1.0.1087", {"position": v(-61.27, 63.57) * mm});
            skLineSegment(sketch, "E16.direction1", {"start": v(-9.66, -16.73) * mm, "end": v(-156.63, -16.73) * mm, "construction": true});
            skCircle(sketch, "E17.cCircle", {"center": v(0, 56.57) * mm, "radius": 60 * mm, "construction": true});
            skLineSegment(sketch, "E17.0", {"start": v(-30, 108.53) * mm, "end": v(30, 108.53) * mm});
            skLineSegment(sketch, "E17.1", {"start": v(30, 108.53) * mm, "end": v(60, 56.57) * mm});
            skLineSegment(sketch, "E17.2", {"start": v(60, 56.57) * mm, "end": v(30, 4.6) * mm});
            skLineSegment(sketch, "E17.3", {"start": v(30, 4.6) * mm, "end": v(-30, 4.6) * mm});
            skLineSegment(sketch, "E17.4", {"start": v(-30, 4.6) * mm, "end": v(-60, 56.57) * mm});
            skLineSegment(sketch, "E17.5", {"start": v(-60, 56.57) * mm, "end": v(-30, 108.53) * mm});
            skLineSegment(sketch, "E18.0", {"start": v(28.61, 7) * mm, "end": v(-28.61, 7) * mm});
            skLineSegment(sketch, "E18.1", {"start": v(-57.23, 56.57) * mm, "end": v(-28.61, 106.13) * mm});
            skLineSegment(sketch, "E18.2", {"start": v(-28.61, 106.13) * mm, "end": v(28.61, 106.13) * mm});
            skLineSegment(sketch, "E18.3", {"start": v(-28.61, 7) * mm, "end": v(-57.23, 56.57) * mm});
            skLineSegment(sketch, "E18.4", {"start": v(28.61, 106.13) * mm, "end": v(57.23, 56.57) * mm});
            skLineSegment(sketch, "E18.5", {"start": v(57.23, 56.57) * mm, "end": v(28.61, 7) * mm});
            skSolve(sketch);
        }
        {
            var Q0;
            {var subQ3=sQuery(id+"F0.wireOp",EDGE,"E16.1.0.470");var subQ5=sQuery(id+"F0.wireOp",EDGE,"E16.1.0.367");var subQ6=makeQuery(id+"F0.imprint","INTERSECT",VERTEX,{"derivedFrom":[subQ5,subQ3]});Q0=makeQuery(id+"F0.imprint","IMPRINT",FACE,{"disambiguationData":[TD([[makeQuery(id+"F0.imprint","IMPRINT",EDGE,{"disambiguationData":[TD([[subQ6,-1.0]])],"derivedFrom":subQ5}),-1.0]])]});}
            var Q1;
            {var subQ0=sQuery(id+"F0.wireOp",EDGE,"E17.4");var subQ1=sQuery(id+"F0.wireOp",EDGE,"E16.1.0.86");var subQ2=makeQuery(id+"F0.imprint","INTERSECT",VERTEX,{"derivedFrom":[subQ1,subQ0]});Q1=makeQuery(id+"F0.imprint","IMPRINT",FACE,{"disambiguationData":[TD([[makeQuery(id+"F0.imprint","IMPRINT",EDGE,{"disambiguationData":[TD([[subQ2,-1.0]])],"derivedFrom":subQ1}),1.0]])]});}
            var Q2;
            {var subQ3=sQuery(id+"F0.wireOp",EDGE,"E17.4");var subQ4=sQuery(id+"F0.wireOp",EDGE,"E16.1.0.86");var subQ5=makeQuery(id+"F0.imprint","INTERSECT",VERTEX,{"derivedFrom":[subQ4,subQ3]});Q2=makeQuery(id+"F0.imprint","IMPRINT",FACE,{"disambiguationData":[TD([[makeQuery(id+"F0.imprint","IMPRINT",EDGE,{"disambiguationData":[TD([[subQ5,-1.0]])],"derivedFrom":subQ4}),-1.0]])]});}
            var Q3;
            {var subQ5=sQuery(id+"F0.wireOp",EDGE,"E16.1.0.222");var subQ9=sQuery(id+"F0.wireOp",EDGE,"E16.1.0.870");var subQ14=makeQuery(id+"F0.imprint","INTERSECT",VERTEX,{"derivedFrom":[subQ5,subQ9]});Q3=makeQuery(id+"F0.imprint","IMPRINT",FACE,{"disambiguationData":[TD([[makeQuery(id+"F0.imprint","IMPRINT",EDGE,{"disambiguationData":[TD([[subQ14,1.0]])],"derivedFrom":subQ5}),-1.0]])]});}
            var Q4;
            {var subQ0=sQuery(id+"F0.wireOp",EDGE,"E16.1.0.222");var subQ1=sQuery(id+"F0.wireOp",EDGE,"E16.1.0.42");var subQ2=makeQuery(id+"F0.imprint","INTERSECT",VERTEX,{"derivedFrom":[subQ1,subQ0]});Q4=makeQuery(id+"F0.imprint","IMPRINT",FACE,{"disambiguationData":[TD([[makeQuery(id+"F0.imprint","IMPRINT",EDGE,{"disambiguationData":[TD([[subQ2,1.0]])],"derivedFrom":subQ1}),1.0]])]});}
            var Q5;
            {var subQ0=sQuery(id+"F0.wireOp",EDGE,"E16.1.0.222");var subQ1=sQuery(id+"F0.wireOp",EDGE,"E16.1.0.42");var subQ2=makeQuery(id+"F0.imprint","INTERSECT",VERTEX,{"derivedFrom":[subQ1,subQ0]});Q5=makeQuery(id+"F0.imprint","IMPRINT",FACE,{"disambiguationData":[TD([[makeQuery(id+"F0.imprint","IMPRINT",EDGE,{"disambiguationData":[TD([[subQ2,1.0]])],"derivedFrom":subQ1}),-1.0]])]});}
            var Q6;
            {var subQ0=sQuery(id+"F0.wireOp",EDGE,"E16.1.0.773");var subQ1=sQuery(id+"F0.wireOp",EDGE,"E16.1.0.478");var subQ2=makeQuery(id+"F0.imprint","INTERSECT",VERTEX,{"derivedFrom":[subQ1,subQ0]});Q6=makeQuery(id+"F0.imprint","IMPRINT",FACE,{"disambiguationData":[TD([[makeQuery(id+"F0.imprint","IMPRINT",EDGE,{"disambiguationData":[TD([[subQ2,-1.0]])],"derivedFrom":subQ1}),-1.0]])]});}
            var Q7;
            {var subQ2=sQuery(id+"F0.wireOp",EDGE,"E15.0.2.58");Q7=makeQuery(id+"F0.imprint","IMPRINT",FACE,{"disambiguationData":[TD([[makeQuery(id+"F0.imprint","IMPRINT",EDGE,{"derivedFrom":subQ2}),-1.0]])]});}
            var Q8;
            {var subQ13=sQuery(id+"F0.wireOp",EDGE,"E15.0.1.58");Q8=makeQuery(id+"F0.imprint","IMPRINT",FACE,{"disambiguationData":[TD([[makeQuery(id+"F0.imprint","IMPRINT",EDGE,{"derivedFrom":subQ13}),-1.0]])]});}
            var Q9;
            {var subQ2=sQuery(id+"F0.wireOp",EDGE,"E16.1.0.84");Q9=makeQuery(id+"F0.imprint","IMPRINT",FACE,{"disambiguationData":[TD([[makeQuery(id+"F0.imprint","IMPRINT",EDGE,{"derivedFrom":subQ2}),-1.0]])]});}
            var Q10;
            {var subQ1=sQuery(id+"F0.wireOp",EDGE,"E16.1.0.428");var subQ3=sQuery(id+"F0.wireOp",EDGE,"E18.3");var subQ4=makeQuery(id+"F0.imprint","INTERSECT",VERTEX,{"derivedFrom":[subQ1,subQ3]});Q10=makeQuery(id+"F0.imprint","IMPRINT",FACE,{"disambiguationData":[TD([[makeQuery(id+"F0.imprint","IMPRINT",EDGE,{"disambiguationData":[TD([[subQ4,-1.0]])],"derivedFrom":subQ3}),-1.0]])]});}
            var Q11;
            {var subQ3=sQuery(id+"F0.wireOp",EDGE,"E16.1.0.487");var subQ5=sQuery(id+"F0.wireOp",EDGE,"E16.1.0.50");var subQ6=makeQuery(id+"F0.imprint","INTERSECT",VERTEX,{"derivedFrom":[subQ5,subQ3]});Q11=makeQuery(id+"F0.imprint","IMPRINT",FACE,{"disambiguationData":[TD([[makeQuery(id+"F0.imprint","IMPRINT",EDGE,{"disambiguationData":[TD([[subQ6,-1.0]])],"derivedFrom":subQ5}),1.0]])]});}
            var Q12;
            {var subQ0=sQuery(id+"F0.wireOp",EDGE,"E16.1.0.552");Q12=makeQuery(id+"F0.imprint","IMPRINT",FACE,{"disambiguationData":[TD([[makeQuery(id+"F0.imprint","IMPRINT",EDGE,{"derivedFrom":subQ0}),-1.0]])]});}
            var Q13;
            {var subQ4=sQuery(id+"F0.wireOp",EDGE,"E15.0.1.36");Q13=makeQuery(id+"F0.imprint","IMPRINT",FACE,{"disambiguationData":[TD([[makeQuery(id+"F0.imprint","IMPRINT",EDGE,{"derivedFrom":subQ4}),1.0]])]});}
            var Q14;
            {var subQ0=sQuery(id+"F0.wireOp",EDGE,"E16.1.0.149");var subQ8=makeQuery(id+"F0.imprint","INTERSECT",VERTEX,{"derivedFrom":[sQuery(id+"F0.wireOp",EDGE,"E16.1.0.121"),subQ0]});Q14=makeQuery(id+"F0.imprint","IMPRINT",FACE,{"disambiguationData":[TD([[makeQuery(id+"F0.imprint","IMPRINT",EDGE,{"disambiguationData":[TD([[subQ8,1.0]])],"derivedFrom":subQ0}),1.0]])]});}
            var Q15;
            {var subQ0=sQuery(id+"F0.wireOp",EDGE,"E17.4");var subQ1=sQuery(id+"F0.wireOp",EDGE,"E16.1.0.291");var subQ2=makeQuery(id+"F0.imprint","INTERSECT",VERTEX,{"derivedFrom":[subQ1,subQ0]});Q15=makeQuery(id+"F0.imprint","IMPRINT",FACE,{"disambiguationData":[TD([[makeQuery(id+"F0.imprint","IMPRINT",EDGE,{"disambiguationData":[TD([[subQ2,-1.0]])],"derivedFrom":subQ1}),-1.0]])]});}
            var Q16;
            {var subQ3=sQuery(id+"F0.wireOp",EDGE,"E16.1.0.487");var subQ5=sQuery(id+"F0.wireOp",EDGE,"E16.1.0.50");var subQ6=makeQuery(id+"F0.imprint","INTERSECT",VERTEX,{"derivedFrom":[subQ5,subQ3]});Q16=makeQuery(id+"F0.imprint","IMPRINT",FACE,{"disambiguationData":[TD([[makeQuery(id+"F0.imprint","IMPRINT",EDGE,{"disambiguationData":[TD([[subQ6,-1.0]])],"derivedFrom":subQ5}),-1.0]])]});}
            var Q17;
            {var subQ5=sQuery(id+"F0.wireOp",EDGE,"E15.0.1.1");Q17=makeQuery(id+"F0.imprint","IMPRINT",FACE,{"disambiguationData":[TD([[makeQuery(id+"F0.imprint","IMPRINT",EDGE,{"derivedFrom":subQ5}),-1.0]])]});}
            var Q18;
            {var subQ4=sQuery(id+"F0.wireOp",EDGE,"E15.0.1.3");Q18=makeQuery(id+"F0.imprint","IMPRINT",FACE,{"disambiguationData":[TD([[makeQuery(id+"F0.imprint","IMPRINT",EDGE,{"derivedFrom":subQ4}),-1.0]])]});}
            var Q19;
            {var subQ1=sQuery(id+"F0.wireOp",EDGE,"E15.0.1.3");Q19=makeQuery(id+"F0.imprint","IMPRINT",FACE,{"disambiguationData":[TD([[makeQuery(id+"F0.imprint","IMPRINT",EDGE,{"derivedFrom":subQ1}),1.0]])]});}
            var Q20;
            {var subQ0=sQuery(id+"F0.wireOp",EDGE,"E18.0");var subQ1=sQuery(id+"F0.wireOp",EDGE,"E4.1.0");var subQ2=makeQuery(id+"F0.imprint","INTERSECT",VERTEX,{"derivedFrom":[subQ1,subQ0]});Q20=makeQuery(id+"F0.imprint","IMPRINT",FACE,{"disambiguationData":[TD([[makeQuery(id+"F0.imprint","IMPRINT",EDGE,{"disambiguationData":[TD([[subQ2,-1.0]])],"derivedFrom":subQ1}),-1.0]])]});}
            var Q21;
            {var subQ0=sQuery(id+"F0.wireOp",EDGE,"E18.0");var subQ1=sQuery(id+"F0.wireOp",EDGE,"E4.1.2");var subQ2=makeQuery(id+"F0.imprint","INTERSECT",VERTEX,{"disambiguationData":[OD(0.0)],"derivedFrom":[subQ1,subQ0]});Q21=makeQuery(id+"F0.imprint","IMPRINT",FACE,{"disambiguationData":[TD([[makeQuery(id+"F0.imprint","IMPRINT",EDGE,{"disambiguationData":[TD([[subQ2,-1.0]])],"derivedFrom":subQ1}),1.0]])]});}
            var Q22;
            {var subQ1=sQuery(id+"F0.wireOp",EDGE,"E4.1.0");var subQ3=sQuery(id+"F0.wireOp",EDGE,"E18.0");var subQ4=makeQuery(id+"F0.imprint","INTERSECT",VERTEX,{"derivedFrom":[subQ1,subQ3]});Q22=makeQuery(id+"F0.imprint","IMPRINT",FACE,{"disambiguationData":[TD([[makeQuery(id+"F0.imprint","IMPRINT",EDGE,{"disambiguationData":[TD([[subQ4,1.0]])],"derivedFrom":subQ3}),-1.0]])]});}
            var Q23;
            {var subQ4=sQuery(id+"F0.wireOp",EDGE,"E18.0");var subQ5=sQuery(id+"F0.wireOp",EDGE,"E4.1.0");var subQ6=makeQuery(id+"F0.imprint","INTERSECT",VERTEX,{"derivedFrom":[subQ5,subQ4]});Q23=makeQuery(id+"F0.imprint","IMPRINT",FACE,{"disambiguationData":[TD([[makeQuery(id+"F0.imprint","IMPRINT",EDGE,{"disambiguationData":[TD([[subQ6,-1.0]])],"derivedFrom":subQ5}),1.0]])]});}
            var Q24;
            {var subQ0=sQuery(id+"F0.wireOp",EDGE,"E9.3");var subQ1=sQuery(id+"F0.wireOp",EDGE,"E9.0");var subQ2=makeQuery(id+"F0.imprint","INTERSECT",VERTEX,{"derivedFrom":[subQ1,subQ0]});Q24=makeQuery(id+"F0.imprint","IMPRINT",FACE,{"disambiguationData":[TD([[makeQuery(id+"F0.imprint","IMPRINT",EDGE,{"disambiguationData":[TD([[subQ2,-1.0]])],"derivedFrom":subQ1}),1.0]])]});}
            var Q25;
            {var subQ3=sQuery(id+"F0.wireOp",EDGE,"E16.1.0.142");var subQ5=sQuery(id+"F0.wireOp",EDGE,"E16.1.0.149");var subQ6=makeQuery(id+"F0.imprint","INTERSECT",VERTEX,{"derivedFrom":[subQ3,subQ5]});Q25=makeQuery(id+"F0.imprint","IMPRINT",FACE,{"disambiguationData":[TD([[makeQuery(id+"F0.imprint","IMPRINT",EDGE,{"disambiguationData":[TD([[subQ6,1.0]])],"derivedFrom":subQ3}),-1.0]])]});}
            var Q26;
            {var subQ0=sQuery(id+"F0.wireOp",EDGE,"E16.1.0.149");var subQ1=sQuery(id+"F0.wireOp",EDGE,"E16.1.0.121");var subQ2=makeQuery(id+"F0.imprint","INTERSECT",VERTEX,{"derivedFrom":[subQ1,subQ0]});Q26=makeQuery(id+"F0.imprint","IMPRINT",FACE,{"disambiguationData":[TD([[makeQuery(id+"F0.imprint","IMPRINT",EDGE,{"disambiguationData":[TD([[subQ2,1.0]])],"derivedFrom":subQ1}),-1.0]])]});}
            var Q27;
            {var subQ1=sQuery(id+"F0.wireOp",EDGE,"E16.1.0.121");var subQ5=sQuery(id+"F0.wireOp",EDGE,"E16.1.0.149");var subQ6=makeQuery(id+"F0.imprint","INTERSECT",VERTEX,{"derivedFrom":[subQ1,subQ5]});Q27=makeQuery(id+"F0.imprint","IMPRINT",FACE,{"disambiguationData":[TD([[makeQuery(id+"F0.imprint","IMPRINT",EDGE,{"disambiguationData":[TD([[subQ6,1.0]])],"derivedFrom":subQ1}),1.0]])]});}
            var Q28;
            {var subQ0=sQuery(id+"F0.wireOp",EDGE,"E17.3");var subQ1=sQuery(id+"F0.wireOp",EDGE,"E16.1.0.782");var subQ2=makeQuery(id+"F0.imprint","INTERSECT",VERTEX,{"derivedFrom":[subQ1,subQ0]});Q28=makeQuery(id+"F0.imprint","IMPRINT",FACE,{"disambiguationData":[TD([[makeQuery(id+"F0.imprint","IMPRINT",EDGE,{"disambiguationData":[TD([[subQ2,-1.0]])],"derivedFrom":subQ1}),1.0]])]});}
            var Q29;
            {var subQ0=sQuery(id+"F0.wireOp",EDGE,"E9.3");var subQ1=sQuery(id+"F0.wireOp",EDGE,"E2.1.0");var subQ2=makeQuery(id+"F0.imprint","INTERSECT",VERTEX,{"derivedFrom":[subQ1,subQ0]});Q29=makeQuery(id+"F0.imprint","IMPRINT",FACE,{"disambiguationData":[TD([[makeQuery(id+"F0.imprint","IMPRINT",EDGE,{"disambiguationData":[TD([[subQ2,1.0]])],"derivedFrom":subQ1}),1.0]])]});}
            var Q30;
            {var subQ1=sQuery(id+"F0.wireOp",EDGE,"E2.1.0");var subQ7=sQuery(id+"F0.wireOp",EDGE,"E9.3");var subQ8=makeQuery(id+"F0.imprint","INTERSECT",VERTEX,{"derivedFrom":[subQ1,subQ7]});Q30=makeQuery(id+"F0.imprint","IMPRINT",FACE,{"disambiguationData":[TD([[makeQuery(id+"F0.imprint","IMPRINT",EDGE,{"disambiguationData":[TD([[subQ8,1.0]])],"derivedFrom":subQ1}),-1.0]])]});}
            var Q31;
            {var subQ0=sQuery(id+"F0.wireOp",EDGE,"E17.3");var subQ1=sQuery(id+"F0.wireOp",EDGE,"E9.2");var subQ2=makeQuery(id+"F0.imprint","INTERSECT",VERTEX,{"derivedFrom":[subQ1,subQ0]});Q31=makeQuery(id+"F0.imprint","IMPRINT",FACE,{"disambiguationData":[TD([[makeQuery(id+"F0.imprint","IMPRINT",EDGE,{"disambiguationData":[TD([[subQ2,1.0]])],"derivedFrom":subQ1}),-1.0]])]});}
            var Q32;
            {var subQ0=sQuery(id+"F0.wireOp",EDGE,"E10.0");var subQ1=sQuery(id+"F0.wireOp",EDGE,"E9.3");var subQ2=makeQuery(id+"F0.imprint","INTERSECT",VERTEX,{"derivedFrom":[subQ1,subQ0]});Q32=makeQuery(id+"F0.imprint","IMPRINT",FACE,{"disambiguationData":[TD([[makeQuery(id+"F0.imprint","IMPRINT",EDGE,{"disambiguationData":[TD([[subQ2,1.0]])],"derivedFrom":subQ1}),-1.0]])]});}
            var Q33;
            {var subQ0=sQuery(id+"F0.wireOp",EDGE,"E18.0");var subQ1=sQuery(id+"F0.wireOp",EDGE,"E3.1.0.2");var subQ2=makeQuery(id+"F0.imprint","INTERSECT",VERTEX,{"derivedFrom":[subQ1,subQ0]});Q33=makeQuery(id+"F0.imprint","IMPRINT",FACE,{"disambiguationData":[TD([[makeQuery(id+"F0.imprint","IMPRINT",EDGE,{"disambiguationData":[TD([[subQ2,-1.0]])],"derivedFrom":subQ1}),-1.0]])]});}
            var Q34;
            {var subQ0=sQuery(id+"F0.wireOp",EDGE,"E18.0");var subQ10=sQuery(id+"F0.wireOp",EDGE,"E3.1.0.2");var subQ11=makeQuery(id+"F0.imprint","INTERSECT",VERTEX,{"derivedFrom":[subQ10,subQ0]});Q34=makeQuery(id+"F0.imprint","IMPRINT",FACE,{"disambiguationData":[TD([[makeQuery(id+"F0.imprint","IMPRINT",EDGE,{"disambiguationData":[TD([[subQ11,-1.0]])],"derivedFrom":subQ10}),1.0]])]});}
            var Q35;
            {var subQ4=sQuery(id+"F0.wireOp",EDGE,"E3.1.0.0");Q35=makeQuery(id+"F0.imprint","IMPRINT",FACE,{"disambiguationData":[TD([[makeQuery(id+"F0.imprint","IMPRINT",EDGE,{"derivedFrom":subQ4}),1.0]])]});}
            var Q36;
            {var subQ1=sQuery(id+"F0.wireOp",EDGE,"E3.1.0.2");var subQ3=sQuery(id+"F0.wireOp",EDGE,"E18.0");var subQ4=makeQuery(id+"F0.imprint","INTERSECT",VERTEX,{"derivedFrom":[subQ1,subQ3]});Q36=makeQuery(id+"F0.imprint","IMPRINT",FACE,{"disambiguationData":[TD([[makeQuery(id+"F0.imprint","IMPRINT",EDGE,{"disambiguationData":[TD([[subQ4,1.0]])],"derivedFrom":subQ3}),-1.0]])]});}
            var Q37;
            {var subQ0=sQuery(id+"F0.wireOp",EDGE,"E13.1.0.12");var subQ1=sQuery(id+"F0.wireOp",EDGE,"E13.1.0.3");var subQ2=makeQuery(id+"F0.imprint","INTERSECT",VERTEX,{"derivedFrom":[subQ1,subQ0]});Q37=makeQuery(id+"F0.imprint","IMPRINT",FACE,{"disambiguationData":[TD([[makeQuery(id+"F0.imprint","IMPRINT",EDGE,{"disambiguationData":[TD([[subQ2,-1.0]])],"derivedFrom":subQ1}),1.0]])]});}
            var Q38;
            {var subQ0=sQuery(id+"F0.wireOp",EDGE,"E18.0");var subQ1=sQuery(id+"F0.wireOp",EDGE,"E13.1.0.4");var subQ2=makeQuery(id+"F0.imprint","INTERSECT",VERTEX,{"disambiguationData":[OD(0.0)],"derivedFrom":[subQ1,subQ0]});Q38=makeQuery(id+"F0.imprint","IMPRINT",FACE,{"disambiguationData":[TD([[makeQuery(id+"F0.imprint","IMPRINT",EDGE,{"disambiguationData":[TD([[subQ2,-1.0]])],"derivedFrom":subQ1}),1.0]])]});}
            var Q39;
            {var subQ12=sQuery(id+"F0.wireOp",EDGE,"E3.1.0.0");Q39=makeQuery(id+"F0.imprint","IMPRINT",FACE,{"disambiguationData":[TD([[makeQuery(id+"F0.imprint","IMPRINT",EDGE,{"derivedFrom":subQ12}),-1.0]])]});}
            var Q40;
            {var subQ0=sQuery(id+"F0.wireOp",EDGE,"E13.1.0.12");var subQ1=sQuery(id+"F0.wireOp",EDGE,"E13.1.0.6");var subQ2=makeQuery(id+"F0.imprint","INTERSECT",VERTEX,{"derivedFrom":[subQ1,subQ0]});Q40=makeQuery(id+"F0.imprint","IMPRINT",FACE,{"disambiguationData":[TD([[makeQuery(id+"F0.imprint","IMPRINT",EDGE,{"disambiguationData":[TD([[subQ2,1.0]])],"derivedFrom":subQ1}),-1.0]])]});}
            var Q41;
            {var subQ0=sQuery(id+"F0.wireOp",EDGE,"E13.1.0.12");var subQ1=sQuery(id+"F0.wireOp",EDGE,"E13.1.0.11");var subQ2=makeQuery(id+"F0.imprint","INTERSECT",VERTEX,{"derivedFrom":[subQ1,subQ0]});Q41=makeQuery(id+"F0.imprint","IMPRINT",FACE,{"disambiguationData":[TD([[makeQuery(id+"F0.imprint","IMPRINT",EDGE,{"disambiguationData":[TD([[subQ2,1.0]])],"derivedFrom":subQ1}),-1.0]])]});}
            var Q42;
            {var subQ1=sQuery(id+"F0.wireOp",EDGE,"E17.2");var subQ3=sQuery(id+"F0.wireOp",EDGE,"E13.1.0.5");var subQ4=makeQuery(id+"F0.imprint","INTERSECT",VERTEX,{"derivedFrom":[subQ3,subQ1]});Q42=makeQuery(id+"F0.imprint","IMPRINT",FACE,{"disambiguationData":[TD([[makeQuery(id+"F0.imprint","IMPRINT",EDGE,{"disambiguationData":[TD([[subQ4,-1.0]])],"derivedFrom":subQ3}),1.0]])]});}
            var Q43;
            {var subQ0=sQuery(id+"F0.wireOp",EDGE,"E13.1.0.18");var subQ1=sQuery(id+"F0.wireOp",EDGE,"E13.1.0.12");var subQ2=makeQuery(id+"F0.imprint","INTERSECT",VERTEX,{"derivedFrom":[subQ1,subQ0]});Q43=makeQuery(id+"F0.imprint","IMPRINT",FACE,{"disambiguationData":[TD([[makeQuery(id+"F0.imprint","IMPRINT",EDGE,{"disambiguationData":[TD([[subQ2,1.0]])],"derivedFrom":subQ1}),-1.0]])]});}
            var Q44;
            {var subQ0=sQuery(id+"F0.wireOp",EDGE,"E17.2");var subQ1=sQuery(id+"F0.wireOp",EDGE,"E13.1.0.1");var subQ2=makeQuery(id+"F0.imprint","INTERSECT",VERTEX,{"derivedFrom":[subQ1,subQ0]});Q44=makeQuery(id+"F0.imprint","IMPRINT",FACE,{"disambiguationData":[TD([[makeQuery(id+"F0.imprint","IMPRINT",EDGE,{"disambiguationData":[TD([[subQ2,-1.0]])],"derivedFrom":subQ1}),1.0]])]});}
            var Q45;
            {var subQ4=sQuery(id+"F0.wireOp",EDGE,"E17.2");var subQ6=sQuery(id+"F0.wireOp",EDGE,"E13.1.0.1");var subQ7=makeQuery(id+"F0.imprint","INTERSECT",VERTEX,{"derivedFrom":[subQ6,subQ4]});Q45=makeQuery(id+"F0.imprint","IMPRINT",FACE,{"disambiguationData":[TD([[makeQuery(id+"F0.imprint","IMPRINT",EDGE,{"disambiguationData":[TD([[subQ7,-1.0]])],"derivedFrom":subQ6}),-1.0]])]});}
            var Q46;
            {var subQ9=sQuery(id+"F0.wireOp",EDGE,"E15.0.1.86");var subQ10=sQuery(id+"F0.wireOp",EDGE,"E15.0.1.14");var subQ11=makeQuery(id+"F0.imprint","INTERSECT",VERTEX,{"derivedFrom":[subQ10,subQ9]});Q46=makeQuery(id+"F0.imprint","IMPRINT",FACE,{"disambiguationData":[TD([[makeQuery(id+"F0.imprint","IMPRINT",EDGE,{"disambiguationData":[TD([[subQ11,-1.0]])],"derivedFrom":subQ10}),-1.0]])]});}
            var Q47;
            {var subQ0=sQuery(id+"F0.wireOp",EDGE,"E15.0.1.49");var subQ1=sQuery(id+"F0.wireOp",EDGE,"E15.0.1.20");var subQ2=makeQuery(id+"F0.imprint","INTERSECT",VERTEX,{"derivedFrom":[subQ1,subQ0]});Q47=makeQuery(id+"F0.imprint","IMPRINT",FACE,{"disambiguationData":[TD([[makeQuery(id+"F0.imprint","IMPRINT",EDGE,{"disambiguationData":[TD([[subQ2,1.0]])],"derivedFrom":subQ1}),1.0]])]});}
            var Q48;
            {var subQ0=sQuery(id+"F0.wireOp",EDGE,"E15.0.1.49");var subQ1=sQuery(id+"F0.wireOp",EDGE,"E15.0.1.20");var subQ2=makeQuery(id+"F0.imprint","INTERSECT",VERTEX,{"derivedFrom":[subQ1,subQ0]});Q48=makeQuery(id+"F0.imprint","IMPRINT",FACE,{"disambiguationData":[TD([[makeQuery(id+"F0.imprint","IMPRINT",EDGE,{"disambiguationData":[TD([[subQ2,1.0]])],"derivedFrom":subQ1}),-1.0]])]});}
            var Q49;
            {var subQ0=sQuery(id+"F0.wireOp",EDGE,"E15.0.1.86");var subQ1=sQuery(id+"F0.wireOp",EDGE,"E15.0.1.14");var subQ2=makeQuery(id+"F0.imprint","INTERSECT",VERTEX,{"derivedFrom":[subQ1,subQ0]});Q49=makeQuery(id+"F0.imprint","IMPRINT",FACE,{"disambiguationData":[TD([[makeQuery(id+"F0.imprint","IMPRINT",EDGE,{"disambiguationData":[TD([[subQ2,-1.0]])],"derivedFrom":subQ1}),1.0]])]});}
            var Q50;
            {var subQ1=sQuery(id+"F0.wireOp",EDGE,"E15.0.1.95");var subQ7=sQuery(id+"F0.wireOp",EDGE,"E15.0.1.99");var subQ8=makeQuery(id+"F0.imprint","INTERSECT",VERTEX,{"derivedFrom":[subQ1,subQ7]});Q50=makeQuery(id+"F0.imprint","IMPRINT",FACE,{"disambiguationData":[TD([[makeQuery(id+"F0.imprint","IMPRINT",EDGE,{"disambiguationData":[TD([[subQ8,-1.0]])],"derivedFrom":subQ1}),-1.0]])]});}
            var Q51;
            {var subQ1=sQuery(id+"F0.wireOp",EDGE,"E15.0.1.103");var subQ3=sQuery(id+"F0.wireOp",EDGE,"E18.5");var subQ4=makeQuery(id+"F0.imprint","INTERSECT",VERTEX,{"derivedFrom":[subQ1,subQ3]});Q51=makeQuery(id+"F0.imprint","IMPRINT",FACE,{"disambiguationData":[TD([[makeQuery(id+"F0.imprint","IMPRINT",EDGE,{"disambiguationData":[TD([[subQ4,-1.0]])],"derivedFrom":subQ3}),-1.0]])]});}
            var Q52;
            {var subQ1=sQuery(id+"F0.wireOp",EDGE,"E15.0.1.24");Q52=makeQuery(id+"F0.imprint","IMPRINT",FACE,{"disambiguationData":[TD([[makeQuery(id+"F0.imprint","IMPRINT",EDGE,{"derivedFrom":subQ1}),1.0]])]});}
            var Q53;
            {var subQ1=sQuery(id+"F0.wireOp",EDGE,"E15.0.1.24");Q53=makeQuery(id+"F0.imprint","IMPRINT",FACE,{"disambiguationData":[TD([[makeQuery(id+"F0.imprint","IMPRINT",EDGE,{"derivedFrom":subQ1}),-1.0]])]});}
            var Q54;
            {var subQ5=sQuery(id+"F0.wireOp",EDGE,"E17.2");var subQ7=sQuery(id+"F0.wireOp",EDGE,"E15.0.1.77");var subQ8=makeQuery(id+"F0.imprint","INTERSECT",VERTEX,{"derivedFrom":[subQ7,subQ5]});Q54=makeQuery(id+"F0.imprint","IMPRINT",FACE,{"disambiguationData":[TD([[makeQuery(id+"F0.imprint","IMPRINT",EDGE,{"disambiguationData":[TD([[subQ8,-1.0]])],"derivedFrom":subQ7}),1.0]])]});}
            var Q55;
            {var subQ5=sQuery(id+"F0.wireOp",EDGE,"E17.2");var subQ7=sQuery(id+"F0.wireOp",EDGE,"E15.0.1.112");var subQ8=makeQuery(id+"F0.imprint","INTERSECT",VERTEX,{"derivedFrom":[subQ7,subQ5]});Q55=makeQuery(id+"F0.imprint","IMPRINT",FACE,{"disambiguationData":[TD([[makeQuery(id+"F0.imprint","IMPRINT",EDGE,{"disambiguationData":[TD([[subQ8,-1.0]])],"derivedFrom":subQ7}),-1.0]])]});}
            var Q56;
            {var subQ5=sQuery(id+"F0.wireOp",EDGE,"E15.0.2.121");var subQ6=sQuery(id+"F0.wireOp",EDGE,"E15.0.2.21");var subQ7=makeQuery(id+"F0.imprint","INTERSECT",VERTEX,{"derivedFrom":[subQ6,subQ5]});Q56=makeQuery(id+"F0.imprint","IMPRINT",FACE,{"disambiguationData":[TD([[makeQuery(id+"F0.imprint","IMPRINT",EDGE,{"disambiguationData":[TD([[subQ7,-1.0]])],"derivedFrom":subQ6}),-1.0]])]});}
            var Q57;
            {var subQ0=sQuery(id+"F0.wireOp",EDGE,"E15.0.2.144");var subQ1=sQuery(id+"F0.wireOp",EDGE,"E15.0.2.28");var subQ2=makeQuery(id+"F0.imprint","INTERSECT",VERTEX,{"derivedFrom":[subQ1,subQ0]});Q57=makeQuery(id+"F0.imprint","IMPRINT",FACE,{"disambiguationData":[TD([[makeQuery(id+"F0.imprint","IMPRINT",EDGE,{"disambiguationData":[TD([[subQ2,1.0]])],"derivedFrom":subQ1}),-1.0]])]});}
            var Q58;
            {var subQ0=sQuery(id+"F0.wireOp",EDGE,"E17.2");var subQ1=sQuery(id+"F0.wireOp",EDGE,"E15.0.1.77");var subQ2=makeQuery(id+"F0.imprint","INTERSECT",VERTEX,{"derivedFrom":[subQ1,subQ0]});Q58=makeQuery(id+"F0.imprint","IMPRINT",FACE,{"disambiguationData":[TD([[makeQuery(id+"F0.imprint","IMPRINT",EDGE,{"disambiguationData":[TD([[subQ2,-1.0]])],"derivedFrom":subQ1}),-1.0]])]});}
            var Q59;
            {var subQ0=sQuery(id+"F0.wireOp",EDGE,"E15.0.2.144");var subQ1=sQuery(id+"F0.wireOp",EDGE,"E15.0.2.28");var subQ2=makeQuery(id+"F0.imprint","INTERSECT",VERTEX,{"derivedFrom":[subQ1,subQ0]});Q59=makeQuery(id+"F0.imprint","IMPRINT",FACE,{"disambiguationData":[TD([[makeQuery(id+"F0.imprint","IMPRINT",EDGE,{"disambiguationData":[TD([[subQ2,1.0]])],"derivedFrom":subQ1}),1.0]])]});}
            var Q60;
            {var subQ12=sQuery(id+"F0.wireOp",EDGE,"E15.0.2.107");Q60=makeQuery(id+"F0.imprint","IMPRINT",FACE,{"disambiguationData":[TD([[makeQuery(id+"F0.imprint","IMPRINT",EDGE,{"derivedFrom":subQ12}),-1.0]])]});}
            var Q61;
            {var subQ2=sQuery(id+"F0.wireOp",EDGE,"E15.0.1.37");Q61=makeQuery(id+"F0.imprint","IMPRINT",FACE,{"disambiguationData":[TD([[makeQuery(id+"F0.imprint","IMPRINT",EDGE,{"derivedFrom":subQ2}),-1.0]])]});}
            var Q62;
            {var subQ0=sQuery(id+"F0.wireOp",EDGE,"E15.0.2.121");var subQ1=sQuery(id+"F0.wireOp",EDGE,"E15.0.2.21");var subQ2=makeQuery(id+"F0.imprint","INTERSECT",VERTEX,{"derivedFrom":[subQ1,subQ0]});Q62=makeQuery(id+"F0.imprint","IMPRINT",FACE,{"disambiguationData":[TD([[makeQuery(id+"F0.imprint","IMPRINT",EDGE,{"disambiguationData":[TD([[subQ2,-1.0]])],"derivedFrom":subQ1}),1.0]])]});}
            var Q63;
            {var subQ1=sQuery(id+"F0.wireOp",EDGE,"E15.0.2.93");var subQ3=sQuery(id+"F0.wireOp",EDGE,"E18.5");var subQ4=makeQuery(id+"F0.imprint","INTERSECT",VERTEX,{"derivedFrom":[subQ1,subQ3]});Q63=makeQuery(id+"F0.imprint","IMPRINT",FACE,{"disambiguationData":[TD([[makeQuery(id+"F0.imprint","IMPRINT",EDGE,{"disambiguationData":[TD([[subQ4,1.0]])],"derivedFrom":subQ3}),-1.0]])]});}
            var Q64;
            {var subQ1=sQuery(id+"F0.wireOp",EDGE,"E15.0.2.91");Q64=makeQuery(id+"F0.imprint","IMPRINT",FACE,{"disambiguationData":[TD([[makeQuery(id+"F0.imprint","IMPRINT",EDGE,{"derivedFrom":subQ1}),-1.0]])]});}
            var Q65;
            {var subQ0=sQuery(id+"F0.wireOp",EDGE,"E15.0.2.75");var subQ1=sQuery(id+"F0.wireOp",EDGE,"E15.0.2.11");var subQ2=makeQuery(id+"F0.imprint","INTERSECT",VERTEX,{"derivedFrom":[subQ1,subQ0]});Q65=makeQuery(id+"F0.imprint","IMPRINT",FACE,{"disambiguationData":[TD([[makeQuery(id+"F0.imprint","IMPRINT",EDGE,{"disambiguationData":[TD([[subQ2,-1.0]])],"derivedFrom":subQ1}),-1.0]])]});}
            var Q66;
            {var subQ1=sQuery(id+"F0.wireOp",EDGE,"E15.0.2.136");Q66=makeQuery(id+"F0.imprint","IMPRINT",FACE,{"disambiguationData":[TD([[makeQuery(id+"F0.imprint","IMPRINT",EDGE,{"derivedFrom":subQ1}),-1.0]])]});}
            var Q67;
            {var subQ0=sQuery(id+"F0.wireOp",EDGE,"E17.2");var subQ1=sQuery(id+"F0.wireOp",EDGE,"E15.0.2.31");var subQ2=makeQuery(id+"F0.imprint","INTERSECT",VERTEX,{"derivedFrom":[subQ1,subQ0]});Q67=makeQuery(id+"F0.imprint","IMPRINT",FACE,{"disambiguationData":[TD([[makeQuery(id+"F0.imprint","IMPRINT",EDGE,{"disambiguationData":[TD([[subQ2,-1.0]])],"derivedFrom":subQ1}),-1.0]])]});}
            var Q68;
            {var subQ5=sQuery(id+"F0.wireOp",EDGE,"E17.2");var subQ7=sQuery(id+"F0.wireOp",EDGE,"E15.0.2.89");var subQ8=makeQuery(id+"F0.imprint","INTERSECT",VERTEX,{"derivedFrom":[subQ7,subQ5]});Q68=makeQuery(id+"F0.imprint","IMPRINT",FACE,{"disambiguationData":[TD([[makeQuery(id+"F0.imprint","IMPRINT",EDGE,{"disambiguationData":[TD([[subQ8,-1.0]])],"derivedFrom":subQ7}),-1.0]])]});}
            var Q69;
            {var subQ1=sQuery(id+"F0.wireOp",EDGE,"E15.0.3.74");Q69=makeQuery(id+"F0.imprint","IMPRINT",FACE,{"disambiguationData":[TD([[makeQuery(id+"F0.imprint","IMPRINT",EDGE,{"derivedFrom":subQ1}),-1.0]])]});}
            var Q70;
            Q70=makeQuery(id+"F0.imprint","IMPRINT",FACE,{"disambiguationData":[TD([[makeQuery(id+"F0.imprint","IMPRINT",EDGE,{"derivedFrom":sQuery(id+"F0.wireOp",EDGE,"E15.0.2.109")}),1.0]])]});
            var Q71;
            {var subQ0=sQuery(id+"F0.wireOp",EDGE,"E17.1");var subQ1=sQuery(id+"F0.wireOp",EDGE,"E15.0.3.71");var subQ2=makeQuery(id+"F0.imprint","INTERSECT",VERTEX,{"derivedFrom":[subQ1,subQ0]});Q71=makeQuery(id+"F0.imprint","IMPRINT",FACE,{"disambiguationData":[TD([[makeQuery(id+"F0.imprint","IMPRINT",EDGE,{"disambiguationData":[TD([[subQ2,1.0]])],"derivedFrom":subQ1}),-1.0]])]});}
            var Q72;
            {var subQ0=sQuery(id+"F0.wireOp",EDGE,"E17.1");var subQ1=sQuery(id+"F0.wireOp",EDGE,"E15.0.3.13");var subQ2=makeQuery(id+"F0.imprint","INTERSECT",VERTEX,{"derivedFrom":[subQ1,subQ0]});Q72=makeQuery(id+"F0.imprint","IMPRINT",FACE,{"disambiguationData":[TD([[makeQuery(id+"F0.imprint","IMPRINT",EDGE,{"disambiguationData":[TD([[subQ2,-1.0]])],"derivedFrom":subQ1}),-1.0]])]});}
            var Q73;
            {var subQ0=sQuery(id+"F0.wireOp",EDGE,"E17.1");var subQ1=sQuery(id+"F0.wireOp",EDGE,"E15.0.3.13");var subQ2=makeQuery(id+"F0.imprint","INTERSECT",VERTEX,{"derivedFrom":[subQ1,subQ0]});Q73=makeQuery(id+"F0.imprint","IMPRINT",FACE,{"disambiguationData":[TD([[makeQuery(id+"F0.imprint","IMPRINT",EDGE,{"disambiguationData":[TD([[subQ2,-1.0]])],"derivedFrom":subQ1}),1.0]])]});}
            var Q74;
            {var subQ0=sQuery(id+"F0.wireOp",EDGE,"E17.1");var subQ1=sQuery(id+"F0.wireOp",EDGE,"E15.0.3.71");var subQ2=makeQuery(id+"F0.imprint","INTERSECT",VERTEX,{"derivedFrom":[subQ1,subQ0]});Q74=makeQuery(id+"F0.imprint","IMPRINT",FACE,{"disambiguationData":[TD([[makeQuery(id+"F0.imprint","IMPRINT",EDGE,{"disambiguationData":[TD([[subQ2,1.0]])],"derivedFrom":subQ1}),1.0]])]});}
            var Q75;
            {var subQ0=sQuery(id+"F0.wireOp",EDGE,"E18.4");var subQ1=sQuery(id+"F0.wireOp",EDGE,"E15.0.3.89");var subQ2=makeQuery(id+"F0.imprint","INTERSECT",VERTEX,{"disambiguationData":[OD(0.0)],"derivedFrom":[subQ1,subQ0]});Q75=makeQuery(id+"F0.imprint","IMPRINT",FACE,{"disambiguationData":[TD([[makeQuery(id+"F0.imprint","IMPRINT",EDGE,{"disambiguationData":[TD([[subQ2,-1.0]])],"derivedFrom":subQ1}),1.0]])]});}
            var Q76;
            {var subQ6=sQuery(id+"F0.wireOp",EDGE,"E18.4");var subQ12=sQuery(id+"F0.wireOp",EDGE,"E15.0.3.89");var subQ14=makeQuery(id+"F0.imprint","INTERSECT",VERTEX,{"disambiguationData":[OD(0.0)],"derivedFrom":[subQ12,subQ6]});Q76=makeQuery(id+"F0.imprint","IMPRINT",FACE,{"disambiguationData":[TD([[makeQuery(id+"F0.imprint","IMPRINT",EDGE,{"disambiguationData":[TD([[subQ14,-1.0]])],"derivedFrom":subQ12}),-1.0]])]});}
            var Q77;
            {var subQ0=sQuery(id+"F0.wireOp",EDGE,"E15.0.4.87");var subQ1=sQuery(id+"F0.wireOp",EDGE,"E15.0.4.13");var subQ2=makeQuery(id+"F0.imprint","INTERSECT",VERTEX,{"derivedFrom":[subQ1,subQ0]});Q77=makeQuery(id+"F0.imprint","IMPRINT",FACE,{"disambiguationData":[TD([[makeQuery(id+"F0.imprint","IMPRINT",EDGE,{"disambiguationData":[TD([[subQ2,1.0]])],"derivedFrom":subQ1}),1.0]])]});}
            var Q78;
            {var subQ1=sQuery(id+"F0.wireOp",EDGE,"E15.0.3.89");var subQ3=sQuery(id+"F0.wireOp",EDGE,"E18.4");var subQ4=makeQuery(id+"F0.imprint","INTERSECT",VERTEX,{"disambiguationData":[OD(0.0)],"derivedFrom":[subQ1,subQ3]});Q78=makeQuery(id+"F0.imprint","IMPRINT",FACE,{"disambiguationData":[TD([[makeQuery(id+"F0.imprint","IMPRINT",EDGE,{"disambiguationData":[TD([[subQ4,-1.0]])],"derivedFrom":subQ3}),-1.0]])]});}
            var Q79;
            {var subQ0=sQuery(id+"F0.wireOp",EDGE,"E15.0.4.87");var subQ1=sQuery(id+"F0.wireOp",EDGE,"E15.0.4.13");var subQ2=makeQuery(id+"F0.imprint","INTERSECT",VERTEX,{"derivedFrom":[subQ1,subQ0]});Q79=makeQuery(id+"F0.imprint","IMPRINT",FACE,{"disambiguationData":[TD([[makeQuery(id+"F0.imprint","IMPRINT",EDGE,{"disambiguationData":[TD([[subQ2,1.0]])],"derivedFrom":subQ1}),-1.0]])]});}
            var Q80;
            {var subQ0=sQuery(id+"F0.wireOp",EDGE,"E15.0.4.87");var subQ1=sQuery(id+"F0.wireOp",EDGE,"E15.0.4.57");var subQ2=makeQuery(id+"F0.imprint","INTERSECT",VERTEX,{"derivedFrom":[subQ1,subQ0]});Q80=makeQuery(id+"F0.imprint","IMPRINT",FACE,{"disambiguationData":[TD([[makeQuery(id+"F0.imprint","IMPRINT",EDGE,{"disambiguationData":[TD([[subQ2,1.0]])],"derivedFrom":subQ1}),-1.0]])]});}
            var Q81;
            {var subQ4=sQuery(id+"F0.wireOp",EDGE,"E15.0.4.74");Q81=makeQuery(id+"F0.imprint","IMPRINT",FACE,{"disambiguationData":[TD([[makeQuery(id+"F0.imprint","IMPRINT",EDGE,{"derivedFrom":subQ4}),-1.0]])]});}
            var Q82;
            Q82=makeQuery(id+"F0.imprint","IMPRINT",FACE,{"disambiguationData":[TD([[makeQuery(id+"F0.imprint","IMPRINT",EDGE,{"derivedFrom":sQuery(id+"F0.wireOp",EDGE,"E15.0.3.109")}),1.0]])]});
            var Q83;
            {var subQ0=sQuery(id+"F0.wireOp",EDGE,"E18.4");var subQ1=sQuery(id+"F0.wireOp",EDGE,"E15.0.4.89");var subQ2=makeQuery(id+"F0.imprint","INTERSECT",VERTEX,{"disambiguationData":[OD(0.0)],"derivedFrom":[subQ1,subQ0]});Q83=makeQuery(id+"F0.imprint","IMPRINT",FACE,{"disambiguationData":[TD([[makeQuery(id+"F0.imprint","IMPRINT",EDGE,{"disambiguationData":[TD([[subQ2,-1.0]])],"derivedFrom":subQ1}),1.0]])]});}
            var Q84;
            {var subQ0=sQuery(id+"F0.wireOp",EDGE,"E17.1");var subQ1=sQuery(id+"F0.wireOp",EDGE,"E15.0.4.71");var subQ2=makeQuery(id+"F0.imprint","INTERSECT",VERTEX,{"derivedFrom":[subQ1,subQ0]});Q84=makeQuery(id+"F0.imprint","IMPRINT",FACE,{"disambiguationData":[TD([[makeQuery(id+"F0.imprint","IMPRINT",EDGE,{"disambiguationData":[TD([[subQ2,1.0]])],"derivedFrom":subQ1}),1.0]])]});}
            var Q85;
            {var subQ6=sQuery(id+"F0.wireOp",EDGE,"E18.4");var subQ10=sQuery(id+"F0.wireOp",EDGE,"E15.0.4.89");var subQ11=makeQuery(id+"F0.imprint","INTERSECT",VERTEX,{"disambiguationData":[OD(0.0)],"derivedFrom":[subQ10,subQ6]});Q85=makeQuery(id+"F0.imprint","IMPRINT",FACE,{"disambiguationData":[TD([[makeQuery(id+"F0.imprint","IMPRINT",EDGE,{"disambiguationData":[TD([[subQ11,-1.0]])],"derivedFrom":subQ10}),-1.0]])]});}
            var Q86;
            {var subQ0=sQuery(id+"F0.wireOp",EDGE,"E17.1");var subQ1=sQuery(id+"F0.wireOp",EDGE,"E15.0.4.71");var subQ2=makeQuery(id+"F0.imprint","INTERSECT",VERTEX,{"derivedFrom":[subQ1,subQ0]});Q86=makeQuery(id+"F0.imprint","IMPRINT",FACE,{"disambiguationData":[TD([[makeQuery(id+"F0.imprint","IMPRINT",EDGE,{"disambiguationData":[TD([[subQ2,1.0]])],"derivedFrom":subQ1}),-1.0]])]});}
            var Q87;
            {var subQ0=sQuery(id+"F0.wireOp",EDGE,"E15.0.5.87");var subQ1=sQuery(id+"F0.wireOp",EDGE,"E15.0.5.13");var subQ2=makeQuery(id+"F0.imprint","INTERSECT",VERTEX,{"derivedFrom":[subQ1,subQ0]});Q87=makeQuery(id+"F0.imprint","IMPRINT",FACE,{"disambiguationData":[TD([[makeQuery(id+"F0.imprint","IMPRINT",EDGE,{"disambiguationData":[TD([[subQ2,1.0]])],"derivedFrom":subQ1}),1.0]])]});}
            var Q88;
            {var subQ0=sQuery(id+"F0.wireOp",EDGE,"E15.0.5.87");var subQ1=sQuery(id+"F0.wireOp",EDGE,"E15.0.5.13");var subQ2=makeQuery(id+"F0.imprint","INTERSECT",VERTEX,{"derivedFrom":[subQ1,subQ0]});Q88=makeQuery(id+"F0.imprint","IMPRINT",FACE,{"disambiguationData":[TD([[makeQuery(id+"F0.imprint","IMPRINT",EDGE,{"disambiguationData":[TD([[subQ2,1.0]])],"derivedFrom":subQ1}),-1.0]])]});}
            var Q89;
            {var subQ1=sQuery(id+"F0.wireOp",EDGE,"E15.0.5.57");var subQ5=sQuery(id+"F0.wireOp",EDGE,"E15.0.5.87");var subQ6=makeQuery(id+"F0.imprint","INTERSECT",VERTEX,{"derivedFrom":[subQ1,subQ5]});Q89=makeQuery(id+"F0.imprint","IMPRINT",FACE,{"disambiguationData":[TD([[makeQuery(id+"F0.imprint","IMPRINT",EDGE,{"disambiguationData":[TD([[subQ6,1.0]])],"derivedFrom":subQ1}),-1.0]])]});}
            var Q90;
            {var subQ1=sQuery(id+"F0.wireOp",EDGE,"E17.0");var subQ8=sQuery(id+"F0.wireOp",EDGE,"E15.0.5.74");var subQ10=makeQuery(id+"F0.imprint","INTERSECT",VERTEX,{"derivedFrom":[subQ8,subQ1]});Q90=makeQuery(id+"F0.imprint","IMPRINT",FACE,{"disambiguationData":[TD([[makeQuery(id+"F0.imprint","IMPRINT",EDGE,{"disambiguationData":[TD([[subQ10,-1.0]])],"derivedFrom":subQ8}),1.0]])]});}
            var Q91;
            {var subQ0=sQuery(id+"F0.wireOp",EDGE,"E15.0.5.87");var subQ1=sQuery(id+"F0.wireOp",EDGE,"E15.0.5.84");var subQ2=makeQuery(id+"F0.imprint","INTERSECT",VERTEX,{"derivedFrom":[subQ1,subQ0]});Q91=makeQuery(id+"F0.imprint","IMPRINT",FACE,{"disambiguationData":[TD([[makeQuery(id+"F0.imprint","IMPRINT",EDGE,{"disambiguationData":[TD([[subQ2,1.0]])],"derivedFrom":subQ1}),1.0]])]});}
            var Q92;
            {var subQ0=sQuery(id+"F0.wireOp",EDGE,"E15.0.5.87");var subQ4=sQuery(id+"F0.wireOp",EDGE,"E15.0.5.74");var subQ5=makeQuery(id+"F0.imprint","INTERSECT",VERTEX,{"derivedFrom":[subQ4,subQ0]});Q92=makeQuery(id+"F0.imprint","IMPRINT",FACE,{"disambiguationData":[TD([[makeQuery(id+"F0.imprint","IMPRINT",EDGE,{"disambiguationData":[TD([[subQ5,1.0]])],"derivedFrom":subQ4}),-1.0]])]});}
            var Q93;
            {var subQ1=sQuery(id+"F0.wireOp",EDGE,"E15.0.4.89");var subQ3=sQuery(id+"F0.wireOp",EDGE,"E18.4");var subQ4=makeQuery(id+"F0.imprint","INTERSECT",VERTEX,{"disambiguationData":[OD(0.0)],"derivedFrom":[subQ1,subQ3]});Q93=makeQuery(id+"F0.imprint","IMPRINT",FACE,{"disambiguationData":[TD([[makeQuery(id+"F0.imprint","IMPRINT",EDGE,{"disambiguationData":[TD([[subQ4,-1.0]])],"derivedFrom":subQ3}),-1.0]])]});}
            var Q94;
            {var subQ0=sQuery(id+"F0.wireOp",EDGE,"E17.0");var subQ1=sQuery(id+"F0.wireOp",EDGE,"E15.0.5.74");var subQ2=makeQuery(id+"F0.imprint","INTERSECT",VERTEX,{"derivedFrom":[subQ1,subQ0]});Q94=makeQuery(id+"F0.imprint","IMPRINT",FACE,{"disambiguationData":[TD([[makeQuery(id+"F0.imprint","IMPRINT",EDGE,{"disambiguationData":[TD([[subQ2,-1.0]])],"derivedFrom":subQ1}),-1.0]])]});}
            var Q95;
            {var subQ0=sQuery(id+"F0.wireOp",EDGE,"E15.0.5.15");var subQ8=makeQuery(id+"F0.imprint","INTERSECT",VERTEX,{"derivedFrom":[subQ0,sQuery(id+"F0.wireOp",EDGE,"E15.0.5.145")]});Q95=makeQuery(id+"F0.imprint","IMPRINT",FACE,{"disambiguationData":[TD([[makeQuery(id+"F0.imprint","IMPRINT",EDGE,{"disambiguationData":[TD([[subQ8,1.0]])],"derivedFrom":subQ0}),1.0]])]});}
            var Q96;
            {var subQ0=sQuery(id+"F0.wireOp",EDGE,"E15.0.5.75");var subQ1=sQuery(id+"F0.wireOp",EDGE,"E15.0.5.11");var subQ2=makeQuery(id+"F0.imprint","INTERSECT",VERTEX,{"derivedFrom":[subQ1,subQ0]});Q96=makeQuery(id+"F0.imprint","IMPRINT",FACE,{"disambiguationData":[TD([[makeQuery(id+"F0.imprint","IMPRINT",EDGE,{"disambiguationData":[TD([[subQ2,-1.0]])],"derivedFrom":subQ1}),-1.0]])]});}
            var Q97;
            {var subQ0=sQuery(id+"F0.wireOp",EDGE,"E15.0.5.121");var subQ1=sQuery(id+"F0.wireOp",EDGE,"E15.0.5.15");var subQ2=makeQuery(id+"F0.imprint","INTERSECT",VERTEX,{"derivedFrom":[subQ1,subQ0]});Q97=makeQuery(id+"F0.imprint","IMPRINT",FACE,{"disambiguationData":[TD([[makeQuery(id+"F0.imprint","IMPRINT",EDGE,{"disambiguationData":[TD([[subQ2,1.0]])],"derivedFrom":subQ1}),-1.0]])]});}
            var Q98;
            {var subQ0=sQuery(id+"F0.wireOp",EDGE,"E15.0.5.121");var subQ1=sQuery(id+"F0.wireOp",EDGE,"E15.0.5.15");var subQ2=makeQuery(id+"F0.imprint","INTERSECT",VERTEX,{"derivedFrom":[subQ1,subQ0]});Q98=makeQuery(id+"F0.imprint","IMPRINT",FACE,{"disambiguationData":[TD([[makeQuery(id+"F0.imprint","IMPRINT",EDGE,{"disambiguationData":[TD([[subQ2,-1.0]])],"derivedFrom":subQ1}),-1.0]])]});}
            var Q99;
            {var subQ0=sQuery(id+"F0.wireOp",EDGE,"E15.0.5.75");var subQ1=sQuery(id+"F0.wireOp",EDGE,"E15.0.5.11");var subQ2=makeQuery(id+"F0.imprint","INTERSECT",VERTEX,{"derivedFrom":[subQ1,subQ0]});Q99=makeQuery(id+"F0.imprint","IMPRINT",FACE,{"disambiguationData":[TD([[makeQuery(id+"F0.imprint","IMPRINT",EDGE,{"disambiguationData":[TD([[subQ2,-1.0]])],"derivedFrom":subQ1}),1.0]])]});}
            var Q100;
            {var subQ5=sQuery(id+"F0.wireOp",EDGE,"E15.0.5.91");var subQ6=sQuery(id+"F0.wireOp",EDGE,"E15.0.5.28");var subQ7=makeQuery(id+"F0.imprint","INTERSECT",VERTEX,{"derivedFrom":[subQ6,subQ5]});Q100=makeQuery(id+"F0.imprint","IMPRINT",FACE,{"disambiguationData":[TD([[makeQuery(id+"F0.imprint","IMPRINT",EDGE,{"disambiguationData":[TD([[subQ7,-1.0]])],"derivedFrom":subQ6}),1.0]])]});}
            var Q101;
            {var subQ3=sQuery(id+"F0.wireOp",EDGE,"E15.0.5.91");var subQ6=sQuery(id+"F0.wireOp",EDGE,"E15.0.5.28");var subQ9=makeQuery(id+"F0.imprint","INTERSECT",VERTEX,{"derivedFrom":[subQ6,subQ3]});Q101=makeQuery(id+"F0.imprint","IMPRINT",FACE,{"disambiguationData":[TD([[makeQuery(id+"F0.imprint","IMPRINT",EDGE,{"disambiguationData":[TD([[subQ9,-1.0]])],"derivedFrom":subQ6}),-1.0]])]});}
            var Q102;
            {var subQ1=sQuery(id+"F0.wireOp",EDGE,"E15.0.5.136");var subQ3=sQuery(id+"F0.wireOp",EDGE,"E18.2");var subQ4=makeQuery(id+"F0.imprint","INTERSECT",VERTEX,{"derivedFrom":[subQ1,subQ3]});Q102=makeQuery(id+"F0.imprint","IMPRINT",FACE,{"disambiguationData":[TD([[makeQuery(id+"F0.imprint","IMPRINT",EDGE,{"disambiguationData":[TD([[subQ4,-1.0]])],"derivedFrom":subQ3}),-1.0]])]});}
            var Q103;
            {var subQ1=sQuery(id+"F0.wireOp",EDGE,"E15.0.5.21");Q103=makeQuery(id+"F0.imprint","IMPRINT",FACE,{"disambiguationData":[TD([[makeQuery(id+"F0.imprint","IMPRINT",EDGE,{"derivedFrom":subQ1}),-1.0]])]});}
            var Q104;
            {var subQ0=sQuery(id+"F0.wireOp",EDGE,"E17.0");var subQ1=sQuery(id+"F0.wireOp",EDGE,"E15.0.5.107");var subQ2=makeQuery(id+"F0.imprint","INTERSECT",VERTEX,{"derivedFrom":[subQ1,subQ0]});Q104=makeQuery(id+"F0.imprint","IMPRINT",FACE,{"disambiguationData":[TD([[makeQuery(id+"F0.imprint","IMPRINT",EDGE,{"disambiguationData":[TD([[subQ2,-1.0]])],"derivedFrom":subQ1}),-1.0]])]});}
            var Q105;
            {var subQ5=sQuery(id+"F0.wireOp",EDGE,"E15.0.5.63");var subQ8=makeQuery(id+"F0.imprint","INTERSECT",VERTEX,{"derivedFrom":[subQ5,sQuery(id+"F0.wireOp",EDGE,"E15.0.5.103")]});Q105=makeQuery(id+"F0.imprint","IMPRINT",FACE,{"disambiguationData":[TD([[makeQuery(id+"F0.imprint","IMPRINT",EDGE,{"disambiguationData":[TD([[subQ8,1.0]])],"derivedFrom":subQ5}),1.0]])]});}
            var Q106;
            {var subQ0=sQuery(id+"F0.wireOp",EDGE,"E15.0.5.86");var subQ1=sQuery(id+"F0.wireOp",EDGE,"E15.0.5.63");var subQ2=makeQuery(id+"F0.imprint","INTERSECT",VERTEX,{"derivedFrom":[subQ1,subQ0]});Q106=makeQuery(id+"F0.imprint","IMPRINT",FACE,{"disambiguationData":[TD([[makeQuery(id+"F0.imprint","IMPRINT",EDGE,{"disambiguationData":[TD([[subQ2,-1.0]])],"derivedFrom":subQ1}),-1.0]])]});}
            var Q107;
            {var subQ0=sQuery(id+"F0.wireOp",EDGE,"E15.0.5.86");var subQ1=sQuery(id+"F0.wireOp",EDGE,"E15.0.5.63");var subQ2=makeQuery(id+"F0.imprint","INTERSECT",VERTEX,{"derivedFrom":[subQ1,subQ0]});Q107=makeQuery(id+"F0.imprint","IMPRINT",FACE,{"disambiguationData":[TD([[makeQuery(id+"F0.imprint","IMPRINT",EDGE,{"disambiguationData":[TD([[subQ2,1.0]])],"derivedFrom":subQ1}),-1.0]])]});}
            var Q108;
            {var subQ0=sQuery(id+"F0.wireOp",EDGE,"E15.0.5.99");var subQ1=sQuery(id+"F0.wireOp",EDGE,"E15.0.5.95");var subQ2=makeQuery(id+"F0.imprint","INTERSECT",VERTEX,{"derivedFrom":[subQ1,subQ0]});Q108=makeQuery(id+"F0.imprint","IMPRINT",FACE,{"disambiguationData":[TD([[makeQuery(id+"F0.imprint","IMPRINT",EDGE,{"disambiguationData":[TD([[subQ2,-1.0]])],"derivedFrom":subQ1}),1.0]])]});}
            var Q109;
            {var subQ3=sQuery(id+"F0.wireOp",EDGE,"E15.0.5.131");var subQ6=sQuery(id+"F0.wireOp",EDGE,"E15.0.5.20");var subQ9=makeQuery(id+"F0.imprint","INTERSECT",VERTEX,{"derivedFrom":[subQ6,subQ3]});Q109=makeQuery(id+"F0.imprint","IMPRINT",FACE,{"disambiguationData":[TD([[makeQuery(id+"F0.imprint","IMPRINT",EDGE,{"disambiguationData":[TD([[subQ9,-1.0]])],"derivedFrom":subQ6}),1.0]])]});}
            var Q110;
            {var subQ1=sQuery(id+"F0.wireOp",EDGE,"E15.0.5.131");var subQ7=sQuery(id+"F0.wireOp",EDGE,"E15.0.5.20");var subQ8=makeQuery(id+"F0.imprint","INTERSECT",VERTEX,{"derivedFrom":[subQ7,subQ1]});Q110=makeQuery(id+"F0.imprint","IMPRINT",FACE,{"disambiguationData":[TD([[makeQuery(id+"F0.imprint","IMPRINT",EDGE,{"disambiguationData":[TD([[subQ8,-1.0]])],"derivedFrom":subQ7}),-1.0]])]});}
            var Q111;
            {var subQ0=sQuery(id+"F0.wireOp",EDGE,"E17.0");var subQ1=sQuery(id+"F0.wireOp",EDGE,"E15.0.5.137");var subQ2=makeQuery(id+"F0.imprint","INTERSECT",VERTEX,{"derivedFrom":[subQ1,subQ0]});Q111=makeQuery(id+"F0.imprint","IMPRINT",FACE,{"disambiguationData":[TD([[makeQuery(id+"F0.imprint","IMPRINT",EDGE,{"disambiguationData":[TD([[subQ2,-1.0]])],"derivedFrom":subQ1}),1.0]])]});}
            var Q112;
            {var subQ5=sQuery(id+"F0.wireOp",EDGE,"E15.0.5.9");var subQ7=makeQuery(id+"F0.imprint","INTERSECT",VERTEX,{"derivedFrom":[subQ5,sQuery(id+"F0.wireOp",EDGE,"E15.0.5.150")]});Q112=makeQuery(id+"F0.imprint","IMPRINT",FACE,{"disambiguationData":[TD([[makeQuery(id+"F0.imprint","IMPRINT",EDGE,{"disambiguationData":[TD([[subQ7,1.0]])],"derivedFrom":subQ5}),1.0]])]});}
            var Q113;
            {var subQ3=sQuery(id+"F0.wireOp",EDGE,"E15.0.5.88");var subQ5=sQuery(id+"F0.wireOp",EDGE,"E15.0.5.9");var subQ6=makeQuery(id+"F0.imprint","INTERSECT",VERTEX,{"derivedFrom":[subQ5,subQ3]});Q113=makeQuery(id+"F0.imprint","IMPRINT",FACE,{"disambiguationData":[TD([[makeQuery(id+"F0.imprint","IMPRINT",EDGE,{"disambiguationData":[TD([[subQ6,-1.0]])],"derivedFrom":subQ5}),-1.0]])]});}
            var Q114;
            {var subQ10=sQuery(id+"F0.wireOp",EDGE,"E18.2");var subQ11=sQuery(id+"F0.wireOp",EDGE,"E15.0.5.24");var subQ12=makeQuery(id+"F0.imprint","INTERSECT",VERTEX,{"derivedFrom":[subQ11,subQ10]});Q114=makeQuery(id+"F0.imprint","IMPRINT",FACE,{"disambiguationData":[TD([[makeQuery(id+"F0.imprint","IMPRINT",EDGE,{"disambiguationData":[TD([[subQ12,-1.0]])],"derivedFrom":subQ11}),-1.0]])]});}
            var Q115;
            {var subQ0=sQuery(id+"F0.wireOp",EDGE,"E15.0.5.88");var subQ1=sQuery(id+"F0.wireOp",EDGE,"E15.0.5.9");var subQ2=makeQuery(id+"F0.imprint","INTERSECT",VERTEX,{"derivedFrom":[subQ1,subQ0]});Q115=makeQuery(id+"F0.imprint","IMPRINT",FACE,{"disambiguationData":[TD([[makeQuery(id+"F0.imprint","IMPRINT",EDGE,{"disambiguationData":[TD([[subQ2,1.0]])],"derivedFrom":subQ1}),-1.0]])]});}
            var Q116;
            {var subQ3=sQuery(id+"F0.wireOp",EDGE,"E15.0.5.7");var subQ5=sQuery(id+"F0.wireOp",EDGE,"E17.5");var subQ6=makeQuery(id+"F0.imprint","INTERSECT",VERTEX,{"derivedFrom":[subQ3,subQ5]});Q116=makeQuery(id+"F0.imprint","IMPRINT",FACE,{"disambiguationData":[TD([[makeQuery(id+"F0.imprint","IMPRINT",EDGE,{"disambiguationData":[TD([[subQ6,-1.0]])],"derivedFrom":subQ3}),-1.0]])]});}
            var Q117;
            {var subQ0=sQuery(id+"F0.wireOp",EDGE,"E17.5");var subQ1=sQuery(id+"F0.wireOp",EDGE,"E15.0.5.7");var subQ2=makeQuery(id+"F0.imprint","INTERSECT",VERTEX,{"derivedFrom":[subQ1,subQ0]});Q117=makeQuery(id+"F0.imprint","IMPRINT",FACE,{"disambiguationData":[TD([[makeQuery(id+"F0.imprint","IMPRINT",EDGE,{"disambiguationData":[TD([[subQ2,-1.0]])],"derivedFrom":subQ1}),1.0]])]});}
            var Q118;
            {var subQ0=sQuery(id+"F0.wireOp",EDGE,"E18.1");var subQ1=sQuery(id+"F0.wireOp",EDGE,"E15.0.4.102");var subQ2=makeQuery(id+"F0.imprint","INTERSECT",VERTEX,{"derivedFrom":[subQ1,subQ0]});Q118=makeQuery(id+"F0.imprint","IMPRINT",FACE,{"disambiguationData":[TD([[makeQuery(id+"F0.imprint","IMPRINT",EDGE,{"disambiguationData":[TD([[subQ2,-1.0]])],"derivedFrom":subQ1}),-1.0]])]});}
            var Q119;
            {var subQ0=sQuery(id+"F0.wireOp",EDGE,"E15.0.4.50");var subQ1=sQuery(id+"F0.wireOp",EDGE,"E15.0.4.10");var subQ2=makeQuery(id+"F0.imprint","INTERSECT",VERTEX,{"derivedFrom":[subQ1,subQ0]});Q119=makeQuery(id+"F0.imprint","IMPRINT",FACE,{"disambiguationData":[TD([[makeQuery(id+"F0.imprint","IMPRINT",EDGE,{"disambiguationData":[TD([[subQ2,-1.0]])],"derivedFrom":subQ1}),1.0]])]});}
            var Q120;
            {var subQ0=sQuery(id+"F0.wireOp",EDGE,"E15.0.4.50");var subQ1=sQuery(id+"F0.wireOp",EDGE,"E15.0.4.10");var subQ2=makeQuery(id+"F0.imprint","INTERSECT",VERTEX,{"derivedFrom":[subQ1,subQ0]});Q120=makeQuery(id+"F0.imprint","IMPRINT",FACE,{"disambiguationData":[TD([[makeQuery(id+"F0.imprint","IMPRINT",EDGE,{"disambiguationData":[TD([[subQ2,-1.0]])],"derivedFrom":subQ1}),-1.0]])]});}
            var Q121;
            {var subQ0=sQuery(id+"F0.wireOp",EDGE,"E15.0.4.55");var subQ1=sQuery(id+"F0.wireOp",EDGE,"E15.0.4.10");var subQ2=makeQuery(id+"F0.imprint","INTERSECT",VERTEX,{"derivedFrom":[subQ1,subQ0]});Q121=makeQuery(id+"F0.imprint","IMPRINT",FACE,{"disambiguationData":[TD([[makeQuery(id+"F0.imprint","IMPRINT",EDGE,{"disambiguationData":[TD([[subQ2,1.0]])],"derivedFrom":subQ1}),-1.0]])]});}
            var Q122;
            {var subQ1=sQuery(id+"F0.wireOp",EDGE,"E15.0.4.55");var subQ7=sQuery(id+"F0.wireOp",EDGE,"E15.0.4.10");var subQ8=makeQuery(id+"F0.imprint","INTERSECT",VERTEX,{"derivedFrom":[subQ7,subQ1]});Q122=makeQuery(id+"F0.imprint","IMPRINT",FACE,{"disambiguationData":[TD([[makeQuery(id+"F0.imprint","IMPRINT",EDGE,{"disambiguationData":[TD([[subQ8,-1.0]])],"derivedFrom":subQ7}),-1.0]])]});}
            var Q123;
            {var subQ0=sQuery(id+"F0.wireOp",EDGE,"E18.1");var subQ1=sQuery(id+"F0.wireOp",EDGE,"E15.0.4.47");var subQ2=makeQuery(id+"F0.imprint","INTERSECT",VERTEX,{"derivedFrom":[subQ1,subQ0]});Q123=makeQuery(id+"F0.imprint","IMPRINT",FACE,{"disambiguationData":[TD([[makeQuery(id+"F0.imprint","IMPRINT",EDGE,{"disambiguationData":[TD([[subQ2,-1.0]])],"derivedFrom":subQ1}),-1.0]])]});}
            var Q124;
            {var subQ0=sQuery(id+"F0.wireOp",EDGE,"E18.1");var subQ1=sQuery(id+"F0.wireOp",EDGE,"E15.0.4.128");var subQ2=makeQuery(id+"F0.imprint","INTERSECT",VERTEX,{"disambiguationData":[OD(0.0)],"derivedFrom":[subQ1,subQ0]});Q124=makeQuery(id+"F0.imprint","IMPRINT",FACE,{"disambiguationData":[TD([[makeQuery(id+"F0.imprint","IMPRINT",EDGE,{"disambiguationData":[TD([[subQ2,-1.0]])],"derivedFrom":subQ1}),1.0]])]});}
            var Q125;
            {var subQ1=sQuery(id+"F0.wireOp",EDGE,"E15.0.4.102");var subQ3=sQuery(id+"F0.wireOp",EDGE,"E18.1");var subQ4=makeQuery(id+"F0.imprint","INTERSECT",VERTEX,{"derivedFrom":[subQ1,subQ3]});Q125=makeQuery(id+"F0.imprint","IMPRINT",FACE,{"disambiguationData":[TD([[makeQuery(id+"F0.imprint","IMPRINT",EDGE,{"disambiguationData":[TD([[subQ4,1.0]])],"derivedFrom":subQ3}),-1.0]])]});}
            var Q126;
            {var subQ9=sQuery(id+"F0.wireOp",EDGE,"E15.0.4.106");Q126=makeQuery(id+"F0.imprint","IMPRINT",FACE,{"disambiguationData":[TD([[makeQuery(id+"F0.imprint","IMPRINT",EDGE,{"derivedFrom":subQ9}),1.0]])]});}
            var Q127;
            {var subQ13=sQuery(id+"F0.wireOp",EDGE,"E15.0.3.102");Q127=makeQuery(id+"F0.imprint","IMPRINT",FACE,{"disambiguationData":[TD([[makeQuery(id+"F0.imprint","IMPRINT",EDGE,{"derivedFrom":subQ13}),-1.0]])]});}
            var Q128;
            {var subQ0=sQuery(id+"F0.wireOp",EDGE,"E15.0.4.115");var subQ1=sQuery(id+"F0.wireOp",EDGE,"E15.0.4.10");var subQ2=makeQuery(id+"F0.imprint","INTERSECT",VERTEX,{"derivedFrom":[subQ1,subQ0]});Q128=makeQuery(id+"F0.imprint","IMPRINT",FACE,{"disambiguationData":[TD([[makeQuery(id+"F0.imprint","IMPRINT",EDGE,{"disambiguationData":[TD([[subQ2,1.0]])],"derivedFrom":subQ1}),-1.0]])]});}
            var Q129;
            {var subQ6=sQuery(id+"F0.wireOp",EDGE,"E15.0.3.39");Q129=makeQuery(id+"F0.imprint","IMPRINT",FACE,{"disambiguationData":[TD([[makeQuery(id+"F0.imprint","IMPRINT",EDGE,{"derivedFrom":subQ6}),1.0]])]});}
            var Q130;
            {var subQ0=sQuery(id+"F0.wireOp",EDGE,"E18.1");var subQ1=sQuery(id+"F0.wireOp",EDGE,"E15.0.4.36");var subQ2=makeQuery(id+"F0.imprint","INTERSECT",VERTEX,{"derivedFrom":[subQ1,subQ0]});Q130=makeQuery(id+"F0.imprint","IMPRINT",FACE,{"disambiguationData":[TD([[makeQuery(id+"F0.imprint","IMPRINT",EDGE,{"disambiguationData":[TD([[subQ2,-1.0]])],"derivedFrom":subQ1}),-1.0]])]});}
            var Q131;
            {var subQ5=sQuery(id+"F0.wireOp",EDGE,"E18.1");var subQ6=sQuery(id+"F0.wireOp",EDGE,"E15.0.3.58");var subQ7=makeQuery(id+"F0.imprint","INTERSECT",VERTEX,{"disambiguationData":[OD(0.0)],"derivedFrom":[subQ6,subQ5]});Q131=makeQuery(id+"F0.imprint","IMPRINT",FACE,{"disambiguationData":[TD([[makeQuery(id+"F0.imprint","IMPRINT",EDGE,{"disambiguationData":[TD([[subQ7,-1.0]])],"derivedFrom":subQ6}),-1.0]])]});}
            var Q132;
            {var subQ0=sQuery(id+"F0.wireOp",EDGE,"E16.1.0.160");var subQ1=sQuery(id+"F0.wireOp",EDGE,"E16.1.0.4");var subQ2=makeQuery(id+"F0.imprint","INTERSECT",VERTEX,{"derivedFrom":[subQ1,subQ0]});Q132=makeQuery(id+"F0.imprint","IMPRINT",FACE,{"disambiguationData":[TD([[makeQuery(id+"F0.imprint","IMPRINT",EDGE,{"disambiguationData":[TD([[subQ2,-1.0]])],"derivedFrom":subQ1}),1.0]])]});}
            var Q133;
            {var subQ1=sQuery(id+"F0.wireOp",EDGE,"E15.0.3.58");var subQ3=sQuery(id+"F0.wireOp",EDGE,"E18.1");var subQ4=makeQuery(id+"F0.imprint","INTERSECT",VERTEX,{"disambiguationData":[OD(0.0)],"derivedFrom":[subQ1,subQ3]});Q133=makeQuery(id+"F0.imprint","IMPRINT",FACE,{"disambiguationData":[TD([[makeQuery(id+"F0.imprint","IMPRINT",EDGE,{"disambiguationData":[TD([[subQ4,-1.0]])],"derivedFrom":subQ3}),-1.0]])]});}
            var Q134;
            {var subQ0=sQuery(id+"F0.wireOp",EDGE,"E18.1");var subQ1=sQuery(id+"F0.wireOp",EDGE,"E15.0.3.58");var subQ2=makeQuery(id+"F0.imprint","INTERSECT",VERTEX,{"disambiguationData":[OD(0.0)],"derivedFrom":[subQ1,subQ0]});Q134=makeQuery(id+"F0.imprint","IMPRINT",FACE,{"disambiguationData":[TD([[makeQuery(id+"F0.imprint","IMPRINT",EDGE,{"disambiguationData":[TD([[subQ2,-1.0]])],"derivedFrom":subQ1}),1.0]])]});}
            var Q135;
            {var subQ0=sQuery(id+"F0.wireOp",EDGE,"E16.1.0.269");var subQ1=sQuery(id+"F0.wireOp",EDGE,"E16.1.0.160");var subQ2=makeQuery(id+"F0.imprint","INTERSECT",VERTEX,{"derivedFrom":[subQ1,subQ0]});Q135=makeQuery(id+"F0.imprint","IMPRINT",FACE,{"disambiguationData":[TD([[makeQuery(id+"F0.imprint","IMPRINT",EDGE,{"disambiguationData":[TD([[subQ2,1.0]])],"derivedFrom":subQ1}),-1.0]])]});}
            var Q136;
            {var subQ1=sQuery(id+"F0.wireOp",EDGE,"E16.1.0.269");var subQ7=sQuery(id+"F0.wireOp",EDGE,"E16.1.0.160");var subQ8=makeQuery(id+"F0.imprint","INTERSECT",VERTEX,{"derivedFrom":[subQ7,subQ1]});Q136=makeQuery(id+"F0.imprint","IMPRINT",FACE,{"disambiguationData":[TD([[makeQuery(id+"F0.imprint","IMPRINT",EDGE,{"disambiguationData":[TD([[subQ8,-1.0]])],"derivedFrom":subQ7}),-1.0]])]});}
            var Q137;
            {var subQ1=sQuery(id+"F0.wireOp",EDGE,"E17.4");var subQ5=sQuery(id+"F0.wireOp",EDGE,"E16.1.0.158");var subQ6=makeQuery(id+"F0.imprint","INTERSECT",VERTEX,{"derivedFrom":[subQ5,subQ1]});Q137=makeQuery(id+"F0.imprint","IMPRINT",FACE,{"disambiguationData":[TD([[makeQuery(id+"F0.imprint","IMPRINT",EDGE,{"disambiguationData":[TD([[subQ6,-1.0]])],"derivedFrom":subQ5}),1.0]])]});}
            var Q138;
            {var subQ0=sQuery(id+"F0.wireOp",EDGE,"E16.1.0.544");var subQ1=sQuery(id+"F0.wireOp",EDGE,"E16.1.0.160");var subQ2=makeQuery(id+"F0.imprint","INTERSECT",VERTEX,{"derivedFrom":[subQ1,subQ0]});Q138=makeQuery(id+"F0.imprint","IMPRINT",FACE,{"disambiguationData":[TD([[makeQuery(id+"F0.imprint","IMPRINT",EDGE,{"disambiguationData":[TD([[subQ2,1.0]])],"derivedFrom":subQ1}),-1.0]])]});}
            var Q139;
            {var subQ0=sQuery(id+"F0.wireOp",EDGE,"E17.4");var subQ1=sQuery(id+"F0.wireOp",EDGE,"E16.1.0.32");var subQ2=makeQuery(id+"F0.imprint","INTERSECT",VERTEX,{"derivedFrom":[subQ1,subQ0]});Q139=makeQuery(id+"F0.imprint","IMPRINT",FACE,{"disambiguationData":[TD([[makeQuery(id+"F0.imprint","IMPRINT",EDGE,{"disambiguationData":[TD([[subQ2,-1.0]])],"derivedFrom":subQ1}),1.0]])]});}
            var Q140;
            {var subQ4=sQuery(id+"F0.wireOp",EDGE,"E17.4");var subQ6=sQuery(id+"F0.wireOp",EDGE,"E16.1.0.32");var subQ7=makeQuery(id+"F0.imprint","INTERSECT",VERTEX,{"derivedFrom":[subQ6,subQ4]});Q140=makeQuery(id+"F0.imprint","IMPRINT",FACE,{"disambiguationData":[TD([[makeQuery(id+"F0.imprint","IMPRINT",EDGE,{"disambiguationData":[TD([[subQ7,-1.0]])],"derivedFrom":subQ6}),-1.0]])]});}
            var Q141;
            {var subQ0=sQuery(id+"F0.wireOp",EDGE,"E16.1.0.565");var subQ1=sQuery(id+"F0.wireOp",EDGE,"E16.1.0.557");var subQ2=makeQuery(id+"F0.imprint","INTERSECT",VERTEX,{"derivedFrom":[subQ1,subQ0]});Q141=makeQuery(id+"F0.imprint","IMPRINT",FACE,{"disambiguationData":[TD([[makeQuery(id+"F0.imprint","IMPRINT",EDGE,{"disambiguationData":[TD([[subQ2,1.0]])],"derivedFrom":subQ1}),-1.0]])]});}
            var Q142;
            {var subQ0=sQuery(id+"F0.wireOp",EDGE,"E16.1.0.565");var subQ1=sQuery(id+"F0.wireOp",EDGE,"E16.1.0.557");var subQ2=makeQuery(id+"F0.imprint","INTERSECT",VERTEX,{"derivedFrom":[subQ1,subQ0]});Q142=makeQuery(id+"F0.imprint","IMPRINT",FACE,{"disambiguationData":[TD([[makeQuery(id+"F0.imprint","IMPRINT",EDGE,{"disambiguationData":[TD([[subQ2,1.0]])],"derivedFrom":subQ1}),1.0]])]});}
            var Q143;
            {var subQ0=sQuery(id+"F0.wireOp",EDGE,"E16.1.0.628");var subQ1=sQuery(id+"F0.wireOp",EDGE,"E16.1.0.454");var subQ2=makeQuery(id+"F0.imprint","INTERSECT",VERTEX,{"derivedFrom":[subQ1,subQ0]});Q143=makeQuery(id+"F0.imprint","IMPRINT",FACE,{"disambiguationData":[TD([[makeQuery(id+"F0.imprint","IMPRINT",EDGE,{"disambiguationData":[TD([[subQ2,-1.0]])],"derivedFrom":subQ1}),1.0]])]});}
            var Q144;
            {var subQ0=sQuery(id+"F0.wireOp",EDGE,"E16.1.0.628");var subQ1=sQuery(id+"F0.wireOp",EDGE,"E16.1.0.454");var subQ2=makeQuery(id+"F0.imprint","INTERSECT",VERTEX,{"derivedFrom":[subQ1,subQ0]});Q144=makeQuery(id+"F0.imprint","IMPRINT",FACE,{"disambiguationData":[TD([[makeQuery(id+"F0.imprint","IMPRINT",EDGE,{"disambiguationData":[TD([[subQ2,-1.0]])],"derivedFrom":subQ1}),-1.0]])]});}
            var Q145;
            {var subQ1=sQuery(id+"F0.wireOp",EDGE,"E16.1.0.559");var subQ3=sQuery(id+"F0.wireOp",EDGE,"E18.3");var subQ4=makeQuery(id+"F0.imprint","INTERSECT",VERTEX,{"derivedFrom":[subQ1,subQ3]});Q145=makeQuery(id+"F0.imprint","IMPRINT",FACE,{"disambiguationData":[TD([[makeQuery(id+"F0.imprint","IMPRINT",EDGE,{"disambiguationData":[TD([[subQ4,-1.0]])],"derivedFrom":subQ3}),-1.0]])]});}
            var Q146;
            {var subQ2=sQuery(id+"F0.wireOp",EDGE,"E16.1.0.92");Q146=makeQuery(id+"F0.imprint","IMPRINT",FACE,{"disambiguationData":[TD([[makeQuery(id+"F0.imprint","IMPRINT",EDGE,{"derivedFrom":subQ2}),-1.0]])]});}
            var Q147;
            {var subQ1=sQuery(id+"F0.wireOp",EDGE,"E16.1.0.470");var subQ7=sQuery(id+"F0.wireOp",EDGE,"E16.1.0.367");var subQ8=makeQuery(id+"F0.imprint","INTERSECT",VERTEX,{"derivedFrom":[subQ7,subQ1]});Q147=makeQuery(id+"F0.imprint","IMPRINT",FACE,{"disambiguationData":[TD([[makeQuery(id+"F0.imprint","IMPRINT",EDGE,{"disambiguationData":[TD([[subQ8,-1.0]])],"derivedFrom":subQ7}),1.0]])]});}
            var Q148;
            {var subQ6=sQuery(id+"F0.wireOp",EDGE,"E16.1.0.546");Q148=makeQuery(id+"F0.imprint","IMPRINT",FACE,{"disambiguationData":[TD([[makeQuery(id+"F0.imprint","IMPRINT",EDGE,{"derivedFrom":subQ6}),-1.0]])]});}
            var Q149;
            {var subQ3=sQuery(id+"F0.wireOp",EDGE,"E15.0.2.11");var subQ5=sQuery(id+"F0.wireOp",EDGE,"E15.0.2.75");var subQ6=makeQuery(id+"F0.imprint","INTERSECT",VERTEX,{"derivedFrom":[subQ3,subQ5]});Q149=makeQuery(id+"F0.imprint","IMPRINT",FACE,{"disambiguationData":[TD([[makeQuery(id+"F0.imprint","IMPRINT",EDGE,{"disambiguationData":[TD([[subQ6,-1.0]])],"derivedFrom":subQ3}),1.0]])]});}
            var Q150;
            {var subQ0=sQuery(id+"F0.wireOp",EDGE,"E15.0.3.87");var subQ1=sQuery(id+"F0.wireOp",EDGE,"E15.0.3.57");var subQ2=makeQuery(id+"F0.imprint","INTERSECT",VERTEX,{"derivedFrom":[subQ1,subQ0]});Q150=makeQuery(id+"F0.imprint","IMPRINT",FACE,{"disambiguationData":[TD([[makeQuery(id+"F0.imprint","IMPRINT",EDGE,{"disambiguationData":[TD([[subQ2,1.0]])],"derivedFrom":subQ1}),-1.0]])]});}
            var Q151;
            {var subQ5=sQuery(id+"F0.wireOp",EDGE,"E16.1.0.160");var subQ9=sQuery(id+"F0.wireOp",EDGE,"E16.1.0.158");var subQ10=makeQuery(id+"F0.imprint","INTERSECT",VERTEX,{"derivedFrom":[subQ9,subQ5]});Q151=makeQuery(id+"F0.imprint","IMPRINT",FACE,{"disambiguationData":[TD([[makeQuery(id+"F0.imprint","IMPRINT",EDGE,{"disambiguationData":[TD([[subQ10,1.0]])],"derivedFrom":subQ9}),-1.0]])]});}
            var Q152;
            {var subQ2=sQuery(id+"F0.wireOp",EDGE,"E15.0.3.3");Q152=makeQuery(id+"F0.imprint","IMPRINT",FACE,{"disambiguationData":[TD([[makeQuery(id+"F0.imprint","IMPRINT",EDGE,{"derivedFrom":subQ2}),1.0]])]});}
            var Q153;
            Q153=makeQuery(id+"F0.imprint","IMPRINT",FACE,{"disambiguationData":[TD([[makeQuery(id+"F0.imprint","IMPRINT",EDGE,{"derivedFrom":sQuery(id+"F0.wireOp",EDGE,"E15.0.1.39")}),1.0]])]});
            var Q154;
            Q154=makeQuery(id+"F0.imprint","IMPRINT",FACE,{"disambiguationData":[TD([[makeQuery(id+"F0.imprint","IMPRINT",EDGE,{"derivedFrom":sQuery(id+"F0.wireOp",EDGE,"E15.0.2.102")}),-1.0]])]});
            var Q155;
            Q155=makeQuery(id+"F0.imprint","IMPRINT",FACE,{"disambiguationData":[TD([[makeQuery(id+"F0.imprint","IMPRINT",EDGE,{"derivedFrom":sQuery(id+"F0.wireOp",EDGE,"E15.0.2.39")}),1.0]])]});
            var Q156;
            {var subQ5=sQuery(id+"F0.wireOp",EDGE,"E15.0.3.3");Q156=makeQuery(id+"F0.imprint","IMPRINT",FACE,{"disambiguationData":[TD([[makeQuery(id+"F0.imprint","IMPRINT",EDGE,{"derivedFrom":subQ5}),-1.0]])]});}
            var Q157;
            {var subQ2=sQuery(id+"F0.wireOp",EDGE,"E15.0.3.55");Q157=makeQuery(id+"F0.imprint","IMPRINT",FACE,{"disambiguationData":[TD([[makeQuery(id+"F0.imprint","IMPRINT",EDGE,{"derivedFrom":subQ2}),1.0]])]});}
            var Q158;
            {var subQ2=sQuery(id+"F0.wireOp",EDGE,"E15.0.3.17");Q158=makeQuery(id+"F0.imprint","IMPRINT",FACE,{"disambiguationData":[TD([[makeQuery(id+"F0.imprint","IMPRINT",EDGE,{"derivedFrom":subQ2}),-1.0]])]});}
            var Q159;
            {var subQ2=sQuery(id+"F0.wireOp",EDGE,"E15.0.3.7");Q159=makeQuery(id+"F0.imprint","IMPRINT",FACE,{"disambiguationData":[TD([[makeQuery(id+"F0.imprint","IMPRINT",EDGE,{"derivedFrom":subQ2}),-1.0]])]});}
            var Q160;
            {var subQ2=sQuery(id+"F0.wireOp",EDGE,"E15.0.3.17");Q160=makeQuery(id+"F0.imprint","IMPRINT",FACE,{"disambiguationData":[TD([[makeQuery(id+"F0.imprint","IMPRINT",EDGE,{"derivedFrom":subQ2}),1.0]])]});}
            var Q161;
            Q161=makeQuery(id+"F0.imprint","IMPRINT",FACE,{"disambiguationData":[TD([[makeQuery(id+"F0.imprint","IMPRINT",EDGE,{"derivedFrom":sQuery(id+"F0.wireOp",EDGE,"E15.0.2.25")}),-1.0]])]});
            var Q162;
            Q162=makeQuery(id+"F0.imprint","IMPRINT",FACE,{"disambiguationData":[TD([[makeQuery(id+"F0.imprint","IMPRINT",EDGE,{"derivedFrom":sQuery(id+"F0.wireOp",EDGE,"E15.0.1.102")}),-1.0]])]});
            var Q163;
            Q163=makeQuery(id+"F0.imprint","IMPRINT",FACE,{"disambiguationData":[TD([[makeQuery(id+"F0.imprint","IMPRINT",EDGE,{"derivedFrom":sQuery(id+"F0.wireOp",EDGE,"E15.0.1.25")}),-1.0]])]});
            var Q164;
            {var subQ2=sQuery(id+"F0.wireOp",EDGE,"E15.0.2.3");Q164=makeQuery(id+"F0.imprint","IMPRINT",FACE,{"disambiguationData":[TD([[makeQuery(id+"F0.imprint","IMPRINT",EDGE,{"derivedFrom":subQ2}),1.0]])]});}
            var Q165;
            {var subQ5=sQuery(id+"F0.wireOp",EDGE,"E15.0.2.3");Q165=makeQuery(id+"F0.imprint","IMPRINT",FACE,{"disambiguationData":[TD([[makeQuery(id+"F0.imprint","IMPRINT",EDGE,{"derivedFrom":subQ5}),-1.0]])]});}
            var Q166;
            {var subQ1=sQuery(id+"F0.wireOp",EDGE,"E15.0.2.55");Q166=makeQuery(id+"F0.imprint","IMPRINT",FACE,{"disambiguationData":[TD([[makeQuery(id+"F0.imprint","IMPRINT",EDGE,{"derivedFrom":subQ1}),1.0]])]});}
            var Q167;
            {var subQ4=sQuery(id+"F0.wireOp",EDGE,"E15.0.2.17");Q167=makeQuery(id+"F0.imprint","IMPRINT",FACE,{"disambiguationData":[TD([[makeQuery(id+"F0.imprint","IMPRINT",EDGE,{"derivedFrom":subQ4}),-1.0]])]});}
            var Q168;
            {var subQ1=sQuery(id+"F0.wireOp",EDGE,"E15.0.2.7");Q168=makeQuery(id+"F0.imprint","IMPRINT",FACE,{"disambiguationData":[TD([[makeQuery(id+"F0.imprint","IMPRINT",EDGE,{"derivedFrom":subQ1}),-1.0]])]});}
            var Q169;
            {var subQ1=sQuery(id+"F0.wireOp",EDGE,"E15.0.2.17");Q169=makeQuery(id+"F0.imprint","IMPRINT",FACE,{"disambiguationData":[TD([[makeQuery(id+"F0.imprint","IMPRINT",EDGE,{"derivedFrom":subQ1}),1.0]])]});}
            var Q170;
            {var subQ4=sQuery(id+"F0.wireOp",EDGE,"E15.0.2.20");Q170=makeQuery(id+"F0.imprint","IMPRINT",FACE,{"disambiguationData":[TD([[makeQuery(id+"F0.imprint","IMPRINT",EDGE,{"derivedFrom":subQ4}),1.0]])]});}
            var Q171;
            {var subQ5=sQuery(id+"F0.wireOp",EDGE,"E15.0.2.24");Q171=makeQuery(id+"F0.imprint","IMPRINT",FACE,{"disambiguationData":[TD([[makeQuery(id+"F0.imprint","IMPRINT",EDGE,{"derivedFrom":subQ5}),-1.0]])]});}
            var Q172;
            {var subQ1=sQuery(id+"F0.wireOp",EDGE,"E15.0.2.14");Q172=makeQuery(id+"F0.imprint","IMPRINT",FACE,{"disambiguationData":[TD([[makeQuery(id+"F0.imprint","IMPRINT",EDGE,{"derivedFrom":subQ1}),-1.0]])]});}
            var Q173;
            {var subQ3=sQuery(id+"F0.wireOp",EDGE,"E15.0.1.17");Q173=makeQuery(id+"F0.imprint","IMPRINT",FACE,{"disambiguationData":[TD([[makeQuery(id+"F0.imprint","IMPRINT",EDGE,{"derivedFrom":subQ3}),-1.0]])]});}
            var Q174;
            {var subQ1=sQuery(id+"F0.wireOp",EDGE,"E15.0.1.7");Q174=makeQuery(id+"F0.imprint","IMPRINT",FACE,{"disambiguationData":[TD([[makeQuery(id+"F0.imprint","IMPRINT",EDGE,{"derivedFrom":subQ1}),-1.0]])]});}
            var Q175;
            {var subQ1=sQuery(id+"F0.wireOp",EDGE,"E15.0.1.17");Q175=makeQuery(id+"F0.imprint","IMPRINT",FACE,{"disambiguationData":[TD([[makeQuery(id+"F0.imprint","IMPRINT",EDGE,{"derivedFrom":subQ1}),1.0]])]});}
            var Q176;
            {var subQ5=sQuery(id+"F0.wireOp",EDGE,"E15.0.3.14");Q176=makeQuery(id+"F0.imprint","IMPRINT",FACE,{"disambiguationData":[TD([[makeQuery(id+"F0.imprint","IMPRINT",EDGE,{"derivedFrom":subQ5}),-1.0]])]});}
            var Q177;
            {var subQ1=sQuery(id+"F0.wireOp",EDGE,"E15.0.3.20");Q177=makeQuery(id+"F0.imprint","IMPRINT",FACE,{"disambiguationData":[TD([[makeQuery(id+"F0.imprint","IMPRINT",EDGE,{"derivedFrom":subQ1}),1.0]])]});}
            var Q178;
            {var subQ4=sQuery(id+"F0.wireOp",EDGE,"E15.0.3.28");Q178=makeQuery(id+"F0.imprint","IMPRINT",FACE,{"disambiguationData":[TD([[makeQuery(id+"F0.imprint","IMPRINT",EDGE,{"derivedFrom":subQ4}),1.0]])]});}
            var Q179;
            {var subQ2=sQuery(id+"F0.wireOp",EDGE,"E15.0.3.21");Q179=makeQuery(id+"F0.imprint","IMPRINT",FACE,{"disambiguationData":[TD([[makeQuery(id+"F0.imprint","IMPRINT",EDGE,{"derivedFrom":subQ2}),-1.0]])]});}
            var Q180;
            {var subQ2=sQuery(id+"F0.wireOp",EDGE,"E15.0.1.55");Q180=makeQuery(id+"F0.imprint","IMPRINT",FACE,{"disambiguationData":[TD([[makeQuery(id+"F0.imprint","IMPRINT",EDGE,{"derivedFrom":subQ2}),1.0]])]});}
            var Q181;
            {var subQ0=sQuery(id+"F0.wireOp",EDGE,"E13.1.0.12");var subQ7=sQuery(id+"F0.wireOp",EDGE,"E13.1.0.5");var subQ9=makeQuery(id+"F0.imprint","INTERSECT",VERTEX,{"derivedFrom":[subQ7,subQ0]});Q181=makeQuery(id+"F0.imprint","IMPRINT",FACE,{"disambiguationData":[TD([[makeQuery(id+"F0.imprint","IMPRINT",EDGE,{"disambiguationData":[TD([[subQ9,1.0]])],"derivedFrom":subQ7}),-1.0]])]});}
            var Q182;
            Q182=makeQuery(id+"F0.imprint","IMPRINT",FACE,{"disambiguationData":[TD([[makeQuery(id+"F0.imprint","IMPRINT",EDGE,{"derivedFrom":sQuery(id+"F0.wireOp",EDGE,"E15.0.3.25")}),-1.0]])]});
            var Q183;
            {var subQ14=sQuery(id+"F0.wireOp",EDGE,"E15.0.4.25");Q183=makeQuery(id+"F0.imprint","IMPRINT",FACE,{"disambiguationData":[TD([[makeQuery(id+"F0.imprint","IMPRINT",EDGE,{"derivedFrom":subQ14}),-1.0]])]});}
            var Q184;
            {var subQ9=sQuery(id+"F0.wireOp",EDGE,"E15.0.4.109");Q184=makeQuery(id+"F0.imprint","IMPRINT",FACE,{"disambiguationData":[TD([[makeQuery(id+"F0.imprint","IMPRINT",EDGE,{"derivedFrom":subQ9}),1.0]])]});}
            var Q185;
            {var subQ3=sQuery(id+"F0.wireOp",EDGE,"E15.0.5.93");Q185=makeQuery(id+"F0.imprint","IMPRINT",FACE,{"disambiguationData":[TD([[makeQuery(id+"F0.imprint","IMPRINT",EDGE,{"derivedFrom":subQ3}),-1.0]])]});}
            var Q186;
            {var subQ3=sQuery(id+"F0.wireOp",EDGE,"E15.0.5.122");Q186=makeQuery(id+"F0.imprint","IMPRINT",FACE,{"disambiguationData":[TD([[makeQuery(id+"F0.imprint","IMPRINT",EDGE,{"derivedFrom":subQ3}),-1.0]])]});}
            var Q187;
            {var subQ1=sQuery(id+"F0.wireOp",EDGE,"E15.0.5.24");var subQ3=sQuery(id+"F0.wireOp",EDGE,"E18.2");var subQ4=makeQuery(id+"F0.imprint","INTERSECT",VERTEX,{"derivedFrom":[subQ1,subQ3]});Q187=makeQuery(id+"F0.imprint","IMPRINT",FACE,{"disambiguationData":[TD([[makeQuery(id+"F0.imprint","IMPRINT",EDGE,{"disambiguationData":[TD([[subQ4,-1.0]])],"derivedFrom":subQ3}),-1.0]])]});}
            var Q188;
            {var subQ1=sQuery(id+"F0.wireOp",EDGE,"E15.0.4.7");Q188=makeQuery(id+"F0.imprint","IMPRINT",FACE,{"disambiguationData":[TD([[makeQuery(id+"F0.imprint","IMPRINT",EDGE,{"derivedFrom":subQ1}),-1.0]])]});}
            var Q189;
            {var subQ2=sQuery(id+"F0.wireOp",EDGE,"E15.0.4.17");Q189=makeQuery(id+"F0.imprint","IMPRINT",FACE,{"disambiguationData":[TD([[makeQuery(id+"F0.imprint","IMPRINT",EDGE,{"derivedFrom":subQ2}),-1.0]])]});}
            var Q190;
            {var subQ3=sQuery(id+"F0.wireOp",EDGE,"E15.0.4.17");Q190=makeQuery(id+"F0.imprint","IMPRINT",FACE,{"disambiguationData":[TD([[makeQuery(id+"F0.imprint","IMPRINT",EDGE,{"derivedFrom":subQ3}),1.0]])]});}
            var Q191;
            {var subQ4=sQuery(id+"F0.wireOp",EDGE,"E15.0.4.20");Q191=makeQuery(id+"F0.imprint","IMPRINT",FACE,{"disambiguationData":[TD([[makeQuery(id+"F0.imprint","IMPRINT",EDGE,{"derivedFrom":subQ4}),1.0]])]});}
            var Q192;
            {var subQ4=sQuery(id+"F0.wireOp",EDGE,"E15.0.4.14");Q192=makeQuery(id+"F0.imprint","IMPRINT",FACE,{"disambiguationData":[TD([[makeQuery(id+"F0.imprint","IMPRINT",EDGE,{"derivedFrom":subQ4}),-1.0]])]});}
            var Q193;
            {var subQ1=sQuery(id+"F0.wireOp",EDGE,"E15.0.4.24");Q193=makeQuery(id+"F0.imprint","IMPRINT",FACE,{"disambiguationData":[TD([[makeQuery(id+"F0.imprint","IMPRINT",EDGE,{"derivedFrom":subQ1}),-1.0]])]});}
            var Q194;
            {var subQ4=sQuery(id+"F0.wireOp",EDGE,"E15.0.4.28");Q194=makeQuery(id+"F0.imprint","IMPRINT",FACE,{"disambiguationData":[TD([[makeQuery(id+"F0.imprint","IMPRINT",EDGE,{"derivedFrom":subQ4}),1.0]])]});}
            var Q195;
            {var subQ1=sQuery(id+"F0.wireOp",EDGE,"E15.0.4.11");Q195=makeQuery(id+"F0.imprint","IMPRINT",FACE,{"disambiguationData":[TD([[makeQuery(id+"F0.imprint","IMPRINT",EDGE,{"derivedFrom":subQ1}),-1.0]])]});}
            var Q196;
            {var subQ3=sQuery(id+"F0.wireOp",EDGE,"E15.0.4.21");Q196=makeQuery(id+"F0.imprint","IMPRINT",FACE,{"disambiguationData":[TD([[makeQuery(id+"F0.imprint","IMPRINT",EDGE,{"derivedFrom":subQ3}),-1.0]])]});}
            var Q197;
            {var subQ4=sQuery(id+"F0.wireOp",EDGE,"E15.0.3.11");Q197=makeQuery(id+"F0.imprint","IMPRINT",FACE,{"disambiguationData":[TD([[makeQuery(id+"F0.imprint","IMPRINT",EDGE,{"derivedFrom":subQ4}),-1.0]])]});}
            var Q198;
            {var subQ3=sQuery(id+"F0.wireOp",EDGE,"E15.0.3.24");Q198=makeQuery(id+"F0.imprint","IMPRINT",FACE,{"disambiguationData":[TD([[makeQuery(id+"F0.imprint","IMPRINT",EDGE,{"derivedFrom":subQ3}),-1.0]])]});}
            var Q199;
            {var subQ1=sQuery(id+"F0.wireOp",EDGE,"E15.0.5.14");Q199=makeQuery(id+"F0.imprint","IMPRINT",FACE,{"disambiguationData":[TD([[makeQuery(id+"F0.imprint","IMPRINT",EDGE,{"derivedFrom":subQ1}),-1.0]])]});}
            extrude(context, id + "F1", {"entities" : qUnion([Q0, Q1, Q2, Q3, Q4, Q5, Q6, Q7, Q8, Q9, Q10, Q11, Q12, Q13, Q14, Q15, Q16, Q17, Q18, Q19, Q20, Q21, Q22, Q23, Q24, Q25, Q26, Q27, Q28, Q29, Q30, Q31, Q32, Q33, Q34, Q35, Q36, Q37, Q38, Q39, Q40, Q41, Q42, Q43, Q44, Q45, Q46, Q47, Q48, Q49, Q50, Q51, Q52, Q53, Q54, Q55, Q56, Q57, Q58, Q59, Q60, Q61, Q62, Q63, Q64, Q65, Q66, Q67, Q68, Q69, Q70, Q71, Q72, Q73, Q74, Q75, Q76, Q77, Q78, Q79, Q80, Q81, Q82, Q83, Q84, Q85, Q86, Q87, Q88, Q89, Q90, Q91, Q92, Q93, Q94, Q95, Q96, Q97, Q98, Q99, Q100, Q101, Q102, Q103, Q104, Q105, Q106, Q107, Q108, Q109, Q110, Q111, Q112, Q113, Q114, Q115, Q116, Q117, Q118, Q119, Q120, Q121, Q122, Q123, Q124, Q125, Q126, Q127, Q128, Q129, Q130, Q131, Q132, Q133, Q134, Q135, Q136, Q137, Q138, Q139, Q140, Q141, Q142, Q143, Q144, Q145, Q146, Q147, Q148, Q149, Q150, Q151, Q152, Q153, Q154, Q155, Q156, Q157, Q158, Q159, Q160, Q161, Q162, Q163, Q164, Q165, Q166, Q167, Q168, Q169, Q170, Q171, Q172, Q173, Q174, Q175, Q176, Q177, Q178, Q179, Q180, Q181, Q182, Q183, Q184, Q185, Q186, Q187, Q188, Q189, Q190, Q191, Q192, Q193, Q194, Q195, Q196, Q197, Q198, Q199]), "depth" : 2 * mm, "offsetDistance" : 25 * mm});
        }
    });
